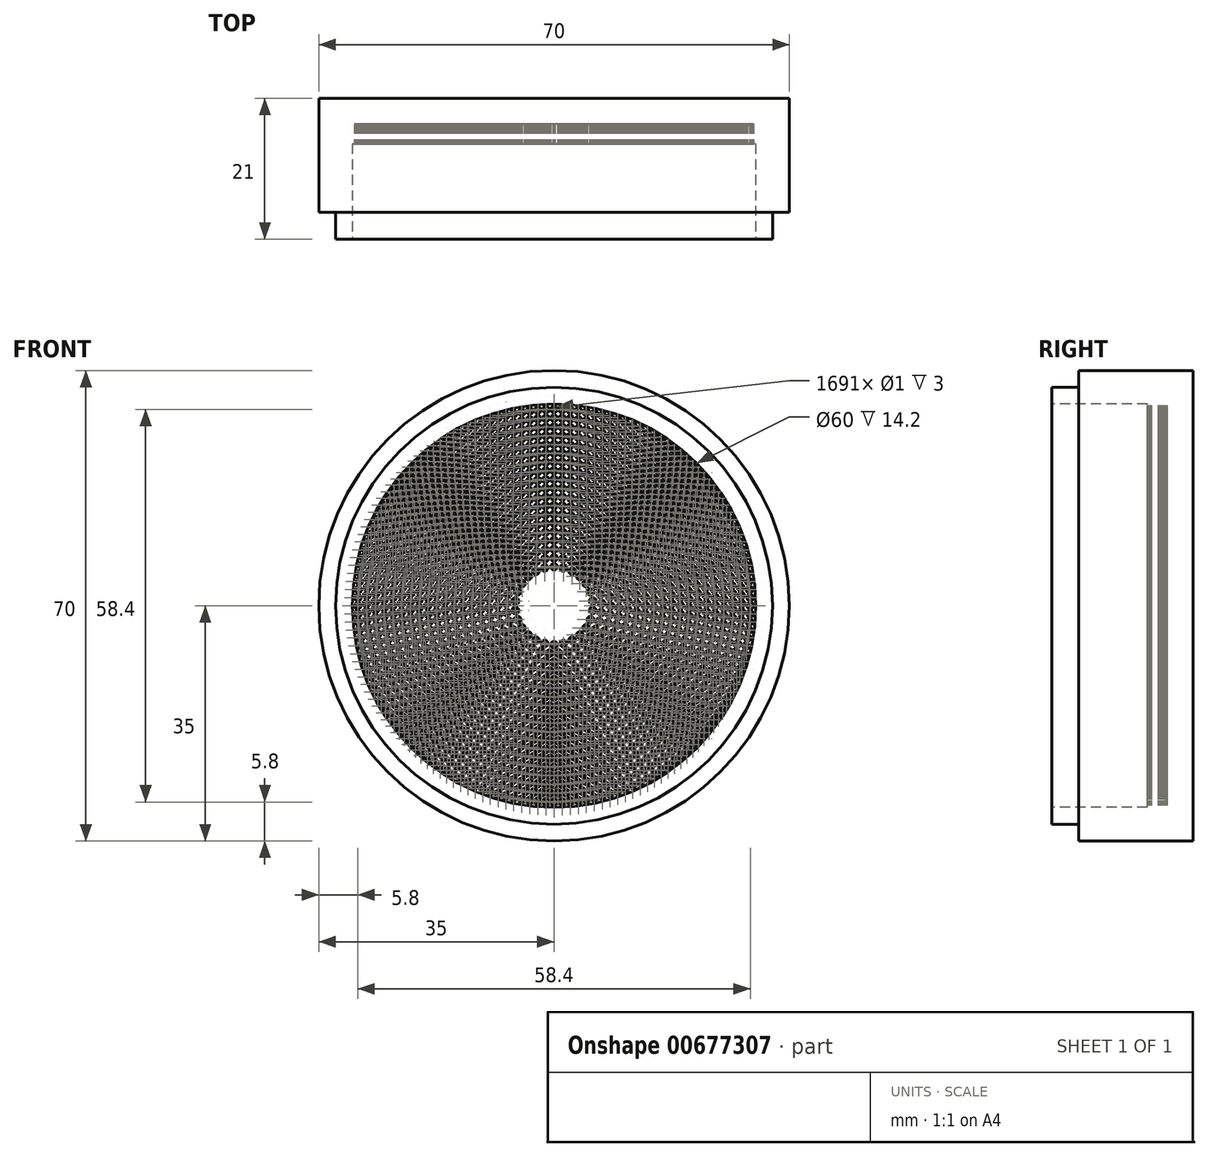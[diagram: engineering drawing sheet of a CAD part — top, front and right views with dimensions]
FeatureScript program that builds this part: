
annotation { "Feature Type Name" : "Feature", "Feature Type Description" : "" }
export const myFeature = defineFeature(function(context is Context, id is Id, definition is map)
    precondition{}
    {
        {
            var Q0;
            Q0=qCreatedBy(makeId("Front.planeOp"),FACE);
            var sketch = newSketch(context, id + "F0", { "sketchPlane" : qUnion([Q0])});
            skCircle(sketch, "E0", {"center": v(0, 0) * mm, "radius": 35 * mm});
            skSolve(sketch);
        }
        {
            var Q0;
            Q0=qSketchRegion(id+"F0",true);
            var Q1;
            Q1=makeQuery(id+"F0.imprint","IMPRINT",FACE,{"disambiguationData":[TD([[makeQuery(id+"F0.imprint","IMPRINT",EDGE,{"derivedFrom":sQuery(id+"F0.wireOp",EDGE,"E0")}),1.0]])]});
            extrude(context, id + "F1", {"entities" : qUnion([Q0, Q1]), "depth" : 21 * mm, "offsetDistance" : 25 * mm});
        }
        {
            var Q0;
            Q0=makeQuery(id+"F1.opExtrude","CAP_FACE",FACE,{"disambiguationData":[OSD([sQuery(id+"F0.wireOp",EDGE,"E0")])],"isStart":false});
            var sketch = newSketch(context, id + "F2", { "sketchPlane" : qUnion([Q0])});
            skCircle(sketch, "E1", {"center": v(0, 0) * mm, "radius": 30 * mm});
            skSolve(sketch);
        }
        {
            var Q0;
            Q0=qSketchRegion(id+"F2",true);
            var Q1;
            Q1=makeQuery(id+"F2.imprint","IMPRINT",FACE,{"disambiguationData":[TD([[makeQuery(id+"F2.imprint","IMPRINT",EDGE,{"derivedFrom":sQuery(id+"F2.wireOp",EDGE,"E1")}),1.0]])]});
            extrude(context, id + "F3", {"entities" : qUnion([Q0, Q1]), "operationType" : NewBodyOperationType.REMOVE, "oppositeDirection" : true, "depth" : 17 * mm, "offsetDistance" : 25 * mm});
        }
        {
            var Q0;
            Q0=makeQuery(id+"F1.opExtrude","CAP_FACE",FACE,{"disambiguationData":[OSD([sQuery(id+"F0.wireOp",EDGE,"E0")])],"isStart":false});
            var sketch = newSketch(context, id + "F4", { "sketchPlane" : qUnion([Q0])});
            skCircle(sketch, "E2", {"center": v(0, 0) * mm, "radius": 32.5 * mm});
            skSolve(sketch);
        }
        {
            var Q0;
            Q0=makeQuery(id+"F4.imprint","IMPRINT",FACE,{"disambiguationData":[TD([[makeQuery(id+"F4.imprint","IMPRINT",EDGE,{"derivedFrom":sQuery(id+"F4.wireOp",EDGE,"E2")}),-1.0]])]});
            extrude(context, id + "F5", {"entities" : qUnion([Q0]), "operationType" : NewBodyOperationType.REMOVE, "oppositeDirection" : true, "depth" : 4 * mm, "offsetDistance" : 25 * mm});
        }
        {
            var Q0;
            Q0=makeQuery(id+"F3.boolean.opBoolean","COPY",FACE,{"derivedFrom":makeQuery(id+"F3.opExtrude","CAP_FACE",FACE,{"disambiguationData":[OSD([sQuery(id+"F2.wireOp",EDGE,"E1")])],"isStart":false})});
            var sketch = newSketch(context, id + "F6", { "sketchPlane" : qUnion([Q0])});
            skLineSegment(sketch, "E3", {"start": v(0, 0) * mm, "end": v(0, 30) * mm, "construction": true});
            skCircle(sketch, "E4", {"center": v(0, 0) * mm, "radius": 5 * mm, "construction": true});
            skCircle(sketch, "E5", {"center": v(0, 5.8) * mm, "radius": 0.1 * mm});
            skLineSegment(sketch, "E6", {"start": v(0, 5) * mm, "end": v(-0.66, 5) * mm, "construction": true});
            skCircle(sketch, "E7", {"center": v(0, 7.1) * mm, "radius": 0.1 * mm});
            skCircle(sketch, "E8", {"center": v(0, 8.4) * mm, "radius": 0.1 * mm});
            skCircle(sketch, "E9", {"center": v(0, 9.7) * mm, "radius": 0.1 * mm});
            skCircle(sketch, "E10", {"center": v(0, 11) * mm, "radius": 0.1 * mm});
            skLineSegment(sketch, "E11", {"start": v(-1.23, 11.65) * mm, "end": v(1.24, 11.65) * mm, "construction": true});
            skCircle(sketch, "E12.MirrorC", {"center": v(0, 12.3) * mm, "radius": 0.1 * mm});
            skCircle(sketch, "E13.MirrorC", {"center": v(0, 13.6) * mm, "radius": 0.1 * mm});
            skCircle(sketch, "E14.MirrorC", {"center": v(0, 14.9) * mm, "radius": 0.1 * mm});
            skCircle(sketch, "E15.MirrorC", {"center": v(0, 16.2) * mm, "radius": 0.1 * mm});
            skCircle(sketch, "E16.MirrorC", {"center": v(0, 17.5) * mm, "radius": 0.1 * mm});
            skLineSegment(sketch, "E17", {"start": v(-0.97, 18.15) * mm, "end": v(1.04, 18.15) * mm, "construction": true});
            skCircle(sketch, "E18.MirrorC", {"center": v(0, 18.8) * mm, "radius": 0.1 * mm});
            skCircle(sketch, "E19.MirrorC", {"center": v(0, 20.1) * mm, "radius": 0.1 * mm});
            skCircle(sketch, "E20.MirrorC", {"center": v(0, 21.4) * mm, "radius": 0.1 * mm});
            skCircle(sketch, "E21.MirrorC", {"center": v(0, 22.7) * mm, "radius": 0.1 * mm});
            skCircle(sketch, "E22.MirrorC", {"center": v(0, 24) * mm, "radius": 0.1 * mm});
            skCircle(sketch, "E23.MirrorC", {"center": v(0, 25.3) * mm, "radius": 0.1 * mm});
            skCircle(sketch, "E24.MirrorC", {"center": v(0, 26.6) * mm, "radius": 0.1 * mm});
            skCircle(sketch, "E25.MirrorC", {"center": v(0, 27.9) * mm, "radius": 0.1 * mm});
            skCircle(sketch, "E26.MirrorC", {"center": v(0, 29.2) * mm, "radius": 0.1 * mm});
            skCircle(sketch, "E27.1.0", {"center": v(-1.39, 5.63) * mm, "radius": 0.1 * mm});
            skCircle(sketch, "E27.2.0", {"center": v(-2.7, 5.14) * mm, "radius": 0.1 * mm});
            skCircle(sketch, "E27.3.0", {"center": v(-3.85, 4.34) * mm, "radius": 0.1 * mm});
            skCircle(sketch, "E27.4.0", {"center": v(-4.77, 3.3) * mm, "radius": 0.1 * mm});
            skCircle(sketch, "E27.5.0", {"center": v(-5.42, 2.06) * mm, "radius": 0.1 * mm});
            skCircle(sketch, "E27.6.0", {"center": v(-5.76, 0.7) * mm, "radius": 0.1 * mm});
            skCircle(sketch, "E27.7.0", {"center": v(-5.76, -0.7) * mm, "radius": 0.1 * mm});
            skCircle(sketch, "E27.8.0", {"center": v(-5.42, -2.06) * mm, "radius": 0.1 * mm});
            skCircle(sketch, "E27.9.0", {"center": v(-4.77, -3.3) * mm, "radius": 0.1 * mm});
            skCircle(sketch, "E27.10.0", {"center": v(-3.85, -4.34) * mm, "radius": 0.1 * mm});
            skCircle(sketch, "E27.11.0", {"center": v(-2.7, -5.14) * mm, "radius": 0.1 * mm});
            skCircle(sketch, "E27.12.0", {"center": v(-1.39, -5.63) * mm, "radius": 0.1 * mm});
            skCircle(sketch, "E27.13.0", {"center": v(0, -5.8) * mm, "radius": 0.1 * mm});
            skCircle(sketch, "E27.14.0", {"center": v(1.39, -5.63) * mm, "radius": 0.1 * mm});
            skCircle(sketch, "E27.15.0", {"center": v(2.7, -5.14) * mm, "radius": 0.1 * mm});
            skCircle(sketch, "E27.16.0", {"center": v(3.85, -4.34) * mm, "radius": 0.1 * mm});
            skCircle(sketch, "E27.17.0", {"center": v(4.77, -3.3) * mm, "radius": 0.1 * mm});
            skCircle(sketch, "E27.18.0", {"center": v(5.42, -2.06) * mm, "radius": 0.1 * mm});
            skCircle(sketch, "E27.19.0", {"center": v(5.76, -0.7) * mm, "radius": 0.1 * mm});
            skCircle(sketch, "E27.20.0", {"center": v(5.76, 0.7) * mm, "radius": 0.1 * mm});
            skCircle(sketch, "E27.21.0", {"center": v(5.42, 2.06) * mm, "radius": 0.1 * mm});
            skCircle(sketch, "E27.22.0", {"center": v(4.77, 3.3) * mm, "radius": 0.1 * mm});
            skCircle(sketch, "E27.23.0", {"center": v(3.85, 4.34) * mm, "radius": 0.1 * mm});
            skCircle(sketch, "E27.24.0", {"center": v(2.7, 5.14) * mm, "radius": 0.1 * mm});
            skCircle(sketch, "E27.25.0", {"center": v(1.39, 5.63) * mm, "radius": 0.1 * mm});
            skCircle(sketch, "E28.1.0", {"center": v(-1.34, 6.97) * mm, "radius": 0.1 * mm});
            skCircle(sketch, "E28.2.0", {"center": v(-2.64, 6.6) * mm, "radius": 0.1 * mm});
            skCircle(sketch, "E28.3.0", {"center": v(-3.84, 5.97) * mm, "radius": 0.1 * mm});
            skCircle(sketch, "E28.4.0", {"center": v(-4.9, 5.14) * mm, "radius": 0.1 * mm});
            skCircle(sketch, "E28.5.0", {"center": v(-5.78, 4.12) * mm, "radius": 0.1 * mm});
            skCircle(sketch, "E28.6.0", {"center": v(-6.46, 2.95) * mm, "radius": 0.1 * mm});
            skCircle(sketch, "E28.7.0", {"center": v(-6.9, 1.67) * mm, "radius": 0.1 * mm});
            skCircle(sketch, "E28.8.0", {"center": v(-7.1, 0.34) * mm, "radius": 0.1 * mm});
            skCircle(sketch, "E28.9.0", {"center": v(-7.03, -1.01) * mm, "radius": 0.1 * mm});
            skCircle(sketch, "E28.10.0", {"center": v(-6.7, -2.32) * mm, "radius": 0.1 * mm});
            skCircle(sketch, "E28.11.0", {"center": v(-6.15, -3.55) * mm, "radius": 0.1 * mm});
            skCircle(sketch, "E28.12.0", {"center": v(-5.37, -4.65) * mm, "radius": 0.1 * mm});
            skCircle(sketch, "E28.13.0", {"center": v(-4.39, -5.58) * mm, "radius": 0.1 * mm});
            skCircle(sketch, "E28.14.0", {"center": v(-3.25, -6.31) * mm, "radius": 0.1 * mm});
            skCircle(sketch, "E28.15.0", {"center": v(-2, -6.81) * mm, "radius": 0.1 * mm});
            skCircle(sketch, "E28.16.0", {"center": v(-0.67, -7.07) * mm, "radius": 0.1 * mm});
            skCircle(sketch, "E28.17.0", {"center": v(0.67, -7.07) * mm, "radius": 0.1 * mm});
            skCircle(sketch, "E28.18.0", {"center": v(2, -6.81) * mm, "radius": 0.1 * mm});
            skCircle(sketch, "E28.19.0", {"center": v(3.25, -6.31) * mm, "radius": 0.1 * mm});
            skCircle(sketch, "E28.20.0", {"center": v(4.39, -5.58) * mm, "radius": 0.1 * mm});
            skCircle(sketch, "E28.21.0", {"center": v(5.37, -4.65) * mm, "radius": 0.1 * mm});
            skCircle(sketch, "E28.22.0", {"center": v(6.15, -3.55) * mm, "radius": 0.1 * mm});
            skCircle(sketch, "E28.23.0", {"center": v(6.7, -2.32) * mm, "radius": 0.1 * mm});
            skCircle(sketch, "E28.24.0", {"center": v(7.03, -1.01) * mm, "radius": 0.1 * mm});
            skCircle(sketch, "E28.25.0", {"center": v(7.1, 0.34) * mm, "radius": 0.1 * mm});
            skCircle(sketch, "E28.26.0", {"center": v(6.9, 1.67) * mm, "radius": 0.1 * mm});
            skCircle(sketch, "E28.27.0", {"center": v(6.46, 2.95) * mm, "radius": 0.1 * mm});
            skCircle(sketch, "E28.28.0", {"center": v(5.78, 4.12) * mm, "radius": 0.1 * mm});
            skCircle(sketch, "E28.29.0", {"center": v(4.9, 5.14) * mm, "radius": 0.1 * mm});
            skCircle(sketch, "E28.30.0", {"center": v(3.84, 5.97) * mm, "radius": 0.1 * mm});
            skCircle(sketch, "E28.31.0", {"center": v(2.64, 6.6) * mm, "radius": 0.1 * mm});
            skCircle(sketch, "E28.32.0", {"center": v(1.34, 6.97) * mm, "radius": 0.1 * mm});
            skCircle(sketch, "E29.1.0", {"center": v(-1.31, 8.3) * mm, "radius": 0.1 * mm});
            skCircle(sketch, "E29.2.0", {"center": v(-2.6, 7.99) * mm, "radius": 0.1 * mm});
            skCircle(sketch, "E29.3.0", {"center": v(-3.81, 7.48) * mm, "radius": 0.1 * mm});
            skCircle(sketch, "E29.4.0", {"center": v(-4.94, 6.8) * mm, "radius": 0.1 * mm});
            skCircle(sketch, "E29.5.0", {"center": v(-5.94, 5.94) * mm, "radius": 0.1 * mm});
            skCircle(sketch, "E29.6.0", {"center": v(-6.8, 4.94) * mm, "radius": 0.1 * mm});
            skCircle(sketch, "E29.7.0", {"center": v(-7.48, 3.81) * mm, "radius": 0.1 * mm});
            skCircle(sketch, "E29.8.0", {"center": v(-7.99, 2.6) * mm, "radius": 0.1 * mm});
            skCircle(sketch, "E29.9.0", {"center": v(-8.3, 1.31) * mm, "radius": 0.1 * mm});
            skCircle(sketch, "E29.10.0", {"center": v(-8.4, 0) * mm, "radius": 0.1 * mm});
            skCircle(sketch, "E29.11.0", {"center": v(-8.3, -1.31) * mm, "radius": 0.1 * mm});
            skCircle(sketch, "E29.12.0", {"center": v(-7.99, -2.6) * mm, "radius": 0.1 * mm});
            skCircle(sketch, "E29.13.0", {"center": v(-7.48, -3.81) * mm, "radius": 0.1 * mm});
            skCircle(sketch, "E29.14.0", {"center": v(-6.8, -4.94) * mm, "radius": 0.1 * mm});
            skCircle(sketch, "E29.15.0", {"center": v(-5.94, -5.94) * mm, "radius": 0.1 * mm});
            skCircle(sketch, "E29.16.0", {"center": v(-4.94, -6.8) * mm, "radius": 0.1 * mm});
            skCircle(sketch, "E29.17.0", {"center": v(-3.81, -7.48) * mm, "radius": 0.1 * mm});
            skCircle(sketch, "E29.18.0", {"center": v(-2.6, -7.99) * mm, "radius": 0.1 * mm});
            skCircle(sketch, "E29.19.0", {"center": v(-1.31, -8.3) * mm, "radius": 0.1 * mm});
            skCircle(sketch, "E29.20.0", {"center": v(0, -8.4) * mm, "radius": 0.1 * mm});
            skCircle(sketch, "E29.21.0", {"center": v(1.31, -8.3) * mm, "radius": 0.1 * mm});
            skCircle(sketch, "E29.22.0", {"center": v(2.6, -7.99) * mm, "radius": 0.1 * mm});
            skCircle(sketch, "E29.23.0", {"center": v(3.81, -7.48) * mm, "radius": 0.1 * mm});
            skCircle(sketch, "E29.24.0", {"center": v(4.94, -6.8) * mm, "radius": 0.1 * mm});
            skCircle(sketch, "E29.25.0", {"center": v(5.94, -5.94) * mm, "radius": 0.1 * mm});
            skCircle(sketch, "E29.26.0", {"center": v(6.8, -4.94) * mm, "radius": 0.1 * mm});
            skCircle(sketch, "E29.27.0", {"center": v(7.48, -3.81) * mm, "radius": 0.1 * mm});
            skCircle(sketch, "E29.28.0", {"center": v(7.99, -2.6) * mm, "radius": 0.1 * mm});
            skCircle(sketch, "E29.29.0", {"center": v(8.3, -1.31) * mm, "radius": 0.1 * mm});
            skCircle(sketch, "E29.30.0", {"center": v(8.4, 0) * mm, "radius": 0.1 * mm});
            skCircle(sketch, "E29.31.0", {"center": v(8.3, 1.31) * mm, "radius": 0.1 * mm});
            skCircle(sketch, "E29.32.0", {"center": v(7.99, 2.6) * mm, "radius": 0.1 * mm});
            skCircle(sketch, "E29.33.0", {"center": v(7.48, 3.81) * mm, "radius": 0.1 * mm});
            skCircle(sketch, "E29.34.0", {"center": v(6.8, 4.94) * mm, "radius": 0.1 * mm});
            skCircle(sketch, "E29.35.0", {"center": v(5.94, 5.94) * mm, "radius": 0.1 * mm});
            skCircle(sketch, "E29.36.0", {"center": v(4.94, 6.8) * mm, "radius": 0.1 * mm});
            skCircle(sketch, "E29.37.0", {"center": v(3.81, 7.48) * mm, "radius": 0.1 * mm});
            skCircle(sketch, "E29.38.0", {"center": v(2.6, 7.99) * mm, "radius": 0.1 * mm});
            skCircle(sketch, "E29.39.0", {"center": v(1.31, 8.3) * mm, "radius": 0.1 * mm});
            skCircle(sketch, "E30.1.0", {"center": v(-1.3, 9.61) * mm, "radius": 0.1 * mm});
            skCircle(sketch, "E30.2.0", {"center": v(-2.56, 9.36) * mm, "radius": 0.1 * mm});
            skCircle(sketch, "E30.3.0", {"center": v(-3.79, 8.93) * mm, "radius": 0.1 * mm});
            skCircle(sketch, "E30.4.0", {"center": v(-4.94, 8.35) * mm, "radius": 0.1 * mm});
            skCircle(sketch, "E30.5.0", {"center": v(-6.01, 7.61) * mm, "radius": 0.1 * mm});
            skCircle(sketch, "E30.6.0", {"center": v(-6.97, 6.74) * mm, "radius": 0.1 * mm});
            skCircle(sketch, "E30.7.0", {"center": v(-7.8, 5.75) * mm, "radius": 0.1 * mm});
            skCircle(sketch, "E30.8.0", {"center": v(-8.5, 4.66) * mm, "radius": 0.1 * mm});
            skCircle(sketch, "E30.9.0", {"center": v(-9.05, 3.49) * mm, "radius": 0.1 * mm});
            skCircle(sketch, "E30.10.0", {"center": v(-9.44, 2.25) * mm, "radius": 0.1 * mm});
            skCircle(sketch, "E30.11.0", {"center": v(-9.65, 0.97) * mm, "radius": 0.1 * mm});
            skCircle(sketch, "E30.12.0", {"center": v(-9.7, -0.32) * mm, "radius": 0.1 * mm});
            skCircle(sketch, "E30.13.0", {"center": v(-9.56, -1.61) * mm, "radius": 0.1 * mm});
            skCircle(sketch, "E30.14.0", {"center": v(-9.26, -2.87) * mm, "radius": 0.1 * mm});
            skCircle(sketch, "E30.15.0", {"center": v(-8.8, -4.08) * mm, "radius": 0.1 * mm});
            skCircle(sketch, "E30.16.0", {"center": v(-8.18, -5.22) * mm, "radius": 0.1 * mm});
            skCircle(sketch, "E30.17.0", {"center": v(-7.4, -6.26) * mm, "radius": 0.1 * mm});
            skCircle(sketch, "E30.18.0", {"center": v(-6.5, -7.2) * mm, "radius": 0.1 * mm});
            skCircle(sketch, "E30.19.0", {"center": v(-5.49, -8) * mm, "radius": 0.1 * mm});
            skCircle(sketch, "E30.20.0", {"center": v(-4.37, -8.66) * mm, "radius": 0.1 * mm});
            skCircle(sketch, "E30.21.0", {"center": v(-3.18, -9.16) * mm, "radius": 0.1 * mm});
            skCircle(sketch, "E30.22.0", {"center": v(-1.93, -9.5) * mm, "radius": 0.1 * mm});
            skCircle(sketch, "E30.23.0", {"center": v(-0.65, -9.68) * mm, "radius": 0.1 * mm});
            skCircle(sketch, "E30.24.0", {"center": v(0.65, -9.68) * mm, "radius": 0.1 * mm});
            skCircle(sketch, "E30.25.0", {"center": v(1.93, -9.5) * mm, "radius": 0.1 * mm});
            skCircle(sketch, "E30.26.0", {"center": v(3.18, -9.16) * mm, "radius": 0.1 * mm});
            skCircle(sketch, "E30.27.0", {"center": v(4.37, -8.66) * mm, "radius": 0.1 * mm});
            skCircle(sketch, "E30.28.0", {"center": v(5.49, -8) * mm, "radius": 0.1 * mm});
            skCircle(sketch, "E30.29.0", {"center": v(6.5, -7.2) * mm, "radius": 0.1 * mm});
            skCircle(sketch, "E30.30.0", {"center": v(7.4, -6.26) * mm, "radius": 0.1 * mm});
            skCircle(sketch, "E30.31.0", {"center": v(8.18, -5.22) * mm, "radius": 0.1 * mm});
            skCircle(sketch, "E30.32.0", {"center": v(8.8, -4.08) * mm, "radius": 0.1 * mm});
            skCircle(sketch, "E30.33.0", {"center": v(9.26, -2.87) * mm, "radius": 0.1 * mm});
            skCircle(sketch, "E30.34.0", {"center": v(9.56, -1.61) * mm, "radius": 0.1 * mm});
            skCircle(sketch, "E30.35.0", {"center": v(9.7, -0.32) * mm, "radius": 0.1 * mm});
            skCircle(sketch, "E30.36.0", {"center": v(9.65, 0.97) * mm, "radius": 0.1 * mm});
            skCircle(sketch, "E30.37.0", {"center": v(9.44, 2.25) * mm, "radius": 0.1 * mm});
            skCircle(sketch, "E30.38.0", {"center": v(9.05, 3.49) * mm, "radius": 0.1 * mm});
            skCircle(sketch, "E30.39.0", {"center": v(8.5, 4.66) * mm, "radius": 0.1 * mm});
            skCircle(sketch, "E30.40.0", {"center": v(7.8, 5.75) * mm, "radius": 0.1 * mm});
            skCircle(sketch, "E30.41.0", {"center": v(6.97, 6.74) * mm, "radius": 0.1 * mm});
            skCircle(sketch, "E30.42.0", {"center": v(6.01, 7.61) * mm, "radius": 0.1 * mm});
            skCircle(sketch, "E30.43.0", {"center": v(4.94, 8.35) * mm, "radius": 0.1 * mm});
            skCircle(sketch, "E30.44.0", {"center": v(3.79, 8.93) * mm, "radius": 0.1 * mm});
            skCircle(sketch, "E30.45.0", {"center": v(2.56, 9.36) * mm, "radius": 0.1 * mm});
            skCircle(sketch, "E30.46.0", {"center": v(1.3, 9.61) * mm, "radius": 0.1 * mm});
            skCircle(sketch, "E31.1.0", {"center": v(-1.28, 10.93) * mm, "radius": 0.1 * mm});
            skCircle(sketch, "E31.2.0", {"center": v(-2.54, 10.7) * mm, "radius": 0.1 * mm});
            skCircle(sketch, "E31.3.0", {"center": v(-3.76, 10.34) * mm, "radius": 0.1 * mm});
            skCircle(sketch, "E31.4.0", {"center": v(-4.94, 9.83) * mm, "radius": 0.1 * mm});
            skCircle(sketch, "E31.5.0", {"center": v(-6.04, 9.2) * mm, "radius": 0.1 * mm});
            skCircle(sketch, "E31.6.0", {"center": v(-7.07, 8.43) * mm, "radius": 0.1 * mm});
            skCircle(sketch, "E31.7.0", {"center": v(-8, 7.55) * mm, "radius": 0.1 * mm});
            skCircle(sketch, "E31.8.0", {"center": v(-8.82, 6.57) * mm, "radius": 0.1 * mm});
            skCircle(sketch, "E31.9.0", {"center": v(-9.53, 5.5) * mm, "radius": 0.1 * mm});
            skCircle(sketch, "E31.10.0", {"center": v(-10.1, 4.36) * mm, "radius": 0.1 * mm});
            skCircle(sketch, "E31.11.0", {"center": v(-10.54, 3.15) * mm, "radius": 0.1 * mm});
            skCircle(sketch, "E31.12.0", {"center": v(-10.83, 1.91) * mm, "radius": 0.1 * mm});
            skCircle(sketch, "E31.13.0", {"center": v(-10.98, 0.64) * mm, "radius": 0.1 * mm});
            skCircle(sketch, "E31.14.0", {"center": v(-10.98, -0.64) * mm, "radius": 0.1 * mm});
            skCircle(sketch, "E31.15.0", {"center": v(-10.83, -1.91) * mm, "radius": 0.1 * mm});
            skCircle(sketch, "E31.16.0", {"center": v(-10.54, -3.15) * mm, "radius": 0.1 * mm});
            skCircle(sketch, "E31.17.0", {"center": v(-10.1, -4.36) * mm, "radius": 0.1 * mm});
            skCircle(sketch, "E31.18.0", {"center": v(-9.53, -5.5) * mm, "radius": 0.1 * mm});
            skCircle(sketch, "E31.19.0", {"center": v(-8.82, -6.57) * mm, "radius": 0.1 * mm});
            skCircle(sketch, "E31.20.0", {"center": v(-8, -7.55) * mm, "radius": 0.1 * mm});
            skCircle(sketch, "E31.21.0", {"center": v(-7.07, -8.43) * mm, "radius": 0.1 * mm});
            skCircle(sketch, "E31.22.0", {"center": v(-6.04, -9.2) * mm, "radius": 0.1 * mm});
            skCircle(sketch, "E31.23.0", {"center": v(-4.94, -9.83) * mm, "radius": 0.1 * mm});
            skCircle(sketch, "E31.24.0", {"center": v(-3.76, -10.34) * mm, "radius": 0.1 * mm});
            skCircle(sketch, "E31.25.0", {"center": v(-2.54, -10.7) * mm, "radius": 0.1 * mm});
            skCircle(sketch, "E31.26.0", {"center": v(-1.28, -10.93) * mm, "radius": 0.1 * mm});
            skCircle(sketch, "E31.27.0", {"center": v(0, -11) * mm, "radius": 0.1 * mm});
            skCircle(sketch, "E31.28.0", {"center": v(1.28, -10.93) * mm, "radius": 0.1 * mm});
            skCircle(sketch, "E31.29.0", {"center": v(2.54, -10.7) * mm, "radius": 0.1 * mm});
            skCircle(sketch, "E31.30.0", {"center": v(3.76, -10.34) * mm, "radius": 0.1 * mm});
            skCircle(sketch, "E31.31.0", {"center": v(4.94, -9.83) * mm, "radius": 0.1 * mm});
            skCircle(sketch, "E31.32.0", {"center": v(6.04, -9.2) * mm, "radius": 0.1 * mm});
            skCircle(sketch, "E31.33.0", {"center": v(7.07, -8.43) * mm, "radius": 0.1 * mm});
            skCircle(sketch, "E31.34.0", {"center": v(8, -7.55) * mm, "radius": 0.1 * mm});
            skCircle(sketch, "E31.35.0", {"center": v(8.82, -6.57) * mm, "radius": 0.1 * mm});
            skCircle(sketch, "E31.36.0", {"center": v(9.53, -5.5) * mm, "radius": 0.1 * mm});
            skCircle(sketch, "E31.37.0", {"center": v(10.1, -4.36) * mm, "radius": 0.1 * mm});
            skCircle(sketch, "E31.38.0", {"center": v(10.54, -3.15) * mm, "radius": 0.1 * mm});
            skCircle(sketch, "E31.39.0", {"center": v(10.83, -1.91) * mm, "radius": 0.1 * mm});
            skCircle(sketch, "E31.40.0", {"center": v(10.98, -0.64) * mm, "radius": 0.1 * mm});
            skCircle(sketch, "E31.41.0", {"center": v(10.98, 0.64) * mm, "radius": 0.1 * mm});
            skCircle(sketch, "E31.42.0", {"center": v(10.83, 1.91) * mm, "radius": 0.1 * mm});
            skCircle(sketch, "E31.43.0", {"center": v(10.54, 3.15) * mm, "radius": 0.1 * mm});
            skCircle(sketch, "E31.44.0", {"center": v(10.1, 4.36) * mm, "radius": 0.1 * mm});
            skCircle(sketch, "E31.45.0", {"center": v(9.53, 5.5) * mm, "radius": 0.1 * mm});
            skCircle(sketch, "E31.46.0", {"center": v(8.82, 6.57) * mm, "radius": 0.1 * mm});
            skCircle(sketch, "E31.47.0", {"center": v(8, 7.55) * mm, "radius": 0.1 * mm});
            skCircle(sketch, "E31.48.0", {"center": v(7.07, 8.43) * mm, "radius": 0.1 * mm});
            skCircle(sketch, "E31.49.0", {"center": v(6.04, 9.2) * mm, "radius": 0.1 * mm});
            skCircle(sketch, "E31.50.0", {"center": v(4.94, 9.83) * mm, "radius": 0.1 * mm});
            skCircle(sketch, "E31.51.0", {"center": v(3.76, 10.34) * mm, "radius": 0.1 * mm});
            skCircle(sketch, "E31.52.0", {"center": v(2.54, 10.7) * mm, "radius": 0.1 * mm});
            skCircle(sketch, "E31.53.0", {"center": v(1.28, 10.93) * mm, "radius": 0.1 * mm});
            skCircle(sketch, "E32.1.0", {"center": v(-1.26, 12.23) * mm, "radius": 0.1 * mm});
            skCircle(sketch, "E32.2.0", {"center": v(-2.52, 12.04) * mm, "radius": 0.1 * mm});
            skCircle(sketch, "E32.3.0", {"center": v(-3.74, 11.72) * mm, "radius": 0.1 * mm});
            skCircle(sketch, "E32.4.0", {"center": v(-4.93, 11.27) * mm, "radius": 0.1 * mm});
            skCircle(sketch, "E32.5.0", {"center": v(-6.06, 10.7) * mm, "radius": 0.1 * mm});
            skCircle(sketch, "E32.6.0", {"center": v(-7.13, 10.02) * mm, "radius": 0.1 * mm});
            skCircle(sketch, "E32.7.0", {"center": v(-8.12, 9.24) * mm, "radius": 0.1 * mm});
            skCircle(sketch, "E32.8.0", {"center": v(-9.03, 8.36) * mm, "radius": 0.1 * mm});
            skCircle(sketch, "E32.9.0", {"center": v(-9.84, 7.38) * mm, "radius": 0.1 * mm});
            skCircle(sketch, "E32.10.0", {"center": v(-10.54, 6.33) * mm, "radius": 0.1 * mm});
            skCircle(sketch, "E32.11.0", {"center": v(-11.14, 5.21) * mm, "radius": 0.1 * mm});
            skCircle(sketch, "E32.12.0", {"center": v(-11.62, 4.04) * mm, "radius": 0.1 * mm});
            skCircle(sketch, "E32.13.0", {"center": v(-11.97, 2.83) * mm, "radius": 0.1 * mm});
            skCircle(sketch, "E32.14.0", {"center": v(-12.2, 1.58) * mm, "radius": 0.1 * mm});
            skCircle(sketch, "E32.15.0", {"center": v(-12.3, 0.32) * mm, "radius": 0.1 * mm});
            skCircle(sketch, "E32.16.0", {"center": v(-12.26, -0.95) * mm, "radius": 0.1 * mm});
            skCircle(sketch, "E32.17.0", {"center": v(-12.1, -2.2) * mm, "radius": 0.1 * mm});
            skCircle(sketch, "E32.18.0", {"center": v(-11.8, -3.44) * mm, "radius": 0.1 * mm});
            skCircle(sketch, "E32.19.0", {"center": v(-11.4, -4.63) * mm, "radius": 0.1 * mm});
            skCircle(sketch, "E32.20.0", {"center": v(-10.86, -5.78) * mm, "radius": 0.1 * mm});
            skCircle(sketch, "E32.21.0", {"center": v(-10.2, -6.87) * mm, "radius": 0.1 * mm});
            skCircle(sketch, "E32.22.0", {"center": v(-9.44, -7.88) * mm, "radius": 0.1 * mm});
            skCircle(sketch, "E32.23.0", {"center": v(-8.58, -8.8) * mm, "radius": 0.1 * mm});
            skCircle(sketch, "E32.24.0", {"center": v(-7.63, -9.64) * mm, "radius": 0.1 * mm});
            skCircle(sketch, "E32.25.0", {"center": v(-6.6, -10.38) * mm, "radius": 0.1 * mm});
            skCircle(sketch, "E32.26.0", {"center": v(-5.5, -11) * mm, "radius": 0.1 * mm});
            skCircle(sketch, "E32.27.0", {"center": v(-4.34, -11.5) * mm, "radius": 0.1 * mm});
            skCircle(sketch, "E32.28.0", {"center": v(-3.13, -11.9) * mm, "radius": 0.1 * mm});
            skCircle(sketch, "E32.29.0", {"center": v(-1.9, -12.15) * mm, "radius": 0.1 * mm});
            skCircle(sketch, "E32.30.0", {"center": v(-0.63, -12.28) * mm, "radius": 0.1 * mm});
            skCircle(sketch, "E32.31.0", {"center": v(0.63, -12.28) * mm, "radius": 0.1 * mm});
            skCircle(sketch, "E32.32.0", {"center": v(1.9, -12.15) * mm, "radius": 0.1 * mm});
            skCircle(sketch, "E32.33.0", {"center": v(3.13, -11.9) * mm, "radius": 0.1 * mm});
            skCircle(sketch, "E32.34.0", {"center": v(4.34, -11.5) * mm, "radius": 0.1 * mm});
            skCircle(sketch, "E32.35.0", {"center": v(5.5, -11) * mm, "radius": 0.1 * mm});
            skCircle(sketch, "E32.36.0", {"center": v(6.6, -10.38) * mm, "radius": 0.1 * mm});
            skCircle(sketch, "E32.37.0", {"center": v(7.63, -9.64) * mm, "radius": 0.1 * mm});
            skCircle(sketch, "E32.38.0", {"center": v(8.58, -8.8) * mm, "radius": 0.1 * mm});
            skCircle(sketch, "E32.39.0", {"center": v(9.44, -7.88) * mm, "radius": 0.1 * mm});
            skCircle(sketch, "E32.40.0", {"center": v(10.2, -6.87) * mm, "radius": 0.1 * mm});
            skCircle(sketch, "E32.41.0", {"center": v(10.86, -5.78) * mm, "radius": 0.1 * mm});
            skCircle(sketch, "E32.42.0", {"center": v(11.4, -4.63) * mm, "radius": 0.1 * mm});
            skCircle(sketch, "E32.43.0", {"center": v(11.8, -3.44) * mm, "radius": 0.1 * mm});
            skCircle(sketch, "E32.44.0", {"center": v(12.1, -2.2) * mm, "radius": 0.1 * mm});
            skCircle(sketch, "E32.45.0", {"center": v(12.26, -0.95) * mm, "radius": 0.1 * mm});
            skCircle(sketch, "E32.46.0", {"center": v(12.3, 0.32) * mm, "radius": 0.1 * mm});
            skCircle(sketch, "E32.47.0", {"center": v(12.2, 1.58) * mm, "radius": 0.1 * mm});
            skCircle(sketch, "E32.48.0", {"center": v(11.97, 2.83) * mm, "radius": 0.1 * mm});
            skCircle(sketch, "E32.49.0", {"center": v(11.62, 4.04) * mm, "radius": 0.1 * mm});
            skCircle(sketch, "E32.50.0", {"center": v(11.14, 5.21) * mm, "radius": 0.1 * mm});
            skCircle(sketch, "E32.51.0", {"center": v(10.54, 6.33) * mm, "radius": 0.1 * mm});
            skCircle(sketch, "E32.52.0", {"center": v(9.84, 7.38) * mm, "radius": 0.1 * mm});
            skCircle(sketch, "E32.53.0", {"center": v(9.03, 8.36) * mm, "radius": 0.1 * mm});
            skCircle(sketch, "E32.54.0", {"center": v(8.12, 9.24) * mm, "radius": 0.1 * mm});
            skCircle(sketch, "E32.55.0", {"center": v(7.13, 10.02) * mm, "radius": 0.1 * mm});
            skCircle(sketch, "E32.56.0", {"center": v(6.06, 10.7) * mm, "radius": 0.1 * mm});
            skCircle(sketch, "E32.57.0", {"center": v(4.93, 11.27) * mm, "radius": 0.1 * mm});
            skCircle(sketch, "E32.58.0", {"center": v(3.74, 11.72) * mm, "radius": 0.1 * mm});
            skCircle(sketch, "E32.59.0", {"center": v(2.52, 12.04) * mm, "radius": 0.1 * mm});
            skCircle(sketch, "E32.60.0", {"center": v(1.26, 12.23) * mm, "radius": 0.1 * mm});
            skCircle(sketch, "E33.1.0", {"center": v(-1.25, 13.54) * mm, "radius": 0.1 * mm});
            skCircle(sketch, "E33.2.0", {"center": v(-2.5, 13.37) * mm, "radius": 0.1 * mm});
            skCircle(sketch, "E33.3.0", {"center": v(-3.72, 13.08) * mm, "radius": 0.1 * mm});
            skCircle(sketch, "E33.4.0", {"center": v(-4.91, 12.68) * mm, "radius": 0.1 * mm});
            skCircle(sketch, "E33.5.0", {"center": v(-6.06, 12.17) * mm, "radius": 0.1 * mm});
            skCircle(sketch, "E33.6.0", {"center": v(-7.16, 11.56) * mm, "radius": 0.1 * mm});
            skCircle(sketch, "E33.7.0", {"center": v(-8.2, 10.85) * mm, "radius": 0.1 * mm});
            skCircle(sketch, "E33.8.0", {"center": v(-9.16, 10.05) * mm, "radius": 0.1 * mm});
            skCircle(sketch, "E33.9.0", {"center": v(-10.05, 9.16) * mm, "radius": 0.1 * mm});
            skCircle(sketch, "E33.10.0", {"center": v(-10.85, 8.2) * mm, "radius": 0.1 * mm});
            skCircle(sketch, "E33.11.0", {"center": v(-11.56, 7.16) * mm, "radius": 0.1 * mm});
            skCircle(sketch, "E33.12.0", {"center": v(-12.17, 6.06) * mm, "radius": 0.1 * mm});
            skCircle(sketch, "E33.13.0", {"center": v(-12.68, 4.91) * mm, "radius": 0.1 * mm});
            skCircle(sketch, "E33.14.0", {"center": v(-13.08, 3.72) * mm, "radius": 0.1 * mm});
            skCircle(sketch, "E33.15.0", {"center": v(-13.37, 2.5) * mm, "radius": 0.1 * mm});
            skCircle(sketch, "E33.16.0", {"center": v(-13.54, 1.25) * mm, "radius": 0.1 * mm});
            skCircle(sketch, "E33.17.0", {"center": v(-13.6, 0) * mm, "radius": 0.1 * mm});
            skCircle(sketch, "E33.18.0", {"center": v(-13.54, -1.25) * mm, "radius": 0.1 * mm});
            skCircle(sketch, "E33.19.0", {"center": v(-13.37, -2.5) * mm, "radius": 0.1 * mm});
            skCircle(sketch, "E33.20.0", {"center": v(-13.08, -3.72) * mm, "radius": 0.1 * mm});
            skCircle(sketch, "E33.21.0", {"center": v(-12.68, -4.91) * mm, "radius": 0.1 * mm});
            skCircle(sketch, "E33.22.0", {"center": v(-12.17, -6.06) * mm, "radius": 0.1 * mm});
            skCircle(sketch, "E33.23.0", {"center": v(-11.56, -7.16) * mm, "radius": 0.1 * mm});
            skCircle(sketch, "E33.24.0", {"center": v(-10.85, -8.2) * mm, "radius": 0.1 * mm});
            skCircle(sketch, "E33.25.0", {"center": v(-10.05, -9.16) * mm, "radius": 0.1 * mm});
            skCircle(sketch, "E33.26.0", {"center": v(-9.16, -10.05) * mm, "radius": 0.1 * mm});
            skCircle(sketch, "E33.27.0", {"center": v(-8.2, -10.85) * mm, "radius": 0.1 * mm});
            skCircle(sketch, "E33.28.0", {"center": v(-7.16, -11.56) * mm, "radius": 0.1 * mm});
            skCircle(sketch, "E33.29.0", {"center": v(-6.06, -12.17) * mm, "radius": 0.1 * mm});
            skCircle(sketch, "E33.30.0", {"center": v(-4.91, -12.68) * mm, "radius": 0.1 * mm});
            skCircle(sketch, "E33.31.0", {"center": v(-3.72, -13.08) * mm, "radius": 0.1 * mm});
            skCircle(sketch, "E33.32.0", {"center": v(-2.5, -13.37) * mm, "radius": 0.1 * mm});
            skCircle(sketch, "E33.33.0", {"center": v(-1.25, -13.54) * mm, "radius": 0.1 * mm});
            skCircle(sketch, "E33.34.0", {"center": v(0, -13.6) * mm, "radius": 0.1 * mm});
            skCircle(sketch, "E33.35.0", {"center": v(1.25, -13.54) * mm, "radius": 0.1 * mm});
            skCircle(sketch, "E33.36.0", {"center": v(2.5, -13.37) * mm, "radius": 0.1 * mm});
            skCircle(sketch, "E33.37.0", {"center": v(3.72, -13.08) * mm, "radius": 0.1 * mm});
            skCircle(sketch, "E33.38.0", {"center": v(4.91, -12.68) * mm, "radius": 0.1 * mm});
            skCircle(sketch, "E33.39.0", {"center": v(6.06, -12.17) * mm, "radius": 0.1 * mm});
            skCircle(sketch, "E33.40.0", {"center": v(7.16, -11.56) * mm, "radius": 0.1 * mm});
            skCircle(sketch, "E33.41.0", {"center": v(8.2, -10.85) * mm, "radius": 0.1 * mm});
            skCircle(sketch, "E33.42.0", {"center": v(9.16, -10.05) * mm, "radius": 0.1 * mm});
            skCircle(sketch, "E33.43.0", {"center": v(10.05, -9.16) * mm, "radius": 0.1 * mm});
            skCircle(sketch, "E33.44.0", {"center": v(10.85, -8.2) * mm, "radius": 0.1 * mm});
            skCircle(sketch, "E33.45.0", {"center": v(11.56, -7.16) * mm, "radius": 0.1 * mm});
            skCircle(sketch, "E33.46.0", {"center": v(12.17, -6.06) * mm, "radius": 0.1 * mm});
            skCircle(sketch, "E33.47.0", {"center": v(12.68, -4.91) * mm, "radius": 0.1 * mm});
            skCircle(sketch, "E33.48.0", {"center": v(13.08, -3.72) * mm, "radius": 0.1 * mm});
            skCircle(sketch, "E33.49.0", {"center": v(13.37, -2.5) * mm, "radius": 0.1 * mm});
            skCircle(sketch, "E33.50.0", {"center": v(13.54, -1.25) * mm, "radius": 0.1 * mm});
            skCircle(sketch, "E33.51.0", {"center": v(13.6, 0) * mm, "radius": 0.1 * mm});
            skCircle(sketch, "E33.52.0", {"center": v(13.54, 1.25) * mm, "radius": 0.1 * mm});
            skCircle(sketch, "E33.53.0", {"center": v(13.37, 2.5) * mm, "radius": 0.1 * mm});
            skCircle(sketch, "E33.54.0", {"center": v(13.08, 3.72) * mm, "radius": 0.1 * mm});
            skCircle(sketch, "E33.55.0", {"center": v(12.68, 4.91) * mm, "radius": 0.1 * mm});
            skCircle(sketch, "E33.56.0", {"center": v(12.17, 6.06) * mm, "radius": 0.1 * mm});
            skCircle(sketch, "E33.57.0", {"center": v(11.56, 7.16) * mm, "radius": 0.1 * mm});
            skCircle(sketch, "E33.58.0", {"center": v(10.85, 8.2) * mm, "radius": 0.1 * mm});
            skCircle(sketch, "E33.59.0", {"center": v(10.05, 9.16) * mm, "radius": 0.1 * mm});
            skCircle(sketch, "E33.60.0", {"center": v(9.16, 10.05) * mm, "radius": 0.1 * mm});
            skCircle(sketch, "E33.61.0", {"center": v(8.2, 10.85) * mm, "radius": 0.1 * mm});
            skCircle(sketch, "E33.62.0", {"center": v(7.16, 11.56) * mm, "radius": 0.1 * mm});
            skCircle(sketch, "E33.63.0", {"center": v(6.06, 12.17) * mm, "radius": 0.1 * mm});
            skCircle(sketch, "E33.64.0", {"center": v(4.91, 12.68) * mm, "radius": 0.1 * mm});
            skCircle(sketch, "E33.65.0", {"center": v(3.72, 13.08) * mm, "radius": 0.1 * mm});
            skCircle(sketch, "E33.66.0", {"center": v(2.5, 13.37) * mm, "radius": 0.1 * mm});
            skCircle(sketch, "E33.67.0", {"center": v(1.25, 13.54) * mm, "radius": 0.1 * mm});
            skCircle(sketch, "E34.1.0", {"center": v(-1.25, 14.85) * mm, "radius": 0.1 * mm});
            skCircle(sketch, "E34.2.0", {"center": v(-2.48, 14.7) * mm, "radius": 0.1 * mm});
            skCircle(sketch, "E34.3.0", {"center": v(-3.7, 14.43) * mm, "radius": 0.1 * mm});
            skCircle(sketch, "E34.4.0", {"center": v(-4.9, 14.07) * mm, "radius": 0.1 * mm});
            skCircle(sketch, "E34.5.0", {"center": v(-6.06, 13.61) * mm, "radius": 0.1 * mm});
            skCircle(sketch, "E34.6.0", {"center": v(-7.18, 13.06) * mm, "radius": 0.1 * mm});
            skCircle(sketch, "E34.7.0", {"center": v(-8.25, 12.41) * mm, "radius": 0.1 * mm});
            skCircle(sketch, "E34.8.0", {"center": v(-9.26, 11.68) * mm, "radius": 0.1 * mm});
            skCircle(sketch, "E34.9.0", {"center": v(-10.2, 10.86) * mm, "radius": 0.1 * mm});
            skCircle(sketch, "E34.10.0", {"center": v(-11.07, 9.97) * mm, "radius": 0.1 * mm});
            skCircle(sketch, "E34.11.0", {"center": v(-11.87, 9) * mm, "radius": 0.1 * mm});
            skCircle(sketch, "E34.12.0", {"center": v(-12.58, 7.98) * mm, "radius": 0.1 * mm});
            skCircle(sketch, "E34.13.0", {"center": v(-13.2, 6.9) * mm, "radius": 0.1 * mm});
            skCircle(sketch, "E34.14.0", {"center": v(-13.74, 5.77) * mm, "radius": 0.1 * mm});
            skCircle(sketch, "E34.15.0", {"center": v(-14.17, 4.6) * mm, "radius": 0.1 * mm});
            skCircle(sketch, "E34.16.0", {"center": v(-14.5, 3.4) * mm, "radius": 0.1 * mm});
            skCircle(sketch, "E34.17.0", {"center": v(-14.74, 2.18) * mm, "radius": 0.1 * mm});
            skCircle(sketch, "E34.18.0", {"center": v(-14.87, 0.94) * mm, "radius": 0.1 * mm});
            skCircle(sketch, "E34.19.0", {"center": v(-14.9, -0.31) * mm, "radius": 0.1 * mm});
            skCircle(sketch, "E34.20.0", {"center": v(-14.82, -1.56) * mm, "radius": 0.1 * mm});
            skCircle(sketch, "E34.21.0", {"center": v(-14.64, -2.8) * mm, "radius": 0.1 * mm});
            skCircle(sketch, "E34.22.0", {"center": v(-14.35, -4) * mm, "radius": 0.1 * mm});
            skCircle(sketch, "E34.23.0", {"center": v(-13.97, -5.2) * mm, "radius": 0.1 * mm});
            skCircle(sketch, "E34.24.0", {"center": v(-13.48, -6.34) * mm, "radius": 0.1 * mm});
            skCircle(sketch, "E34.25.0", {"center": v(-12.9, -7.45) * mm, "radius": 0.1 * mm});
            skCircle(sketch, "E34.26.0", {"center": v(-12.24, -8.5) * mm, "radius": 0.1 * mm});
            skCircle(sketch, "E34.27.0", {"center": v(-11.48, -9.5) * mm, "radius": 0.1 * mm});
            skCircle(sketch, "E34.28.0", {"center": v(-10.65, -10.42) * mm, "radius": 0.1 * mm});
            skCircle(sketch, "E34.29.0", {"center": v(-9.74, -11.28) * mm, "radius": 0.1 * mm});
            skCircle(sketch, "E34.30.0", {"center": v(-8.76, -12.05) * mm, "radius": 0.1 * mm});
            skCircle(sketch, "E34.31.0", {"center": v(-7.72, -12.74) * mm, "radius": 0.1 * mm});
            skCircle(sketch, "E34.32.0", {"center": v(-6.63, -13.35) * mm, "radius": 0.1 * mm});
            skCircle(sketch, "E34.33.0", {"center": v(-5.49, -13.85) * mm, "radius": 0.1 * mm});
            skCircle(sketch, "E34.34.0", {"center": v(-4.3, -14.26) * mm, "radius": 0.1 * mm});
            skCircle(sketch, "E34.35.0", {"center": v(-3.1, -14.57) * mm, "radius": 0.1 * mm});
            skCircle(sketch, "E34.36.0", {"center": v(-1.87, -14.78) * mm, "radius": 0.1 * mm});
            skCircle(sketch, "E34.37.0", {"center": v(-0.62, -14.89) * mm, "radius": 0.1 * mm});
            skCircle(sketch, "E34.38.0", {"center": v(0.62, -14.89) * mm, "radius": 0.1 * mm});
            skCircle(sketch, "E34.39.0", {"center": v(1.87, -14.78) * mm, "radius": 0.1 * mm});
            skCircle(sketch, "E34.40.0", {"center": v(3.1, -14.57) * mm, "radius": 0.1 * mm});
            skCircle(sketch, "E34.41.0", {"center": v(4.3, -14.26) * mm, "radius": 0.1 * mm});
            skCircle(sketch, "E34.42.0", {"center": v(5.49, -13.85) * mm, "radius": 0.1 * mm});
            skCircle(sketch, "E34.43.0", {"center": v(6.63, -13.35) * mm, "radius": 0.1 * mm});
            skCircle(sketch, "E34.44.0", {"center": v(7.72, -12.74) * mm, "radius": 0.1 * mm});
            skCircle(sketch, "E34.45.0", {"center": v(8.76, -12.05) * mm, "radius": 0.1 * mm});
            skCircle(sketch, "E34.46.0", {"center": v(9.74, -11.28) * mm, "radius": 0.1 * mm});
            skCircle(sketch, "E34.47.0", {"center": v(10.65, -10.42) * mm, "radius": 0.1 * mm});
            skCircle(sketch, "E34.48.0", {"center": v(11.48, -9.5) * mm, "radius": 0.1 * mm});
            skCircle(sketch, "E34.49.0", {"center": v(12.24, -8.5) * mm, "radius": 0.1 * mm});
            skCircle(sketch, "E34.50.0", {"center": v(12.9, -7.45) * mm, "radius": 0.1 * mm});
            skCircle(sketch, "E34.51.0", {"center": v(13.48, -6.34) * mm, "radius": 0.1 * mm});
            skCircle(sketch, "E34.52.0", {"center": v(13.97, -5.2) * mm, "radius": 0.1 * mm});
            skCircle(sketch, "E34.53.0", {"center": v(14.35, -4) * mm, "radius": 0.1 * mm});
            skCircle(sketch, "E34.54.0", {"center": v(14.64, -2.8) * mm, "radius": 0.1 * mm});
            skCircle(sketch, "E34.55.0", {"center": v(14.82, -1.56) * mm, "radius": 0.1 * mm});
            skCircle(sketch, "E34.56.0", {"center": v(14.9, -0.31) * mm, "radius": 0.1 * mm});
            skCircle(sketch, "E34.57.0", {"center": v(14.87, 0.94) * mm, "radius": 0.1 * mm});
            skCircle(sketch, "E34.58.0", {"center": v(14.74, 2.18) * mm, "radius": 0.1 * mm});
            skCircle(sketch, "E34.59.0", {"center": v(14.5, 3.4) * mm, "radius": 0.1 * mm});
            skCircle(sketch, "E34.60.0", {"center": v(14.17, 4.6) * mm, "radius": 0.1 * mm});
            skCircle(sketch, "E34.61.0", {"center": v(13.74, 5.77) * mm, "radius": 0.1 * mm});
            skCircle(sketch, "E34.62.0", {"center": v(13.2, 6.9) * mm, "radius": 0.1 * mm});
            skCircle(sketch, "E34.63.0", {"center": v(12.58, 7.98) * mm, "radius": 0.1 * mm});
            skCircle(sketch, "E34.64.0", {"center": v(11.87, 9) * mm, "radius": 0.1 * mm});
            skCircle(sketch, "E34.65.0", {"center": v(11.07, 9.97) * mm, "radius": 0.1 * mm});
            skCircle(sketch, "E34.66.0", {"center": v(10.2, 10.86) * mm, "radius": 0.1 * mm});
            skCircle(sketch, "E34.67.0", {"center": v(9.26, 11.68) * mm, "radius": 0.1 * mm});
            skCircle(sketch, "E34.68.0", {"center": v(8.25, 12.41) * mm, "radius": 0.1 * mm});
            skCircle(sketch, "E34.69.0", {"center": v(7.18, 13.06) * mm, "radius": 0.1 * mm});
            skCircle(sketch, "E34.70.0", {"center": v(6.06, 13.61) * mm, "radius": 0.1 * mm});
            skCircle(sketch, "E34.71.0", {"center": v(4.9, 14.07) * mm, "radius": 0.1 * mm});
            skCircle(sketch, "E34.72.0", {"center": v(3.7, 14.43) * mm, "radius": 0.1 * mm});
            skCircle(sketch, "E34.73.0", {"center": v(2.48, 14.7) * mm, "radius": 0.1 * mm});
            skCircle(sketch, "E34.74.0", {"center": v(1.25, 14.85) * mm, "radius": 0.1 * mm});
            skCircle(sketch, "E35.1.0", {"center": v(-1.24, 16.15) * mm, "radius": 0.1 * mm});
            skCircle(sketch, "E35.2.0", {"center": v(-2.47, 16.01) * mm, "radius": 0.1 * mm});
            skCircle(sketch, "E35.3.0", {"center": v(-3.7, 15.77) * mm, "radius": 0.1 * mm});
            skCircle(sketch, "E35.4.0", {"center": v(-4.89, 15.45) * mm, "radius": 0.1 * mm});
            skCircle(sketch, "E35.5.0", {"center": v(-6.06, 15.03) * mm, "radius": 0.1 * mm});
            skCircle(sketch, "E35.6.0", {"center": v(-7.19, 14.52) * mm, "radius": 0.1 * mm});
            skCircle(sketch, "E35.7.0", {"center": v(-8.28, 13.93) * mm, "radius": 0.1 * mm});
            skCircle(sketch, "E35.8.0", {"center": v(-9.32, 13.25) * mm, "radius": 0.1 * mm});
            skCircle(sketch, "E35.9.0", {"center": v(-10.3, 12.5) * mm, "radius": 0.1 * mm});
            skCircle(sketch, "E35.10.0", {"center": v(-11.23, 11.67) * mm, "radius": 0.1 * mm});
            skCircle(sketch, "E35.11.0", {"center": v(-12.1, 10.78) * mm, "radius": 0.1 * mm});
            skCircle(sketch, "E35.12.0", {"center": v(-12.88, 9.82) * mm, "radius": 0.1 * mm});
            skCircle(sketch, "E35.13.0", {"center": v(-13.6, 8.8) * mm, "radius": 0.1 * mm});
            skCircle(sketch, "E35.14.0", {"center": v(-14.23, 7.74) * mm, "radius": 0.1 * mm});
            skCircle(sketch, "E35.15.0", {"center": v(-14.78, 6.63) * mm, "radius": 0.1 * mm});
            skCircle(sketch, "E35.16.0", {"center": v(-15.25, 5.48) * mm, "radius": 0.1 * mm});
            skCircle(sketch, "E35.17.0", {"center": v(-15.62, 4.3) * mm, "radius": 0.1 * mm});
            skCircle(sketch, "E35.18.0", {"center": v(-15.9, 3.08) * mm, "radius": 0.1 * mm});
            skCircle(sketch, "E35.19.0", {"center": v(-16.1, 1.86) * mm, "radius": 0.1 * mm});
            skCircle(sketch, "E35.20.0", {"center": v(-16.19, 0.62) * mm, "radius": 0.1 * mm});
            skCircle(sketch, "E35.21.0", {"center": v(-16.19, -0.62) * mm, "radius": 0.1 * mm});
            skCircle(sketch, "E35.22.0", {"center": v(-16.1, -1.86) * mm, "radius": 0.1 * mm});
            skCircle(sketch, "E35.23.0", {"center": v(-15.9, -3.08) * mm, "radius": 0.1 * mm});
            skCircle(sketch, "E35.24.0", {"center": v(-15.62, -4.3) * mm, "radius": 0.1 * mm});
            skCircle(sketch, "E35.25.0", {"center": v(-15.25, -5.48) * mm, "radius": 0.1 * mm});
            skCircle(sketch, "E35.26.0", {"center": v(-14.78, -6.63) * mm, "radius": 0.1 * mm});
            skCircle(sketch, "E35.27.0", {"center": v(-14.23, -7.74) * mm, "radius": 0.1 * mm});
            skCircle(sketch, "E35.28.0", {"center": v(-13.6, -8.8) * mm, "radius": 0.1 * mm});
            skCircle(sketch, "E35.29.0", {"center": v(-12.88, -9.82) * mm, "radius": 0.1 * mm});
            skCircle(sketch, "E35.30.0", {"center": v(-12.1, -10.78) * mm, "radius": 0.1 * mm});
            skCircle(sketch, "E35.31.0", {"center": v(-11.23, -11.67) * mm, "radius": 0.1 * mm});
            skCircle(sketch, "E35.32.0", {"center": v(-10.3, -12.5) * mm, "radius": 0.1 * mm});
            skCircle(sketch, "E35.33.0", {"center": v(-9.32, -13.25) * mm, "radius": 0.1 * mm});
            skCircle(sketch, "E35.34.0", {"center": v(-8.28, -13.93) * mm, "radius": 0.1 * mm});
            skCircle(sketch, "E35.35.0", {"center": v(-7.19, -14.52) * mm, "radius": 0.1 * mm});
            skCircle(sketch, "E35.36.0", {"center": v(-6.06, -15.03) * mm, "radius": 0.1 * mm});
            skCircle(sketch, "E35.37.0", {"center": v(-4.89, -15.45) * mm, "radius": 0.1 * mm});
            skCircle(sketch, "E35.38.0", {"center": v(-3.7, -15.77) * mm, "radius": 0.1 * mm});
            skCircle(sketch, "E35.39.0", {"center": v(-2.47, -16.01) * mm, "radius": 0.1 * mm});
            skCircle(sketch, "E35.40.0", {"center": v(-1.24, -16.15) * mm, "radius": 0.1 * mm});
            skCircle(sketch, "E35.41.0", {"center": v(0, -16.2) * mm, "radius": 0.1 * mm});
            skCircle(sketch, "E35.42.0", {"center": v(1.24, -16.15) * mm, "radius": 0.1 * mm});
            skCircle(sketch, "E35.43.0", {"center": v(2.47, -16.01) * mm, "radius": 0.1 * mm});
            skCircle(sketch, "E35.44.0", {"center": v(3.7, -15.77) * mm, "radius": 0.1 * mm});
            skCircle(sketch, "E35.45.0", {"center": v(4.89, -15.45) * mm, "radius": 0.1 * mm});
            skCircle(sketch, "E35.46.0", {"center": v(6.06, -15.03) * mm, "radius": 0.1 * mm});
            skCircle(sketch, "E35.47.0", {"center": v(7.19, -14.52) * mm, "radius": 0.1 * mm});
            skCircle(sketch, "E35.48.0", {"center": v(8.28, -13.93) * mm, "radius": 0.1 * mm});
            skCircle(sketch, "E35.49.0", {"center": v(9.32, -13.25) * mm, "radius": 0.1 * mm});
            skCircle(sketch, "E35.50.0", {"center": v(10.3, -12.5) * mm, "radius": 0.1 * mm});
            skCircle(sketch, "E35.51.0", {"center": v(11.23, -11.67) * mm, "radius": 0.1 * mm});
            skCircle(sketch, "E35.52.0", {"center": v(12.1, -10.78) * mm, "radius": 0.1 * mm});
            skCircle(sketch, "E35.53.0", {"center": v(12.88, -9.82) * mm, "radius": 0.1 * mm});
            skCircle(sketch, "E35.54.0", {"center": v(13.6, -8.8) * mm, "radius": 0.1 * mm});
            skCircle(sketch, "E35.55.0", {"center": v(14.23, -7.74) * mm, "radius": 0.1 * mm});
            skCircle(sketch, "E35.56.0", {"center": v(14.78, -6.63) * mm, "radius": 0.1 * mm});
            skCircle(sketch, "E35.57.0", {"center": v(15.25, -5.48) * mm, "radius": 0.1 * mm});
            skCircle(sketch, "E35.58.0", {"center": v(15.62, -4.3) * mm, "radius": 0.1 * mm});
            skCircle(sketch, "E35.59.0", {"center": v(15.9, -3.08) * mm, "radius": 0.1 * mm});
            skCircle(sketch, "E35.60.0", {"center": v(16.1, -1.86) * mm, "radius": 0.1 * mm});
            skCircle(sketch, "E35.61.0", {"center": v(16.19, -0.62) * mm, "radius": 0.1 * mm});
            skCircle(sketch, "E35.62.0", {"center": v(16.19, 0.62) * mm, "radius": 0.1 * mm});
            skCircle(sketch, "E35.63.0", {"center": v(16.1, 1.86) * mm, "radius": 0.1 * mm});
            skCircle(sketch, "E35.64.0", {"center": v(15.9, 3.08) * mm, "radius": 0.1 * mm});
            skCircle(sketch, "E35.65.0", {"center": v(15.62, 4.3) * mm, "radius": 0.1 * mm});
            skCircle(sketch, "E35.66.0", {"center": v(15.25, 5.48) * mm, "radius": 0.1 * mm});
            skCircle(sketch, "E35.67.0", {"center": v(14.78, 6.63) * mm, "radius": 0.1 * mm});
            skCircle(sketch, "E35.68.0", {"center": v(14.23, 7.74) * mm, "radius": 0.1 * mm});
            skCircle(sketch, "E35.69.0", {"center": v(13.6, 8.8) * mm, "radius": 0.1 * mm});
            skCircle(sketch, "E35.70.0", {"center": v(12.88, 9.82) * mm, "radius": 0.1 * mm});
            skCircle(sketch, "E35.71.0", {"center": v(12.1, 10.78) * mm, "radius": 0.1 * mm});
            skCircle(sketch, "E35.72.0", {"center": v(11.23, 11.67) * mm, "radius": 0.1 * mm});
            skCircle(sketch, "E35.73.0", {"center": v(10.3, 12.5) * mm, "radius": 0.1 * mm});
            skCircle(sketch, "E35.74.0", {"center": v(9.32, 13.25) * mm, "radius": 0.1 * mm});
            skCircle(sketch, "E35.75.0", {"center": v(8.28, 13.93) * mm, "radius": 0.1 * mm});
            skCircle(sketch, "E35.76.0", {"center": v(7.19, 14.52) * mm, "radius": 0.1 * mm});
            skCircle(sketch, "E35.77.0", {"center": v(6.06, 15.03) * mm, "radius": 0.1 * mm});
            skCircle(sketch, "E35.78.0", {"center": v(4.89, 15.45) * mm, "radius": 0.1 * mm});
            skCircle(sketch, "E35.79.0", {"center": v(3.7, 15.77) * mm, "radius": 0.1 * mm});
            skCircle(sketch, "E35.80.0", {"center": v(2.47, 16.01) * mm, "radius": 0.1 * mm});
            skCircle(sketch, "E35.81.0", {"center": v(1.24, 16.15) * mm, "radius": 0.1 * mm});
            skCircle(sketch, "E36.1.0", {"center": v(-1.23, 17.46) * mm, "radius": 0.1 * mm});
            skCircle(sketch, "E36.2.0", {"center": v(-2.46, 17.33) * mm, "radius": 0.1 * mm});
            skCircle(sketch, "E36.3.0", {"center": v(-3.68, 17.1) * mm, "radius": 0.1 * mm});
            skCircle(sketch, "E36.4.0", {"center": v(-4.88, 16.8) * mm, "radius": 0.1 * mm});
            skCircle(sketch, "E36.5.0", {"center": v(-6.05, 16.42) * mm, "radius": 0.1 * mm});
            skCircle(sketch, "E36.6.0", {"center": v(-7.2, 15.95) * mm, "radius": 0.1 * mm});
            skCircle(sketch, "E36.7.0", {"center": v(-8.3, 15.4) * mm, "radius": 0.1 * mm});
            skCircle(sketch, "E36.8.0", {"center": v(-9.37, 14.78) * mm, "radius": 0.1 * mm});
            skCircle(sketch, "E36.9.0", {"center": v(-10.39, 14.08) * mm, "radius": 0.1 * mm});
            skCircle(sketch, "E36.10.0", {"center": v(-11.35, 13.32) * mm, "radius": 0.1 * mm});
            skCircle(sketch, "E36.11.0", {"center": v(-12.26, 12.48) * mm, "radius": 0.1 * mm});
            skCircle(sketch, "E36.12.0", {"center": v(-13.11, 11.59) * mm, "radius": 0.1 * mm});
            skCircle(sketch, "E36.13.0", {"center": v(-13.9, 10.63) * mm, "radius": 0.1 * mm});
            skCircle(sketch, "E36.14.0", {"center": v(-14.61, 9.63) * mm, "radius": 0.1 * mm});
            skCircle(sketch, "E36.15.0", {"center": v(-15.26, 8.57) * mm, "radius": 0.1 * mm});
            skCircle(sketch, "E36.16.0", {"center": v(-15.82, 7.47) * mm, "radius": 0.1 * mm});
            skCircle(sketch, "E36.17.0", {"center": v(-16.31, 6.34) * mm, "radius": 0.1 * mm});
            skCircle(sketch, "E36.18.0", {"center": v(-16.72, 5.17) * mm, "radius": 0.1 * mm});
            skCircle(sketch, "E36.19.0", {"center": v(-17.04, 3.98) * mm, "radius": 0.1 * mm});
            skCircle(sketch, "E36.20.0", {"center": v(-17.28, 2.77) * mm, "radius": 0.1 * mm});
            skCircle(sketch, "E36.21.0", {"center": v(-17.43, 1.54) * mm, "radius": 0.1 * mm});
            skCircle(sketch, "E36.22.0", {"center": v(-17.5, 0.3) * mm, "radius": 0.1 * mm});
            skCircle(sketch, "E36.23.0", {"center": v(-17.48, -0.93) * mm, "radius": 0.1 * mm});
            skCircle(sketch, "E36.24.0", {"center": v(-17.37, -2.16) * mm, "radius": 0.1 * mm});
            skCircle(sketch, "E36.25.0", {"center": v(-17.17, -3.38) * mm, "radius": 0.1 * mm});
            skCircle(sketch, "E36.26.0", {"center": v(-16.9, -4.58) * mm, "radius": 0.1 * mm});
            skCircle(sketch, "E36.27.0", {"center": v(-16.53, -5.76) * mm, "radius": 0.1 * mm});
            skCircle(sketch, "E36.28.0", {"center": v(-16.08, -6.91) * mm, "radius": 0.1 * mm});
            skCircle(sketch, "E36.29.0", {"center": v(-15.55, -8.03) * mm, "radius": 0.1 * mm});
            skCircle(sketch, "E36.30.0", {"center": v(-14.95, -9.1) * mm, "radius": 0.1 * mm});
            skCircle(sketch, "E36.31.0", {"center": v(-14.27, -10.14) * mm, "radius": 0.1 * mm});
            skCircle(sketch, "E36.32.0", {"center": v(-13.52, -11.12) * mm, "radius": 0.1 * mm});
            skCircle(sketch, "E36.33.0", {"center": v(-12.7, -12.04) * mm, "radius": 0.1 * mm});
            skCircle(sketch, "E36.34.0", {"center": v(-11.82, -12.9) * mm, "radius": 0.1 * mm});
            skCircle(sketch, "E36.35.0", {"center": v(-10.88, -13.7) * mm, "radius": 0.1 * mm});
            skCircle(sketch, "E36.36.0", {"center": v(-9.88, -14.44) * mm, "radius": 0.1 * mm});
            skCircle(sketch, "E36.37.0", {"center": v(-8.84, -15.1) * mm, "radius": 0.1 * mm});
            skCircle(sketch, "E36.38.0", {"center": v(-7.75, -15.69) * mm, "radius": 0.1 * mm});
            skCircle(sketch, "E36.39.0", {"center": v(-6.63, -16.2) * mm, "radius": 0.1 * mm});
            skCircle(sketch, "E36.40.0", {"center": v(-5.47, -16.62) * mm, "radius": 0.1 * mm});
            skCircle(sketch, "E36.41.0", {"center": v(-4.28, -16.97) * mm, "radius": 0.1 * mm});
            skCircle(sketch, "E36.42.0", {"center": v(-3.07, -17.23) * mm, "radius": 0.1 * mm});
            skCircle(sketch, "E36.43.0", {"center": v(-1.85, -17.4) * mm, "radius": 0.1 * mm});
            skCircle(sketch, "E36.44.0", {"center": v(-0.62, -17.49) * mm, "radius": 0.1 * mm});
            skCircle(sketch, "E36.45.0", {"center": v(0.62, -17.49) * mm, "radius": 0.1 * mm});
            skCircle(sketch, "E36.46.0", {"center": v(1.85, -17.4) * mm, "radius": 0.1 * mm});
            skCircle(sketch, "E36.47.0", {"center": v(3.07, -17.23) * mm, "radius": 0.1 * mm});
            skCircle(sketch, "E36.48.0", {"center": v(4.28, -16.97) * mm, "radius": 0.1 * mm});
            skCircle(sketch, "E36.49.0", {"center": v(5.47, -16.62) * mm, "radius": 0.1 * mm});
            skCircle(sketch, "E36.50.0", {"center": v(6.63, -16.2) * mm, "radius": 0.1 * mm});
            skCircle(sketch, "E36.51.0", {"center": v(7.75, -15.69) * mm, "radius": 0.1 * mm});
            skCircle(sketch, "E36.52.0", {"center": v(8.84, -15.1) * mm, "radius": 0.1 * mm});
            skCircle(sketch, "E36.53.0", {"center": v(9.88, -14.44) * mm, "radius": 0.1 * mm});
            skCircle(sketch, "E36.54.0", {"center": v(10.88, -13.7) * mm, "radius": 0.1 * mm});
            skCircle(sketch, "E36.55.0", {"center": v(11.82, -12.9) * mm, "radius": 0.1 * mm});
            skCircle(sketch, "E36.56.0", {"center": v(12.7, -12.04) * mm, "radius": 0.1 * mm});
            skCircle(sketch, "E36.57.0", {"center": v(13.52, -11.12) * mm, "radius": 0.1 * mm});
            skCircle(sketch, "E36.58.0", {"center": v(14.27, -10.14) * mm, "radius": 0.1 * mm});
            skCircle(sketch, "E36.59.0", {"center": v(14.95, -9.1) * mm, "radius": 0.1 * mm});
            skCircle(sketch, "E36.60.0", {"center": v(15.55, -8.03) * mm, "radius": 0.1 * mm});
            skCircle(sketch, "E36.61.0", {"center": v(16.08, -6.91) * mm, "radius": 0.1 * mm});
            skCircle(sketch, "E36.62.0", {"center": v(16.53, -5.76) * mm, "radius": 0.1 * mm});
            skCircle(sketch, "E36.63.0", {"center": v(16.9, -4.58) * mm, "radius": 0.1 * mm});
            skCircle(sketch, "E36.64.0", {"center": v(17.17, -3.38) * mm, "radius": 0.1 * mm});
            skCircle(sketch, "E36.65.0", {"center": v(17.37, -2.16) * mm, "radius": 0.1 * mm});
            skCircle(sketch, "E36.66.0", {"center": v(17.48, -0.93) * mm, "radius": 0.1 * mm});
            skCircle(sketch, "E36.67.0", {"center": v(17.5, 0.3) * mm, "radius": 0.1 * mm});
            skCircle(sketch, "E36.68.0", {"center": v(17.43, 1.54) * mm, "radius": 0.1 * mm});
            skCircle(sketch, "E36.69.0", {"center": v(17.28, 2.77) * mm, "radius": 0.1 * mm});
            skCircle(sketch, "E36.70.0", {"center": v(17.04, 3.98) * mm, "radius": 0.1 * mm});
            skCircle(sketch, "E36.71.0", {"center": v(16.72, 5.17) * mm, "radius": 0.1 * mm});
            skCircle(sketch, "E36.72.0", {"center": v(16.31, 6.34) * mm, "radius": 0.1 * mm});
            skCircle(sketch, "E36.73.0", {"center": v(15.82, 7.47) * mm, "radius": 0.1 * mm});
            skCircle(sketch, "E36.74.0", {"center": v(15.26, 8.57) * mm, "radius": 0.1 * mm});
            skCircle(sketch, "E36.75.0", {"center": v(14.61, 9.63) * mm, "radius": 0.1 * mm});
            skCircle(sketch, "E36.76.0", {"center": v(13.9, 10.63) * mm, "radius": 0.1 * mm});
            skCircle(sketch, "E36.77.0", {"center": v(13.11, 11.59) * mm, "radius": 0.1 * mm});
            skCircle(sketch, "E36.78.0", {"center": v(12.26, 12.48) * mm, "radius": 0.1 * mm});
            skCircle(sketch, "E36.79.0", {"center": v(11.35, 13.32) * mm, "radius": 0.1 * mm});
            skCircle(sketch, "E36.80.0", {"center": v(10.39, 14.08) * mm, "radius": 0.1 * mm});
            skCircle(sketch, "E36.81.0", {"center": v(9.37, 14.78) * mm, "radius": 0.1 * mm});
            skCircle(sketch, "E36.82.0", {"center": v(8.3, 15.4) * mm, "radius": 0.1 * mm});
            skCircle(sketch, "E36.83.0", {"center": v(7.2, 15.95) * mm, "radius": 0.1 * mm});
            skCircle(sketch, "E36.84.0", {"center": v(6.05, 16.42) * mm, "radius": 0.1 * mm});
            skCircle(sketch, "E36.85.0", {"center": v(4.88, 16.8) * mm, "radius": 0.1 * mm});
            skCircle(sketch, "E36.86.0", {"center": v(3.68, 17.1) * mm, "radius": 0.1 * mm});
            skCircle(sketch, "E36.87.0", {"center": v(2.46, 17.33) * mm, "radius": 0.1 * mm});
            skCircle(sketch, "E36.88.0", {"center": v(1.23, 17.46) * mm, "radius": 0.1 * mm});
            skCircle(sketch, "E37.1.0", {"center": v(-1.23, 18.76) * mm, "radius": 0.1 * mm});
            skCircle(sketch, "E37.2.0", {"center": v(-2.45, 18.64) * mm, "radius": 0.1 * mm});
            skCircle(sketch, "E37.3.0", {"center": v(-3.67, 18.44) * mm, "radius": 0.1 * mm});
            skCircle(sketch, "E37.4.0", {"center": v(-4.87, 18.16) * mm, "radius": 0.1 * mm});
            skCircle(sketch, "E37.5.0", {"center": v(-6.04, 17.8) * mm, "radius": 0.1 * mm});
            skCircle(sketch, "E37.6.0", {"center": v(-7.2, 17.37) * mm, "radius": 0.1 * mm});
            skCircle(sketch, "E37.7.0", {"center": v(-8.32, 16.86) * mm, "radius": 0.1 * mm});
            skCircle(sketch, "E37.8.0", {"center": v(-9.4, 16.28) * mm, "radius": 0.1 * mm});
            skCircle(sketch, "E37.9.0", {"center": v(-10.44, 15.63) * mm, "radius": 0.1 * mm});
            skCircle(sketch, "E37.10.0", {"center": v(-11.44, 14.92) * mm, "radius": 0.1 * mm});
            skCircle(sketch, "E37.11.0", {"center": v(-12.4, 14.13) * mm, "radius": 0.1 * mm});
            skCircle(sketch, "E37.12.0", {"center": v(-13.3, 13.3) * mm, "radius": 0.1 * mm});
            skCircle(sketch, "E37.13.0", {"center": v(-14.13, 12.4) * mm, "radius": 0.1 * mm});
            skCircle(sketch, "E37.14.0", {"center": v(-14.92, 11.44) * mm, "radius": 0.1 * mm});
            skCircle(sketch, "E37.15.0", {"center": v(-15.63, 10.44) * mm, "radius": 0.1 * mm});
            skCircle(sketch, "E37.16.0", {"center": v(-16.28, 9.4) * mm, "radius": 0.1 * mm});
            skCircle(sketch, "E37.17.0", {"center": v(-16.86, 8.32) * mm, "radius": 0.1 * mm});
            skCircle(sketch, "E37.18.0", {"center": v(-17.37, 7.2) * mm, "radius": 0.1 * mm});
            skCircle(sketch, "E37.19.0", {"center": v(-17.8, 6.04) * mm, "radius": 0.1 * mm});
            skCircle(sketch, "E37.20.0", {"center": v(-18.16, 4.87) * mm, "radius": 0.1 * mm});
            skCircle(sketch, "E37.21.0", {"center": v(-18.44, 3.67) * mm, "radius": 0.1 * mm});
            skCircle(sketch, "E37.22.0", {"center": v(-18.64, 2.45) * mm, "radius": 0.1 * mm});
            skCircle(sketch, "E37.23.0", {"center": v(-18.76, 1.23) * mm, "radius": 0.1 * mm});
            skCircle(sketch, "E37.24.0", {"center": v(-18.8, 0) * mm, "radius": 0.1 * mm});
            skCircle(sketch, "E37.25.0", {"center": v(-18.76, -1.23) * mm, "radius": 0.1 * mm});
            skCircle(sketch, "E37.26.0", {"center": v(-18.64, -2.45) * mm, "radius": 0.1 * mm});
            skCircle(sketch, "E37.27.0", {"center": v(-18.44, -3.67) * mm, "radius": 0.1 * mm});
            skCircle(sketch, "E37.28.0", {"center": v(-18.16, -4.87) * mm, "radius": 0.1 * mm});
            skCircle(sketch, "E37.29.0", {"center": v(-17.8, -6.04) * mm, "radius": 0.1 * mm});
            skCircle(sketch, "E37.30.0", {"center": v(-17.37, -7.2) * mm, "radius": 0.1 * mm});
            skCircle(sketch, "E37.31.0", {"center": v(-16.86, -8.32) * mm, "radius": 0.1 * mm});
            skCircle(sketch, "E37.32.0", {"center": v(-16.28, -9.4) * mm, "radius": 0.1 * mm});
            skCircle(sketch, "E37.33.0", {"center": v(-15.63, -10.44) * mm, "radius": 0.1 * mm});
            skCircle(sketch, "E37.34.0", {"center": v(-14.92, -11.44) * mm, "radius": 0.1 * mm});
            skCircle(sketch, "E37.35.0", {"center": v(-14.13, -12.4) * mm, "radius": 0.1 * mm});
            skCircle(sketch, "E37.36.0", {"center": v(-13.3, -13.3) * mm, "radius": 0.1 * mm});
            skCircle(sketch, "E37.37.0", {"center": v(-12.4, -14.13) * mm, "radius": 0.1 * mm});
            skCircle(sketch, "E37.38.0", {"center": v(-11.44, -14.92) * mm, "radius": 0.1 * mm});
            skCircle(sketch, "E37.39.0", {"center": v(-10.44, -15.63) * mm, "radius": 0.1 * mm});
            skCircle(sketch, "E37.40.0", {"center": v(-9.4, -16.28) * mm, "radius": 0.1 * mm});
            skCircle(sketch, "E37.41.0", {"center": v(-8.32, -16.86) * mm, "radius": 0.1 * mm});
            skCircle(sketch, "E37.42.0", {"center": v(-7.2, -17.37) * mm, "radius": 0.1 * mm});
            skCircle(sketch, "E37.43.0", {"center": v(-6.04, -17.8) * mm, "radius": 0.1 * mm});
            skCircle(sketch, "E37.44.0", {"center": v(-4.87, -18.16) * mm, "radius": 0.1 * mm});
            skCircle(sketch, "E37.45.0", {"center": v(-3.67, -18.44) * mm, "radius": 0.1 * mm});
            skCircle(sketch, "E37.46.0", {"center": v(-2.45, -18.64) * mm, "radius": 0.1 * mm});
            skCircle(sketch, "E37.47.0", {"center": v(-1.23, -18.76) * mm, "radius": 0.1 * mm});
            skCircle(sketch, "E37.48.0", {"center": v(0, -18.8) * mm, "radius": 0.1 * mm});
            skCircle(sketch, "E37.49.0", {"center": v(1.23, -18.76) * mm, "radius": 0.1 * mm});
            skCircle(sketch, "E37.50.0", {"center": v(2.45, -18.64) * mm, "radius": 0.1 * mm});
            skCircle(sketch, "E37.51.0", {"center": v(3.67, -18.44) * mm, "radius": 0.1 * mm});
            skCircle(sketch, "E37.52.0", {"center": v(4.87, -18.16) * mm, "radius": 0.1 * mm});
            skCircle(sketch, "E37.53.0", {"center": v(6.04, -17.8) * mm, "radius": 0.1 * mm});
            skCircle(sketch, "E37.54.0", {"center": v(7.2, -17.37) * mm, "radius": 0.1 * mm});
            skCircle(sketch, "E37.55.0", {"center": v(8.32, -16.86) * mm, "radius": 0.1 * mm});
            skCircle(sketch, "E37.56.0", {"center": v(9.4, -16.28) * mm, "radius": 0.1 * mm});
            skCircle(sketch, "E37.57.0", {"center": v(10.44, -15.63) * mm, "radius": 0.1 * mm});
            skCircle(sketch, "E37.58.0", {"center": v(11.44, -14.92) * mm, "radius": 0.1 * mm});
            skCircle(sketch, "E37.59.0", {"center": v(12.4, -14.13) * mm, "radius": 0.1 * mm});
            skCircle(sketch, "E37.60.0", {"center": v(13.3, -13.3) * mm, "radius": 0.1 * mm});
            skCircle(sketch, "E37.61.0", {"center": v(14.13, -12.4) * mm, "radius": 0.1 * mm});
            skCircle(sketch, "E37.62.0", {"center": v(14.92, -11.44) * mm, "radius": 0.1 * mm});
            skCircle(sketch, "E37.63.0", {"center": v(15.63, -10.44) * mm, "radius": 0.1 * mm});
            skCircle(sketch, "E37.64.0", {"center": v(16.28, -9.4) * mm, "radius": 0.1 * mm});
            skCircle(sketch, "E37.65.0", {"center": v(16.86, -8.32) * mm, "radius": 0.1 * mm});
            skCircle(sketch, "E37.66.0", {"center": v(17.37, -7.2) * mm, "radius": 0.1 * mm});
            skCircle(sketch, "E37.67.0", {"center": v(17.8, -6.04) * mm, "radius": 0.1 * mm});
            skCircle(sketch, "E37.68.0", {"center": v(18.16, -4.87) * mm, "radius": 0.1 * mm});
            skCircle(sketch, "E37.69.0", {"center": v(18.44, -3.67) * mm, "radius": 0.1 * mm});
            skCircle(sketch, "E37.70.0", {"center": v(18.64, -2.45) * mm, "radius": 0.1 * mm});
            skCircle(sketch, "E37.71.0", {"center": v(18.76, -1.23) * mm, "radius": 0.1 * mm});
            skCircle(sketch, "E37.72.0", {"center": v(18.8, 0) * mm, "radius": 0.1 * mm});
            skCircle(sketch, "E37.73.0", {"center": v(18.76, 1.23) * mm, "radius": 0.1 * mm});
            skCircle(sketch, "E37.74.0", {"center": v(18.64, 2.45) * mm, "radius": 0.1 * mm});
            skCircle(sketch, "E37.75.0", {"center": v(18.44, 3.67) * mm, "radius": 0.1 * mm});
            skCircle(sketch, "E37.76.0", {"center": v(18.16, 4.87) * mm, "radius": 0.1 * mm});
            skCircle(sketch, "E37.77.0", {"center": v(17.8, 6.04) * mm, "radius": 0.1 * mm});
            skCircle(sketch, "E37.78.0", {"center": v(17.37, 7.2) * mm, "radius": 0.1 * mm});
            skCircle(sketch, "E37.79.0", {"center": v(16.86, 8.32) * mm, "radius": 0.1 * mm});
            skCircle(sketch, "E37.80.0", {"center": v(16.28, 9.4) * mm, "radius": 0.1 * mm});
            skCircle(sketch, "E37.81.0", {"center": v(15.63, 10.44) * mm, "radius": 0.1 * mm});
            skCircle(sketch, "E37.82.0", {"center": v(14.92, 11.44) * mm, "radius": 0.1 * mm});
            skCircle(sketch, "E37.83.0", {"center": v(14.13, 12.4) * mm, "radius": 0.1 * mm});
            skCircle(sketch, "E37.84.0", {"center": v(13.3, 13.3) * mm, "radius": 0.1 * mm});
            skCircle(sketch, "E37.85.0", {"center": v(12.4, 14.13) * mm, "radius": 0.1 * mm});
            skCircle(sketch, "E37.86.0", {"center": v(11.44, 14.92) * mm, "radius": 0.1 * mm});
            skCircle(sketch, "E37.87.0", {"center": v(10.44, 15.63) * mm, "radius": 0.1 * mm});
            skCircle(sketch, "E37.88.0", {"center": v(9.4, 16.28) * mm, "radius": 0.1 * mm});
            skCircle(sketch, "E37.89.0", {"center": v(8.32, 16.86) * mm, "radius": 0.1 * mm});
            skCircle(sketch, "E37.90.0", {"center": v(7.2, 17.37) * mm, "radius": 0.1 * mm});
            skCircle(sketch, "E37.91.0", {"center": v(6.04, 17.8) * mm, "radius": 0.1 * mm});
            skCircle(sketch, "E37.92.0", {"center": v(4.87, 18.16) * mm, "radius": 0.1 * mm});
            skCircle(sketch, "E37.93.0", {"center": v(3.67, 18.44) * mm, "radius": 0.1 * mm});
            skCircle(sketch, "E37.94.0", {"center": v(2.45, 18.64) * mm, "radius": 0.1 * mm});
            skCircle(sketch, "E37.95.0", {"center": v(1.23, 18.76) * mm, "radius": 0.1 * mm});
            skCircle(sketch, "E38.1.0", {"center": v(-1.23, 20.06) * mm, "radius": 0.1 * mm});
            skCircle(sketch, "E38.2.0", {"center": v(-2.45, 19.95) * mm, "radius": 0.1 * mm});
            skCircle(sketch, "E38.3.0", {"center": v(-3.66, 19.76) * mm, "radius": 0.1 * mm});
            skCircle(sketch, "E38.4.0", {"center": v(-4.86, 19.5) * mm, "radius": 0.1 * mm});
            skCircle(sketch, "E38.5.0", {"center": v(-6.04, 19.17) * mm, "radius": 0.1 * mm});
            skCircle(sketch, "E38.6.0", {"center": v(-7.2, 18.77) * mm, "radius": 0.1 * mm});
            skCircle(sketch, "E38.7.0", {"center": v(-8.32, 18.3) * mm, "radius": 0.1 * mm});
            skCircle(sketch, "E38.8.0", {"center": v(-9.42, 17.75) * mm, "radius": 0.1 * mm});
            skCircle(sketch, "E38.9.0", {"center": v(-10.49, 17.15) * mm, "radius": 0.1 * mm});
            skCircle(sketch, "E38.10.0", {"center": v(-11.51, 16.47) * mm, "radius": 0.1 * mm});
            skCircle(sketch, "E38.11.0", {"center": v(-12.5, 15.74) * mm, "radius": 0.1 * mm});
            skCircle(sketch, "E38.12.0", {"center": v(-13.43, 14.95) * mm, "radius": 0.1 * mm});
            skCircle(sketch, "E38.13.0", {"center": v(-14.32, 14.1) * mm, "radius": 0.1 * mm});
            skCircle(sketch, "E38.14.0", {"center": v(-15.15, 13.2) * mm, "radius": 0.1 * mm});
            skCircle(sketch, "E38.15.0", {"center": v(-15.93, 12.26) * mm, "radius": 0.1 * mm});
            skCircle(sketch, "E38.16.0", {"center": v(-16.65, 11.26) * mm, "radius": 0.1 * mm});
            skCircle(sketch, "E38.17.0", {"center": v(-17.3, 10.23) * mm, "radius": 0.1 * mm});
            skCircle(sketch, "E38.18.0", {"center": v(-17.9, 9.15) * mm, "radius": 0.1 * mm});
            skCircle(sketch, "E38.19.0", {"center": v(-18.42, 8.04) * mm, "radius": 0.1 * mm});
            skCircle(sketch, "E38.20.0", {"center": v(-18.88, 6.9) * mm, "radius": 0.1 * mm});
            skCircle(sketch, "E38.21.0", {"center": v(-19.26, 5.74) * mm, "radius": 0.1 * mm});
            skCircle(sketch, "E38.22.0", {"center": v(-19.58, 4.56) * mm, "radius": 0.1 * mm});
            skCircle(sketch, "E38.23.0", {"center": v(-19.82, 3.36) * mm, "radius": 0.1 * mm});
            skCircle(sketch, "E38.24.0", {"center": v(-19.99, 2.14) * mm, "radius": 0.1 * mm});
            skCircle(sketch, "E38.25.0", {"center": v(-20.08, 0.92) * mm, "radius": 0.1 * mm});
            skCircle(sketch, "E38.26.0", {"center": v(-20.1, -0.3) * mm, "radius": 0.1 * mm});
            skCircle(sketch, "E38.27.0", {"center": v(-20.04, -1.53) * mm, "radius": 0.1 * mm});
            skCircle(sketch, "E38.28.0", {"center": v(-19.91, -2.75) * mm, "radius": 0.1 * mm});
            skCircle(sketch, "E38.29.0", {"center": v(-19.7, -3.96) * mm, "radius": 0.1 * mm});
            skCircle(sketch, "E38.30.0", {"center": v(-19.43, -5.15) * mm, "radius": 0.1 * mm});
            skCircle(sketch, "E38.31.0", {"center": v(-19.08, -6.33) * mm, "radius": 0.1 * mm});
            skCircle(sketch, "E38.32.0", {"center": v(-18.66, -7.48) * mm, "radius": 0.1 * mm});
            skCircle(sketch, "E38.33.0", {"center": v(-18.17, -8.6) * mm, "radius": 0.1 * mm});
            skCircle(sketch, "E38.34.0", {"center": v(-17.6, -9.7) * mm, "radius": 0.1 * mm});
            skCircle(sketch, "E38.35.0", {"center": v(-16.98, -10.75) * mm, "radius": 0.1 * mm});
            skCircle(sketch, "E38.36.0", {"center": v(-16.3, -11.76) * mm, "radius": 0.1 * mm});
            skCircle(sketch, "E38.37.0", {"center": v(-15.55, -12.74) * mm, "radius": 0.1 * mm});
            skCircle(sketch, "E38.38.0", {"center": v(-14.74, -13.66) * mm, "radius": 0.1 * mm});
            skCircle(sketch, "E38.39.0", {"center": v(-13.88, -14.53) * mm, "radius": 0.1 * mm});
            skCircle(sketch, "E38.40.0", {"center": v(-12.97, -15.35) * mm, "radius": 0.1 * mm});
            skCircle(sketch, "E38.41.0", {"center": v(-12.01, -16.12) * mm, "radius": 0.1 * mm});
            skCircle(sketch, "E38.42.0", {"center": v(-11, -16.82) * mm, "radius": 0.1 * mm});
            skCircle(sketch, "E38.43.0", {"center": v(-9.96, -17.46) * mm, "radius": 0.1 * mm});
            skCircle(sketch, "E38.44.0", {"center": v(-8.88, -18.03) * mm, "radius": 0.1 * mm});
            skCircle(sketch, "E38.45.0", {"center": v(-7.76, -18.54) * mm, "radius": 0.1 * mm});
            skCircle(sketch, "E38.46.0", {"center": v(-6.62, -18.98) * mm, "radius": 0.1 * mm});
            skCircle(sketch, "E38.47.0", {"center": v(-5.45, -19.35) * mm, "radius": 0.1 * mm});
            skCircle(sketch, "E38.48.0", {"center": v(-4.26, -19.64) * mm, "radius": 0.1 * mm});
            skCircle(sketch, "E38.49.0", {"center": v(-3.05, -19.87) * mm, "radius": 0.1 * mm});
            skCircle(sketch, "E38.50.0", {"center": v(-1.84, -20.02) * mm, "radius": 0.1 * mm});
            skCircle(sketch, "E38.51.0", {"center": v(-0.61, -20.1) * mm, "radius": 0.1 * mm});
            skCircle(sketch, "E38.52.0", {"center": v(0.61, -20.1) * mm, "radius": 0.1 * mm});
            skCircle(sketch, "E38.53.0", {"center": v(1.84, -20.02) * mm, "radius": 0.1 * mm});
            skCircle(sketch, "E38.54.0", {"center": v(3.05, -19.87) * mm, "radius": 0.1 * mm});
            skCircle(sketch, "E38.55.0", {"center": v(4.26, -19.64) * mm, "radius": 0.1 * mm});
            skCircle(sketch, "E38.56.0", {"center": v(5.45, -19.35) * mm, "radius": 0.1 * mm});
            skCircle(sketch, "E38.57.0", {"center": v(6.62, -18.98) * mm, "radius": 0.1 * mm});
            skCircle(sketch, "E38.58.0", {"center": v(7.76, -18.54) * mm, "radius": 0.1 * mm});
            skCircle(sketch, "E38.59.0", {"center": v(8.88, -18.03) * mm, "radius": 0.1 * mm});
            skCircle(sketch, "E38.60.0", {"center": v(9.96, -17.46) * mm, "radius": 0.1 * mm});
            skCircle(sketch, "E38.61.0", {"center": v(11, -16.82) * mm, "radius": 0.1 * mm});
            skCircle(sketch, "E38.62.0", {"center": v(12.01, -16.12) * mm, "radius": 0.1 * mm});
            skCircle(sketch, "E38.63.0", {"center": v(12.97, -15.35) * mm, "radius": 0.1 * mm});
            skCircle(sketch, "E38.64.0", {"center": v(13.88, -14.53) * mm, "radius": 0.1 * mm});
            skCircle(sketch, "E38.65.0", {"center": v(14.74, -13.66) * mm, "radius": 0.1 * mm});
            skCircle(sketch, "E38.66.0", {"center": v(15.55, -12.74) * mm, "radius": 0.1 * mm});
            skCircle(sketch, "E38.67.0", {"center": v(16.3, -11.76) * mm, "radius": 0.1 * mm});
            skCircle(sketch, "E38.68.0", {"center": v(16.98, -10.75) * mm, "radius": 0.1 * mm});
            skCircle(sketch, "E38.69.0", {"center": v(17.6, -9.7) * mm, "radius": 0.1 * mm});
            skCircle(sketch, "E38.70.0", {"center": v(18.17, -8.6) * mm, "radius": 0.1 * mm});
            skCircle(sketch, "E38.71.0", {"center": v(18.66, -7.48) * mm, "radius": 0.1 * mm});
            skCircle(sketch, "E38.72.0", {"center": v(19.08, -6.33) * mm, "radius": 0.1 * mm});
            skCircle(sketch, "E38.73.0", {"center": v(19.43, -5.15) * mm, "radius": 0.1 * mm});
            skCircle(sketch, "E38.74.0", {"center": v(19.7, -3.96) * mm, "radius": 0.1 * mm});
            skCircle(sketch, "E38.75.0", {"center": v(19.91, -2.75) * mm, "radius": 0.1 * mm});
            skCircle(sketch, "E38.76.0", {"center": v(20.04, -1.53) * mm, "radius": 0.1 * mm});
            skCircle(sketch, "E38.77.0", {"center": v(20.1, -0.3) * mm, "radius": 0.1 * mm});
            skCircle(sketch, "E38.78.0", {"center": v(20.08, 0.92) * mm, "radius": 0.1 * mm});
            skCircle(sketch, "E38.79.0", {"center": v(19.99, 2.14) * mm, "radius": 0.1 * mm});
            skCircle(sketch, "E38.80.0", {"center": v(19.82, 3.36) * mm, "radius": 0.1 * mm});
            skCircle(sketch, "E38.81.0", {"center": v(19.58, 4.56) * mm, "radius": 0.1 * mm});
            skCircle(sketch, "E38.82.0", {"center": v(19.26, 5.74) * mm, "radius": 0.1 * mm});
            skCircle(sketch, "E38.83.0", {"center": v(18.88, 6.9) * mm, "radius": 0.1 * mm});
            skCircle(sketch, "E38.84.0", {"center": v(18.42, 8.04) * mm, "radius": 0.1 * mm});
            skCircle(sketch, "E38.85.0", {"center": v(17.9, 9.15) * mm, "radius": 0.1 * mm});
            skCircle(sketch, "E38.86.0", {"center": v(17.3, 10.23) * mm, "radius": 0.1 * mm});
            skCircle(sketch, "E38.87.0", {"center": v(16.65, 11.26) * mm, "radius": 0.1 * mm});
            skCircle(sketch, "E38.88.0", {"center": v(15.93, 12.26) * mm, "radius": 0.1 * mm});
            skCircle(sketch, "E38.89.0", {"center": v(15.15, 13.2) * mm, "radius": 0.1 * mm});
            skCircle(sketch, "E38.90.0", {"center": v(14.32, 14.1) * mm, "radius": 0.1 * mm});
            skCircle(sketch, "E38.91.0", {"center": v(13.43, 14.95) * mm, "radius": 0.1 * mm});
            skCircle(sketch, "E38.92.0", {"center": v(12.5, 15.74) * mm, "radius": 0.1 * mm});
            skCircle(sketch, "E38.93.0", {"center": v(11.51, 16.47) * mm, "radius": 0.1 * mm});
            skCircle(sketch, "E38.94.0", {"center": v(10.49, 17.15) * mm, "radius": 0.1 * mm});
            skCircle(sketch, "E38.95.0", {"center": v(9.42, 17.75) * mm, "radius": 0.1 * mm});
            skCircle(sketch, "E38.96.0", {"center": v(8.32, 18.3) * mm, "radius": 0.1 * mm});
            skCircle(sketch, "E38.97.0", {"center": v(7.2, 18.77) * mm, "radius": 0.1 * mm});
            skCircle(sketch, "E38.98.0", {"center": v(6.04, 19.17) * mm, "radius": 0.1 * mm});
            skCircle(sketch, "E38.99.0", {"center": v(4.86, 19.5) * mm, "radius": 0.1 * mm});
            skCircle(sketch, "E38.100.0", {"center": v(3.66, 19.76) * mm, "radius": 0.1 * mm});
            skCircle(sketch, "E38.101.0", {"center": v(2.45, 19.95) * mm, "radius": 0.1 * mm});
            skCircle(sketch, "E38.102.0", {"center": v(1.23, 20.06) * mm, "radius": 0.1 * mm});
            skCircle(sketch, "E39.1.0", {"center": v(-1.22, 21.37) * mm, "radius": 0.1 * mm});
            skCircle(sketch, "E39.2.0", {"center": v(-2.44, 21.26) * mm, "radius": 0.1 * mm});
            skCircle(sketch, "E39.3.0", {"center": v(-3.65, 21.09) * mm, "radius": 0.1 * mm});
            skCircle(sketch, "E39.4.0", {"center": v(-4.85, 20.84) * mm, "radius": 0.1 * mm});
            skCircle(sketch, "E39.5.0", {"center": v(-6.03, 20.53) * mm, "radius": 0.1 * mm});
            skCircle(sketch, "E39.6.0", {"center": v(-7.2, 20.16) * mm, "radius": 0.1 * mm});
            skCircle(sketch, "E39.7.0", {"center": v(-8.33, 19.71) * mm, "radius": 0.1 * mm});
            skCircle(sketch, "E39.8.0", {"center": v(-9.44, 19.2) * mm, "radius": 0.1 * mm});
            skCircle(sketch, "E39.9.0", {"center": v(-10.52, 18.63) * mm, "radius": 0.1 * mm});
            skCircle(sketch, "E39.10.0", {"center": v(-11.57, 18) * mm, "radius": 0.1 * mm});
            skCircle(sketch, "E39.11.0", {"center": v(-12.58, 17.31) * mm, "radius": 0.1 * mm});
            skCircle(sketch, "E39.12.0", {"center": v(-13.55, 16.57) * mm, "radius": 0.1 * mm});
            skCircle(sketch, "E39.13.0", {"center": v(-14.47, 15.77) * mm, "radius": 0.1 * mm});
            skCircle(sketch, "E39.14.0", {"center": v(-15.35, 14.91) * mm, "radius": 0.1 * mm});
            skCircle(sketch, "E39.15.0", {"center": v(-16.17, 14.01) * mm, "radius": 0.1 * mm});
            skCircle(sketch, "E39.16.0", {"center": v(-16.95, 13.07) * mm, "radius": 0.1 * mm});
            skCircle(sketch, "E39.17.0", {"center": v(-17.67, 12.08) * mm, "radius": 0.1 * mm});
            skCircle(sketch, "E39.18.0", {"center": v(-18.33, 11.05) * mm, "radius": 0.1 * mm});
            skCircle(sketch, "E39.19.0", {"center": v(-18.93, 9.99) * mm, "radius": 0.1 * mm});
            skCircle(sketch, "E39.20.0", {"center": v(-19.47, 8.89) * mm, "radius": 0.1 * mm});
            skCircle(sketch, "E39.21.0", {"center": v(-19.94, 7.76) * mm, "radius": 0.1 * mm});
            skCircle(sketch, "E39.22.0", {"center": v(-20.35, 6.61) * mm, "radius": 0.1 * mm});
            skCircle(sketch, "E39.23.0", {"center": v(-20.7, 5.44) * mm, "radius": 0.1 * mm});
            skCircle(sketch, "E39.24.0", {"center": v(-20.97, 4.25) * mm, "radius": 0.1 * mm});
            skCircle(sketch, "E39.25.0", {"center": v(-21.18, 3.05) * mm, "radius": 0.1 * mm});
            skCircle(sketch, "E39.26.0", {"center": v(-21.32, 1.83) * mm, "radius": 0.1 * mm});
            skCircle(sketch, "E39.27.0", {"center": v(-21.4, 0.61) * mm, "radius": 0.1 * mm});
            skCircle(sketch, "E39.28.0", {"center": v(-21.4, -0.61) * mm, "radius": 0.1 * mm});
            skCircle(sketch, "E39.29.0", {"center": v(-21.32, -1.83) * mm, "radius": 0.1 * mm});
            skCircle(sketch, "E39.30.0", {"center": v(-21.18, -3.05) * mm, "radius": 0.1 * mm});
            skCircle(sketch, "E39.31.0", {"center": v(-20.97, -4.25) * mm, "radius": 0.1 * mm});
            skCircle(sketch, "E39.32.0", {"center": v(-20.7, -5.44) * mm, "radius": 0.1 * mm});
            skCircle(sketch, "E39.33.0", {"center": v(-20.35, -6.61) * mm, "radius": 0.1 * mm});
            skCircle(sketch, "E39.34.0", {"center": v(-19.94, -7.76) * mm, "radius": 0.1 * mm});
            skCircle(sketch, "E39.35.0", {"center": v(-19.47, -8.89) * mm, "radius": 0.1 * mm});
            skCircle(sketch, "E39.36.0", {"center": v(-18.93, -9.99) * mm, "radius": 0.1 * mm});
            skCircle(sketch, "E39.37.0", {"center": v(-18.33, -11.05) * mm, "radius": 0.1 * mm});
            skCircle(sketch, "E39.38.0", {"center": v(-17.67, -12.08) * mm, "radius": 0.1 * mm});
            skCircle(sketch, "E39.39.0", {"center": v(-16.95, -13.07) * mm, "radius": 0.1 * mm});
            skCircle(sketch, "E39.40.0", {"center": v(-16.17, -14.01) * mm, "radius": 0.1 * mm});
            skCircle(sketch, "E39.41.0", {"center": v(-15.35, -14.91) * mm, "radius": 0.1 * mm});
            skCircle(sketch, "E39.42.0", {"center": v(-14.47, -15.77) * mm, "radius": 0.1 * mm});
            skCircle(sketch, "E39.43.0", {"center": v(-13.55, -16.57) * mm, "radius": 0.1 * mm});
            skCircle(sketch, "E39.44.0", {"center": v(-12.58, -17.31) * mm, "radius": 0.1 * mm});
            skCircle(sketch, "E39.45.0", {"center": v(-11.57, -18) * mm, "radius": 0.1 * mm});
            skCircle(sketch, "E39.46.0", {"center": v(-10.52, -18.63) * mm, "radius": 0.1 * mm});
            skCircle(sketch, "E39.47.0", {"center": v(-9.44, -19.2) * mm, "radius": 0.1 * mm});
            skCircle(sketch, "E39.48.0", {"center": v(-8.33, -19.71) * mm, "radius": 0.1 * mm});
            skCircle(sketch, "E39.49.0", {"center": v(-7.2, -20.16) * mm, "radius": 0.1 * mm});
            skCircle(sketch, "E39.50.0", {"center": v(-6.03, -20.53) * mm, "radius": 0.1 * mm});
            skCircle(sketch, "E39.51.0", {"center": v(-4.85, -20.84) * mm, "radius": 0.1 * mm});
            skCircle(sketch, "E39.52.0", {"center": v(-3.65, -21.09) * mm, "radius": 0.1 * mm});
            skCircle(sketch, "E39.53.0", {"center": v(-2.44, -21.26) * mm, "radius": 0.1 * mm});
            skCircle(sketch, "E39.54.0", {"center": v(-1.22, -21.37) * mm, "radius": 0.1 * mm});
            skCircle(sketch, "E39.55.0", {"center": v(0, -21.4) * mm, "radius": 0.1 * mm});
            skCircle(sketch, "E39.56.0", {"center": v(1.22, -21.37) * mm, "radius": 0.1 * mm});
            skCircle(sketch, "E39.57.0", {"center": v(2.44, -21.26) * mm, "radius": 0.1 * mm});
            skCircle(sketch, "E39.58.0", {"center": v(3.65, -21.09) * mm, "radius": 0.1 * mm});
            skCircle(sketch, "E39.59.0", {"center": v(4.85, -20.84) * mm, "radius": 0.1 * mm});
            skCircle(sketch, "E39.60.0", {"center": v(6.03, -20.53) * mm, "radius": 0.1 * mm});
            skCircle(sketch, "E39.61.0", {"center": v(7.2, -20.16) * mm, "radius": 0.1 * mm});
            skCircle(sketch, "E39.62.0", {"center": v(8.33, -19.71) * mm, "radius": 0.1 * mm});
            skCircle(sketch, "E39.63.0", {"center": v(9.44, -19.2) * mm, "radius": 0.1 * mm});
            skCircle(sketch, "E39.64.0", {"center": v(10.52, -18.63) * mm, "radius": 0.1 * mm});
            skCircle(sketch, "E39.65.0", {"center": v(11.57, -18) * mm, "radius": 0.1 * mm});
            skCircle(sketch, "E39.66.0", {"center": v(12.58, -17.31) * mm, "radius": 0.1 * mm});
            skCircle(sketch, "E39.67.0", {"center": v(13.55, -16.57) * mm, "radius": 0.1 * mm});
            skCircle(sketch, "E39.68.0", {"center": v(14.47, -15.77) * mm, "radius": 0.1 * mm});
            skCircle(sketch, "E39.69.0", {"center": v(15.35, -14.91) * mm, "radius": 0.1 * mm});
            skCircle(sketch, "E39.70.0", {"center": v(16.17, -14.01) * mm, "radius": 0.1 * mm});
            skCircle(sketch, "E39.71.0", {"center": v(16.95, -13.07) * mm, "radius": 0.1 * mm});
            skCircle(sketch, "E39.72.0", {"center": v(17.67, -12.08) * mm, "radius": 0.1 * mm});
            skCircle(sketch, "E39.73.0", {"center": v(18.33, -11.05) * mm, "radius": 0.1 * mm});
            skCircle(sketch, "E39.74.0", {"center": v(18.93, -9.99) * mm, "radius": 0.1 * mm});
            skCircle(sketch, "E39.75.0", {"center": v(19.47, -8.89) * mm, "radius": 0.1 * mm});
            skCircle(sketch, "E39.76.0", {"center": v(19.94, -7.76) * mm, "radius": 0.1 * mm});
            skCircle(sketch, "E39.77.0", {"center": v(20.35, -6.61) * mm, "radius": 0.1 * mm});
            skCircle(sketch, "E39.78.0", {"center": v(20.7, -5.44) * mm, "radius": 0.1 * mm});
            skCircle(sketch, "E39.79.0", {"center": v(20.97, -4.25) * mm, "radius": 0.1 * mm});
            skCircle(sketch, "E39.80.0", {"center": v(21.18, -3.05) * mm, "radius": 0.1 * mm});
            skCircle(sketch, "E39.81.0", {"center": v(21.32, -1.83) * mm, "radius": 0.1 * mm});
            skCircle(sketch, "E39.82.0", {"center": v(21.4, -0.61) * mm, "radius": 0.1 * mm});
            skCircle(sketch, "E39.83.0", {"center": v(21.4, 0.61) * mm, "radius": 0.1 * mm});
            skCircle(sketch, "E39.84.0", {"center": v(21.32, 1.83) * mm, "radius": 0.1 * mm});
            skCircle(sketch, "E39.85.0", {"center": v(21.18, 3.05) * mm, "radius": 0.1 * mm});
            skCircle(sketch, "E39.86.0", {"center": v(20.97, 4.25) * mm, "radius": 0.1 * mm});
            skCircle(sketch, "E39.87.0", {"center": v(20.7, 5.44) * mm, "radius": 0.1 * mm});
            skCircle(sketch, "E39.88.0", {"center": v(20.35, 6.61) * mm, "radius": 0.1 * mm});
            skCircle(sketch, "E39.89.0", {"center": v(19.94, 7.76) * mm, "radius": 0.1 * mm});
            skCircle(sketch, "E39.90.0", {"center": v(19.47, 8.89) * mm, "radius": 0.1 * mm});
            skCircle(sketch, "E39.91.0", {"center": v(18.93, 9.99) * mm, "radius": 0.1 * mm});
            skCircle(sketch, "E39.92.0", {"center": v(18.33, 11.05) * mm, "radius": 0.1 * mm});
            skCircle(sketch, "E39.93.0", {"center": v(17.67, 12.08) * mm, "radius": 0.1 * mm});
            skCircle(sketch, "E39.94.0", {"center": v(16.95, 13.07) * mm, "radius": 0.1 * mm});
            skCircle(sketch, "E39.95.0", {"center": v(16.17, 14.01) * mm, "radius": 0.1 * mm});
            skCircle(sketch, "E39.96.0", {"center": v(15.35, 14.91) * mm, "radius": 0.1 * mm});
            skCircle(sketch, "E39.97.0", {"center": v(14.47, 15.77) * mm, "radius": 0.1 * mm});
            skCircle(sketch, "E39.98.0", {"center": v(13.55, 16.57) * mm, "radius": 0.1 * mm});
            skCircle(sketch, "E39.99.0", {"center": v(12.58, 17.31) * mm, "radius": 0.1 * mm});
            skCircle(sketch, "E39.100.0", {"center": v(11.57, 18) * mm, "radius": 0.1 * mm});
            skCircle(sketch, "E39.101.0", {"center": v(10.52, 18.63) * mm, "radius": 0.1 * mm});
            skCircle(sketch, "E39.102.0", {"center": v(9.44, 19.2) * mm, "radius": 0.1 * mm});
            skCircle(sketch, "E39.103.0", {"center": v(8.33, 19.71) * mm, "radius": 0.1 * mm});
            skCircle(sketch, "E39.104.0", {"center": v(7.2, 20.16) * mm, "radius": 0.1 * mm});
            skCircle(sketch, "E39.105.0", {"center": v(6.03, 20.53) * mm, "radius": 0.1 * mm});
            skCircle(sketch, "E39.106.0", {"center": v(4.85, 20.84) * mm, "radius": 0.1 * mm});
            skCircle(sketch, "E39.107.0", {"center": v(3.65, 21.09) * mm, "radius": 0.1 * mm});
            skCircle(sketch, "E39.108.0", {"center": v(2.44, 21.26) * mm, "radius": 0.1 * mm});
            skCircle(sketch, "E39.109.0", {"center": v(1.22, 21.37) * mm, "radius": 0.1 * mm});
            skCircle(sketch, "E40.1.0", {"center": v(-1.22, 22.67) * mm, "radius": 0.1 * mm});
            skCircle(sketch, "E40.2.0", {"center": v(-2.43, 22.57) * mm, "radius": 0.1 * mm});
            skCircle(sketch, "E40.3.0", {"center": v(-3.64, 22.4) * mm, "radius": 0.1 * mm});
            skCircle(sketch, "E40.4.0", {"center": v(-4.84, 22.18) * mm, "radius": 0.1 * mm});
            skCircle(sketch, "E40.5.0", {"center": v(-6.02, 21.89) * mm, "radius": 0.1 * mm});
            skCircle(sketch, "E40.6.0", {"center": v(-7.19, 21.53) * mm, "radius": 0.1 * mm});
            skCircle(sketch, "E40.7.0", {"center": v(-8.33, 21.11) * mm, "radius": 0.1 * mm});
            skCircle(sketch, "E40.8.0", {"center": v(-9.46, 20.64) * mm, "radius": 0.1 * mm});
            skCircle(sketch, "E40.9.0", {"center": v(-10.55, 20.1) * mm, "radius": 0.1 * mm});
            skCircle(sketch, "E40.10.0", {"center": v(-11.61, 19.5) * mm, "radius": 0.1 * mm});
            skCircle(sketch, "E40.11.0", {"center": v(-12.64, 18.85) * mm, "radius": 0.1 * mm});
            skCircle(sketch, "E40.12.0", {"center": v(-13.64, 18.15) * mm, "radius": 0.1 * mm});
            skCircle(sketch, "E40.13.0", {"center": v(-14.6, 17.39) * mm, "radius": 0.1 * mm});
            skCircle(sketch, "E40.14.0", {"center": v(-15.5, 16.58) * mm, "radius": 0.1 * mm});
            skCircle(sketch, "E40.15.0", {"center": v(-16.37, 15.72) * mm, "radius": 0.1 * mm});
            skCircle(sketch, "E40.16.0", {"center": v(-17.2, 14.82) * mm, "radius": 0.1 * mm});
            skCircle(sketch, "E40.17.0", {"center": v(-17.96, 13.88) * mm, "radius": 0.1 * mm});
            skCircle(sketch, "E40.18.0", {"center": v(-18.68, 12.9) * mm, "radius": 0.1 * mm});
            skCircle(sketch, "E40.19.0", {"center": v(-19.35, 11.87) * mm, "radius": 0.1 * mm});
            skCircle(sketch, "E40.20.0", {"center": v(-19.96, 10.82) * mm, "radius": 0.1 * mm});
            skCircle(sketch, "E40.21.0", {"center": v(-20.5, 9.73) * mm, "radius": 0.1 * mm});
            skCircle(sketch, "E40.22.0", {"center": v(-21, 8.62) * mm, "radius": 0.1 * mm});
            skCircle(sketch, "E40.23.0", {"center": v(-21.43, 7.48) * mm, "radius": 0.1 * mm});
            skCircle(sketch, "E40.24.0", {"center": v(-21.8, 6.32) * mm, "radius": 0.1 * mm});
            skCircle(sketch, "E40.25.0", {"center": v(-22.11, 5.14) * mm, "radius": 0.1 * mm});
            skCircle(sketch, "E40.26.0", {"center": v(-22.36, 3.94) * mm, "radius": 0.1 * mm});
            skCircle(sketch, "E40.27.0", {"center": v(-22.53, 2.74) * mm, "radius": 0.1 * mm});
            skCircle(sketch, "E40.28.0", {"center": v(-22.65, 1.52) * mm, "radius": 0.1 * mm});
            skCircle(sketch, "E40.29.0", {"center": v(-22.7, 0.3) * mm, "radius": 0.1 * mm});
            skCircle(sketch, "E40.30.0", {"center": v(-22.68, -0.91) * mm, "radius": 0.1 * mm});
            skCircle(sketch, "E40.31.0", {"center": v(-22.6, -2.13) * mm, "radius": 0.1 * mm});
            skCircle(sketch, "E40.32.0", {"center": v(-22.45, -3.34) * mm, "radius": 0.1 * mm});
            skCircle(sketch, "E40.33.0", {"center": v(-22.24, -4.54) * mm, "radius": 0.1 * mm});
            skCircle(sketch, "E40.34.0", {"center": v(-21.97, -5.73) * mm, "radius": 0.1 * mm});
            skCircle(sketch, "E40.35.0", {"center": v(-21.63, -6.9) * mm, "radius": 0.1 * mm});
            skCircle(sketch, "E40.36.0", {"center": v(-21.22, -8.05) * mm, "radius": 0.1 * mm});
            skCircle(sketch, "E40.37.0", {"center": v(-20.76, -9.18) * mm, "radius": 0.1 * mm});
            skCircle(sketch, "E40.38.0", {"center": v(-20.24, -10.28) * mm, "radius": 0.1 * mm});
            skCircle(sketch, "E40.39.0", {"center": v(-19.66, -11.35) * mm, "radius": 0.1 * mm});
            skCircle(sketch, "E40.40.0", {"center": v(-19.02, -12.39) * mm, "radius": 0.1 * mm});
            skCircle(sketch, "E40.41.0", {"center": v(-18.33, -13.4) * mm, "radius": 0.1 * mm});
            skCircle(sketch, "E40.42.0", {"center": v(-17.58, -14.36) * mm, "radius": 0.1 * mm});
            skCircle(sketch, "E40.43.0", {"center": v(-16.79, -15.28) * mm, "radius": 0.1 * mm});
            skCircle(sketch, "E40.44.0", {"center": v(-15.94, -16.16) * mm, "radius": 0.1 * mm});
            skCircle(sketch, "E40.45.0", {"center": v(-15.05, -17) * mm, "radius": 0.1 * mm});
            skCircle(sketch, "E40.46.0", {"center": v(-14.12, -17.77) * mm, "radius": 0.1 * mm});
            skCircle(sketch, "E40.47.0", {"center": v(-13.14, -18.5) * mm, "radius": 0.1 * mm});
            skCircle(sketch, "E40.48.0", {"center": v(-12.13, -19.19) * mm, "radius": 0.1 * mm});
            skCircle(sketch, "E40.49.0", {"center": v(-11.09, -19.8) * mm, "radius": 0.1 * mm});
            skCircle(sketch, "E40.50.0", {"center": v(-10, -20.38) * mm, "radius": 0.1 * mm});
            skCircle(sketch, "E40.51.0", {"center": v(-8.9, -20.88) * mm, "radius": 0.1 * mm});
            skCircle(sketch, "E40.52.0", {"center": v(-7.76, -21.33) * mm, "radius": 0.1 * mm});
            skCircle(sketch, "E40.53.0", {"center": v(-6.6, -21.72) * mm, "radius": 0.1 * mm});
            skCircle(sketch, "E40.54.0", {"center": v(-5.43, -22.04) * mm, "radius": 0.1 * mm});
            skCircle(sketch, "E40.55.0", {"center": v(-4.24, -22.3) * mm, "radius": 0.1 * mm});
            skCircle(sketch, "E40.56.0", {"center": v(-3.04, -22.5) * mm, "radius": 0.1 * mm});
            skCircle(sketch, "E40.57.0", {"center": v(-1.83, -22.63) * mm, "radius": 0.1 * mm});
            skCircle(sketch, "E40.58.0", {"center": v(-0.6, -22.7) * mm, "radius": 0.1 * mm});
            skCircle(sketch, "E40.59.0", {"center": v(0.6, -22.7) * mm, "radius": 0.1 * mm});
            skCircle(sketch, "E40.60.0", {"center": v(1.83, -22.63) * mm, "radius": 0.1 * mm});
            skCircle(sketch, "E40.61.0", {"center": v(3.04, -22.5) * mm, "radius": 0.1 * mm});
            skCircle(sketch, "E40.62.0", {"center": v(4.24, -22.3) * mm, "radius": 0.1 * mm});
            skCircle(sketch, "E40.63.0", {"center": v(5.43, -22.04) * mm, "radius": 0.1 * mm});
            skCircle(sketch, "E40.64.0", {"center": v(6.6, -21.72) * mm, "radius": 0.1 * mm});
            skCircle(sketch, "E40.65.0", {"center": v(7.76, -21.33) * mm, "radius": 0.1 * mm});
            skCircle(sketch, "E40.66.0", {"center": v(8.9, -20.88) * mm, "radius": 0.1 * mm});
            skCircle(sketch, "E40.67.0", {"center": v(10, -20.38) * mm, "radius": 0.1 * mm});
            skCircle(sketch, "E40.68.0", {"center": v(11.09, -19.8) * mm, "radius": 0.1 * mm});
            skCircle(sketch, "E40.69.0", {"center": v(12.13, -19.19) * mm, "radius": 0.1 * mm});
            skCircle(sketch, "E40.70.0", {"center": v(13.14, -18.5) * mm, "radius": 0.1 * mm});
            skCircle(sketch, "E40.71.0", {"center": v(14.12, -17.77) * mm, "radius": 0.1 * mm});
            skCircle(sketch, "E40.72.0", {"center": v(15.05, -17) * mm, "radius": 0.1 * mm});
            skCircle(sketch, "E40.73.0", {"center": v(15.94, -16.16) * mm, "radius": 0.1 * mm});
            skCircle(sketch, "E40.74.0", {"center": v(16.79, -15.28) * mm, "radius": 0.1 * mm});
            skCircle(sketch, "E40.75.0", {"center": v(17.58, -14.36) * mm, "radius": 0.1 * mm});
            skCircle(sketch, "E40.76.0", {"center": v(18.33, -13.4) * mm, "radius": 0.1 * mm});
            skCircle(sketch, "E40.77.0", {"center": v(19.02, -12.39) * mm, "radius": 0.1 * mm});
            skCircle(sketch, "E40.78.0", {"center": v(19.66, -11.35) * mm, "radius": 0.1 * mm});
            skCircle(sketch, "E40.79.0", {"center": v(20.24, -10.28) * mm, "radius": 0.1 * mm});
            skCircle(sketch, "E40.80.0", {"center": v(20.76, -9.18) * mm, "radius": 0.1 * mm});
            skCircle(sketch, "E40.81.0", {"center": v(21.22, -8.05) * mm, "radius": 0.1 * mm});
            skCircle(sketch, "E40.82.0", {"center": v(21.63, -6.9) * mm, "radius": 0.1 * mm});
            skCircle(sketch, "E40.83.0", {"center": v(21.97, -5.73) * mm, "radius": 0.1 * mm});
            skCircle(sketch, "E40.84.0", {"center": v(22.24, -4.54) * mm, "radius": 0.1 * mm});
            skCircle(sketch, "E40.85.0", {"center": v(22.45, -3.34) * mm, "radius": 0.1 * mm});
            skCircle(sketch, "E40.86.0", {"center": v(22.6, -2.13) * mm, "radius": 0.1 * mm});
            skCircle(sketch, "E40.87.0", {"center": v(22.68, -0.91) * mm, "radius": 0.1 * mm});
            skCircle(sketch, "E40.88.0", {"center": v(22.7, 0.3) * mm, "radius": 0.1 * mm});
            skCircle(sketch, "E40.89.0", {"center": v(22.65, 1.52) * mm, "radius": 0.1 * mm});
            skCircle(sketch, "E40.90.0", {"center": v(22.53, 2.74) * mm, "radius": 0.1 * mm});
            skCircle(sketch, "E40.91.0", {"center": v(22.36, 3.94) * mm, "radius": 0.1 * mm});
            skCircle(sketch, "E40.92.0", {"center": v(22.11, 5.14) * mm, "radius": 0.1 * mm});
            skCircle(sketch, "E40.93.0", {"center": v(21.8, 6.32) * mm, "radius": 0.1 * mm});
            skCircle(sketch, "E40.94.0", {"center": v(21.43, 7.48) * mm, "radius": 0.1 * mm});
            skCircle(sketch, "E40.95.0", {"center": v(21, 8.62) * mm, "radius": 0.1 * mm});
            skCircle(sketch, "E40.96.0", {"center": v(20.5, 9.73) * mm, "radius": 0.1 * mm});
            skCircle(sketch, "E40.97.0", {"center": v(19.96, 10.82) * mm, "radius": 0.1 * mm});
            skCircle(sketch, "E40.98.0", {"center": v(19.35, 11.87) * mm, "radius": 0.1 * mm});
            skCircle(sketch, "E40.99.0", {"center": v(18.68, 12.9) * mm, "radius": 0.1 * mm});
            skCircle(sketch, "E40.100.0", {"center": v(17.96, 13.88) * mm, "radius": 0.1 * mm});
            skCircle(sketch, "E40.101.0", {"center": v(17.2, 14.82) * mm, "radius": 0.1 * mm});
            skCircle(sketch, "E40.102.0", {"center": v(16.37, 15.72) * mm, "radius": 0.1 * mm});
            skCircle(sketch, "E40.103.0", {"center": v(15.5, 16.58) * mm, "radius": 0.1 * mm});
            skCircle(sketch, "E40.104.0", {"center": v(14.6, 17.39) * mm, "radius": 0.1 * mm});
            skCircle(sketch, "E40.105.0", {"center": v(13.64, 18.15) * mm, "radius": 0.1 * mm});
            skCircle(sketch, "E40.106.0", {"center": v(12.64, 18.85) * mm, "radius": 0.1 * mm});
            skCircle(sketch, "E40.107.0", {"center": v(11.61, 19.5) * mm, "radius": 0.1 * mm});
            skCircle(sketch, "E40.108.0", {"center": v(10.55, 20.1) * mm, "radius": 0.1 * mm});
            skCircle(sketch, "E40.109.0", {"center": v(9.46, 20.64) * mm, "radius": 0.1 * mm});
            skCircle(sketch, "E40.110.0", {"center": v(8.33, 21.11) * mm, "radius": 0.1 * mm});
            skCircle(sketch, "E40.111.0", {"center": v(7.19, 21.53) * mm, "radius": 0.1 * mm});
            skCircle(sketch, "E40.112.0", {"center": v(6.02, 21.89) * mm, "radius": 0.1 * mm});
            skCircle(sketch, "E40.113.0", {"center": v(4.84, 22.18) * mm, "radius": 0.1 * mm});
            skCircle(sketch, "E40.114.0", {"center": v(3.64, 22.4) * mm, "radius": 0.1 * mm});
            skCircle(sketch, "E40.115.0", {"center": v(2.43, 22.57) * mm, "radius": 0.1 * mm});
            skCircle(sketch, "E40.116.0", {"center": v(1.22, 22.67) * mm, "radius": 0.1 * mm});
            skCircle(sketch, "E41.1.0", {"center": v(-1.22, 23.97) * mm, "radius": 0.1 * mm});
            skCircle(sketch, "E41.2.0", {"center": v(-2.43, 23.88) * mm, "radius": 0.1 * mm});
            skCircle(sketch, "E41.3.0", {"center": v(-3.63, 23.72) * mm, "radius": 0.1 * mm});
            skCircle(sketch, "E41.4.0", {"center": v(-4.83, 23.5) * mm, "radius": 0.1 * mm});
            skCircle(sketch, "E41.5.0", {"center": v(-6.02, 23.23) * mm, "radius": 0.1 * mm});
            skCircle(sketch, "E41.6.0", {"center": v(-7.18, 22.9) * mm, "radius": 0.1 * mm});
            skCircle(sketch, "E41.7.0", {"center": v(-8.34, 22.5) * mm, "radius": 0.1 * mm});
            skCircle(sketch, "E41.8.0", {"center": v(-9.46, 22.05) * mm, "radius": 0.1 * mm});
            skCircle(sketch, "E41.9.0", {"center": v(-10.57, 21.55) * mm, "radius": 0.1 * mm});
            skCircle(sketch, "E41.10.0", {"center": v(-11.65, 20.98) * mm, "radius": 0.1 * mm});
            skCircle(sketch, "E41.11.0", {"center": v(-12.7, 20.37) * mm, "radius": 0.1 * mm});
            skCircle(sketch, "E41.12.0", {"center": v(-13.71, 19.7) * mm, "radius": 0.1 * mm});
            skCircle(sketch, "E41.13.0", {"center": v(-14.7, 18.98) * mm, "radius": 0.1 * mm});
            skCircle(sketch, "E41.14.0", {"center": v(-15.63, 18.21) * mm, "radius": 0.1 * mm});
            skCircle(sketch, "E41.15.0", {"center": v(-16.54, 17.4) * mm, "radius": 0.1 * mm});
            skCircle(sketch, "E41.16.0", {"center": v(-17.4, 16.54) * mm, "radius": 0.1 * mm});
            skCircle(sketch, "E41.17.0", {"center": v(-18.21, 15.63) * mm, "radius": 0.1 * mm});
            skCircle(sketch, "E41.18.0", {"center": v(-18.98, 14.7) * mm, "radius": 0.1 * mm});
            skCircle(sketch, "E41.19.0", {"center": v(-19.7, 13.71) * mm, "radius": 0.1 * mm});
            skCircle(sketch, "E41.20.0", {"center": v(-20.37, 12.7) * mm, "radius": 0.1 * mm});
            skCircle(sketch, "E41.21.0", {"center": v(-20.98, 11.65) * mm, "radius": 0.1 * mm});
            skCircle(sketch, "E41.22.0", {"center": v(-21.55, 10.57) * mm, "radius": 0.1 * mm});
            skCircle(sketch, "E41.23.0", {"center": v(-22.05, 9.46) * mm, "radius": 0.1 * mm});
            skCircle(sketch, "E41.24.0", {"center": v(-22.5, 8.34) * mm, "radius": 0.1 * mm});
            skCircle(sketch, "E41.25.0", {"center": v(-22.9, 7.18) * mm, "radius": 0.1 * mm});
            skCircle(sketch, "E41.26.0", {"center": v(-23.23, 6.02) * mm, "radius": 0.1 * mm});
            skCircle(sketch, "E41.27.0", {"center": v(-23.5, 4.83) * mm, "radius": 0.1 * mm});
            skCircle(sketch, "E41.28.0", {"center": v(-23.72, 3.63) * mm, "radius": 0.1 * mm});
            skCircle(sketch, "E41.29.0", {"center": v(-23.88, 2.43) * mm, "radius": 0.1 * mm});
            skCircle(sketch, "E41.30.0", {"center": v(-23.97, 1.22) * mm, "radius": 0.1 * mm});
            skCircle(sketch, "E41.31.0", {"center": v(-24, 0) * mm, "radius": 0.1 * mm});
            skCircle(sketch, "E41.32.0", {"center": v(-23.97, -1.22) * mm, "radius": 0.1 * mm});
            skCircle(sketch, "E41.33.0", {"center": v(-23.88, -2.43) * mm, "radius": 0.1 * mm});
            skCircle(sketch, "E41.34.0", {"center": v(-23.72, -3.63) * mm, "radius": 0.1 * mm});
            skCircle(sketch, "E41.35.0", {"center": v(-23.5, -4.83) * mm, "radius": 0.1 * mm});
            skCircle(sketch, "E41.36.0", {"center": v(-23.23, -6.02) * mm, "radius": 0.1 * mm});
            skCircle(sketch, "E41.37.0", {"center": v(-22.9, -7.18) * mm, "radius": 0.1 * mm});
            skCircle(sketch, "E41.38.0", {"center": v(-22.5, -8.34) * mm, "radius": 0.1 * mm});
            skCircle(sketch, "E41.39.0", {"center": v(-22.05, -9.46) * mm, "radius": 0.1 * mm});
            skCircle(sketch, "E41.40.0", {"center": v(-21.55, -10.57) * mm, "radius": 0.1 * mm});
            skCircle(sketch, "E41.41.0", {"center": v(-20.98, -11.65) * mm, "radius": 0.1 * mm});
            skCircle(sketch, "E41.42.0", {"center": v(-20.37, -12.7) * mm, "radius": 0.1 * mm});
            skCircle(sketch, "E41.43.0", {"center": v(-19.7, -13.71) * mm, "radius": 0.1 * mm});
            skCircle(sketch, "E41.44.0", {"center": v(-18.98, -14.7) * mm, "radius": 0.1 * mm});
            skCircle(sketch, "E41.45.0", {"center": v(-18.21, -15.63) * mm, "radius": 0.1 * mm});
            skCircle(sketch, "E41.46.0", {"center": v(-17.4, -16.54) * mm, "radius": 0.1 * mm});
            skCircle(sketch, "E41.47.0", {"center": v(-16.54, -17.4) * mm, "radius": 0.1 * mm});
            skCircle(sketch, "E41.48.0", {"center": v(-15.63, -18.21) * mm, "radius": 0.1 * mm});
            skCircle(sketch, "E41.49.0", {"center": v(-14.7, -18.98) * mm, "radius": 0.1 * mm});
            skCircle(sketch, "E41.50.0", {"center": v(-13.71, -19.7) * mm, "radius": 0.1 * mm});
            skCircle(sketch, "E41.51.0", {"center": v(-12.7, -20.37) * mm, "radius": 0.1 * mm});
            skCircle(sketch, "E41.52.0", {"center": v(-11.65, -20.98) * mm, "radius": 0.1 * mm});
            skCircle(sketch, "E41.53.0", {"center": v(-10.57, -21.55) * mm, "radius": 0.1 * mm});
            skCircle(sketch, "E41.54.0", {"center": v(-9.46, -22.05) * mm, "radius": 0.1 * mm});
            skCircle(sketch, "E41.55.0", {"center": v(-8.34, -22.5) * mm, "radius": 0.1 * mm});
            skCircle(sketch, "E41.56.0", {"center": v(-7.18, -22.9) * mm, "radius": 0.1 * mm});
            skCircle(sketch, "E41.57.0", {"center": v(-6.02, -23.23) * mm, "radius": 0.1 * mm});
            skCircle(sketch, "E41.58.0", {"center": v(-4.83, -23.5) * mm, "radius": 0.1 * mm});
            skCircle(sketch, "E41.59.0", {"center": v(-3.63, -23.72) * mm, "radius": 0.1 * mm});
            skCircle(sketch, "E41.60.0", {"center": v(-2.43, -23.88) * mm, "radius": 0.1 * mm});
            skCircle(sketch, "E41.61.0", {"center": v(-1.22, -23.97) * mm, "radius": 0.1 * mm});
            skCircle(sketch, "E41.62.0", {"center": v(0, -24) * mm, "radius": 0.1 * mm});
            skCircle(sketch, "E41.63.0", {"center": v(1.22, -23.97) * mm, "radius": 0.1 * mm});
            skCircle(sketch, "E41.64.0", {"center": v(2.43, -23.88) * mm, "radius": 0.1 * mm});
            skCircle(sketch, "E41.65.0", {"center": v(3.63, -23.72) * mm, "radius": 0.1 * mm});
            skCircle(sketch, "E41.66.0", {"center": v(4.83, -23.5) * mm, "radius": 0.1 * mm});
            skCircle(sketch, "E41.67.0", {"center": v(6.02, -23.23) * mm, "radius": 0.1 * mm});
            skCircle(sketch, "E41.68.0", {"center": v(7.18, -22.9) * mm, "radius": 0.1 * mm});
            skCircle(sketch, "E41.69.0", {"center": v(8.34, -22.5) * mm, "radius": 0.1 * mm});
            skCircle(sketch, "E41.70.0", {"center": v(9.46, -22.05) * mm, "radius": 0.1 * mm});
            skCircle(sketch, "E41.71.0", {"center": v(10.57, -21.55) * mm, "radius": 0.1 * mm});
            skCircle(sketch, "E41.72.0", {"center": v(11.65, -20.98) * mm, "radius": 0.1 * mm});
            skCircle(sketch, "E41.73.0", {"center": v(12.7, -20.37) * mm, "radius": 0.1 * mm});
            skCircle(sketch, "E41.74.0", {"center": v(13.71, -19.7) * mm, "radius": 0.1 * mm});
            skCircle(sketch, "E41.75.0", {"center": v(14.7, -18.98) * mm, "radius": 0.1 * mm});
            skCircle(sketch, "E41.76.0", {"center": v(15.63, -18.21) * mm, "radius": 0.1 * mm});
            skCircle(sketch, "E41.77.0", {"center": v(16.54, -17.4) * mm, "radius": 0.1 * mm});
            skCircle(sketch, "E41.78.0", {"center": v(17.4, -16.54) * mm, "radius": 0.1 * mm});
            skCircle(sketch, "E41.79.0", {"center": v(18.21, -15.63) * mm, "radius": 0.1 * mm});
            skCircle(sketch, "E41.80.0", {"center": v(18.98, -14.7) * mm, "radius": 0.1 * mm});
            skCircle(sketch, "E41.81.0", {"center": v(19.7, -13.71) * mm, "radius": 0.1 * mm});
            skCircle(sketch, "E41.82.0", {"center": v(20.37, -12.7) * mm, "radius": 0.1 * mm});
            skCircle(sketch, "E41.83.0", {"center": v(20.98, -11.65) * mm, "radius": 0.1 * mm});
            skCircle(sketch, "E41.84.0", {"center": v(21.55, -10.57) * mm, "radius": 0.1 * mm});
            skCircle(sketch, "E41.85.0", {"center": v(22.05, -9.46) * mm, "radius": 0.1 * mm});
            skCircle(sketch, "E41.86.0", {"center": v(22.5, -8.34) * mm, "radius": 0.1 * mm});
            skCircle(sketch, "E41.87.0", {"center": v(22.9, -7.18) * mm, "radius": 0.1 * mm});
            skCircle(sketch, "E41.88.0", {"center": v(23.23, -6.02) * mm, "radius": 0.1 * mm});
            skCircle(sketch, "E41.89.0", {"center": v(23.5, -4.83) * mm, "radius": 0.1 * mm});
            skCircle(sketch, "E41.90.0", {"center": v(23.72, -3.63) * mm, "radius": 0.1 * mm});
            skCircle(sketch, "E41.91.0", {"center": v(23.88, -2.43) * mm, "radius": 0.1 * mm});
            skCircle(sketch, "E41.92.0", {"center": v(23.97, -1.22) * mm, "radius": 0.1 * mm});
            skCircle(sketch, "E41.93.0", {"center": v(24, 0) * mm, "radius": 0.1 * mm});
            skCircle(sketch, "E41.94.0", {"center": v(23.97, 1.22) * mm, "radius": 0.1 * mm});
            skCircle(sketch, "E41.95.0", {"center": v(23.88, 2.43) * mm, "radius": 0.1 * mm});
            skCircle(sketch, "E41.96.0", {"center": v(23.72, 3.63) * mm, "radius": 0.1 * mm});
            skCircle(sketch, "E41.97.0", {"center": v(23.5, 4.83) * mm, "radius": 0.1 * mm});
            skCircle(sketch, "E41.98.0", {"center": v(23.23, 6.02) * mm, "radius": 0.1 * mm});
            skCircle(sketch, "E41.99.0", {"center": v(22.9, 7.18) * mm, "radius": 0.1 * mm});
            skCircle(sketch, "E41.100.0", {"center": v(22.5, 8.34) * mm, "radius": 0.1 * mm});
            skCircle(sketch, "E41.101.0", {"center": v(22.05, 9.46) * mm, "radius": 0.1 * mm});
            skCircle(sketch, "E41.102.0", {"center": v(21.55, 10.57) * mm, "radius": 0.1 * mm});
            skCircle(sketch, "E41.103.0", {"center": v(20.98, 11.65) * mm, "radius": 0.1 * mm});
            skCircle(sketch, "E41.104.0", {"center": v(20.37, 12.7) * mm, "radius": 0.1 * mm});
            skCircle(sketch, "E41.105.0", {"center": v(19.7, 13.71) * mm, "radius": 0.1 * mm});
            skCircle(sketch, "E41.106.0", {"center": v(18.98, 14.7) * mm, "radius": 0.1 * mm});
            skCircle(sketch, "E41.107.0", {"center": v(18.21, 15.63) * mm, "radius": 0.1 * mm});
            skCircle(sketch, "E41.108.0", {"center": v(17.4, 16.54) * mm, "radius": 0.1 * mm});
            skCircle(sketch, "E41.109.0", {"center": v(16.54, 17.4) * mm, "radius": 0.1 * mm});
            skCircle(sketch, "E41.110.0", {"center": v(15.63, 18.21) * mm, "radius": 0.1 * mm});
            skCircle(sketch, "E41.111.0", {"center": v(14.7, 18.98) * mm, "radius": 0.1 * mm});
            skCircle(sketch, "E41.112.0", {"center": v(13.71, 19.7) * mm, "radius": 0.1 * mm});
            skCircle(sketch, "E41.113.0", {"center": v(12.7, 20.37) * mm, "radius": 0.1 * mm});
            skCircle(sketch, "E41.114.0", {"center": v(11.65, 20.98) * mm, "radius": 0.1 * mm});
            skCircle(sketch, "E41.115.0", {"center": v(10.57, 21.55) * mm, "radius": 0.1 * mm});
            skCircle(sketch, "E41.116.0", {"center": v(9.46, 22.05) * mm, "radius": 0.1 * mm});
            skCircle(sketch, "E41.117.0", {"center": v(8.34, 22.5) * mm, "radius": 0.1 * mm});
            skCircle(sketch, "E41.118.0", {"center": v(7.18, 22.9) * mm, "radius": 0.1 * mm});
            skCircle(sketch, "E41.119.0", {"center": v(6.02, 23.23) * mm, "radius": 0.1 * mm});
            skCircle(sketch, "E41.120.0", {"center": v(4.83, 23.5) * mm, "radius": 0.1 * mm});
            skCircle(sketch, "E41.121.0", {"center": v(3.63, 23.72) * mm, "radius": 0.1 * mm});
            skCircle(sketch, "E41.122.0", {"center": v(2.43, 23.88) * mm, "radius": 0.1 * mm});
            skCircle(sketch, "E41.123.0", {"center": v(1.22, 23.97) * mm, "radius": 0.1 * mm});
            skCircle(sketch, "E42.1.0", {"center": v(-1.21, 25.27) * mm, "radius": 0.1 * mm});
            skCircle(sketch, "E42.2.0", {"center": v(-2.42, 25.18) * mm, "radius": 0.1 * mm});
            skCircle(sketch, "E42.3.0", {"center": v(-3.63, 25.04) * mm, "radius": 0.1 * mm});
            skCircle(sketch, "E42.4.0", {"center": v(-4.82, 24.84) * mm, "radius": 0.1 * mm});
            skCircle(sketch, "E42.5.0", {"center": v(-6, 24.58) * mm, "radius": 0.1 * mm});
            skCircle(sketch, "E42.6.0", {"center": v(-7.18, 24.26) * mm, "radius": 0.1 * mm});
            skCircle(sketch, "E42.7.0", {"center": v(-8.34, 23.89) * mm, "radius": 0.1 * mm});
            skCircle(sketch, "E42.8.0", {"center": v(-9.47, 23.46) * mm, "radius": 0.1 * mm});
            skCircle(sketch, "E42.9.0", {"center": v(-10.59, 22.98) * mm, "radius": 0.1 * mm});
            skCircle(sketch, "E42.10.0", {"center": v(-11.67, 22.45) * mm, "radius": 0.1 * mm});
            skCircle(sketch, "E42.11.0", {"center": v(-12.74, 21.86) * mm, "radius": 0.1 * mm});
            skCircle(sketch, "E42.12.0", {"center": v(-13.77, 21.22) * mm, "radius": 0.1 * mm});
            skCircle(sketch, "E42.13.0", {"center": v(-14.77, 20.54) * mm, "radius": 0.1 * mm});
            skCircle(sketch, "E42.14.0", {"center": v(-15.74, 19.8) * mm, "radius": 0.1 * mm});
            skCircle(sketch, "E42.15.0", {"center": v(-16.67, 19.03) * mm, "radius": 0.1 * mm});
            skCircle(sketch, "E42.16.0", {"center": v(-17.57, 18.2) * mm, "radius": 0.1 * mm});
            skCircle(sketch, "E42.17.0", {"center": v(-18.42, 17.35) * mm, "radius": 0.1 * mm});
            skCircle(sketch, "E42.18.0", {"center": v(-19.23, 16.44) * mm, "radius": 0.1 * mm});
            skCircle(sketch, "E42.19.0", {"center": v(-20, 15.5) * mm, "radius": 0.1 * mm});
            skCircle(sketch, "E42.20.0", {"center": v(-20.71, 14.53) * mm, "radius": 0.1 * mm});
            skCircle(sketch, "E42.21.0", {"center": v(-21.39, 13.52) * mm, "radius": 0.1 * mm});
            skCircle(sketch, "E42.22.0", {"center": v(-22.01, 12.47) * mm, "radius": 0.1 * mm});
            skCircle(sketch, "E42.23.0", {"center": v(-22.58, 11.4) * mm, "radius": 0.1 * mm});
            skCircle(sketch, "E42.24.0", {"center": v(-23.1, 10.3) * mm, "radius": 0.1 * mm});
            skCircle(sketch, "E42.25.0", {"center": v(-23.57, 9.19) * mm, "radius": 0.1 * mm});
            skCircle(sketch, "E42.26.0", {"center": v(-23.99, 8.05) * mm, "radius": 0.1 * mm});
            skCircle(sketch, "E42.27.0", {"center": v(-24.34, 6.89) * mm, "radius": 0.1 * mm});
            skCircle(sketch, "E42.28.0", {"center": v(-24.65, 5.71) * mm, "radius": 0.1 * mm});
            skCircle(sketch, "E42.29.0", {"center": v(-24.9, 4.53) * mm, "radius": 0.1 * mm});
            skCircle(sketch, "E42.30.0", {"center": v(-25.08, 3.33) * mm, "radius": 0.1 * mm});
            skCircle(sketch, "E42.31.0", {"center": v(-25.21, 2.12) * mm, "radius": 0.1 * mm});
            skCircle(sketch, "E42.32.0", {"center": v(-25.28, 0.9) * mm, "radius": 0.1 * mm});
            skCircle(sketch, "E42.33.0", {"center": v(-25.3, -0.3) * mm, "radius": 0.1 * mm});
            skCircle(sketch, "E42.34.0", {"center": v(-25.25, -1.52) * mm, "radius": 0.1 * mm});
            skCircle(sketch, "E42.35.0", {"center": v(-25.15, -2.73) * mm, "radius": 0.1 * mm});
            skCircle(sketch, "E42.36.0", {"center": v(-25, -3.93) * mm, "radius": 0.1 * mm});
            skCircle(sketch, "E42.37.0", {"center": v(-24.78, -5.12) * mm, "radius": 0.1 * mm});
            skCircle(sketch, "E42.38.0", {"center": v(-24.5, -6.3) * mm, "radius": 0.1 * mm});
            skCircle(sketch, "E42.39.0", {"center": v(-24.17, -7.47) * mm, "radius": 0.1 * mm});
            skCircle(sketch, "E42.40.0", {"center": v(-23.79, -8.62) * mm, "radius": 0.1 * mm});
            skCircle(sketch, "E42.41.0", {"center": v(-23.35, -9.75) * mm, "radius": 0.1 * mm});
            skCircle(sketch, "E42.42.0", {"center": v(-22.85, -10.86) * mm, "radius": 0.1 * mm});
            skCircle(sketch, "E42.43.0", {"center": v(-22.3, -11.94) * mm, "radius": 0.1 * mm});
            skCircle(sketch, "E42.44.0", {"center": v(-21.7, -13) * mm, "radius": 0.1 * mm});
            skCircle(sketch, "E42.45.0", {"center": v(-21.06, -14.02) * mm, "radius": 0.1 * mm});
            skCircle(sketch, "E42.46.0", {"center": v(-20.36, -15.02) * mm, "radius": 0.1 * mm});
            skCircle(sketch, "E42.47.0", {"center": v(-19.62, -15.98) * mm, "radius": 0.1 * mm});
            skCircle(sketch, "E42.48.0", {"center": v(-18.83, -16.9) * mm, "radius": 0.1 * mm});
            skCircle(sketch, "E42.49.0", {"center": v(-18, -17.78) * mm, "radius": 0.1 * mm});
            skCircle(sketch, "E42.50.0", {"center": v(-17.12, -18.62) * mm, "radius": 0.1 * mm});
            skCircle(sketch, "E42.51.0", {"center": v(-16.21, -19.42) * mm, "radius": 0.1 * mm});
            skCircle(sketch, "E42.52.0", {"center": v(-15.26, -20.18) * mm, "radius": 0.1 * mm});
            skCircle(sketch, "E42.53.0", {"center": v(-14.28, -20.89) * mm, "radius": 0.1 * mm});
            skCircle(sketch, "E42.54.0", {"center": v(-13.26, -21.55) * mm, "radius": 0.1 * mm});
            skCircle(sketch, "E42.55.0", {"center": v(-12.2, -22.16) * mm, "radius": 0.1 * mm});
            skCircle(sketch, "E42.56.0", {"center": v(-11.13, -22.72) * mm, "radius": 0.1 * mm});
            skCircle(sketch, "E42.57.0", {"center": v(-10.03, -23.23) * mm, "radius": 0.1 * mm});
            skCircle(sketch, "E42.58.0", {"center": v(-8.9, -23.68) * mm, "radius": 0.1 * mm});
            skCircle(sketch, "E42.59.0", {"center": v(-7.76, -24.08) * mm, "radius": 0.1 * mm});
            skCircle(sketch, "E42.60.0", {"center": v(-6.6, -24.42) * mm, "radius": 0.1 * mm});
            skCircle(sketch, "E42.61.0", {"center": v(-5.42, -24.71) * mm, "radius": 0.1 * mm});
            skCircle(sketch, "E42.62.0", {"center": v(-4.23, -24.94) * mm, "radius": 0.1 * mm});
            skCircle(sketch, "E42.63.0", {"center": v(-3.03, -25.12) * mm, "radius": 0.1 * mm});
            skCircle(sketch, "E42.64.0", {"center": v(-1.82, -25.23) * mm, "radius": 0.1 * mm});
            skCircle(sketch, "E42.65.0", {"center": v(-0.6, -25.3) * mm, "radius": 0.1 * mm});
            skCircle(sketch, "E42.66.0", {"center": v(0.6, -25.3) * mm, "radius": 0.1 * mm});
            skCircle(sketch, "E42.67.0", {"center": v(1.82, -25.23) * mm, "radius": 0.1 * mm});
            skCircle(sketch, "E42.68.0", {"center": v(3.03, -25.12) * mm, "radius": 0.1 * mm});
            skCircle(sketch, "E42.69.0", {"center": v(4.23, -24.94) * mm, "radius": 0.1 * mm});
            skCircle(sketch, "E42.70.0", {"center": v(5.42, -24.71) * mm, "radius": 0.1 * mm});
            skCircle(sketch, "E42.71.0", {"center": v(6.6, -24.42) * mm, "radius": 0.1 * mm});
            skCircle(sketch, "E42.72.0", {"center": v(7.76, -24.08) * mm, "radius": 0.1 * mm});
            skCircle(sketch, "E42.73.0", {"center": v(8.9, -23.68) * mm, "radius": 0.1 * mm});
            skCircle(sketch, "E42.74.0", {"center": v(10.03, -23.23) * mm, "radius": 0.1 * mm});
            skCircle(sketch, "E42.75.0", {"center": v(11.13, -22.72) * mm, "radius": 0.1 * mm});
            skCircle(sketch, "E42.76.0", {"center": v(12.2, -22.16) * mm, "radius": 0.1 * mm});
            skCircle(sketch, "E42.77.0", {"center": v(13.26, -21.55) * mm, "radius": 0.1 * mm});
            skCircle(sketch, "E42.78.0", {"center": v(14.28, -20.89) * mm, "radius": 0.1 * mm});
            skCircle(sketch, "E42.79.0", {"center": v(15.26, -20.18) * mm, "radius": 0.1 * mm});
            skCircle(sketch, "E42.80.0", {"center": v(16.21, -19.42) * mm, "radius": 0.1 * mm});
            skCircle(sketch, "E42.81.0", {"center": v(17.12, -18.62) * mm, "radius": 0.1 * mm});
            skCircle(sketch, "E42.82.0", {"center": v(18, -17.78) * mm, "radius": 0.1 * mm});
            skCircle(sketch, "E42.83.0", {"center": v(18.83, -16.9) * mm, "radius": 0.1 * mm});
            skCircle(sketch, "E42.84.0", {"center": v(19.62, -15.98) * mm, "radius": 0.1 * mm});
            skCircle(sketch, "E42.85.0", {"center": v(20.36, -15.02) * mm, "radius": 0.1 * mm});
            skCircle(sketch, "E42.86.0", {"center": v(21.06, -14.02) * mm, "radius": 0.1 * mm});
            skCircle(sketch, "E42.87.0", {"center": v(21.7, -13) * mm, "radius": 0.1 * mm});
            skCircle(sketch, "E42.88.0", {"center": v(22.3, -11.94) * mm, "radius": 0.1 * mm});
            skCircle(sketch, "E42.89.0", {"center": v(22.85, -10.86) * mm, "radius": 0.1 * mm});
            skCircle(sketch, "E42.90.0", {"center": v(23.35, -9.75) * mm, "radius": 0.1 * mm});
            skCircle(sketch, "E42.91.0", {"center": v(23.79, -8.62) * mm, "radius": 0.1 * mm});
            skCircle(sketch, "E42.92.0", {"center": v(24.17, -7.47) * mm, "radius": 0.1 * mm});
            skCircle(sketch, "E42.93.0", {"center": v(24.5, -6.3) * mm, "radius": 0.1 * mm});
            skCircle(sketch, "E42.94.0", {"center": v(24.78, -5.12) * mm, "radius": 0.1 * mm});
            skCircle(sketch, "E42.95.0", {"center": v(25, -3.93) * mm, "radius": 0.1 * mm});
            skCircle(sketch, "E42.96.0", {"center": v(25.15, -2.73) * mm, "radius": 0.1 * mm});
            skCircle(sketch, "E42.97.0", {"center": v(25.25, -1.52) * mm, "radius": 0.1 * mm});
            skCircle(sketch, "E42.98.0", {"center": v(25.3, -0.3) * mm, "radius": 0.1 * mm});
            skCircle(sketch, "E42.99.0", {"center": v(25.28, 0.9) * mm, "radius": 0.1 * mm});
            skCircle(sketch, "E42.100.0", {"center": v(25.21, 2.12) * mm, "radius": 0.1 * mm});
            skCircle(sketch, "E42.101.0", {"center": v(25.08, 3.33) * mm, "radius": 0.1 * mm});
            skCircle(sketch, "E42.102.0", {"center": v(24.9, 4.53) * mm, "radius": 0.1 * mm});
            skCircle(sketch, "E42.103.0", {"center": v(24.65, 5.71) * mm, "radius": 0.1 * mm});
            skCircle(sketch, "E42.104.0", {"center": v(24.34, 6.89) * mm, "radius": 0.1 * mm});
            skCircle(sketch, "E42.105.0", {"center": v(23.99, 8.05) * mm, "radius": 0.1 * mm});
            skCircle(sketch, "E42.106.0", {"center": v(23.57, 9.19) * mm, "radius": 0.1 * mm});
            skCircle(sketch, "E42.107.0", {"center": v(23.1, 10.3) * mm, "radius": 0.1 * mm});
            skCircle(sketch, "E42.108.0", {"center": v(22.58, 11.4) * mm, "radius": 0.1 * mm});
            skCircle(sketch, "E42.109.0", {"center": v(22.01, 12.47) * mm, "radius": 0.1 * mm});
            skCircle(sketch, "E42.110.0", {"center": v(21.39, 13.52) * mm, "radius": 0.1 * mm});
            skCircle(sketch, "E42.111.0", {"center": v(20.71, 14.53) * mm, "radius": 0.1 * mm});
            skCircle(sketch, "E42.112.0", {"center": v(20, 15.5) * mm, "radius": 0.1 * mm});
            skCircle(sketch, "E42.113.0", {"center": v(19.23, 16.44) * mm, "radius": 0.1 * mm});
            skCircle(sketch, "E42.114.0", {"center": v(18.42, 17.35) * mm, "radius": 0.1 * mm});
            skCircle(sketch, "E42.115.0", {"center": v(17.57, 18.2) * mm, "radius": 0.1 * mm});
            skCircle(sketch, "E42.116.0", {"center": v(16.67, 19.03) * mm, "radius": 0.1 * mm});
            skCircle(sketch, "E42.117.0", {"center": v(15.74, 19.8) * mm, "radius": 0.1 * mm});
            skCircle(sketch, "E42.118.0", {"center": v(14.77, 20.54) * mm, "radius": 0.1 * mm});
            skCircle(sketch, "E42.119.0", {"center": v(13.77, 21.22) * mm, "radius": 0.1 * mm});
            skCircle(sketch, "E42.120.0", {"center": v(12.74, 21.86) * mm, "radius": 0.1 * mm});
            skCircle(sketch, "E42.121.0", {"center": v(11.67, 22.45) * mm, "radius": 0.1 * mm});
            skCircle(sketch, "E42.122.0", {"center": v(10.59, 22.98) * mm, "radius": 0.1 * mm});
            skCircle(sketch, "E42.123.0", {"center": v(9.47, 23.46) * mm, "radius": 0.1 * mm});
            skCircle(sketch, "E42.124.0", {"center": v(8.34, 23.89) * mm, "radius": 0.1 * mm});
            skCircle(sketch, "E42.125.0", {"center": v(7.18, 24.26) * mm, "radius": 0.1 * mm});
            skCircle(sketch, "E42.126.0", {"center": v(6, 24.58) * mm, "radius": 0.1 * mm});
            skCircle(sketch, "E42.127.0", {"center": v(4.82, 24.84) * mm, "radius": 0.1 * mm});
            skCircle(sketch, "E42.128.0", {"center": v(3.63, 25.04) * mm, "radius": 0.1 * mm});
            skCircle(sketch, "E42.129.0", {"center": v(2.42, 25.18) * mm, "radius": 0.1 * mm});
            skCircle(sketch, "E42.130.0", {"center": v(1.21, 25.27) * mm, "radius": 0.1 * mm});
            skCircle(sketch, "E43.1.0", {"center": v(-1.21, 26.57) * mm, "radius": 0.1 * mm});
            skCircle(sketch, "E43.2.0", {"center": v(-2.42, 26.49) * mm, "radius": 0.1 * mm});
            skCircle(sketch, "E43.3.0", {"center": v(-3.62, 26.35) * mm, "radius": 0.1 * mm});
            skCircle(sketch, "E43.4.0", {"center": v(-4.82, 26.16) * mm, "radius": 0.1 * mm});
            skCircle(sketch, "E43.5.0", {"center": v(-6, 25.91) * mm, "radius": 0.1 * mm});
            skCircle(sketch, "E43.6.0", {"center": v(-7.18, 25.61) * mm, "radius": 0.1 * mm});
            skCircle(sketch, "E43.7.0", {"center": v(-8.33, 25.26) * mm, "radius": 0.1 * mm});
            skCircle(sketch, "E43.8.0", {"center": v(-9.48, 24.85) * mm, "radius": 0.1 * mm});
            skCircle(sketch, "E43.9.0", {"center": v(-10.6, 24.4) * mm, "radius": 0.1 * mm});
            skCircle(sketch, "E43.10.0", {"center": v(-11.7, 23.9) * mm, "radius": 0.1 * mm});
            skCircle(sketch, "E43.11.0", {"center": v(-12.77, 23.33) * mm, "radius": 0.1 * mm});
            skCircle(sketch, "E43.12.0", {"center": v(-13.82, 22.73) * mm, "radius": 0.1 * mm});
            skCircle(sketch, "E43.13.0", {"center": v(-14.84, 22.07) * mm, "radius": 0.1 * mm});
            skCircle(sketch, "E43.14.0", {"center": v(-15.83, 21.38) * mm, "radius": 0.1 * mm});
            skCircle(sketch, "E43.15.0", {"center": v(-16.79, 20.63) * mm, "radius": 0.1 * mm});
            skCircle(sketch, "E43.16.0", {"center": v(-17.7, 19.85) * mm, "radius": 0.1 * mm});
            skCircle(sketch, "E43.17.0", {"center": v(-18.6, 19.02) * mm, "radius": 0.1 * mm});
            skCircle(sketch, "E43.18.0", {"center": v(-19.44, 18.16) * mm, "radius": 0.1 * mm});
            skCircle(sketch, "E43.19.0", {"center": v(-20.25, 17.25) * mm, "radius": 0.1 * mm});
            skCircle(sketch, "E43.20.0", {"center": v(-21.01, 16.31) * mm, "radius": 0.1 * mm});
            skCircle(sketch, "E43.21.0", {"center": v(-21.73, 15.34) * mm, "radius": 0.1 * mm});
            skCircle(sketch, "E43.22.0", {"center": v(-22.4, 14.33) * mm, "radius": 0.1 * mm});
            skCircle(sketch, "E43.23.0", {"center": v(-23.04, 13.3) * mm, "radius": 0.1 * mm});
            skCircle(sketch, "E43.24.0", {"center": v(-23.62, 12.24) * mm, "radius": 0.1 * mm});
            skCircle(sketch, "E43.25.0", {"center": v(-24.15, 11.15) * mm, "radius": 0.1 * mm});
            skCircle(sketch, "E43.26.0", {"center": v(-24.63, 10.04) * mm, "radius": 0.1 * mm});
            skCircle(sketch, "E43.27.0", {"center": v(-25.06, 8.9) * mm, "radius": 0.1 * mm});
            skCircle(sketch, "E43.28.0", {"center": v(-25.44, 7.76) * mm, "radius": 0.1 * mm});
            skCircle(sketch, "E43.29.0", {"center": v(-25.77, 6.6) * mm, "radius": 0.1 * mm});
            skCircle(sketch, "E43.30.0", {"center": v(-26.04, 5.41) * mm, "radius": 0.1 * mm});
            skCircle(sketch, "E43.31.0", {"center": v(-26.26, 4.22) * mm, "radius": 0.1 * mm});
            skCircle(sketch, "E43.32.0", {"center": v(-26.43, 3.02) * mm, "radius": 0.1 * mm});
            skCircle(sketch, "E43.33.0", {"center": v(-26.54, 1.82) * mm, "radius": 0.1 * mm});
            skCircle(sketch, "E43.34.0", {"center": v(-26.6, 0.6) * mm, "radius": 0.1 * mm});
            skCircle(sketch, "E43.35.0", {"center": v(-26.6, -0.6) * mm, "radius": 0.1 * mm});
            skCircle(sketch, "E43.36.0", {"center": v(-26.54, -1.82) * mm, "radius": 0.1 * mm});
            skCircle(sketch, "E43.37.0", {"center": v(-26.43, -3.02) * mm, "radius": 0.1 * mm});
            skCircle(sketch, "E43.38.0", {"center": v(-26.26, -4.22) * mm, "radius": 0.1 * mm});
            skCircle(sketch, "E43.39.0", {"center": v(-26.04, -5.41) * mm, "radius": 0.1 * mm});
            skCircle(sketch, "E43.40.0", {"center": v(-25.77, -6.6) * mm, "radius": 0.1 * mm});
            skCircle(sketch, "E43.41.0", {"center": v(-25.44, -7.76) * mm, "radius": 0.1 * mm});
            skCircle(sketch, "E43.42.0", {"center": v(-25.06, -8.9) * mm, "radius": 0.1 * mm});
            skCircle(sketch, "E43.43.0", {"center": v(-24.63, -10.04) * mm, "radius": 0.1 * mm});
            skCircle(sketch, "E43.44.0", {"center": v(-24.15, -11.15) * mm, "radius": 0.1 * mm});
            skCircle(sketch, "E43.45.0", {"center": v(-23.62, -12.24) * mm, "radius": 0.1 * mm});
            skCircle(sketch, "E43.46.0", {"center": v(-23.04, -13.3) * mm, "radius": 0.1 * mm});
            skCircle(sketch, "E43.47.0", {"center": v(-22.4, -14.33) * mm, "radius": 0.1 * mm});
            skCircle(sketch, "E43.48.0", {"center": v(-21.73, -15.34) * mm, "radius": 0.1 * mm});
            skCircle(sketch, "E43.49.0", {"center": v(-21.01, -16.31) * mm, "radius": 0.1 * mm});
            skCircle(sketch, "E43.50.0", {"center": v(-20.25, -17.25) * mm, "radius": 0.1 * mm});
            skCircle(sketch, "E43.51.0", {"center": v(-19.44, -18.16) * mm, "radius": 0.1 * mm});
            skCircle(sketch, "E43.52.0", {"center": v(-18.6, -19.02) * mm, "radius": 0.1 * mm});
            skCircle(sketch, "E43.53.0", {"center": v(-17.7, -19.85) * mm, "radius": 0.1 * mm});
            skCircle(sketch, "E43.54.0", {"center": v(-16.79, -20.63) * mm, "radius": 0.1 * mm});
            skCircle(sketch, "E43.55.0", {"center": v(-15.83, -21.38) * mm, "radius": 0.1 * mm});
            skCircle(sketch, "E43.56.0", {"center": v(-14.84, -22.07) * mm, "radius": 0.1 * mm});
            skCircle(sketch, "E43.57.0", {"center": v(-13.82, -22.73) * mm, "radius": 0.1 * mm});
            skCircle(sketch, "E43.58.0", {"center": v(-12.77, -23.33) * mm, "radius": 0.1 * mm});
            skCircle(sketch, "E43.59.0", {"center": v(-11.7, -23.9) * mm, "radius": 0.1 * mm});
            skCircle(sketch, "E43.60.0", {"center": v(-10.6, -24.4) * mm, "radius": 0.1 * mm});
            skCircle(sketch, "E43.61.0", {"center": v(-9.48, -24.85) * mm, "radius": 0.1 * mm});
            skCircle(sketch, "E43.62.0", {"center": v(-8.33, -25.26) * mm, "radius": 0.1 * mm});
            skCircle(sketch, "E43.63.0", {"center": v(-7.18, -25.61) * mm, "radius": 0.1 * mm});
            skCircle(sketch, "E43.64.0", {"center": v(-6, -25.91) * mm, "radius": 0.1 * mm});
            skCircle(sketch, "E43.65.0", {"center": v(-4.82, -26.16) * mm, "radius": 0.1 * mm});
            skCircle(sketch, "E43.66.0", {"center": v(-3.62, -26.35) * mm, "radius": 0.1 * mm});
            skCircle(sketch, "E43.67.0", {"center": v(-2.42, -26.49) * mm, "radius": 0.1 * mm});
            skCircle(sketch, "E43.68.0", {"center": v(-1.21, -26.57) * mm, "radius": 0.1 * mm});
            skCircle(sketch, "E43.69.0", {"center": v(0, -26.6) * mm, "radius": 0.1 * mm});
            skCircle(sketch, "E43.70.0", {"center": v(1.21, -26.57) * mm, "radius": 0.1 * mm});
            skCircle(sketch, "E43.71.0", {"center": v(2.42, -26.49) * mm, "radius": 0.1 * mm});
            skCircle(sketch, "E43.72.0", {"center": v(3.62, -26.35) * mm, "radius": 0.1 * mm});
            skCircle(sketch, "E43.73.0", {"center": v(4.82, -26.16) * mm, "radius": 0.1 * mm});
            skCircle(sketch, "E43.74.0", {"center": v(6, -25.91) * mm, "radius": 0.1 * mm});
            skCircle(sketch, "E43.75.0", {"center": v(7.18, -25.61) * mm, "radius": 0.1 * mm});
            skCircle(sketch, "E43.76.0", {"center": v(8.33, -25.26) * mm, "radius": 0.1 * mm});
            skCircle(sketch, "E43.77.0", {"center": v(9.48, -24.85) * mm, "radius": 0.1 * mm});
            skCircle(sketch, "E43.78.0", {"center": v(10.6, -24.4) * mm, "radius": 0.1 * mm});
            skCircle(sketch, "E43.79.0", {"center": v(11.7, -23.9) * mm, "radius": 0.1 * mm});
            skCircle(sketch, "E43.80.0", {"center": v(12.77, -23.33) * mm, "radius": 0.1 * mm});
            skCircle(sketch, "E43.81.0", {"center": v(13.82, -22.73) * mm, "radius": 0.1 * mm});
            skCircle(sketch, "E43.82.0", {"center": v(14.84, -22.07) * mm, "radius": 0.1 * mm});
            skCircle(sketch, "E43.83.0", {"center": v(15.83, -21.38) * mm, "radius": 0.1 * mm});
            skCircle(sketch, "E43.84.0", {"center": v(16.79, -20.63) * mm, "radius": 0.1 * mm});
            skCircle(sketch, "E43.85.0", {"center": v(17.7, -19.85) * mm, "radius": 0.1 * mm});
            skCircle(sketch, "E43.86.0", {"center": v(18.6, -19.02) * mm, "radius": 0.1 * mm});
            skCircle(sketch, "E43.87.0", {"center": v(19.44, -18.16) * mm, "radius": 0.1 * mm});
            skCircle(sketch, "E43.88.0", {"center": v(20.25, -17.25) * mm, "radius": 0.1 * mm});
            skCircle(sketch, "E43.89.0", {"center": v(21.01, -16.31) * mm, "radius": 0.1 * mm});
            skCircle(sketch, "E43.90.0", {"center": v(21.73, -15.34) * mm, "radius": 0.1 * mm});
            skCircle(sketch, "E43.91.0", {"center": v(22.4, -14.33) * mm, "radius": 0.1 * mm});
            skCircle(sketch, "E43.92.0", {"center": v(23.04, -13.3) * mm, "radius": 0.1 * mm});
            skCircle(sketch, "E43.93.0", {"center": v(23.62, -12.24) * mm, "radius": 0.1 * mm});
            skCircle(sketch, "E43.94.0", {"center": v(24.15, -11.15) * mm, "radius": 0.1 * mm});
            skCircle(sketch, "E43.95.0", {"center": v(24.63, -10.04) * mm, "radius": 0.1 * mm});
            skCircle(sketch, "E43.96.0", {"center": v(25.06, -8.9) * mm, "radius": 0.1 * mm});
            skCircle(sketch, "E43.97.0", {"center": v(25.44, -7.76) * mm, "radius": 0.1 * mm});
            skCircle(sketch, "E43.98.0", {"center": v(25.77, -6.6) * mm, "radius": 0.1 * mm});
            skCircle(sketch, "E43.99.0", {"center": v(26.04, -5.41) * mm, "radius": 0.1 * mm});
            skCircle(sketch, "E43.100.0", {"center": v(26.26, -4.22) * mm, "radius": 0.1 * mm});
            skCircle(sketch, "E43.101.0", {"center": v(26.43, -3.02) * mm, "radius": 0.1 * mm});
            skCircle(sketch, "E43.102.0", {"center": v(26.54, -1.82) * mm, "radius": 0.1 * mm});
            skCircle(sketch, "E43.103.0", {"center": v(26.6, -0.6) * mm, "radius": 0.1 * mm});
            skCircle(sketch, "E43.104.0", {"center": v(26.6, 0.6) * mm, "radius": 0.1 * mm});
            skCircle(sketch, "E43.105.0", {"center": v(26.54, 1.82) * mm, "radius": 0.1 * mm});
            skCircle(sketch, "E43.106.0", {"center": v(26.43, 3.02) * mm, "radius": 0.1 * mm});
            skCircle(sketch, "E43.107.0", {"center": v(26.26, 4.22) * mm, "radius": 0.1 * mm});
            skCircle(sketch, "E43.108.0", {"center": v(26.04, 5.41) * mm, "radius": 0.1 * mm});
            skCircle(sketch, "E43.109.0", {"center": v(25.77, 6.6) * mm, "radius": 0.1 * mm});
            skCircle(sketch, "E43.110.0", {"center": v(25.44, 7.76) * mm, "radius": 0.1 * mm});
            skCircle(sketch, "E43.111.0", {"center": v(25.06, 8.9) * mm, "radius": 0.1 * mm});
            skCircle(sketch, "E43.112.0", {"center": v(24.63, 10.04) * mm, "radius": 0.1 * mm});
            skCircle(sketch, "E43.113.0", {"center": v(24.15, 11.15) * mm, "radius": 0.1 * mm});
            skCircle(sketch, "E43.114.0", {"center": v(23.62, 12.24) * mm, "radius": 0.1 * mm});
            skCircle(sketch, "E43.115.0", {"center": v(23.04, 13.3) * mm, "radius": 0.1 * mm});
            skCircle(sketch, "E43.116.0", {"center": v(22.4, 14.33) * mm, "radius": 0.1 * mm});
            skCircle(sketch, "E43.117.0", {"center": v(21.73, 15.34) * mm, "radius": 0.1 * mm});
            skCircle(sketch, "E43.118.0", {"center": v(21.01, 16.31) * mm, "radius": 0.1 * mm});
            skCircle(sketch, "E43.119.0", {"center": v(20.25, 17.25) * mm, "radius": 0.1 * mm});
            skCircle(sketch, "E43.120.0", {"center": v(19.44, 18.16) * mm, "radius": 0.1 * mm});
            skCircle(sketch, "E43.121.0", {"center": v(18.6, 19.02) * mm, "radius": 0.1 * mm});
            skCircle(sketch, "E43.122.0", {"center": v(17.7, 19.85) * mm, "radius": 0.1 * mm});
            skCircle(sketch, "E43.123.0", {"center": v(16.79, 20.63) * mm, "radius": 0.1 * mm});
            skCircle(sketch, "E43.124.0", {"center": v(15.83, 21.38) * mm, "radius": 0.1 * mm});
            skCircle(sketch, "E43.125.0", {"center": v(14.84, 22.07) * mm, "radius": 0.1 * mm});
            skCircle(sketch, "E43.126.0", {"center": v(13.82, 22.73) * mm, "radius": 0.1 * mm});
            skCircle(sketch, "E43.127.0", {"center": v(12.77, 23.33) * mm, "radius": 0.1 * mm});
            skCircle(sketch, "E43.128.0", {"center": v(11.7, 23.9) * mm, "radius": 0.1 * mm});
            skCircle(sketch, "E43.129.0", {"center": v(10.6, 24.4) * mm, "radius": 0.1 * mm});
            skCircle(sketch, "E43.130.0", {"center": v(9.48, 24.85) * mm, "radius": 0.1 * mm});
            skCircle(sketch, "E43.131.0", {"center": v(8.33, 25.26) * mm, "radius": 0.1 * mm});
            skCircle(sketch, "E43.132.0", {"center": v(7.18, 25.61) * mm, "radius": 0.1 * mm});
            skCircle(sketch, "E43.133.0", {"center": v(6, 25.91) * mm, "radius": 0.1 * mm});
            skCircle(sketch, "E43.134.0", {"center": v(4.82, 26.16) * mm, "radius": 0.1 * mm});
            skCircle(sketch, "E43.135.0", {"center": v(3.62, 26.35) * mm, "radius": 0.1 * mm});
            skCircle(sketch, "E43.136.0", {"center": v(2.42, 26.49) * mm, "radius": 0.1 * mm});
            skCircle(sketch, "E43.137.0", {"center": v(1.21, 26.57) * mm, "radius": 0.1 * mm});
            skCircle(sketch, "E44.1.0", {"center": v(-1.2, 27.87) * mm, "radius": 0.1 * mm});
            skCircle(sketch, "E44.2.0", {"center": v(-2.41, 27.8) * mm, "radius": 0.1 * mm});
            skCircle(sketch, "E44.3.0", {"center": v(-3.62, 27.66) * mm, "radius": 0.1 * mm});
            skCircle(sketch, "E44.4.0", {"center": v(-4.81, 27.48) * mm, "radius": 0.1 * mm});
            skCircle(sketch, "E44.5.0", {"center": v(-6, 27.25) * mm, "radius": 0.1 * mm});
            skCircle(sketch, "E44.6.0", {"center": v(-7.17, 26.96) * mm, "radius": 0.1 * mm});
            skCircle(sketch, "E44.7.0", {"center": v(-8.33, 26.63) * mm, "radius": 0.1 * mm});
            skCircle(sketch, "E44.8.0", {"center": v(-9.48, 26.24) * mm, "radius": 0.1 * mm});
            skCircle(sketch, "E44.9.0", {"center": v(-10.6, 25.8) * mm, "radius": 0.1 * mm});
            skCircle(sketch, "E44.10.0", {"center": v(-11.71, 25.32) * mm, "radius": 0.1 * mm});
            skCircle(sketch, "E44.11.0", {"center": v(-12.8, 24.8) * mm, "radius": 0.1 * mm});
            skCircle(sketch, "E44.12.0", {"center": v(-13.86, 24.21) * mm, "radius": 0.1 * mm});
            skCircle(sketch, "E44.13.0", {"center": v(-14.9, 23.59) * mm, "radius": 0.1 * mm});
            skCircle(sketch, "E44.14.0", {"center": v(-15.9, 22.92) * mm, "radius": 0.1 * mm});
            skCircle(sketch, "E44.15.0", {"center": v(-16.88, 22.21) * mm, "radius": 0.1 * mm});
            skCircle(sketch, "E44.16.0", {"center": v(-17.83, 21.46) * mm, "radius": 0.1 * mm});
            skCircle(sketch, "E44.17.0", {"center": v(-18.74, 20.67) * mm, "radius": 0.1 * mm});
            skCircle(sketch, "E44.18.0", {"center": v(-19.62, 19.83) * mm, "radius": 0.1 * mm});
            skCircle(sketch, "E44.19.0", {"center": v(-20.46, 18.97) * mm, "radius": 0.1 * mm});
            skCircle(sketch, "E44.20.0", {"center": v(-21.26, 18.06) * mm, "radius": 0.1 * mm});
            skCircle(sketch, "E44.21.0", {"center": v(-22.03, 17.12) * mm, "radius": 0.1 * mm});
            skCircle(sketch, "E44.22.0", {"center": v(-22.75, 16.15) * mm, "radius": 0.1 * mm});
            skCircle(sketch, "E44.23.0", {"center": v(-23.43, 15.15) * mm, "radius": 0.1 * mm});
            skCircle(sketch, "E44.24.0", {"center": v(-24.06, 14.12) * mm, "radius": 0.1 * mm});
            skCircle(sketch, "E44.25.0", {"center": v(-24.65, 13.07) * mm, "radius": 0.1 * mm});
            skCircle(sketch, "E44.26.0", {"center": v(-25.2, 11.99) * mm, "radius": 0.1 * mm});
            skCircle(sketch, "E44.27.0", {"center": v(-25.69, 10.89) * mm, "radius": 0.1 * mm});
            skCircle(sketch, "E44.28.0", {"center": v(-26.14, 9.76) * mm, "radius": 0.1 * mm});
            skCircle(sketch, "E44.29.0", {"center": v(-26.53, 8.62) * mm, "radius": 0.1 * mm});
            skCircle(sketch, "E44.30.0", {"center": v(-26.88, 7.46) * mm, "radius": 0.1 * mm});
            skCircle(sketch, "E44.31.0", {"center": v(-27.18, 6.3) * mm, "radius": 0.1 * mm});
            skCircle(sketch, "E44.32.0", {"center": v(-27.43, 5.1) * mm, "radius": 0.1 * mm});
            skCircle(sketch, "E44.33.0", {"center": v(-27.62, 3.92) * mm, "radius": 0.1 * mm});
            skCircle(sketch, "E44.34.0", {"center": v(-27.77, 2.72) * mm, "radius": 0.1 * mm});
            skCircle(sketch, "E44.35.0", {"center": v(-27.86, 1.51) * mm, "radius": 0.1 * mm});
            skCircle(sketch, "E44.36.0", {"center": v(-27.9, 0.3) * mm, "radius": 0.1 * mm});
            skCircle(sketch, "E44.37.0", {"center": v(-27.89, -0.9) * mm, "radius": 0.1 * mm});
            skCircle(sketch, "E44.38.0", {"center": v(-27.82, -2.11) * mm, "radius": 0.1 * mm});
            skCircle(sketch, "E44.39.0", {"center": v(-27.7, -3.32) * mm, "radius": 0.1 * mm});
            skCircle(sketch, "E44.40.0", {"center": v(-27.53, -4.51) * mm, "radius": 0.1 * mm});
            skCircle(sketch, "E44.41.0", {"center": v(-27.31, -5.7) * mm, "radius": 0.1 * mm});
            skCircle(sketch, "E44.42.0", {"center": v(-27.04, -6.88) * mm, "radius": 0.1 * mm});
            skCircle(sketch, "E44.43.0", {"center": v(-26.72, -8.04) * mm, "radius": 0.1 * mm});
            skCircle(sketch, "E44.44.0", {"center": v(-26.34, -9.2) * mm, "radius": 0.1 * mm});
            skCircle(sketch, "E44.45.0", {"center": v(-25.92, -10.33) * mm, "radius": 0.1 * mm});
            skCircle(sketch, "E44.46.0", {"center": v(-25.45, -11.44) * mm, "radius": 0.1 * mm});
            skCircle(sketch, "E44.47.0", {"center": v(-24.93, -12.53) * mm, "radius": 0.1 * mm});
            skCircle(sketch, "E44.48.0", {"center": v(-24.36, -13.6) * mm, "radius": 0.1 * mm});
            skCircle(sketch, "E44.49.0", {"center": v(-23.75, -14.64) * mm, "radius": 0.1 * mm});
            skCircle(sketch, "E44.50.0", {"center": v(-23.1, -15.66) * mm, "radius": 0.1 * mm});
            skCircle(sketch, "E44.51.0", {"center": v(-22.4, -16.64) * mm, "radius": 0.1 * mm});
            skCircle(sketch, "E44.52.0", {"center": v(-21.65, -17.6) * mm, "radius": 0.1 * mm});
            skCircle(sketch, "E44.53.0", {"center": v(-20.87, -18.52) * mm, "radius": 0.1 * mm});
            skCircle(sketch, "E44.54.0", {"center": v(-20.05, -19.4) * mm, "radius": 0.1 * mm});
            skCircle(sketch, "E44.55.0", {"center": v(-19.19, -20.26) * mm, "radius": 0.1 * mm});
            skCircle(sketch, "E44.56.0", {"center": v(-18.3, -21.07) * mm, "radius": 0.1 * mm});
            skCircle(sketch, "E44.57.0", {"center": v(-17.36, -21.84) * mm, "radius": 0.1 * mm});
            skCircle(sketch, "E44.58.0", {"center": v(-16.4, -22.57) * mm, "radius": 0.1 * mm});
            skCircle(sketch, "E44.59.0", {"center": v(-15.4, -23.26) * mm, "radius": 0.1 * mm});
            skCircle(sketch, "E44.60.0", {"center": v(-14.38, -23.9) * mm, "radius": 0.1 * mm});
            skCircle(sketch, "E44.61.0", {"center": v(-13.33, -24.5) * mm, "radius": 0.1 * mm});
            skCircle(sketch, "E44.62.0", {"center": v(-12.26, -25.06) * mm, "radius": 0.1 * mm});
            skCircle(sketch, "E44.63.0", {"center": v(-11.16, -25.57) * mm, "radius": 0.1 * mm});
            skCircle(sketch, "E44.64.0", {"center": v(-10.05, -26.03) * mm, "radius": 0.1 * mm});
            skCircle(sketch, "E44.65.0", {"center": v(-8.9, -26.44) * mm, "radius": 0.1 * mm});
            skCircle(sketch, "E44.66.0", {"center": v(-7.75, -26.8) * mm, "radius": 0.1 * mm});
            skCircle(sketch, "E44.67.0", {"center": v(-6.59, -27.11) * mm, "radius": 0.1 * mm});
            skCircle(sketch, "E44.68.0", {"center": v(-5.4, -27.37) * mm, "radius": 0.1 * mm});
            skCircle(sketch, "E44.69.0", {"center": v(-4.22, -27.58) * mm, "radius": 0.1 * mm});
            skCircle(sketch, "E44.70.0", {"center": v(-3.02, -27.74) * mm, "radius": 0.1 * mm});
            skCircle(sketch, "E44.71.0", {"center": v(-1.81, -27.84) * mm, "radius": 0.1 * mm});
            skCircle(sketch, "E44.72.0", {"center": v(-0.6, -27.9) * mm, "radius": 0.1 * mm});
            skCircle(sketch, "E44.73.0", {"center": v(0.6, -27.9) * mm, "radius": 0.1 * mm});
            skCircle(sketch, "E44.74.0", {"center": v(1.81, -27.84) * mm, "radius": 0.1 * mm});
            skCircle(sketch, "E44.75.0", {"center": v(3.02, -27.74) * mm, "radius": 0.1 * mm});
            skCircle(sketch, "E44.76.0", {"center": v(4.22, -27.58) * mm, "radius": 0.1 * mm});
            skCircle(sketch, "E44.77.0", {"center": v(5.4, -27.37) * mm, "radius": 0.1 * mm});
            skCircle(sketch, "E44.78.0", {"center": v(6.59, -27.11) * mm, "radius": 0.1 * mm});
            skCircle(sketch, "E44.79.0", {"center": v(7.75, -26.8) * mm, "radius": 0.1 * mm});
            skCircle(sketch, "E44.80.0", {"center": v(8.9, -26.44) * mm, "radius": 0.1 * mm});
            skCircle(sketch, "E44.81.0", {"center": v(10.05, -26.03) * mm, "radius": 0.1 * mm});
            skCircle(sketch, "E44.82.0", {"center": v(11.16, -25.57) * mm, "radius": 0.1 * mm});
            skCircle(sketch, "E44.83.0", {"center": v(12.26, -25.06) * mm, "radius": 0.1 * mm});
            skCircle(sketch, "E44.84.0", {"center": v(13.33, -24.5) * mm, "radius": 0.1 * mm});
            skCircle(sketch, "E44.85.0", {"center": v(14.38, -23.9) * mm, "radius": 0.1 * mm});
            skCircle(sketch, "E44.86.0", {"center": v(15.4, -23.26) * mm, "radius": 0.1 * mm});
            skCircle(sketch, "E44.87.0", {"center": v(16.4, -22.57) * mm, "radius": 0.1 * mm});
            skCircle(sketch, "E44.88.0", {"center": v(17.36, -21.84) * mm, "radius": 0.1 * mm});
            skCircle(sketch, "E44.89.0", {"center": v(18.3, -21.07) * mm, "radius": 0.1 * mm});
            skCircle(sketch, "E44.90.0", {"center": v(19.19, -20.26) * mm, "radius": 0.1 * mm});
            skCircle(sketch, "E44.91.0", {"center": v(20.05, -19.4) * mm, "radius": 0.1 * mm});
            skCircle(sketch, "E44.92.0", {"center": v(20.87, -18.52) * mm, "radius": 0.1 * mm});
            skCircle(sketch, "E44.93.0", {"center": v(21.65, -17.6) * mm, "radius": 0.1 * mm});
            skCircle(sketch, "E44.94.0", {"center": v(22.4, -16.64) * mm, "radius": 0.1 * mm});
            skCircle(sketch, "E44.95.0", {"center": v(23.1, -15.66) * mm, "radius": 0.1 * mm});
            skCircle(sketch, "E44.96.0", {"center": v(23.75, -14.64) * mm, "radius": 0.1 * mm});
            skCircle(sketch, "E44.97.0", {"center": v(24.36, -13.6) * mm, "radius": 0.1 * mm});
            skCircle(sketch, "E44.98.0", {"center": v(24.93, -12.53) * mm, "radius": 0.1 * mm});
            skCircle(sketch, "E44.99.0", {"center": v(25.45, -11.44) * mm, "radius": 0.1 * mm});
            skCircle(sketch, "E44.100.0", {"center": v(25.92, -10.33) * mm, "radius": 0.1 * mm});
            skCircle(sketch, "E44.101.0", {"center": v(26.34, -9.2) * mm, "radius": 0.1 * mm});
            skCircle(sketch, "E44.102.0", {"center": v(26.72, -8.04) * mm, "radius": 0.1 * mm});
            skCircle(sketch, "E44.103.0", {"center": v(27.04, -6.88) * mm, "radius": 0.1 * mm});
            skCircle(sketch, "E44.104.0", {"center": v(27.31, -5.7) * mm, "radius": 0.1 * mm});
            skCircle(sketch, "E44.105.0", {"center": v(27.53, -4.51) * mm, "radius": 0.1 * mm});
            skCircle(sketch, "E44.106.0", {"center": v(27.7, -3.32) * mm, "radius": 0.1 * mm});
            skCircle(sketch, "E44.107.0", {"center": v(27.82, -2.11) * mm, "radius": 0.1 * mm});
            skCircle(sketch, "E44.108.0", {"center": v(27.89, -0.9) * mm, "radius": 0.1 * mm});
            skCircle(sketch, "E44.109.0", {"center": v(27.9, 0.3) * mm, "radius": 0.1 * mm});
            skCircle(sketch, "E44.110.0", {"center": v(27.86, 1.51) * mm, "radius": 0.1 * mm});
            skCircle(sketch, "E44.111.0", {"center": v(27.77, 2.72) * mm, "radius": 0.1 * mm});
            skCircle(sketch, "E44.112.0", {"center": v(27.62, 3.92) * mm, "radius": 0.1 * mm});
            skCircle(sketch, "E44.113.0", {"center": v(27.43, 5.1) * mm, "radius": 0.1 * mm});
            skCircle(sketch, "E44.114.0", {"center": v(27.18, 6.3) * mm, "radius": 0.1 * mm});
            skCircle(sketch, "E44.115.0", {"center": v(26.88, 7.46) * mm, "radius": 0.1 * mm});
            skCircle(sketch, "E44.116.0", {"center": v(26.53, 8.62) * mm, "radius": 0.1 * mm});
            skCircle(sketch, "E44.117.0", {"center": v(26.14, 9.76) * mm, "radius": 0.1 * mm});
            skCircle(sketch, "E44.118.0", {"center": v(25.69, 10.89) * mm, "radius": 0.1 * mm});
            skCircle(sketch, "E44.119.0", {"center": v(25.2, 11.99) * mm, "radius": 0.1 * mm});
            skCircle(sketch, "E44.120.0", {"center": v(24.65, 13.07) * mm, "radius": 0.1 * mm});
            skCircle(sketch, "E44.121.0", {"center": v(24.06, 14.12) * mm, "radius": 0.1 * mm});
            skCircle(sketch, "E44.122.0", {"center": v(23.43, 15.15) * mm, "radius": 0.1 * mm});
            skCircle(sketch, "E44.123.0", {"center": v(22.75, 16.15) * mm, "radius": 0.1 * mm});
            skCircle(sketch, "E44.124.0", {"center": v(22.03, 17.12) * mm, "radius": 0.1 * mm});
            skCircle(sketch, "E44.125.0", {"center": v(21.26, 18.06) * mm, "radius": 0.1 * mm});
            skCircle(sketch, "E44.126.0", {"center": v(20.46, 18.97) * mm, "radius": 0.1 * mm});
            skCircle(sketch, "E44.127.0", {"center": v(19.62, 19.83) * mm, "radius": 0.1 * mm});
            skCircle(sketch, "E44.128.0", {"center": v(18.74, 20.67) * mm, "radius": 0.1 * mm});
            skCircle(sketch, "E44.129.0", {"center": v(17.83, 21.46) * mm, "radius": 0.1 * mm});
            skCircle(sketch, "E44.130.0", {"center": v(16.88, 22.21) * mm, "radius": 0.1 * mm});
            skCircle(sketch, "E44.131.0", {"center": v(15.9, 22.92) * mm, "radius": 0.1 * mm});
            skCircle(sketch, "E44.132.0", {"center": v(14.9, 23.59) * mm, "radius": 0.1 * mm});
            skCircle(sketch, "E44.133.0", {"center": v(13.86, 24.21) * mm, "radius": 0.1 * mm});
            skCircle(sketch, "E44.134.0", {"center": v(12.8, 24.8) * mm, "radius": 0.1 * mm});
            skCircle(sketch, "E44.135.0", {"center": v(11.71, 25.32) * mm, "radius": 0.1 * mm});
            skCircle(sketch, "E44.136.0", {"center": v(10.6, 25.8) * mm, "radius": 0.1 * mm});
            skCircle(sketch, "E44.137.0", {"center": v(9.48, 26.24) * mm, "radius": 0.1 * mm});
            skCircle(sketch, "E44.138.0", {"center": v(8.33, 26.63) * mm, "radius": 0.1 * mm});
            skCircle(sketch, "E44.139.0", {"center": v(7.17, 26.96) * mm, "radius": 0.1 * mm});
            skCircle(sketch, "E44.140.0", {"center": v(6, 27.25) * mm, "radius": 0.1 * mm});
            skCircle(sketch, "E44.141.0", {"center": v(4.81, 27.48) * mm, "radius": 0.1 * mm});
            skCircle(sketch, "E44.142.0", {"center": v(3.62, 27.66) * mm, "radius": 0.1 * mm});
            skCircle(sketch, "E44.143.0", {"center": v(2.41, 27.8) * mm, "radius": 0.1 * mm});
            skCircle(sketch, "E44.144.0", {"center": v(1.2, 27.87) * mm, "radius": 0.1 * mm});
            skCircle(sketch, "E45.1.0", {"center": v(-1.2, 29.18) * mm, "radius": 0.1 * mm});
            skCircle(sketch, "E45.2.0", {"center": v(-2.41, 29.1) * mm, "radius": 0.1 * mm});
            skCircle(sketch, "E45.3.0", {"center": v(-3.61, 28.98) * mm, "radius": 0.1 * mm});
            skCircle(sketch, "E45.4.0", {"center": v(-4.8, 28.8) * mm, "radius": 0.1 * mm});
            skCircle(sketch, "E45.5.0", {"center": v(-6, 28.58) * mm, "radius": 0.1 * mm});
            skCircle(sketch, "E45.6.0", {"center": v(-7.17, 28.3) * mm, "radius": 0.1 * mm});
            skCircle(sketch, "E45.7.0", {"center": v(-8.33, 27.99) * mm, "radius": 0.1 * mm});
            skCircle(sketch, "E45.8.0", {"center": v(-9.48, 27.62) * mm, "radius": 0.1 * mm});
            skCircle(sketch, "E45.9.0", {"center": v(-10.61, 27.2) * mm, "radius": 0.1 * mm});
            skCircle(sketch, "E45.10.0", {"center": v(-11.73, 26.74) * mm, "radius": 0.1 * mm});
            skCircle(sketch, "E45.11.0", {"center": v(-12.82, 26.23) * mm, "radius": 0.1 * mm});
            skCircle(sketch, "E45.12.0", {"center": v(-13.9, 25.68) * mm, "radius": 0.1 * mm});
            skCircle(sketch, "E45.13.0", {"center": v(-14.95, 25.08) * mm, "radius": 0.1 * mm});
            skCircle(sketch, "E45.14.0", {"center": v(-15.97, 24.45) * mm, "radius": 0.1 * mm});
            skCircle(sketch, "E45.15.0", {"center": v(-16.97, 23.76) * mm, "radius": 0.1 * mm});
            skCircle(sketch, "E45.16.0", {"center": v(-17.94, 23.04) * mm, "radius": 0.1 * mm});
            skCircle(sketch, "E45.17.0", {"center": v(-18.87, 22.28) * mm, "radius": 0.1 * mm});
            skCircle(sketch, "E45.18.0", {"center": v(-19.78, 21.48) * mm, "radius": 0.1 * mm});
            skCircle(sketch, "E45.19.0", {"center": v(-20.65, 20.65) * mm, "radius": 0.1 * mm});
            skCircle(sketch, "E45.20.0", {"center": v(-21.48, 19.78) * mm, "radius": 0.1 * mm});
            skCircle(sketch, "E45.21.0", {"center": v(-22.28, 18.87) * mm, "radius": 0.1 * mm});
            skCircle(sketch, "E45.22.0", {"center": v(-23.04, 17.94) * mm, "radius": 0.1 * mm});
            skCircle(sketch, "E45.23.0", {"center": v(-23.76, 16.97) * mm, "radius": 0.1 * mm});
            skCircle(sketch, "E45.24.0", {"center": v(-24.45, 15.97) * mm, "radius": 0.1 * mm});
            skCircle(sketch, "E45.25.0", {"center": v(-25.08, 14.95) * mm, "radius": 0.1 * mm});
            skCircle(sketch, "E45.26.0", {"center": v(-25.68, 13.9) * mm, "radius": 0.1 * mm});
            skCircle(sketch, "E45.27.0", {"center": v(-26.23, 12.82) * mm, "radius": 0.1 * mm});
            skCircle(sketch, "E45.28.0", {"center": v(-26.74, 11.73) * mm, "radius": 0.1 * mm});
            skCircle(sketch, "E45.29.0", {"center": v(-27.2, 10.61) * mm, "radius": 0.1 * mm});
            skCircle(sketch, "E45.30.0", {"center": v(-27.62, 9.48) * mm, "radius": 0.1 * mm});
            skCircle(sketch, "E45.31.0", {"center": v(-27.99, 8.33) * mm, "radius": 0.1 * mm});
            skCircle(sketch, "E45.32.0", {"center": v(-28.3, 7.17) * mm, "radius": 0.1 * mm});
            skCircle(sketch, "E45.33.0", {"center": v(-28.58, 6) * mm, "radius": 0.1 * mm});
            skCircle(sketch, "E45.34.0", {"center": v(-28.8, 4.8) * mm, "radius": 0.1 * mm});
            skCircle(sketch, "E45.35.0", {"center": v(-28.98, 3.61) * mm, "radius": 0.1 * mm});
            skCircle(sketch, "E45.36.0", {"center": v(-29.1, 2.41) * mm, "radius": 0.1 * mm});
            skCircle(sketch, "E45.37.0", {"center": v(-29.18, 1.2) * mm, "radius": 0.1 * mm});
            skCircle(sketch, "E45.38.0", {"center": v(-29.2, 0) * mm, "radius": 0.1 * mm});
            skCircle(sketch, "E45.39.0", {"center": v(-29.18, -1.2) * mm, "radius": 0.1 * mm});
            skCircle(sketch, "E45.40.0", {"center": v(-29.1, -2.41) * mm, "radius": 0.1 * mm});
            skCircle(sketch, "E45.41.0", {"center": v(-28.98, -3.61) * mm, "radius": 0.1 * mm});
            skCircle(sketch, "E45.42.0", {"center": v(-28.8, -4.8) * mm, "radius": 0.1 * mm});
            skCircle(sketch, "E45.43.0", {"center": v(-28.58, -6) * mm, "radius": 0.1 * mm});
            skCircle(sketch, "E45.44.0", {"center": v(-28.3, -7.17) * mm, "radius": 0.1 * mm});
            skCircle(sketch, "E45.45.0", {"center": v(-27.99, -8.33) * mm, "radius": 0.1 * mm});
            skCircle(sketch, "E45.46.0", {"center": v(-27.62, -9.48) * mm, "radius": 0.1 * mm});
            skCircle(sketch, "E45.47.0", {"center": v(-27.2, -10.61) * mm, "radius": 0.1 * mm});
            skCircle(sketch, "E45.48.0", {"center": v(-26.74, -11.73) * mm, "radius": 0.1 * mm});
            skCircle(sketch, "E45.49.0", {"center": v(-26.23, -12.82) * mm, "radius": 0.1 * mm});
            skCircle(sketch, "E45.50.0", {"center": v(-25.68, -13.9) * mm, "radius": 0.1 * mm});
            skCircle(sketch, "E45.51.0", {"center": v(-25.08, -14.95) * mm, "radius": 0.1 * mm});
            skCircle(sketch, "E45.52.0", {"center": v(-24.45, -15.97) * mm, "radius": 0.1 * mm});
            skCircle(sketch, "E45.53.0", {"center": v(-23.76, -16.97) * mm, "radius": 0.1 * mm});
            skCircle(sketch, "E45.54.0", {"center": v(-23.04, -17.94) * mm, "radius": 0.1 * mm});
            skCircle(sketch, "E45.55.0", {"center": v(-22.28, -18.87) * mm, "radius": 0.1 * mm});
            skCircle(sketch, "E45.56.0", {"center": v(-21.48, -19.78) * mm, "radius": 0.1 * mm});
            skCircle(sketch, "E45.57.0", {"center": v(-20.65, -20.65) * mm, "radius": 0.1 * mm});
            skCircle(sketch, "E45.58.0", {"center": v(-19.78, -21.48) * mm, "radius": 0.1 * mm});
            skCircle(sketch, "E45.59.0", {"center": v(-18.87, -22.28) * mm, "radius": 0.1 * mm});
            skCircle(sketch, "E45.60.0", {"center": v(-17.94, -23.04) * mm, "radius": 0.1 * mm});
            skCircle(sketch, "E45.61.0", {"center": v(-16.97, -23.76) * mm, "radius": 0.1 * mm});
            skCircle(sketch, "E45.62.0", {"center": v(-15.97, -24.45) * mm, "radius": 0.1 * mm});
            skCircle(sketch, "E45.63.0", {"center": v(-14.95, -25.08) * mm, "radius": 0.1 * mm});
            skCircle(sketch, "E45.64.0", {"center": v(-13.9, -25.68) * mm, "radius": 0.1 * mm});
            skCircle(sketch, "E45.65.0", {"center": v(-12.82, -26.23) * mm, "radius": 0.1 * mm});
            skCircle(sketch, "E45.66.0", {"center": v(-11.73, -26.74) * mm, "radius": 0.1 * mm});
            skCircle(sketch, "E45.67.0", {"center": v(-10.61, -27.2) * mm, "radius": 0.1 * mm});
            skCircle(sketch, "E45.68.0", {"center": v(-9.48, -27.62) * mm, "radius": 0.1 * mm});
            skCircle(sketch, "E45.69.0", {"center": v(-8.33, -27.99) * mm, "radius": 0.1 * mm});
            skCircle(sketch, "E45.70.0", {"center": v(-7.17, -28.3) * mm, "radius": 0.1 * mm});
            skCircle(sketch, "E45.71.0", {"center": v(-6, -28.58) * mm, "radius": 0.1 * mm});
            skCircle(sketch, "E45.72.0", {"center": v(-4.8, -28.8) * mm, "radius": 0.1 * mm});
            skCircle(sketch, "E45.73.0", {"center": v(-3.61, -28.98) * mm, "radius": 0.1 * mm});
            skCircle(sketch, "E45.74.0", {"center": v(-2.41, -29.1) * mm, "radius": 0.1 * mm});
            skCircle(sketch, "E45.75.0", {"center": v(-1.2, -29.18) * mm, "radius": 0.1 * mm});
            skCircle(sketch, "E45.76.0", {"center": v(0, -29.2) * mm, "radius": 0.1 * mm});
            skCircle(sketch, "E45.77.0", {"center": v(1.2, -29.18) * mm, "radius": 0.1 * mm});
            skCircle(sketch, "E45.78.0", {"center": v(2.41, -29.1) * mm, "radius": 0.1 * mm});
            skCircle(sketch, "E45.79.0", {"center": v(3.61, -28.98) * mm, "radius": 0.1 * mm});
            skCircle(sketch, "E45.80.0", {"center": v(4.8, -28.8) * mm, "radius": 0.1 * mm});
            skCircle(sketch, "E45.81.0", {"center": v(6, -28.58) * mm, "radius": 0.1 * mm});
            skCircle(sketch, "E45.82.0", {"center": v(7.17, -28.3) * mm, "radius": 0.1 * mm});
            skCircle(sketch, "E45.83.0", {"center": v(8.33, -27.99) * mm, "radius": 0.1 * mm});
            skCircle(sketch, "E45.84.0", {"center": v(9.48, -27.62) * mm, "radius": 0.1 * mm});
            skCircle(sketch, "E45.85.0", {"center": v(10.61, -27.2) * mm, "radius": 0.1 * mm});
            skCircle(sketch, "E45.86.0", {"center": v(11.73, -26.74) * mm, "radius": 0.1 * mm});
            skCircle(sketch, "E45.87.0", {"center": v(12.82, -26.23) * mm, "radius": 0.1 * mm});
            skCircle(sketch, "E45.88.0", {"center": v(13.9, -25.68) * mm, "radius": 0.1 * mm});
            skCircle(sketch, "E45.89.0", {"center": v(14.95, -25.08) * mm, "radius": 0.1 * mm});
            skCircle(sketch, "E45.90.0", {"center": v(15.97, -24.45) * mm, "radius": 0.1 * mm});
            skCircle(sketch, "E45.91.0", {"center": v(16.97, -23.76) * mm, "radius": 0.1 * mm});
            skCircle(sketch, "E45.92.0", {"center": v(17.94, -23.04) * mm, "radius": 0.1 * mm});
            skCircle(sketch, "E45.93.0", {"center": v(18.87, -22.28) * mm, "radius": 0.1 * mm});
            skCircle(sketch, "E45.94.0", {"center": v(19.78, -21.48) * mm, "radius": 0.1 * mm});
            skCircle(sketch, "E45.95.0", {"center": v(20.65, -20.65) * mm, "radius": 0.1 * mm});
            skCircle(sketch, "E45.96.0", {"center": v(21.48, -19.78) * mm, "radius": 0.1 * mm});
            skCircle(sketch, "E45.97.0", {"center": v(22.28, -18.87) * mm, "radius": 0.1 * mm});
            skCircle(sketch, "E45.98.0", {"center": v(23.04, -17.94) * mm, "radius": 0.1 * mm});
            skCircle(sketch, "E45.99.0", {"center": v(23.76, -16.97) * mm, "radius": 0.1 * mm});
            skCircle(sketch, "E45.100.0", {"center": v(24.45, -15.97) * mm, "radius": 0.1 * mm});
            skCircle(sketch, "E45.101.0", {"center": v(25.08, -14.95) * mm, "radius": 0.1 * mm});
            skCircle(sketch, "E45.102.0", {"center": v(25.68, -13.9) * mm, "radius": 0.1 * mm});
            skCircle(sketch, "E45.103.0", {"center": v(26.23, -12.82) * mm, "radius": 0.1 * mm});
            skCircle(sketch, "E45.104.0", {"center": v(26.74, -11.73) * mm, "radius": 0.1 * mm});
            skCircle(sketch, "E45.105.0", {"center": v(27.2, -10.61) * mm, "radius": 0.1 * mm});
            skCircle(sketch, "E45.106.0", {"center": v(27.62, -9.48) * mm, "radius": 0.1 * mm});
            skCircle(sketch, "E45.107.0", {"center": v(27.99, -8.33) * mm, "radius": 0.1 * mm});
            skCircle(sketch, "E45.108.0", {"center": v(28.3, -7.17) * mm, "radius": 0.1 * mm});
            skCircle(sketch, "E45.109.0", {"center": v(28.58, -6) * mm, "radius": 0.1 * mm});
            skCircle(sketch, "E45.110.0", {"center": v(28.8, -4.8) * mm, "radius": 0.1 * mm});
            skCircle(sketch, "E45.111.0", {"center": v(28.98, -3.61) * mm, "radius": 0.1 * mm});
            skCircle(sketch, "E45.112.0", {"center": v(29.1, -2.41) * mm, "radius": 0.1 * mm});
            skCircle(sketch, "E45.113.0", {"center": v(29.18, -1.2) * mm, "radius": 0.1 * mm});
            skCircle(sketch, "E45.114.0", {"center": v(29.2, 0) * mm, "radius": 0.1 * mm});
            skCircle(sketch, "E45.115.0", {"center": v(29.18, 1.2) * mm, "radius": 0.1 * mm});
            skCircle(sketch, "E45.116.0", {"center": v(29.1, 2.41) * mm, "radius": 0.1 * mm});
            skCircle(sketch, "E45.117.0", {"center": v(28.98, 3.61) * mm, "radius": 0.1 * mm});
            skCircle(sketch, "E45.118.0", {"center": v(28.8, 4.8) * mm, "radius": 0.1 * mm});
            skCircle(sketch, "E45.119.0", {"center": v(28.58, 6) * mm, "radius": 0.1 * mm});
            skCircle(sketch, "E45.120.0", {"center": v(28.3, 7.17) * mm, "radius": 0.1 * mm});
            skCircle(sketch, "E45.121.0", {"center": v(27.99, 8.33) * mm, "radius": 0.1 * mm});
            skCircle(sketch, "E45.122.0", {"center": v(27.62, 9.48) * mm, "radius": 0.1 * mm});
            skCircle(sketch, "E45.123.0", {"center": v(27.2, 10.61) * mm, "radius": 0.1 * mm});
            skCircle(sketch, "E45.124.0", {"center": v(26.74, 11.73) * mm, "radius": 0.1 * mm});
            skCircle(sketch, "E45.125.0", {"center": v(26.23, 12.82) * mm, "radius": 0.1 * mm});
            skCircle(sketch, "E45.126.0", {"center": v(25.68, 13.9) * mm, "radius": 0.1 * mm});
            skCircle(sketch, "E45.127.0", {"center": v(25.08, 14.95) * mm, "radius": 0.1 * mm});
            skCircle(sketch, "E45.128.0", {"center": v(24.45, 15.97) * mm, "radius": 0.1 * mm});
            skCircle(sketch, "E45.129.0", {"center": v(23.76, 16.97) * mm, "radius": 0.1 * mm});
            skCircle(sketch, "E45.130.0", {"center": v(23.04, 17.94) * mm, "radius": 0.1 * mm});
            skCircle(sketch, "E45.131.0", {"center": v(22.28, 18.87) * mm, "radius": 0.1 * mm});
            skCircle(sketch, "E45.132.0", {"center": v(21.48, 19.78) * mm, "radius": 0.1 * mm});
            skCircle(sketch, "E45.133.0", {"center": v(20.65, 20.65) * mm, "radius": 0.1 * mm});
            skCircle(sketch, "E45.134.0", {"center": v(19.78, 21.48) * mm, "radius": 0.1 * mm});
            skCircle(sketch, "E45.135.0", {"center": v(18.87, 22.28) * mm, "radius": 0.1 * mm});
            skCircle(sketch, "E45.136.0", {"center": v(17.94, 23.04) * mm, "radius": 0.1 * mm});
            skCircle(sketch, "E45.137.0", {"center": v(16.97, 23.76) * mm, "radius": 0.1 * mm});
            skCircle(sketch, "E45.138.0", {"center": v(15.97, 24.45) * mm, "radius": 0.1 * mm});
            skCircle(sketch, "E45.139.0", {"center": v(14.95, 25.08) * mm, "radius": 0.1 * mm});
            skCircle(sketch, "E45.140.0", {"center": v(13.9, 25.68) * mm, "radius": 0.1 * mm});
            skCircle(sketch, "E45.141.0", {"center": v(12.82, 26.23) * mm, "radius": 0.1 * mm});
            skCircle(sketch, "E45.142.0", {"center": v(11.73, 26.74) * mm, "radius": 0.1 * mm});
            skCircle(sketch, "E45.143.0", {"center": v(10.61, 27.2) * mm, "radius": 0.1 * mm});
            skCircle(sketch, "E45.144.0", {"center": v(9.48, 27.62) * mm, "radius": 0.1 * mm});
            skCircle(sketch, "E45.145.0", {"center": v(8.33, 27.99) * mm, "radius": 0.1 * mm});
            skCircle(sketch, "E45.146.0", {"center": v(7.17, 28.3) * mm, "radius": 0.1 * mm});
            skCircle(sketch, "E45.147.0", {"center": v(6, 28.58) * mm, "radius": 0.1 * mm});
            skCircle(sketch, "E45.148.0", {"center": v(4.8, 28.8) * mm, "radius": 0.1 * mm});
            skCircle(sketch, "E45.149.0", {"center": v(3.61, 28.98) * mm, "radius": 0.1 * mm});
            skCircle(sketch, "E45.150.0", {"center": v(2.41, 29.1) * mm, "radius": 0.1 * mm});
            skCircle(sketch, "E45.151.0", {"center": v(1.2, 29.18) * mm, "radius": 0.1 * mm});
            skSolve(sketch);
        }
        {
            var Q0;
            Q0=makeQuery(id+"F6.imprint","IMPRINT",FACE,{"disambiguationData":[TD([[makeQuery(id+"F6.imprint","IMPRINT",EDGE,{"derivedFrom":sQuery(id+"F6.wireOp",EDGE,"E5")}),-1.0]])]});
            extrude(context, id + "F7", {"entities" : qUnion([Q0]), "operationType" : NewBodyOperationType.REMOVE, "oppositeDirection" : true, "depth" : 0.2 * mm, "offsetDistance" : 25 * mm});
        }
        {
            var Q0;
            Q0=makeQuery(id+"F3.boolean.opBoolean","COPY",FACE,{"derivedFrom":makeQuery(id+"F3.opExtrude","CAP_FACE",FACE,{"disambiguationData":[OSD([sQuery(id+"F2.wireOp",EDGE,"E1")])],"isStart":false})});
            var sketch = newSketch(context, id + "F8", { "sketchPlane" : qUnion([Q0])});
            skCircle(sketch, "E46", {"center": v(0, 0) * mm, "radius": 5 * mm, "construction": true});
            skLineSegment(sketch, "E47", {"start": v(0, 0) * mm, "end": v(0, 30) * mm, "construction": true});
            skLineSegment(sketch, "E48", {"start": v(0, 5) * mm, "end": v(-2.84, 5) * mm, "construction": true});
            skCircle(sketch, "E49", {"center": v(0, 5.8) * mm, "radius": 0.5 * mm});
            skCircle(sketch, "E50", {"center": v(0, 7.1) * mm, "radius": 0.5 * mm});
            skCircle(sketch, "E51", {"center": v(0, 8.4) * mm, "radius": 0.5 * mm});
            skCircle(sketch, "E52", {"center": v(0, 9.7) * mm, "radius": 0.5 * mm});
            skCircle(sketch, "E53", {"center": v(0, 11) * mm, "radius": 0.5 * mm});
            skLineSegment(sketch, "E54", {"start": v(-1.18, 11.65) * mm, "end": v(1.98, 11.65) * mm, "construction": true});
            skCircle(sketch, "E55.MirrorC", {"center": v(0, 12.3) * mm, "radius": 0.5 * mm});
            skCircle(sketch, "E56.MirrorC", {"center": v(0, 13.6) * mm, "radius": 0.5 * mm});
            skCircle(sketch, "E57.MirrorC", {"center": v(0, 14.9) * mm, "radius": 0.5 * mm});
            skCircle(sketch, "E58.MirrorC", {"center": v(0, 16.2) * mm, "radius": 0.5 * mm});
            skCircle(sketch, "E59.MirrorC", {"center": v(0, 17.5) * mm, "radius": 0.5 * mm});
            skLineSegment(sketch, "E60", {"start": v(-1.26, 18.15) * mm, "end": v(1.37, 18.15) * mm, "construction": true});
            skCircle(sketch, "E61.MirrorC", {"center": v(0, 18.8) * mm, "radius": 0.5 * mm});
            skCircle(sketch, "E62.MirrorC", {"center": v(0, 20.1) * mm, "radius": 0.5 * mm});
            skCircle(sketch, "E63.MirrorC", {"center": v(0, 21.4) * mm, "radius": 0.5 * mm});
            skCircle(sketch, "E64.MirrorC", {"center": v(0, 22.7) * mm, "radius": 0.5 * mm});
            skCircle(sketch, "E65.MirrorC", {"center": v(0, 24) * mm, "radius": 0.5 * mm});
            skCircle(sketch, "E66.MirrorC", {"center": v(0, 25.3) * mm, "radius": 0.5 * mm});
            skCircle(sketch, "E67.MirrorC", {"center": v(0, 26.6) * mm, "radius": 0.5 * mm});
            skCircle(sketch, "E68.MirrorC", {"center": v(0, 27.9) * mm, "radius": 0.5 * mm});
            skCircle(sketch, "E69.MirrorC", {"center": v(0, 29.2) * mm, "radius": 0.5 * mm});
            skCircle(sketch, "E70.1.0", {"center": v(-1.39, 5.63) * mm, "radius": 0.5 * mm});
            skCircle(sketch, "E70.2.0", {"center": v(-2.7, 5.14) * mm, "radius": 0.5 * mm});
            skCircle(sketch, "E70.3.0", {"center": v(-3.85, 4.34) * mm, "radius": 0.5 * mm});
            skCircle(sketch, "E70.4.0", {"center": v(-4.77, 3.3) * mm, "radius": 0.5 * mm});
            skCircle(sketch, "E70.5.0", {"center": v(-5.42, 2.06) * mm, "radius": 0.5 * mm});
            skCircle(sketch, "E70.6.0", {"center": v(-5.76, 0.7) * mm, "radius": 0.5 * mm});
            skCircle(sketch, "E70.7.0", {"center": v(-5.76, -0.7) * mm, "radius": 0.5 * mm});
            skCircle(sketch, "E70.8.0", {"center": v(-5.42, -2.06) * mm, "radius": 0.5 * mm});
            skCircle(sketch, "E70.9.0", {"center": v(-4.77, -3.3) * mm, "radius": 0.5 * mm});
            skCircle(sketch, "E70.10.0", {"center": v(-3.85, -4.34) * mm, "radius": 0.5 * mm});
            skCircle(sketch, "E70.11.0", {"center": v(-2.7, -5.14) * mm, "radius": 0.5 * mm});
            skCircle(sketch, "E70.12.0", {"center": v(-1.39, -5.63) * mm, "radius": 0.5 * mm});
            skCircle(sketch, "E70.13.0", {"center": v(0, -5.8) * mm, "radius": 0.5 * mm});
            skCircle(sketch, "E70.14.0", {"center": v(1.39, -5.63) * mm, "radius": 0.5 * mm});
            skCircle(sketch, "E70.15.0", {"center": v(2.7, -5.14) * mm, "radius": 0.5 * mm});
            skCircle(sketch, "E70.16.0", {"center": v(3.85, -4.34) * mm, "radius": 0.5 * mm});
            skCircle(sketch, "E70.17.0", {"center": v(4.77, -3.3) * mm, "radius": 0.5 * mm});
            skCircle(sketch, "E70.18.0", {"center": v(5.42, -2.06) * mm, "radius": 0.5 * mm});
            skCircle(sketch, "E70.19.0", {"center": v(5.76, -0.7) * mm, "radius": 0.5 * mm});
            skCircle(sketch, "E70.20.0", {"center": v(5.76, 0.7) * mm, "radius": 0.5 * mm});
            skCircle(sketch, "E70.21.0", {"center": v(5.42, 2.06) * mm, "radius": 0.5 * mm});
            skCircle(sketch, "E70.22.0", {"center": v(4.77, 3.3) * mm, "radius": 0.5 * mm});
            skCircle(sketch, "E70.23.0", {"center": v(3.85, 4.34) * mm, "radius": 0.5 * mm});
            skCircle(sketch, "E70.24.0", {"center": v(2.7, 5.14) * mm, "radius": 0.5 * mm});
            skCircle(sketch, "E70.25.0", {"center": v(1.39, 5.63) * mm, "radius": 0.5 * mm});
            skCircle(sketch, "E71.1.0", {"center": v(-1.34, 6.97) * mm, "radius": 0.5 * mm});
            skCircle(sketch, "E71.2.0", {"center": v(-2.64, 6.6) * mm, "radius": 0.5 * mm});
            skCircle(sketch, "E71.3.0", {"center": v(-3.84, 5.97) * mm, "radius": 0.5 * mm});
            skCircle(sketch, "E71.4.0", {"center": v(-4.9, 5.14) * mm, "radius": 0.5 * mm});
            skCircle(sketch, "E71.5.0", {"center": v(-5.78, 4.12) * mm, "radius": 0.5 * mm});
            skCircle(sketch, "E71.6.0", {"center": v(-6.46, 2.95) * mm, "radius": 0.5 * mm});
            skCircle(sketch, "E71.7.0", {"center": v(-6.9, 1.67) * mm, "radius": 0.5 * mm});
            skCircle(sketch, "E71.8.0", {"center": v(-7.1, 0.34) * mm, "radius": 0.5 * mm});
            skCircle(sketch, "E71.9.0", {"center": v(-7.03, -1.01) * mm, "radius": 0.5 * mm});
            skCircle(sketch, "E71.10.0", {"center": v(-6.7, -2.32) * mm, "radius": 0.5 * mm});
            skCircle(sketch, "E71.11.0", {"center": v(-6.15, -3.55) * mm, "radius": 0.5 * mm});
            skCircle(sketch, "E71.12.0", {"center": v(-5.37, -4.65) * mm, "radius": 0.5 * mm});
            skCircle(sketch, "E71.13.0", {"center": v(-4.39, -5.58) * mm, "radius": 0.5 * mm});
            skCircle(sketch, "E71.14.0", {"center": v(-3.25, -6.31) * mm, "radius": 0.5 * mm});
            skCircle(sketch, "E71.15.0", {"center": v(-2, -6.81) * mm, "radius": 0.5 * mm});
            skCircle(sketch, "E71.16.0", {"center": v(-0.67, -7.07) * mm, "radius": 0.5 * mm});
            skCircle(sketch, "E71.17.0", {"center": v(0.67, -7.07) * mm, "radius": 0.5 * mm});
            skCircle(sketch, "E71.18.0", {"center": v(2, -6.81) * mm, "radius": 0.5 * mm});
            skCircle(sketch, "E71.19.0", {"center": v(3.25, -6.31) * mm, "radius": 0.5 * mm});
            skCircle(sketch, "E71.20.0", {"center": v(4.39, -5.58) * mm, "radius": 0.5 * mm});
            skCircle(sketch, "E71.21.0", {"center": v(5.37, -4.65) * mm, "radius": 0.5 * mm});
            skCircle(sketch, "E71.22.0", {"center": v(6.15, -3.55) * mm, "radius": 0.5 * mm});
            skCircle(sketch, "E71.23.0", {"center": v(6.7, -2.32) * mm, "radius": 0.5 * mm});
            skCircle(sketch, "E71.24.0", {"center": v(7.03, -1.01) * mm, "radius": 0.5 * mm});
            skCircle(sketch, "E71.25.0", {"center": v(7.1, 0.34) * mm, "radius": 0.5 * mm});
            skCircle(sketch, "E71.26.0", {"center": v(6.9, 1.67) * mm, "radius": 0.5 * mm});
            skCircle(sketch, "E71.27.0", {"center": v(6.46, 2.95) * mm, "radius": 0.5 * mm});
            skCircle(sketch, "E71.28.0", {"center": v(5.78, 4.12) * mm, "radius": 0.5 * mm});
            skCircle(sketch, "E71.29.0", {"center": v(4.9, 5.14) * mm, "radius": 0.5 * mm});
            skCircle(sketch, "E71.30.0", {"center": v(3.84, 5.97) * mm, "radius": 0.5 * mm});
            skCircle(sketch, "E71.31.0", {"center": v(2.64, 6.6) * mm, "radius": 0.5 * mm});
            skCircle(sketch, "E71.32.0", {"center": v(1.34, 6.97) * mm, "radius": 0.5 * mm});
            skCircle(sketch, "E72.1.0", {"center": v(-1.31, 8.3) * mm, "radius": 0.5 * mm});
            skCircle(sketch, "E72.2.0", {"center": v(-2.6, 7.99) * mm, "radius": 0.5 * mm});
            skCircle(sketch, "E72.3.0", {"center": v(-3.81, 7.48) * mm, "radius": 0.5 * mm});
            skCircle(sketch, "E72.4.0", {"center": v(-4.94, 6.8) * mm, "radius": 0.5 * mm});
            skCircle(sketch, "E72.5.0", {"center": v(-5.94, 5.94) * mm, "radius": 0.5 * mm});
            skCircle(sketch, "E72.6.0", {"center": v(-6.8, 4.94) * mm, "radius": 0.5 * mm});
            skCircle(sketch, "E72.7.0", {"center": v(-7.48, 3.81) * mm, "radius": 0.5 * mm});
            skCircle(sketch, "E72.8.0", {"center": v(-7.99, 2.6) * mm, "radius": 0.5 * mm});
            skCircle(sketch, "E72.9.0", {"center": v(-8.3, 1.31) * mm, "radius": 0.5 * mm});
            skCircle(sketch, "E72.10.0", {"center": v(-8.4, 0) * mm, "radius": 0.5 * mm});
            skCircle(sketch, "E72.11.0", {"center": v(-8.3, -1.31) * mm, "radius": 0.5 * mm});
            skCircle(sketch, "E72.12.0", {"center": v(-7.99, -2.6) * mm, "radius": 0.5 * mm});
            skCircle(sketch, "E72.13.0", {"center": v(-7.48, -3.81) * mm, "radius": 0.5 * mm});
            skCircle(sketch, "E72.14.0", {"center": v(-6.8, -4.94) * mm, "radius": 0.5 * mm});
            skCircle(sketch, "E72.15.0", {"center": v(-5.94, -5.94) * mm, "radius": 0.5 * mm});
            skCircle(sketch, "E72.16.0", {"center": v(-4.94, -6.8) * mm, "radius": 0.5 * mm});
            skCircle(sketch, "E72.17.0", {"center": v(-3.81, -7.48) * mm, "radius": 0.5 * mm});
            skCircle(sketch, "E72.18.0", {"center": v(-2.6, -7.99) * mm, "radius": 0.5 * mm});
            skCircle(sketch, "E72.19.0", {"center": v(-1.31, -8.3) * mm, "radius": 0.5 * mm});
            skCircle(sketch, "E72.20.0", {"center": v(0, -8.4) * mm, "radius": 0.5 * mm});
            skCircle(sketch, "E72.21.0", {"center": v(1.31, -8.3) * mm, "radius": 0.5 * mm});
            skCircle(sketch, "E72.22.0", {"center": v(2.6, -7.99) * mm, "radius": 0.5 * mm});
            skCircle(sketch, "E72.23.0", {"center": v(3.81, -7.48) * mm, "radius": 0.5 * mm});
            skCircle(sketch, "E72.24.0", {"center": v(4.94, -6.8) * mm, "radius": 0.5 * mm});
            skCircle(sketch, "E72.25.0", {"center": v(5.94, -5.94) * mm, "radius": 0.5 * mm});
            skCircle(sketch, "E72.26.0", {"center": v(6.8, -4.94) * mm, "radius": 0.5 * mm});
            skCircle(sketch, "E72.27.0", {"center": v(7.48, -3.81) * mm, "radius": 0.5 * mm});
            skCircle(sketch, "E72.28.0", {"center": v(7.99, -2.6) * mm, "radius": 0.5 * mm});
            skCircle(sketch, "E72.29.0", {"center": v(8.3, -1.31) * mm, "radius": 0.5 * mm});
            skCircle(sketch, "E72.30.0", {"center": v(8.4, 0) * mm, "radius": 0.5 * mm});
            skCircle(sketch, "E72.31.0", {"center": v(8.3, 1.31) * mm, "radius": 0.5 * mm});
            skCircle(sketch, "E72.32.0", {"center": v(7.99, 2.6) * mm, "radius": 0.5 * mm});
            skCircle(sketch, "E72.33.0", {"center": v(7.48, 3.81) * mm, "radius": 0.5 * mm});
            skCircle(sketch, "E72.34.0", {"center": v(6.8, 4.94) * mm, "radius": 0.5 * mm});
            skCircle(sketch, "E72.35.0", {"center": v(5.94, 5.94) * mm, "radius": 0.5 * mm});
            skCircle(sketch, "E72.36.0", {"center": v(4.94, 6.8) * mm, "radius": 0.5 * mm});
            skCircle(sketch, "E72.37.0", {"center": v(3.81, 7.48) * mm, "radius": 0.5 * mm});
            skCircle(sketch, "E72.38.0", {"center": v(2.6, 7.99) * mm, "radius": 0.5 * mm});
            skCircle(sketch, "E72.39.0", {"center": v(1.31, 8.3) * mm, "radius": 0.5 * mm});
            skCircle(sketch, "E73.1.0", {"center": v(-1.3, 9.61) * mm, "radius": 0.5 * mm});
            skCircle(sketch, "E73.2.0", {"center": v(-2.56, 9.36) * mm, "radius": 0.5 * mm});
            skCircle(sketch, "E73.3.0", {"center": v(-3.79, 8.93) * mm, "radius": 0.5 * mm});
            skCircle(sketch, "E73.4.0", {"center": v(-4.94, 8.35) * mm, "radius": 0.5 * mm});
            skCircle(sketch, "E73.5.0", {"center": v(-6.01, 7.61) * mm, "radius": 0.5 * mm});
            skCircle(sketch, "E73.6.0", {"center": v(-6.97, 6.74) * mm, "radius": 0.5 * mm});
            skCircle(sketch, "E73.7.0", {"center": v(-7.8, 5.75) * mm, "radius": 0.5 * mm});
            skCircle(sketch, "E73.8.0", {"center": v(-8.5, 4.66) * mm, "radius": 0.5 * mm});
            skCircle(sketch, "E73.9.0", {"center": v(-9.05, 3.49) * mm, "radius": 0.5 * mm});
            skCircle(sketch, "E73.10.0", {"center": v(-9.44, 2.25) * mm, "radius": 0.5 * mm});
            skCircle(sketch, "E73.11.0", {"center": v(-9.65, 0.97) * mm, "radius": 0.5 * mm});
            skCircle(sketch, "E73.12.0", {"center": v(-9.7, -0.32) * mm, "radius": 0.5 * mm});
            skCircle(sketch, "E73.13.0", {"center": v(-9.56, -1.61) * mm, "radius": 0.5 * mm});
            skCircle(sketch, "E73.14.0", {"center": v(-9.26, -2.87) * mm, "radius": 0.5 * mm});
            skCircle(sketch, "E73.15.0", {"center": v(-8.8, -4.08) * mm, "radius": 0.5 * mm});
            skCircle(sketch, "E73.16.0", {"center": v(-8.18, -5.22) * mm, "radius": 0.5 * mm});
            skCircle(sketch, "E73.17.0", {"center": v(-7.4, -6.26) * mm, "radius": 0.5 * mm});
            skCircle(sketch, "E73.18.0", {"center": v(-6.5, -7.2) * mm, "radius": 0.5 * mm});
            skCircle(sketch, "E73.19.0", {"center": v(-5.49, -8) * mm, "radius": 0.5 * mm});
            skCircle(sketch, "E73.20.0", {"center": v(-4.37, -8.66) * mm, "radius": 0.5 * mm});
            skCircle(sketch, "E73.21.0", {"center": v(-3.18, -9.16) * mm, "radius": 0.5 * mm});
            skCircle(sketch, "E73.22.0", {"center": v(-1.93, -9.5) * mm, "radius": 0.5 * mm});
            skCircle(sketch, "E73.23.0", {"center": v(-0.65, -9.68) * mm, "radius": 0.5 * mm});
            skCircle(sketch, "E73.24.0", {"center": v(0.65, -9.68) * mm, "radius": 0.5 * mm});
            skCircle(sketch, "E73.25.0", {"center": v(1.93, -9.5) * mm, "radius": 0.5 * mm});
            skCircle(sketch, "E73.26.0", {"center": v(3.18, -9.16) * mm, "radius": 0.5 * mm});
            skCircle(sketch, "E73.27.0", {"center": v(4.37, -8.66) * mm, "radius": 0.5 * mm});
            skCircle(sketch, "E73.28.0", {"center": v(5.49, -8) * mm, "radius": 0.5 * mm});
            skCircle(sketch, "E73.29.0", {"center": v(6.5, -7.2) * mm, "radius": 0.5 * mm});
            skCircle(sketch, "E73.30.0", {"center": v(7.4, -6.26) * mm, "radius": 0.5 * mm});
            skCircle(sketch, "E73.31.0", {"center": v(8.18, -5.22) * mm, "radius": 0.5 * mm});
            skCircle(sketch, "E73.32.0", {"center": v(8.8, -4.08) * mm, "radius": 0.5 * mm});
            skCircle(sketch, "E73.33.0", {"center": v(9.26, -2.87) * mm, "radius": 0.5 * mm});
            skCircle(sketch, "E73.34.0", {"center": v(9.56, -1.61) * mm, "radius": 0.5 * mm});
            skCircle(sketch, "E73.35.0", {"center": v(9.7, -0.32) * mm, "radius": 0.5 * mm});
            skCircle(sketch, "E73.36.0", {"center": v(9.65, 0.97) * mm, "radius": 0.5 * mm});
            skCircle(sketch, "E73.37.0", {"center": v(9.44, 2.25) * mm, "radius": 0.5 * mm});
            skCircle(sketch, "E73.38.0", {"center": v(9.05, 3.49) * mm, "radius": 0.5 * mm});
            skCircle(sketch, "E73.39.0", {"center": v(8.5, 4.66) * mm, "radius": 0.5 * mm});
            skCircle(sketch, "E73.40.0", {"center": v(7.8, 5.75) * mm, "radius": 0.5 * mm});
            skCircle(sketch, "E73.41.0", {"center": v(6.97, 6.74) * mm, "radius": 0.5 * mm});
            skCircle(sketch, "E73.42.0", {"center": v(6.01, 7.61) * mm, "radius": 0.5 * mm});
            skCircle(sketch, "E73.43.0", {"center": v(4.94, 8.35) * mm, "radius": 0.5 * mm});
            skCircle(sketch, "E73.44.0", {"center": v(3.79, 8.93) * mm, "radius": 0.5 * mm});
            skCircle(sketch, "E73.45.0", {"center": v(2.56, 9.36) * mm, "radius": 0.5 * mm});
            skCircle(sketch, "E73.46.0", {"center": v(1.3, 9.61) * mm, "radius": 0.5 * mm});
            skCircle(sketch, "E74.1.0", {"center": v(-1.28, 10.93) * mm, "radius": 0.5 * mm});
            skCircle(sketch, "E74.2.0", {"center": v(-2.54, 10.7) * mm, "radius": 0.5 * mm});
            skCircle(sketch, "E74.3.0", {"center": v(-3.76, 10.34) * mm, "radius": 0.5 * mm});
            skCircle(sketch, "E74.4.0", {"center": v(-4.94, 9.83) * mm, "radius": 0.5 * mm});
            skCircle(sketch, "E74.5.0", {"center": v(-6.04, 9.2) * mm, "radius": 0.5 * mm});
            skCircle(sketch, "E74.6.0", {"center": v(-7.07, 8.43) * mm, "radius": 0.5 * mm});
            skCircle(sketch, "E74.7.0", {"center": v(-8, 7.55) * mm, "radius": 0.5 * mm});
            skCircle(sketch, "E74.8.0", {"center": v(-8.82, 6.57) * mm, "radius": 0.5 * mm});
            skCircle(sketch, "E74.9.0", {"center": v(-9.53, 5.5) * mm, "radius": 0.5 * mm});
            skCircle(sketch, "E74.10.0", {"center": v(-10.1, 4.36) * mm, "radius": 0.5 * mm});
            skCircle(sketch, "E74.11.0", {"center": v(-10.54, 3.15) * mm, "radius": 0.5 * mm});
            skCircle(sketch, "E74.12.0", {"center": v(-10.83, 1.91) * mm, "radius": 0.5 * mm});
            skCircle(sketch, "E74.13.0", {"center": v(-10.98, 0.64) * mm, "radius": 0.5 * mm});
            skCircle(sketch, "E74.14.0", {"center": v(-10.98, -0.64) * mm, "radius": 0.5 * mm});
            skCircle(sketch, "E74.15.0", {"center": v(-10.83, -1.91) * mm, "radius": 0.5 * mm});
            skCircle(sketch, "E74.16.0", {"center": v(-10.54, -3.15) * mm, "radius": 0.5 * mm});
            skCircle(sketch, "E74.17.0", {"center": v(-10.1, -4.36) * mm, "radius": 0.5 * mm});
            skCircle(sketch, "E74.18.0", {"center": v(-9.53, -5.5) * mm, "radius": 0.5 * mm});
            skCircle(sketch, "E74.19.0", {"center": v(-8.82, -6.57) * mm, "radius": 0.5 * mm});
            skCircle(sketch, "E74.20.0", {"center": v(-8, -7.55) * mm, "radius": 0.5 * mm});
            skCircle(sketch, "E74.21.0", {"center": v(-7.07, -8.43) * mm, "radius": 0.5 * mm});
            skCircle(sketch, "E74.22.0", {"center": v(-6.04, -9.2) * mm, "radius": 0.5 * mm});
            skCircle(sketch, "E74.23.0", {"center": v(-4.94, -9.83) * mm, "radius": 0.5 * mm});
            skCircle(sketch, "E74.24.0", {"center": v(-3.76, -10.34) * mm, "radius": 0.5 * mm});
            skCircle(sketch, "E74.25.0", {"center": v(-2.54, -10.7) * mm, "radius": 0.5 * mm});
            skCircle(sketch, "E74.26.0", {"center": v(-1.28, -10.93) * mm, "radius": 0.5 * mm});
            skCircle(sketch, "E74.27.0", {"center": v(0, -11) * mm, "radius": 0.5 * mm});
            skCircle(sketch, "E74.28.0", {"center": v(1.28, -10.93) * mm, "radius": 0.5 * mm});
            skCircle(sketch, "E74.29.0", {"center": v(2.54, -10.7) * mm, "radius": 0.5 * mm});
            skCircle(sketch, "E74.30.0", {"center": v(3.76, -10.34) * mm, "radius": 0.5 * mm});
            skCircle(sketch, "E74.31.0", {"center": v(4.94, -9.83) * mm, "radius": 0.5 * mm});
            skCircle(sketch, "E74.32.0", {"center": v(6.04, -9.2) * mm, "radius": 0.5 * mm});
            skCircle(sketch, "E74.33.0", {"center": v(7.07, -8.43) * mm, "radius": 0.5 * mm});
            skCircle(sketch, "E74.34.0", {"center": v(8, -7.55) * mm, "radius": 0.5 * mm});
            skCircle(sketch, "E74.35.0", {"center": v(8.82, -6.57) * mm, "radius": 0.5 * mm});
            skCircle(sketch, "E74.36.0", {"center": v(9.53, -5.5) * mm, "radius": 0.5 * mm});
            skCircle(sketch, "E74.37.0", {"center": v(10.1, -4.36) * mm, "radius": 0.5 * mm});
            skCircle(sketch, "E74.38.0", {"center": v(10.54, -3.15) * mm, "radius": 0.5 * mm});
            skCircle(sketch, "E74.39.0", {"center": v(10.83, -1.91) * mm, "radius": 0.5 * mm});
            skCircle(sketch, "E74.40.0", {"center": v(10.98, -0.64) * mm, "radius": 0.5 * mm});
            skCircle(sketch, "E74.41.0", {"center": v(10.98, 0.64) * mm, "radius": 0.5 * mm});
            skCircle(sketch, "E74.42.0", {"center": v(10.83, 1.91) * mm, "radius": 0.5 * mm});
            skCircle(sketch, "E74.43.0", {"center": v(10.54, 3.15) * mm, "radius": 0.5 * mm});
            skCircle(sketch, "E74.44.0", {"center": v(10.1, 4.36) * mm, "radius": 0.5 * mm});
            skCircle(sketch, "E74.45.0", {"center": v(9.53, 5.5) * mm, "radius": 0.5 * mm});
            skCircle(sketch, "E74.46.0", {"center": v(8.82, 6.57) * mm, "radius": 0.5 * mm});
            skCircle(sketch, "E74.47.0", {"center": v(8, 7.55) * mm, "radius": 0.5 * mm});
            skCircle(sketch, "E74.48.0", {"center": v(7.07, 8.43) * mm, "radius": 0.5 * mm});
            skCircle(sketch, "E74.49.0", {"center": v(6.04, 9.2) * mm, "radius": 0.5 * mm});
            skCircle(sketch, "E74.50.0", {"center": v(4.94, 9.83) * mm, "radius": 0.5 * mm});
            skCircle(sketch, "E74.51.0", {"center": v(3.76, 10.34) * mm, "radius": 0.5 * mm});
            skCircle(sketch, "E74.52.0", {"center": v(2.54, 10.7) * mm, "radius": 0.5 * mm});
            skCircle(sketch, "E74.53.0", {"center": v(1.28, 10.93) * mm, "radius": 0.5 * mm});
            skCircle(sketch, "E75.1.0", {"center": v(-1.26, 12.23) * mm, "radius": 0.5 * mm});
            skCircle(sketch, "E75.2.0", {"center": v(-2.52, 12.04) * mm, "radius": 0.5 * mm});
            skCircle(sketch, "E75.3.0", {"center": v(-3.74, 11.72) * mm, "radius": 0.5 * mm});
            skCircle(sketch, "E75.4.0", {"center": v(-4.93, 11.27) * mm, "radius": 0.5 * mm});
            skCircle(sketch, "E75.5.0", {"center": v(-6.06, 10.7) * mm, "radius": 0.5 * mm});
            skCircle(sketch, "E75.6.0", {"center": v(-7.13, 10.02) * mm, "radius": 0.5 * mm});
            skCircle(sketch, "E75.7.0", {"center": v(-8.12, 9.24) * mm, "radius": 0.5 * mm});
            skCircle(sketch, "E75.8.0", {"center": v(-9.03, 8.36) * mm, "radius": 0.5 * mm});
            skCircle(sketch, "E75.9.0", {"center": v(-9.84, 7.38) * mm, "radius": 0.5 * mm});
            skCircle(sketch, "E75.10.0", {"center": v(-10.54, 6.33) * mm, "radius": 0.5 * mm});
            skCircle(sketch, "E75.11.0", {"center": v(-11.14, 5.21) * mm, "radius": 0.5 * mm});
            skCircle(sketch, "E75.12.0", {"center": v(-11.62, 4.04) * mm, "radius": 0.5 * mm});
            skCircle(sketch, "E75.13.0", {"center": v(-11.97, 2.83) * mm, "radius": 0.5 * mm});
            skCircle(sketch, "E75.14.0", {"center": v(-12.2, 1.58) * mm, "radius": 0.5 * mm});
            skCircle(sketch, "E75.15.0", {"center": v(-12.3, 0.32) * mm, "radius": 0.5 * mm});
            skCircle(sketch, "E75.16.0", {"center": v(-12.26, -0.95) * mm, "radius": 0.5 * mm});
            skCircle(sketch, "E75.17.0", {"center": v(-12.1, -2.2) * mm, "radius": 0.5 * mm});
            skCircle(sketch, "E75.18.0", {"center": v(-11.8, -3.44) * mm, "radius": 0.5 * mm});
            skCircle(sketch, "E75.19.0", {"center": v(-11.4, -4.63) * mm, "radius": 0.5 * mm});
            skCircle(sketch, "E75.20.0", {"center": v(-10.86, -5.78) * mm, "radius": 0.5 * mm});
            skCircle(sketch, "E75.21.0", {"center": v(-10.2, -6.87) * mm, "radius": 0.5 * mm});
            skCircle(sketch, "E75.22.0", {"center": v(-9.44, -7.88) * mm, "radius": 0.5 * mm});
            skCircle(sketch, "E75.23.0", {"center": v(-8.58, -8.8) * mm, "radius": 0.5 * mm});
            skCircle(sketch, "E75.24.0", {"center": v(-7.63, -9.64) * mm, "radius": 0.5 * mm});
            skCircle(sketch, "E75.25.0", {"center": v(-6.6, -10.38) * mm, "radius": 0.5 * mm});
            skCircle(sketch, "E75.26.0", {"center": v(-5.5, -11) * mm, "radius": 0.5 * mm});
            skCircle(sketch, "E75.27.0", {"center": v(-4.34, -11.5) * mm, "radius": 0.5 * mm});
            skCircle(sketch, "E75.28.0", {"center": v(-3.13, -11.9) * mm, "radius": 0.5 * mm});
            skCircle(sketch, "E75.29.0", {"center": v(-1.9, -12.15) * mm, "radius": 0.5 * mm});
            skCircle(sketch, "E75.30.0", {"center": v(-0.63, -12.28) * mm, "radius": 0.5 * mm});
            skCircle(sketch, "E75.31.0", {"center": v(0.63, -12.28) * mm, "radius": 0.5 * mm});
            skCircle(sketch, "E75.32.0", {"center": v(1.9, -12.15) * mm, "radius": 0.5 * mm});
            skCircle(sketch, "E75.33.0", {"center": v(3.13, -11.9) * mm, "radius": 0.5 * mm});
            skCircle(sketch, "E75.34.0", {"center": v(4.34, -11.5) * mm, "radius": 0.5 * mm});
            skCircle(sketch, "E75.35.0", {"center": v(5.5, -11) * mm, "radius": 0.5 * mm});
            skCircle(sketch, "E75.36.0", {"center": v(6.6, -10.38) * mm, "radius": 0.5 * mm});
            skCircle(sketch, "E75.37.0", {"center": v(7.63, -9.64) * mm, "radius": 0.5 * mm});
            skCircle(sketch, "E75.38.0", {"center": v(8.58, -8.8) * mm, "radius": 0.5 * mm});
            skCircle(sketch, "E75.39.0", {"center": v(9.44, -7.88) * mm, "radius": 0.5 * mm});
            skCircle(sketch, "E75.40.0", {"center": v(10.2, -6.87) * mm, "radius": 0.5 * mm});
            skCircle(sketch, "E75.41.0", {"center": v(10.86, -5.78) * mm, "radius": 0.5 * mm});
            skCircle(sketch, "E75.42.0", {"center": v(11.4, -4.63) * mm, "radius": 0.5 * mm});
            skCircle(sketch, "E75.43.0", {"center": v(11.8, -3.44) * mm, "radius": 0.5 * mm});
            skCircle(sketch, "E75.44.0", {"center": v(12.1, -2.2) * mm, "radius": 0.5 * mm});
            skCircle(sketch, "E75.45.0", {"center": v(12.26, -0.95) * mm, "radius": 0.5 * mm});
            skCircle(sketch, "E75.46.0", {"center": v(12.3, 0.32) * mm, "radius": 0.5 * mm});
            skCircle(sketch, "E75.47.0", {"center": v(12.2, 1.58) * mm, "radius": 0.5 * mm});
            skCircle(sketch, "E75.48.0", {"center": v(11.97, 2.83) * mm, "radius": 0.5 * mm});
            skCircle(sketch, "E75.49.0", {"center": v(11.62, 4.04) * mm, "radius": 0.5 * mm});
            skCircle(sketch, "E75.50.0", {"center": v(11.14, 5.21) * mm, "radius": 0.5 * mm});
            skCircle(sketch, "E75.51.0", {"center": v(10.54, 6.33) * mm, "radius": 0.5 * mm});
            skCircle(sketch, "E75.52.0", {"center": v(9.84, 7.38) * mm, "radius": 0.5 * mm});
            skCircle(sketch, "E75.53.0", {"center": v(9.03, 8.36) * mm, "radius": 0.5 * mm});
            skCircle(sketch, "E75.54.0", {"center": v(8.12, 9.24) * mm, "radius": 0.5 * mm});
            skCircle(sketch, "E75.55.0", {"center": v(7.13, 10.02) * mm, "radius": 0.5 * mm});
            skCircle(sketch, "E75.56.0", {"center": v(6.06, 10.7) * mm, "radius": 0.5 * mm});
            skCircle(sketch, "E75.57.0", {"center": v(4.93, 11.27) * mm, "radius": 0.5 * mm});
            skCircle(sketch, "E75.58.0", {"center": v(3.74, 11.72) * mm, "radius": 0.5 * mm});
            skCircle(sketch, "E75.59.0", {"center": v(2.52, 12.04) * mm, "radius": 0.5 * mm});
            skCircle(sketch, "E75.60.0", {"center": v(1.26, 12.23) * mm, "radius": 0.5 * mm});
            skCircle(sketch, "E76.1.0", {"center": v(-1.25, 13.54) * mm, "radius": 0.5 * mm});
            skCircle(sketch, "E76.2.0", {"center": v(-2.5, 13.37) * mm, "radius": 0.5 * mm});
            skCircle(sketch, "E76.3.0", {"center": v(-3.72, 13.08) * mm, "radius": 0.5 * mm});
            skCircle(sketch, "E76.4.0", {"center": v(-4.91, 12.68) * mm, "radius": 0.5 * mm});
            skCircle(sketch, "E76.5.0", {"center": v(-6.06, 12.17) * mm, "radius": 0.5 * mm});
            skCircle(sketch, "E76.6.0", {"center": v(-7.16, 11.56) * mm, "radius": 0.5 * mm});
            skCircle(sketch, "E76.7.0", {"center": v(-8.2, 10.85) * mm, "radius": 0.5 * mm});
            skCircle(sketch, "E76.8.0", {"center": v(-9.16, 10.05) * mm, "radius": 0.5 * mm});
            skCircle(sketch, "E76.9.0", {"center": v(-10.05, 9.16) * mm, "radius": 0.5 * mm});
            skCircle(sketch, "E76.10.0", {"center": v(-10.85, 8.2) * mm, "radius": 0.5 * mm});
            skCircle(sketch, "E76.11.0", {"center": v(-11.56, 7.16) * mm, "radius": 0.5 * mm});
            skCircle(sketch, "E76.12.0", {"center": v(-12.17, 6.06) * mm, "radius": 0.5 * mm});
            skCircle(sketch, "E76.13.0", {"center": v(-12.68, 4.91) * mm, "radius": 0.5 * mm});
            skCircle(sketch, "E76.14.0", {"center": v(-13.08, 3.72) * mm, "radius": 0.5 * mm});
            skCircle(sketch, "E76.15.0", {"center": v(-13.37, 2.5) * mm, "radius": 0.5 * mm});
            skCircle(sketch, "E76.16.0", {"center": v(-13.54, 1.25) * mm, "radius": 0.5 * mm});
            skCircle(sketch, "E76.17.0", {"center": v(-13.6, 0) * mm, "radius": 0.5 * mm});
            skCircle(sketch, "E76.18.0", {"center": v(-13.54, -1.25) * mm, "radius": 0.5 * mm});
            skCircle(sketch, "E76.19.0", {"center": v(-13.37, -2.5) * mm, "radius": 0.5 * mm});
            skCircle(sketch, "E76.20.0", {"center": v(-13.08, -3.72) * mm, "radius": 0.5 * mm});
            skCircle(sketch, "E76.21.0", {"center": v(-12.68, -4.91) * mm, "radius": 0.5 * mm});
            skCircle(sketch, "E76.22.0", {"center": v(-12.17, -6.06) * mm, "radius": 0.5 * mm});
            skCircle(sketch, "E76.23.0", {"center": v(-11.56, -7.16) * mm, "radius": 0.5 * mm});
            skCircle(sketch, "E76.24.0", {"center": v(-10.85, -8.2) * mm, "radius": 0.5 * mm});
            skCircle(sketch, "E76.25.0", {"center": v(-10.05, -9.16) * mm, "radius": 0.5 * mm});
            skCircle(sketch, "E76.26.0", {"center": v(-9.16, -10.05) * mm, "radius": 0.5 * mm});
            skCircle(sketch, "E76.27.0", {"center": v(-8.2, -10.85) * mm, "radius": 0.5 * mm});
            skCircle(sketch, "E76.28.0", {"center": v(-7.16, -11.56) * mm, "radius": 0.5 * mm});
            skCircle(sketch, "E76.29.0", {"center": v(-6.06, -12.17) * mm, "radius": 0.5 * mm});
            skCircle(sketch, "E76.30.0", {"center": v(-4.91, -12.68) * mm, "radius": 0.5 * mm});
            skCircle(sketch, "E76.31.0", {"center": v(-3.72, -13.08) * mm, "radius": 0.5 * mm});
            skCircle(sketch, "E76.32.0", {"center": v(-2.5, -13.37) * mm, "radius": 0.5 * mm});
            skCircle(sketch, "E76.33.0", {"center": v(-1.25, -13.54) * mm, "radius": 0.5 * mm});
            skCircle(sketch, "E76.34.0", {"center": v(0, -13.6) * mm, "radius": 0.5 * mm});
            skCircle(sketch, "E76.35.0", {"center": v(1.25, -13.54) * mm, "radius": 0.5 * mm});
            skCircle(sketch, "E76.36.0", {"center": v(2.5, -13.37) * mm, "radius": 0.5 * mm});
            skCircle(sketch, "E76.37.0", {"center": v(3.72, -13.08) * mm, "radius": 0.5 * mm});
            skCircle(sketch, "E76.38.0", {"center": v(4.91, -12.68) * mm, "radius": 0.5 * mm});
            skCircle(sketch, "E76.39.0", {"center": v(6.06, -12.17) * mm, "radius": 0.5 * mm});
            skCircle(sketch, "E76.40.0", {"center": v(7.16, -11.56) * mm, "radius": 0.5 * mm});
            skCircle(sketch, "E76.41.0", {"center": v(8.2, -10.85) * mm, "radius": 0.5 * mm});
            skCircle(sketch, "E76.42.0", {"center": v(9.16, -10.05) * mm, "radius": 0.5 * mm});
            skCircle(sketch, "E76.43.0", {"center": v(10.05, -9.16) * mm, "radius": 0.5 * mm});
            skCircle(sketch, "E76.44.0", {"center": v(10.85, -8.2) * mm, "radius": 0.5 * mm});
            skCircle(sketch, "E76.45.0", {"center": v(11.56, -7.16) * mm, "radius": 0.5 * mm});
            skCircle(sketch, "E76.46.0", {"center": v(12.17, -6.06) * mm, "radius": 0.5 * mm});
            skCircle(sketch, "E76.47.0", {"center": v(12.68, -4.91) * mm, "radius": 0.5 * mm});
            skCircle(sketch, "E76.48.0", {"center": v(13.08, -3.72) * mm, "radius": 0.5 * mm});
            skCircle(sketch, "E76.49.0", {"center": v(13.37, -2.5) * mm, "radius": 0.5 * mm});
            skCircle(sketch, "E76.50.0", {"center": v(13.54, -1.25) * mm, "radius": 0.5 * mm});
            skCircle(sketch, "E76.51.0", {"center": v(13.6, 0) * mm, "radius": 0.5 * mm});
            skCircle(sketch, "E76.52.0", {"center": v(13.54, 1.25) * mm, "radius": 0.5 * mm});
            skCircle(sketch, "E76.53.0", {"center": v(13.37, 2.5) * mm, "radius": 0.5 * mm});
            skCircle(sketch, "E76.54.0", {"center": v(13.08, 3.72) * mm, "radius": 0.5 * mm});
            skCircle(sketch, "E76.55.0", {"center": v(12.68, 4.91) * mm, "radius": 0.5 * mm});
            skCircle(sketch, "E76.56.0", {"center": v(12.17, 6.06) * mm, "radius": 0.5 * mm});
            skCircle(sketch, "E76.57.0", {"center": v(11.56, 7.16) * mm, "radius": 0.5 * mm});
            skCircle(sketch, "E76.58.0", {"center": v(10.85, 8.2) * mm, "radius": 0.5 * mm});
            skCircle(sketch, "E76.59.0", {"center": v(10.05, 9.16) * mm, "radius": 0.5 * mm});
            skCircle(sketch, "E76.60.0", {"center": v(9.16, 10.05) * mm, "radius": 0.5 * mm});
            skCircle(sketch, "E76.61.0", {"center": v(8.2, 10.85) * mm, "radius": 0.5 * mm});
            skCircle(sketch, "E76.62.0", {"center": v(7.16, 11.56) * mm, "radius": 0.5 * mm});
            skCircle(sketch, "E76.63.0", {"center": v(6.06, 12.17) * mm, "radius": 0.5 * mm});
            skCircle(sketch, "E76.64.0", {"center": v(4.91, 12.68) * mm, "radius": 0.5 * mm});
            skCircle(sketch, "E76.65.0", {"center": v(3.72, 13.08) * mm, "radius": 0.5 * mm});
            skCircle(sketch, "E76.66.0", {"center": v(2.5, 13.37) * mm, "radius": 0.5 * mm});
            skCircle(sketch, "E76.67.0", {"center": v(1.25, 13.54) * mm, "radius": 0.5 * mm});
            skCircle(sketch, "E77.1.0", {"center": v(-1.25, 14.85) * mm, "radius": 0.5 * mm});
            skCircle(sketch, "E77.2.0", {"center": v(-2.48, 14.7) * mm, "radius": 0.5 * mm});
            skCircle(sketch, "E77.3.0", {"center": v(-3.7, 14.43) * mm, "radius": 0.5 * mm});
            skCircle(sketch, "E77.4.0", {"center": v(-4.9, 14.07) * mm, "radius": 0.5 * mm});
            skCircle(sketch, "E77.5.0", {"center": v(-6.06, 13.61) * mm, "radius": 0.5 * mm});
            skCircle(sketch, "E77.6.0", {"center": v(-7.18, 13.06) * mm, "radius": 0.5 * mm});
            skCircle(sketch, "E77.7.0", {"center": v(-8.25, 12.41) * mm, "radius": 0.5 * mm});
            skCircle(sketch, "E77.8.0", {"center": v(-9.26, 11.68) * mm, "radius": 0.5 * mm});
            skCircle(sketch, "E77.9.0", {"center": v(-10.2, 10.86) * mm, "radius": 0.5 * mm});
            skCircle(sketch, "E77.10.0", {"center": v(-11.07, 9.97) * mm, "radius": 0.5 * mm});
            skCircle(sketch, "E77.11.0", {"center": v(-11.87, 9) * mm, "radius": 0.5 * mm});
            skCircle(sketch, "E77.12.0", {"center": v(-12.58, 7.98) * mm, "radius": 0.5 * mm});
            skCircle(sketch, "E77.13.0", {"center": v(-13.2, 6.9) * mm, "radius": 0.5 * mm});
            skCircle(sketch, "E77.14.0", {"center": v(-13.74, 5.77) * mm, "radius": 0.5 * mm});
            skCircle(sketch, "E77.15.0", {"center": v(-14.17, 4.6) * mm, "radius": 0.5 * mm});
            skCircle(sketch, "E77.16.0", {"center": v(-14.5, 3.4) * mm, "radius": 0.5 * mm});
            skCircle(sketch, "E77.17.0", {"center": v(-14.74, 2.18) * mm, "radius": 0.5 * mm});
            skCircle(sketch, "E77.18.0", {"center": v(-14.87, 0.94) * mm, "radius": 0.5 * mm});
            skCircle(sketch, "E77.19.0", {"center": v(-14.9, -0.31) * mm, "radius": 0.5 * mm});
            skCircle(sketch, "E77.20.0", {"center": v(-14.82, -1.56) * mm, "radius": 0.5 * mm});
            skCircle(sketch, "E77.21.0", {"center": v(-14.64, -2.8) * mm, "radius": 0.5 * mm});
            skCircle(sketch, "E77.22.0", {"center": v(-14.35, -4) * mm, "radius": 0.5 * mm});
            skCircle(sketch, "E77.23.0", {"center": v(-13.97, -5.2) * mm, "radius": 0.5 * mm});
            skCircle(sketch, "E77.24.0", {"center": v(-13.48, -6.34) * mm, "radius": 0.5 * mm});
            skCircle(sketch, "E77.25.0", {"center": v(-12.9, -7.45) * mm, "radius": 0.5 * mm});
            skCircle(sketch, "E77.26.0", {"center": v(-12.24, -8.5) * mm, "radius": 0.5 * mm});
            skCircle(sketch, "E77.27.0", {"center": v(-11.48, -9.5) * mm, "radius": 0.5 * mm});
            skCircle(sketch, "E77.28.0", {"center": v(-10.65, -10.42) * mm, "radius": 0.5 * mm});
            skCircle(sketch, "E77.29.0", {"center": v(-9.74, -11.28) * mm, "radius": 0.5 * mm});
            skCircle(sketch, "E77.30.0", {"center": v(-8.76, -12.05) * mm, "radius": 0.5 * mm});
            skCircle(sketch, "E77.31.0", {"center": v(-7.72, -12.74) * mm, "radius": 0.5 * mm});
            skCircle(sketch, "E77.32.0", {"center": v(-6.63, -13.35) * mm, "radius": 0.5 * mm});
            skCircle(sketch, "E77.33.0", {"center": v(-5.49, -13.85) * mm, "radius": 0.5 * mm});
            skCircle(sketch, "E77.34.0", {"center": v(-4.3, -14.26) * mm, "radius": 0.5 * mm});
            skCircle(sketch, "E77.35.0", {"center": v(-3.1, -14.57) * mm, "radius": 0.5 * mm});
            skCircle(sketch, "E77.36.0", {"center": v(-1.87, -14.78) * mm, "radius": 0.5 * mm});
            skCircle(sketch, "E77.37.0", {"center": v(-0.62, -14.89) * mm, "radius": 0.5 * mm});
            skCircle(sketch, "E77.38.0", {"center": v(0.62, -14.89) * mm, "radius": 0.5 * mm});
            skCircle(sketch, "E77.39.0", {"center": v(1.87, -14.78) * mm, "radius": 0.5 * mm});
            skCircle(sketch, "E77.40.0", {"center": v(3.1, -14.57) * mm, "radius": 0.5 * mm});
            skCircle(sketch, "E77.41.0", {"center": v(4.3, -14.26) * mm, "radius": 0.5 * mm});
            skCircle(sketch, "E77.42.0", {"center": v(5.49, -13.85) * mm, "radius": 0.5 * mm});
            skCircle(sketch, "E77.43.0", {"center": v(6.63, -13.35) * mm, "radius": 0.5 * mm});
            skCircle(sketch, "E77.44.0", {"center": v(7.72, -12.74) * mm, "radius": 0.5 * mm});
            skCircle(sketch, "E77.45.0", {"center": v(8.76, -12.05) * mm, "radius": 0.5 * mm});
            skCircle(sketch, "E77.46.0", {"center": v(9.74, -11.28) * mm, "radius": 0.5 * mm});
            skCircle(sketch, "E77.47.0", {"center": v(10.65, -10.42) * mm, "radius": 0.5 * mm});
            skCircle(sketch, "E77.48.0", {"center": v(11.48, -9.5) * mm, "radius": 0.5 * mm});
            skCircle(sketch, "E77.49.0", {"center": v(12.24, -8.5) * mm, "radius": 0.5 * mm});
            skCircle(sketch, "E77.50.0", {"center": v(12.9, -7.45) * mm, "radius": 0.5 * mm});
            skCircle(sketch, "E77.51.0", {"center": v(13.48, -6.34) * mm, "radius": 0.5 * mm});
            skCircle(sketch, "E77.52.0", {"center": v(13.97, -5.2) * mm, "radius": 0.5 * mm});
            skCircle(sketch, "E77.53.0", {"center": v(14.35, -4) * mm, "radius": 0.5 * mm});
            skCircle(sketch, "E77.54.0", {"center": v(14.64, -2.8) * mm, "radius": 0.5 * mm});
            skCircle(sketch, "E77.55.0", {"center": v(14.82, -1.56) * mm, "radius": 0.5 * mm});
            skCircle(sketch, "E77.56.0", {"center": v(14.9, -0.31) * mm, "radius": 0.5 * mm});
            skCircle(sketch, "E77.57.0", {"center": v(14.87, 0.94) * mm, "radius": 0.5 * mm});
            skCircle(sketch, "E77.58.0", {"center": v(14.74, 2.18) * mm, "radius": 0.5 * mm});
            skCircle(sketch, "E77.59.0", {"center": v(14.5, 3.4) * mm, "radius": 0.5 * mm});
            skCircle(sketch, "E77.60.0", {"center": v(14.17, 4.6) * mm, "radius": 0.5 * mm});
            skCircle(sketch, "E77.61.0", {"center": v(13.74, 5.77) * mm, "radius": 0.5 * mm});
            skCircle(sketch, "E77.62.0", {"center": v(13.2, 6.9) * mm, "radius": 0.5 * mm});
            skCircle(sketch, "E77.63.0", {"center": v(12.58, 7.98) * mm, "radius": 0.5 * mm});
            skCircle(sketch, "E77.64.0", {"center": v(11.87, 9) * mm, "radius": 0.5 * mm});
            skCircle(sketch, "E77.65.0", {"center": v(11.07, 9.97) * mm, "radius": 0.5 * mm});
            skCircle(sketch, "E77.66.0", {"center": v(10.2, 10.86) * mm, "radius": 0.5 * mm});
            skCircle(sketch, "E77.67.0", {"center": v(9.26, 11.68) * mm, "radius": 0.5 * mm});
            skCircle(sketch, "E77.68.0", {"center": v(8.25, 12.41) * mm, "radius": 0.5 * mm});
            skCircle(sketch, "E77.69.0", {"center": v(7.18, 13.06) * mm, "radius": 0.5 * mm});
            skCircle(sketch, "E77.70.0", {"center": v(6.06, 13.61) * mm, "radius": 0.5 * mm});
            skCircle(sketch, "E77.71.0", {"center": v(4.9, 14.07) * mm, "radius": 0.5 * mm});
            skCircle(sketch, "E77.72.0", {"center": v(3.7, 14.43) * mm, "radius": 0.5 * mm});
            skCircle(sketch, "E77.73.0", {"center": v(2.48, 14.7) * mm, "radius": 0.5 * mm});
            skCircle(sketch, "E77.74.0", {"center": v(1.25, 14.85) * mm, "radius": 0.5 * mm});
            skCircle(sketch, "E78.1.0", {"center": v(-1.24, 16.15) * mm, "radius": 0.5 * mm});
            skCircle(sketch, "E78.2.0", {"center": v(-2.47, 16.01) * mm, "radius": 0.5 * mm});
            skCircle(sketch, "E78.3.0", {"center": v(-3.7, 15.77) * mm, "radius": 0.5 * mm});
            skCircle(sketch, "E78.4.0", {"center": v(-4.89, 15.45) * mm, "radius": 0.5 * mm});
            skCircle(sketch, "E78.5.0", {"center": v(-6.06, 15.03) * mm, "radius": 0.5 * mm});
            skCircle(sketch, "E78.6.0", {"center": v(-7.19, 14.52) * mm, "radius": 0.5 * mm});
            skCircle(sketch, "E78.7.0", {"center": v(-8.28, 13.93) * mm, "radius": 0.5 * mm});
            skCircle(sketch, "E78.8.0", {"center": v(-9.32, 13.25) * mm, "radius": 0.5 * mm});
            skCircle(sketch, "E78.9.0", {"center": v(-10.3, 12.5) * mm, "radius": 0.5 * mm});
            skCircle(sketch, "E78.10.0", {"center": v(-11.23, 11.67) * mm, "radius": 0.5 * mm});
            skCircle(sketch, "E78.11.0", {"center": v(-12.1, 10.78) * mm, "radius": 0.5 * mm});
            skCircle(sketch, "E78.12.0", {"center": v(-12.88, 9.82) * mm, "radius": 0.5 * mm});
            skCircle(sketch, "E78.13.0", {"center": v(-13.6, 8.8) * mm, "radius": 0.5 * mm});
            skCircle(sketch, "E78.14.0", {"center": v(-14.23, 7.74) * mm, "radius": 0.5 * mm});
            skCircle(sketch, "E78.15.0", {"center": v(-14.78, 6.63) * mm, "radius": 0.5 * mm});
            skCircle(sketch, "E78.16.0", {"center": v(-15.25, 5.48) * mm, "radius": 0.5 * mm});
            skCircle(sketch, "E78.17.0", {"center": v(-15.62, 4.3) * mm, "radius": 0.5 * mm});
            skCircle(sketch, "E78.18.0", {"center": v(-15.9, 3.08) * mm, "radius": 0.5 * mm});
            skCircle(sketch, "E78.19.0", {"center": v(-16.1, 1.86) * mm, "radius": 0.5 * mm});
            skCircle(sketch, "E78.20.0", {"center": v(-16.19, 0.62) * mm, "radius": 0.5 * mm});
            skCircle(sketch, "E78.21.0", {"center": v(-16.19, -0.62) * mm, "radius": 0.5 * mm});
            skCircle(sketch, "E78.22.0", {"center": v(-16.1, -1.86) * mm, "radius": 0.5 * mm});
            skCircle(sketch, "E78.23.0", {"center": v(-15.9, -3.08) * mm, "radius": 0.5 * mm});
            skCircle(sketch, "E78.24.0", {"center": v(-15.62, -4.3) * mm, "radius": 0.5 * mm});
            skCircle(sketch, "E78.25.0", {"center": v(-15.25, -5.48) * mm, "radius": 0.5 * mm});
            skCircle(sketch, "E78.26.0", {"center": v(-14.78, -6.63) * mm, "radius": 0.5 * mm});
            skCircle(sketch, "E78.27.0", {"center": v(-14.23, -7.74) * mm, "radius": 0.5 * mm});
            skCircle(sketch, "E78.28.0", {"center": v(-13.6, -8.8) * mm, "radius": 0.5 * mm});
            skCircle(sketch, "E78.29.0", {"center": v(-12.88, -9.82) * mm, "radius": 0.5 * mm});
            skCircle(sketch, "E78.30.0", {"center": v(-12.1, -10.78) * mm, "radius": 0.5 * mm});
            skCircle(sketch, "E78.31.0", {"center": v(-11.23, -11.67) * mm, "radius": 0.5 * mm});
            skCircle(sketch, "E78.32.0", {"center": v(-10.3, -12.5) * mm, "radius": 0.5 * mm});
            skCircle(sketch, "E78.33.0", {"center": v(-9.32, -13.25) * mm, "radius": 0.5 * mm});
            skCircle(sketch, "E78.34.0", {"center": v(-8.28, -13.93) * mm, "radius": 0.5 * mm});
            skCircle(sketch, "E78.35.0", {"center": v(-7.19, -14.52) * mm, "radius": 0.5 * mm});
            skCircle(sketch, "E78.36.0", {"center": v(-6.06, -15.03) * mm, "radius": 0.5 * mm});
            skCircle(sketch, "E78.37.0", {"center": v(-4.89, -15.45) * mm, "radius": 0.5 * mm});
            skCircle(sketch, "E78.38.0", {"center": v(-3.7, -15.77) * mm, "radius": 0.5 * mm});
            skCircle(sketch, "E78.39.0", {"center": v(-2.47, -16.01) * mm, "radius": 0.5 * mm});
            skCircle(sketch, "E78.40.0", {"center": v(-1.24, -16.15) * mm, "radius": 0.5 * mm});
            skCircle(sketch, "E78.41.0", {"center": v(0, -16.2) * mm, "radius": 0.5 * mm});
            skCircle(sketch, "E78.42.0", {"center": v(1.24, -16.15) * mm, "radius": 0.5 * mm});
            skCircle(sketch, "E78.43.0", {"center": v(2.47, -16.01) * mm, "radius": 0.5 * mm});
            skCircle(sketch, "E78.44.0", {"center": v(3.7, -15.77) * mm, "radius": 0.5 * mm});
            skCircle(sketch, "E78.45.0", {"center": v(4.89, -15.45) * mm, "radius": 0.5 * mm});
            skCircle(sketch, "E78.46.0", {"center": v(6.06, -15.03) * mm, "radius": 0.5 * mm});
            skCircle(sketch, "E78.47.0", {"center": v(7.19, -14.52) * mm, "radius": 0.5 * mm});
            skCircle(sketch, "E78.48.0", {"center": v(8.28, -13.93) * mm, "radius": 0.5 * mm});
            skCircle(sketch, "E78.49.0", {"center": v(9.32, -13.25) * mm, "radius": 0.5 * mm});
            skCircle(sketch, "E78.50.0", {"center": v(10.3, -12.5) * mm, "radius": 0.5 * mm});
            skCircle(sketch, "E78.51.0", {"center": v(11.23, -11.67) * mm, "radius": 0.5 * mm});
            skCircle(sketch, "E78.52.0", {"center": v(12.1, -10.78) * mm, "radius": 0.5 * mm});
            skCircle(sketch, "E78.53.0", {"center": v(12.88, -9.82) * mm, "radius": 0.5 * mm});
            skCircle(sketch, "E78.54.0", {"center": v(13.6, -8.8) * mm, "radius": 0.5 * mm});
            skCircle(sketch, "E78.55.0", {"center": v(14.23, -7.74) * mm, "radius": 0.5 * mm});
            skCircle(sketch, "E78.56.0", {"center": v(14.78, -6.63) * mm, "radius": 0.5 * mm});
            skCircle(sketch, "E78.57.0", {"center": v(15.25, -5.48) * mm, "radius": 0.5 * mm});
            skCircle(sketch, "E78.58.0", {"center": v(15.62, -4.3) * mm, "radius": 0.5 * mm});
            skCircle(sketch, "E78.59.0", {"center": v(15.9, -3.08) * mm, "radius": 0.5 * mm});
            skCircle(sketch, "E78.60.0", {"center": v(16.1, -1.86) * mm, "radius": 0.5 * mm});
            skCircle(sketch, "E78.61.0", {"center": v(16.19, -0.62) * mm, "radius": 0.5 * mm});
            skCircle(sketch, "E78.62.0", {"center": v(16.19, 0.62) * mm, "radius": 0.5 * mm});
            skCircle(sketch, "E78.63.0", {"center": v(16.1, 1.86) * mm, "radius": 0.5 * mm});
            skCircle(sketch, "E78.64.0", {"center": v(15.9, 3.08) * mm, "radius": 0.5 * mm});
            skCircle(sketch, "E78.65.0", {"center": v(15.62, 4.3) * mm, "radius": 0.5 * mm});
            skCircle(sketch, "E78.66.0", {"center": v(15.25, 5.48) * mm, "radius": 0.5 * mm});
            skCircle(sketch, "E78.67.0", {"center": v(14.78, 6.63) * mm, "radius": 0.5 * mm});
            skCircle(sketch, "E78.68.0", {"center": v(14.23, 7.74) * mm, "radius": 0.5 * mm});
            skCircle(sketch, "E78.69.0", {"center": v(13.6, 8.8) * mm, "radius": 0.5 * mm});
            skCircle(sketch, "E78.70.0", {"center": v(12.88, 9.82) * mm, "radius": 0.5 * mm});
            skCircle(sketch, "E78.71.0", {"center": v(12.1, 10.78) * mm, "radius": 0.5 * mm});
            skCircle(sketch, "E78.72.0", {"center": v(11.23, 11.67) * mm, "radius": 0.5 * mm});
            skCircle(sketch, "E78.73.0", {"center": v(10.3, 12.5) * mm, "radius": 0.5 * mm});
            skCircle(sketch, "E78.74.0", {"center": v(9.32, 13.25) * mm, "radius": 0.5 * mm});
            skCircle(sketch, "E78.75.0", {"center": v(8.28, 13.93) * mm, "radius": 0.5 * mm});
            skCircle(sketch, "E78.76.0", {"center": v(7.19, 14.52) * mm, "radius": 0.5 * mm});
            skCircle(sketch, "E78.77.0", {"center": v(6.06, 15.03) * mm, "radius": 0.5 * mm});
            skCircle(sketch, "E78.78.0", {"center": v(4.89, 15.45) * mm, "radius": 0.5 * mm});
            skCircle(sketch, "E78.79.0", {"center": v(3.7, 15.77) * mm, "radius": 0.5 * mm});
            skCircle(sketch, "E78.80.0", {"center": v(2.47, 16.01) * mm, "radius": 0.5 * mm});
            skCircle(sketch, "E78.81.0", {"center": v(1.24, 16.15) * mm, "radius": 0.5 * mm});
            skCircle(sketch, "E79.1.0", {"center": v(-1.23, 17.46) * mm, "radius": 0.5 * mm});
            skCircle(sketch, "E79.2.0", {"center": v(-2.46, 17.33) * mm, "radius": 0.5 * mm});
            skCircle(sketch, "E79.3.0", {"center": v(-3.68, 17.1) * mm, "radius": 0.5 * mm});
            skCircle(sketch, "E79.4.0", {"center": v(-4.88, 16.8) * mm, "radius": 0.5 * mm});
            skCircle(sketch, "E79.5.0", {"center": v(-6.05, 16.42) * mm, "radius": 0.5 * mm});
            skCircle(sketch, "E79.6.0", {"center": v(-7.2, 15.95) * mm, "radius": 0.5 * mm});
            skCircle(sketch, "E79.7.0", {"center": v(-8.3, 15.4) * mm, "radius": 0.5 * mm});
            skCircle(sketch, "E79.8.0", {"center": v(-9.37, 14.78) * mm, "radius": 0.5 * mm});
            skCircle(sketch, "E79.9.0", {"center": v(-10.39, 14.08) * mm, "radius": 0.5 * mm});
            skCircle(sketch, "E79.10.0", {"center": v(-11.35, 13.32) * mm, "radius": 0.5 * mm});
            skCircle(sketch, "E79.11.0", {"center": v(-12.26, 12.48) * mm, "radius": 0.5 * mm});
            skCircle(sketch, "E79.12.0", {"center": v(-13.11, 11.59) * mm, "radius": 0.5 * mm});
            skCircle(sketch, "E79.13.0", {"center": v(-13.9, 10.63) * mm, "radius": 0.5 * mm});
            skCircle(sketch, "E79.14.0", {"center": v(-14.61, 9.63) * mm, "radius": 0.5 * mm});
            skCircle(sketch, "E79.15.0", {"center": v(-15.26, 8.57) * mm, "radius": 0.5 * mm});
            skCircle(sketch, "E79.16.0", {"center": v(-15.82, 7.47) * mm, "radius": 0.5 * mm});
            skCircle(sketch, "E79.17.0", {"center": v(-16.31, 6.34) * mm, "radius": 0.5 * mm});
            skCircle(sketch, "E79.18.0", {"center": v(-16.72, 5.17) * mm, "radius": 0.5 * mm});
            skCircle(sketch, "E79.19.0", {"center": v(-17.04, 3.98) * mm, "radius": 0.5 * mm});
            skCircle(sketch, "E79.20.0", {"center": v(-17.28, 2.77) * mm, "radius": 0.5 * mm});
            skCircle(sketch, "E79.21.0", {"center": v(-17.43, 1.54) * mm, "radius": 0.5 * mm});
            skCircle(sketch, "E79.22.0", {"center": v(-17.5, 0.3) * mm, "radius": 0.5 * mm});
            skCircle(sketch, "E79.23.0", {"center": v(-17.48, -0.93) * mm, "radius": 0.5 * mm});
            skCircle(sketch, "E79.24.0", {"center": v(-17.37, -2.16) * mm, "radius": 0.5 * mm});
            skCircle(sketch, "E79.25.0", {"center": v(-17.17, -3.38) * mm, "radius": 0.5 * mm});
            skCircle(sketch, "E79.26.0", {"center": v(-16.9, -4.58) * mm, "radius": 0.5 * mm});
            skCircle(sketch, "E79.27.0", {"center": v(-16.53, -5.76) * mm, "radius": 0.5 * mm});
            skCircle(sketch, "E79.28.0", {"center": v(-16.08, -6.91) * mm, "radius": 0.5 * mm});
            skCircle(sketch, "E79.29.0", {"center": v(-15.55, -8.03) * mm, "radius": 0.5 * mm});
            skCircle(sketch, "E79.30.0", {"center": v(-14.95, -9.1) * mm, "radius": 0.5 * mm});
            skCircle(sketch, "E79.31.0", {"center": v(-14.27, -10.14) * mm, "radius": 0.5 * mm});
            skCircle(sketch, "E79.32.0", {"center": v(-13.52, -11.12) * mm, "radius": 0.5 * mm});
            skCircle(sketch, "E79.33.0", {"center": v(-12.7, -12.04) * mm, "radius": 0.5 * mm});
            skCircle(sketch, "E79.34.0", {"center": v(-11.82, -12.9) * mm, "radius": 0.5 * mm});
            skCircle(sketch, "E79.35.0", {"center": v(-10.88, -13.7) * mm, "radius": 0.5 * mm});
            skCircle(sketch, "E79.36.0", {"center": v(-9.88, -14.44) * mm, "radius": 0.5 * mm});
            skCircle(sketch, "E79.37.0", {"center": v(-8.84, -15.1) * mm, "radius": 0.5 * mm});
            skCircle(sketch, "E79.38.0", {"center": v(-7.75, -15.69) * mm, "radius": 0.5 * mm});
            skCircle(sketch, "E79.39.0", {"center": v(-6.63, -16.2) * mm, "radius": 0.5 * mm});
            skCircle(sketch, "E79.40.0", {"center": v(-5.47, -16.62) * mm, "radius": 0.5 * mm});
            skCircle(sketch, "E79.41.0", {"center": v(-4.28, -16.97) * mm, "radius": 0.5 * mm});
            skCircle(sketch, "E79.42.0", {"center": v(-3.07, -17.23) * mm, "radius": 0.5 * mm});
            skCircle(sketch, "E79.43.0", {"center": v(-1.85, -17.4) * mm, "radius": 0.5 * mm});
            skCircle(sketch, "E79.44.0", {"center": v(-0.62, -17.49) * mm, "radius": 0.5 * mm});
            skCircle(sketch, "E79.45.0", {"center": v(0.62, -17.49) * mm, "radius": 0.5 * mm});
            skCircle(sketch, "E79.46.0", {"center": v(1.85, -17.4) * mm, "radius": 0.5 * mm});
            skCircle(sketch, "E79.47.0", {"center": v(3.07, -17.23) * mm, "radius": 0.5 * mm});
            skCircle(sketch, "E79.48.0", {"center": v(4.28, -16.97) * mm, "radius": 0.5 * mm});
            skCircle(sketch, "E79.49.0", {"center": v(5.47, -16.62) * mm, "radius": 0.5 * mm});
            skCircle(sketch, "E79.50.0", {"center": v(6.63, -16.2) * mm, "radius": 0.5 * mm});
            skCircle(sketch, "E79.51.0", {"center": v(7.75, -15.69) * mm, "radius": 0.5 * mm});
            skCircle(sketch, "E79.52.0", {"center": v(8.84, -15.1) * mm, "radius": 0.5 * mm});
            skCircle(sketch, "E79.53.0", {"center": v(9.88, -14.44) * mm, "radius": 0.5 * mm});
            skCircle(sketch, "E79.54.0", {"center": v(10.88, -13.7) * mm, "radius": 0.5 * mm});
            skCircle(sketch, "E79.55.0", {"center": v(11.82, -12.9) * mm, "radius": 0.5 * mm});
            skCircle(sketch, "E79.56.0", {"center": v(12.7, -12.04) * mm, "radius": 0.5 * mm});
            skCircle(sketch, "E79.57.0", {"center": v(13.52, -11.12) * mm, "radius": 0.5 * mm});
            skCircle(sketch, "E79.58.0", {"center": v(14.27, -10.14) * mm, "radius": 0.5 * mm});
            skCircle(sketch, "E79.59.0", {"center": v(14.95, -9.1) * mm, "radius": 0.5 * mm});
            skCircle(sketch, "E79.60.0", {"center": v(15.55, -8.03) * mm, "radius": 0.5 * mm});
            skCircle(sketch, "E79.61.0", {"center": v(16.08, -6.91) * mm, "radius": 0.5 * mm});
            skCircle(sketch, "E79.62.0", {"center": v(16.53, -5.76) * mm, "radius": 0.5 * mm});
            skCircle(sketch, "E79.63.0", {"center": v(16.9, -4.58) * mm, "radius": 0.5 * mm});
            skCircle(sketch, "E79.64.0", {"center": v(17.17, -3.38) * mm, "radius": 0.5 * mm});
            skCircle(sketch, "E79.65.0", {"center": v(17.37, -2.16) * mm, "radius": 0.5 * mm});
            skCircle(sketch, "E79.66.0", {"center": v(17.48, -0.93) * mm, "radius": 0.5 * mm});
            skCircle(sketch, "E79.67.0", {"center": v(17.5, 0.3) * mm, "radius": 0.5 * mm});
            skCircle(sketch, "E79.68.0", {"center": v(17.43, 1.54) * mm, "radius": 0.5 * mm});
            skCircle(sketch, "E79.69.0", {"center": v(17.28, 2.77) * mm, "radius": 0.5 * mm});
            skCircle(sketch, "E79.70.0", {"center": v(17.04, 3.98) * mm, "radius": 0.5 * mm});
            skCircle(sketch, "E79.71.0", {"center": v(16.72, 5.17) * mm, "radius": 0.5 * mm});
            skCircle(sketch, "E79.72.0", {"center": v(16.31, 6.34) * mm, "radius": 0.5 * mm});
            skCircle(sketch, "E79.73.0", {"center": v(15.82, 7.47) * mm, "radius": 0.5 * mm});
            skCircle(sketch, "E79.74.0", {"center": v(15.26, 8.57) * mm, "radius": 0.5 * mm});
            skCircle(sketch, "E79.75.0", {"center": v(14.61, 9.63) * mm, "radius": 0.5 * mm});
            skCircle(sketch, "E79.76.0", {"center": v(13.9, 10.63) * mm, "radius": 0.5 * mm});
            skCircle(sketch, "E79.77.0", {"center": v(13.11, 11.59) * mm, "radius": 0.5 * mm});
            skCircle(sketch, "E79.78.0", {"center": v(12.26, 12.48) * mm, "radius": 0.5 * mm});
            skCircle(sketch, "E79.79.0", {"center": v(11.35, 13.32) * mm, "radius": 0.5 * mm});
            skCircle(sketch, "E79.80.0", {"center": v(10.39, 14.08) * mm, "radius": 0.5 * mm});
            skCircle(sketch, "E79.81.0", {"center": v(9.37, 14.78) * mm, "radius": 0.5 * mm});
            skCircle(sketch, "E79.82.0", {"center": v(8.3, 15.4) * mm, "radius": 0.5 * mm});
            skCircle(sketch, "E79.83.0", {"center": v(7.2, 15.95) * mm, "radius": 0.5 * mm});
            skCircle(sketch, "E79.84.0", {"center": v(6.05, 16.42) * mm, "radius": 0.5 * mm});
            skCircle(sketch, "E79.85.0", {"center": v(4.88, 16.8) * mm, "radius": 0.5 * mm});
            skCircle(sketch, "E79.86.0", {"center": v(3.68, 17.1) * mm, "radius": 0.5 * mm});
            skCircle(sketch, "E79.87.0", {"center": v(2.46, 17.33) * mm, "radius": 0.5 * mm});
            skCircle(sketch, "E79.88.0", {"center": v(1.23, 17.46) * mm, "radius": 0.5 * mm});
            skCircle(sketch, "E80.1.0", {"center": v(-1.23, 18.76) * mm, "radius": 0.5 * mm});
            skCircle(sketch, "E80.2.0", {"center": v(-2.45, 18.64) * mm, "radius": 0.5 * mm});
            skCircle(sketch, "E80.3.0", {"center": v(-3.67, 18.44) * mm, "radius": 0.5 * mm});
            skCircle(sketch, "E80.4.0", {"center": v(-4.87, 18.16) * mm, "radius": 0.5 * mm});
            skCircle(sketch, "E80.5.0", {"center": v(-6.04, 17.8) * mm, "radius": 0.5 * mm});
            skCircle(sketch, "E80.6.0", {"center": v(-7.2, 17.37) * mm, "radius": 0.5 * mm});
            skCircle(sketch, "E80.7.0", {"center": v(-8.32, 16.86) * mm, "radius": 0.5 * mm});
            skCircle(sketch, "E80.8.0", {"center": v(-9.4, 16.28) * mm, "radius": 0.5 * mm});
            skCircle(sketch, "E80.9.0", {"center": v(-10.44, 15.63) * mm, "radius": 0.5 * mm});
            skCircle(sketch, "E80.10.0", {"center": v(-11.44, 14.92) * mm, "radius": 0.5 * mm});
            skCircle(sketch, "E80.11.0", {"center": v(-12.4, 14.13) * mm, "radius": 0.5 * mm});
            skCircle(sketch, "E80.12.0", {"center": v(-13.3, 13.3) * mm, "radius": 0.5 * mm});
            skCircle(sketch, "E80.13.0", {"center": v(-14.13, 12.4) * mm, "radius": 0.5 * mm});
            skCircle(sketch, "E80.14.0", {"center": v(-14.92, 11.44) * mm, "radius": 0.5 * mm});
            skCircle(sketch, "E80.15.0", {"center": v(-15.63, 10.44) * mm, "radius": 0.5 * mm});
            skCircle(sketch, "E80.16.0", {"center": v(-16.28, 9.4) * mm, "radius": 0.5 * mm});
            skCircle(sketch, "E80.17.0", {"center": v(-16.86, 8.32) * mm, "radius": 0.5 * mm});
            skCircle(sketch, "E80.18.0", {"center": v(-17.37, 7.2) * mm, "radius": 0.5 * mm});
            skCircle(sketch, "E80.19.0", {"center": v(-17.8, 6.04) * mm, "radius": 0.5 * mm});
            skCircle(sketch, "E80.20.0", {"center": v(-18.16, 4.87) * mm, "radius": 0.5 * mm});
            skCircle(sketch, "E80.21.0", {"center": v(-18.44, 3.67) * mm, "radius": 0.5 * mm});
            skCircle(sketch, "E80.22.0", {"center": v(-18.64, 2.45) * mm, "radius": 0.5 * mm});
            skCircle(sketch, "E80.23.0", {"center": v(-18.76, 1.23) * mm, "radius": 0.5 * mm});
            skCircle(sketch, "E80.24.0", {"center": v(-18.8, 0) * mm, "radius": 0.5 * mm});
            skCircle(sketch, "E80.25.0", {"center": v(-18.76, -1.23) * mm, "radius": 0.5 * mm});
            skCircle(sketch, "E80.26.0", {"center": v(-18.64, -2.45) * mm, "radius": 0.5 * mm});
            skCircle(sketch, "E80.27.0", {"center": v(-18.44, -3.67) * mm, "radius": 0.5 * mm});
            skCircle(sketch, "E80.28.0", {"center": v(-18.16, -4.87) * mm, "radius": 0.5 * mm});
            skCircle(sketch, "E80.29.0", {"center": v(-17.8, -6.04) * mm, "radius": 0.5 * mm});
            skCircle(sketch, "E80.30.0", {"center": v(-17.37, -7.2) * mm, "radius": 0.5 * mm});
            skCircle(sketch, "E80.31.0", {"center": v(-16.86, -8.32) * mm, "radius": 0.5 * mm});
            skCircle(sketch, "E80.32.0", {"center": v(-16.28, -9.4) * mm, "radius": 0.5 * mm});
            skCircle(sketch, "E80.33.0", {"center": v(-15.63, -10.44) * mm, "radius": 0.5 * mm});
            skCircle(sketch, "E80.34.0", {"center": v(-14.92, -11.44) * mm, "radius": 0.5 * mm});
            skCircle(sketch, "E80.35.0", {"center": v(-14.13, -12.4) * mm, "radius": 0.5 * mm});
            skCircle(sketch, "E80.36.0", {"center": v(-13.3, -13.3) * mm, "radius": 0.5 * mm});
            skCircle(sketch, "E80.37.0", {"center": v(-12.4, -14.13) * mm, "radius": 0.5 * mm});
            skCircle(sketch, "E80.38.0", {"center": v(-11.44, -14.92) * mm, "radius": 0.5 * mm});
            skCircle(sketch, "E80.39.0", {"center": v(-10.44, -15.63) * mm, "radius": 0.5 * mm});
            skCircle(sketch, "E80.40.0", {"center": v(-9.4, -16.28) * mm, "radius": 0.5 * mm});
            skCircle(sketch, "E80.41.0", {"center": v(-8.32, -16.86) * mm, "radius": 0.5 * mm});
            skCircle(sketch, "E80.42.0", {"center": v(-7.2, -17.37) * mm, "radius": 0.5 * mm});
            skCircle(sketch, "E80.43.0", {"center": v(-6.04, -17.8) * mm, "radius": 0.5 * mm});
            skCircle(sketch, "E80.44.0", {"center": v(-4.87, -18.16) * mm, "radius": 0.5 * mm});
            skCircle(sketch, "E80.45.0", {"center": v(-3.67, -18.44) * mm, "radius": 0.5 * mm});
            skCircle(sketch, "E80.46.0", {"center": v(-2.45, -18.64) * mm, "radius": 0.5 * mm});
            skCircle(sketch, "E80.47.0", {"center": v(-1.23, -18.76) * mm, "radius": 0.5 * mm});
            skCircle(sketch, "E80.48.0", {"center": v(0, -18.8) * mm, "radius": 0.5 * mm});
            skCircle(sketch, "E80.49.0", {"center": v(1.23, -18.76) * mm, "radius": 0.5 * mm});
            skCircle(sketch, "E80.50.0", {"center": v(2.45, -18.64) * mm, "radius": 0.5 * mm});
            skCircle(sketch, "E80.51.0", {"center": v(3.67, -18.44) * mm, "radius": 0.5 * mm});
            skCircle(sketch, "E80.52.0", {"center": v(4.87, -18.16) * mm, "radius": 0.5 * mm});
            skCircle(sketch, "E80.53.0", {"center": v(6.04, -17.8) * mm, "radius": 0.5 * mm});
            skCircle(sketch, "E80.54.0", {"center": v(7.2, -17.37) * mm, "radius": 0.5 * mm});
            skCircle(sketch, "E80.55.0", {"center": v(8.32, -16.86) * mm, "radius": 0.5 * mm});
            skCircle(sketch, "E80.56.0", {"center": v(9.4, -16.28) * mm, "radius": 0.5 * mm});
            skCircle(sketch, "E80.57.0", {"center": v(10.44, -15.63) * mm, "radius": 0.5 * mm});
            skCircle(sketch, "E80.58.0", {"center": v(11.44, -14.92) * mm, "radius": 0.5 * mm});
            skCircle(sketch, "E80.59.0", {"center": v(12.4, -14.13) * mm, "radius": 0.5 * mm});
            skCircle(sketch, "E80.60.0", {"center": v(13.3, -13.3) * mm, "radius": 0.5 * mm});
            skCircle(sketch, "E80.61.0", {"center": v(14.13, -12.4) * mm, "radius": 0.5 * mm});
            skCircle(sketch, "E80.62.0", {"center": v(14.92, -11.44) * mm, "radius": 0.5 * mm});
            skCircle(sketch, "E80.63.0", {"center": v(15.63, -10.44) * mm, "radius": 0.5 * mm});
            skCircle(sketch, "E80.64.0", {"center": v(16.28, -9.4) * mm, "radius": 0.5 * mm});
            skCircle(sketch, "E80.65.0", {"center": v(16.86, -8.32) * mm, "radius": 0.5 * mm});
            skCircle(sketch, "E80.66.0", {"center": v(17.37, -7.2) * mm, "radius": 0.5 * mm});
            skCircle(sketch, "E80.67.0", {"center": v(17.8, -6.04) * mm, "radius": 0.5 * mm});
            skCircle(sketch, "E80.68.0", {"center": v(18.16, -4.87) * mm, "radius": 0.5 * mm});
            skCircle(sketch, "E80.69.0", {"center": v(18.44, -3.67) * mm, "radius": 0.5 * mm});
            skCircle(sketch, "E80.70.0", {"center": v(18.64, -2.45) * mm, "radius": 0.5 * mm});
            skCircle(sketch, "E80.71.0", {"center": v(18.76, -1.23) * mm, "radius": 0.5 * mm});
            skCircle(sketch, "E80.72.0", {"center": v(18.8, 0) * mm, "radius": 0.5 * mm});
            skCircle(sketch, "E80.73.0", {"center": v(18.76, 1.23) * mm, "radius": 0.5 * mm});
            skCircle(sketch, "E80.74.0", {"center": v(18.64, 2.45) * mm, "radius": 0.5 * mm});
            skCircle(sketch, "E80.75.0", {"center": v(18.44, 3.67) * mm, "radius": 0.5 * mm});
            skCircle(sketch, "E80.76.0", {"center": v(18.16, 4.87) * mm, "radius": 0.5 * mm});
            skCircle(sketch, "E80.77.0", {"center": v(17.8, 6.04) * mm, "radius": 0.5 * mm});
            skCircle(sketch, "E80.78.0", {"center": v(17.37, 7.2) * mm, "radius": 0.5 * mm});
            skCircle(sketch, "E80.79.0", {"center": v(16.86, 8.32) * mm, "radius": 0.5 * mm});
            skCircle(sketch, "E80.80.0", {"center": v(16.28, 9.4) * mm, "radius": 0.5 * mm});
            skCircle(sketch, "E80.81.0", {"center": v(15.63, 10.44) * mm, "radius": 0.5 * mm});
            skCircle(sketch, "E80.82.0", {"center": v(14.92, 11.44) * mm, "radius": 0.5 * mm});
            skCircle(sketch, "E80.83.0", {"center": v(14.13, 12.4) * mm, "radius": 0.5 * mm});
            skCircle(sketch, "E80.84.0", {"center": v(13.3, 13.3) * mm, "radius": 0.5 * mm});
            skCircle(sketch, "E80.85.0", {"center": v(12.4, 14.13) * mm, "radius": 0.5 * mm});
            skCircle(sketch, "E80.86.0", {"center": v(11.44, 14.92) * mm, "radius": 0.5 * mm});
            skCircle(sketch, "E80.87.0", {"center": v(10.44, 15.63) * mm, "radius": 0.5 * mm});
            skCircle(sketch, "E80.88.0", {"center": v(9.4, 16.28) * mm, "radius": 0.5 * mm});
            skCircle(sketch, "E80.89.0", {"center": v(8.32, 16.86) * mm, "radius": 0.5 * mm});
            skCircle(sketch, "E80.90.0", {"center": v(7.2, 17.37) * mm, "radius": 0.5 * mm});
            skCircle(sketch, "E80.91.0", {"center": v(6.04, 17.8) * mm, "radius": 0.5 * mm});
            skCircle(sketch, "E80.92.0", {"center": v(4.87, 18.16) * mm, "radius": 0.5 * mm});
            skCircle(sketch, "E80.93.0", {"center": v(3.67, 18.44) * mm, "radius": 0.5 * mm});
            skCircle(sketch, "E80.94.0", {"center": v(2.45, 18.64) * mm, "radius": 0.5 * mm});
            skCircle(sketch, "E80.95.0", {"center": v(1.23, 18.76) * mm, "radius": 0.5 * mm});
            skCircle(sketch, "E81.1.0", {"center": v(-1.23, 20.06) * mm, "radius": 0.5 * mm});
            skCircle(sketch, "E81.2.0", {"center": v(-2.45, 19.95) * mm, "radius": 0.5 * mm});
            skCircle(sketch, "E81.3.0", {"center": v(-3.66, 19.76) * mm, "radius": 0.5 * mm});
            skCircle(sketch, "E81.4.0", {"center": v(-4.86, 19.5) * mm, "radius": 0.5 * mm});
            skCircle(sketch, "E81.5.0", {"center": v(-6.04, 19.17) * mm, "radius": 0.5 * mm});
            skCircle(sketch, "E81.6.0", {"center": v(-7.2, 18.77) * mm, "radius": 0.5 * mm});
            skCircle(sketch, "E81.7.0", {"center": v(-8.32, 18.3) * mm, "radius": 0.5 * mm});
            skCircle(sketch, "E81.8.0", {"center": v(-9.42, 17.75) * mm, "radius": 0.5 * mm});
            skCircle(sketch, "E81.9.0", {"center": v(-10.49, 17.15) * mm, "radius": 0.5 * mm});
            skCircle(sketch, "E81.10.0", {"center": v(-11.51, 16.47) * mm, "radius": 0.5 * mm});
            skCircle(sketch, "E81.11.0", {"center": v(-12.5, 15.74) * mm, "radius": 0.5 * mm});
            skCircle(sketch, "E81.12.0", {"center": v(-13.43, 14.95) * mm, "radius": 0.5 * mm});
            skCircle(sketch, "E81.13.0", {"center": v(-14.32, 14.1) * mm, "radius": 0.5 * mm});
            skCircle(sketch, "E81.14.0", {"center": v(-15.15, 13.2) * mm, "radius": 0.5 * mm});
            skCircle(sketch, "E81.15.0", {"center": v(-15.93, 12.26) * mm, "radius": 0.5 * mm});
            skCircle(sketch, "E81.16.0", {"center": v(-16.65, 11.26) * mm, "radius": 0.5 * mm});
            skCircle(sketch, "E81.17.0", {"center": v(-17.3, 10.23) * mm, "radius": 0.5 * mm});
            skCircle(sketch, "E81.18.0", {"center": v(-17.9, 9.15) * mm, "radius": 0.5 * mm});
            skCircle(sketch, "E81.19.0", {"center": v(-18.42, 8.04) * mm, "radius": 0.5 * mm});
            skCircle(sketch, "E81.20.0", {"center": v(-18.88, 6.9) * mm, "radius": 0.5 * mm});
            skCircle(sketch, "E81.21.0", {"center": v(-19.26, 5.74) * mm, "radius": 0.5 * mm});
            skCircle(sketch, "E81.22.0", {"center": v(-19.58, 4.56) * mm, "radius": 0.5 * mm});
            skCircle(sketch, "E81.23.0", {"center": v(-19.82, 3.36) * mm, "radius": 0.5 * mm});
            skCircle(sketch, "E81.24.0", {"center": v(-19.99, 2.14) * mm, "radius": 0.5 * mm});
            skCircle(sketch, "E81.25.0", {"center": v(-20.08, 0.92) * mm, "radius": 0.5 * mm});
            skCircle(sketch, "E81.26.0", {"center": v(-20.1, -0.3) * mm, "radius": 0.5 * mm});
            skCircle(sketch, "E81.27.0", {"center": v(-20.04, -1.53) * mm, "radius": 0.5 * mm});
            skCircle(sketch, "E81.28.0", {"center": v(-19.91, -2.75) * mm, "radius": 0.5 * mm});
            skCircle(sketch, "E81.29.0", {"center": v(-19.7, -3.96) * mm, "radius": 0.5 * mm});
            skCircle(sketch, "E81.30.0", {"center": v(-19.43, -5.15) * mm, "radius": 0.5 * mm});
            skCircle(sketch, "E81.31.0", {"center": v(-19.08, -6.33) * mm, "radius": 0.5 * mm});
            skCircle(sketch, "E81.32.0", {"center": v(-18.66, -7.48) * mm, "radius": 0.5 * mm});
            skCircle(sketch, "E81.33.0", {"center": v(-18.17, -8.6) * mm, "radius": 0.5 * mm});
            skCircle(sketch, "E81.34.0", {"center": v(-17.6, -9.7) * mm, "radius": 0.5 * mm});
            skCircle(sketch, "E81.35.0", {"center": v(-16.98, -10.75) * mm, "radius": 0.5 * mm});
            skCircle(sketch, "E81.36.0", {"center": v(-16.3, -11.76) * mm, "radius": 0.5 * mm});
            skCircle(sketch, "E81.37.0", {"center": v(-15.55, -12.74) * mm, "radius": 0.5 * mm});
            skCircle(sketch, "E81.38.0", {"center": v(-14.74, -13.66) * mm, "radius": 0.5 * mm});
            skCircle(sketch, "E81.39.0", {"center": v(-13.88, -14.53) * mm, "radius": 0.5 * mm});
            skCircle(sketch, "E81.40.0", {"center": v(-12.97, -15.35) * mm, "radius": 0.5 * mm});
            skCircle(sketch, "E81.41.0", {"center": v(-12.01, -16.12) * mm, "radius": 0.5 * mm});
            skCircle(sketch, "E81.42.0", {"center": v(-11, -16.82) * mm, "radius": 0.5 * mm});
            skCircle(sketch, "E81.43.0", {"center": v(-9.96, -17.46) * mm, "radius": 0.5 * mm});
            skCircle(sketch, "E81.44.0", {"center": v(-8.88, -18.03) * mm, "radius": 0.5 * mm});
            skCircle(sketch, "E81.45.0", {"center": v(-7.76, -18.54) * mm, "radius": 0.5 * mm});
            skCircle(sketch, "E81.46.0", {"center": v(-6.62, -18.98) * mm, "radius": 0.5 * mm});
            skCircle(sketch, "E81.47.0", {"center": v(-5.45, -19.35) * mm, "radius": 0.5 * mm});
            skCircle(sketch, "E81.48.0", {"center": v(-4.26, -19.64) * mm, "radius": 0.5 * mm});
            skCircle(sketch, "E81.49.0", {"center": v(-3.05, -19.87) * mm, "radius": 0.5 * mm});
            skCircle(sketch, "E81.50.0", {"center": v(-1.84, -20.02) * mm, "radius": 0.5 * mm});
            skCircle(sketch, "E81.51.0", {"center": v(-0.61, -20.1) * mm, "radius": 0.5 * mm});
            skCircle(sketch, "E81.52.0", {"center": v(0.61, -20.1) * mm, "radius": 0.5 * mm});
            skCircle(sketch, "E81.53.0", {"center": v(1.84, -20.02) * mm, "radius": 0.5 * mm});
            skCircle(sketch, "E81.54.0", {"center": v(3.05, -19.87) * mm, "radius": 0.5 * mm});
            skCircle(sketch, "E81.55.0", {"center": v(4.26, -19.64) * mm, "radius": 0.5 * mm});
            skCircle(sketch, "E81.56.0", {"center": v(5.45, -19.35) * mm, "radius": 0.5 * mm});
            skCircle(sketch, "E81.57.0", {"center": v(6.62, -18.98) * mm, "radius": 0.5 * mm});
            skCircle(sketch, "E81.58.0", {"center": v(7.76, -18.54) * mm, "radius": 0.5 * mm});
            skCircle(sketch, "E81.59.0", {"center": v(8.88, -18.03) * mm, "radius": 0.5 * mm});
            skCircle(sketch, "E81.60.0", {"center": v(9.96, -17.46) * mm, "radius": 0.5 * mm});
            skCircle(sketch, "E81.61.0", {"center": v(11, -16.82) * mm, "radius": 0.5 * mm});
            skCircle(sketch, "E81.62.0", {"center": v(12.01, -16.12) * mm, "radius": 0.5 * mm});
            skCircle(sketch, "E81.63.0", {"center": v(12.97, -15.35) * mm, "radius": 0.5 * mm});
            skCircle(sketch, "E81.64.0", {"center": v(13.88, -14.53) * mm, "radius": 0.5 * mm});
            skCircle(sketch, "E81.65.0", {"center": v(14.74, -13.66) * mm, "radius": 0.5 * mm});
            skCircle(sketch, "E81.66.0", {"center": v(15.55, -12.74) * mm, "radius": 0.5 * mm});
            skCircle(sketch, "E81.67.0", {"center": v(16.3, -11.76) * mm, "radius": 0.5 * mm});
            skCircle(sketch, "E81.68.0", {"center": v(16.98, -10.75) * mm, "radius": 0.5 * mm});
            skCircle(sketch, "E81.69.0", {"center": v(17.6, -9.7) * mm, "radius": 0.5 * mm});
            skCircle(sketch, "E81.70.0", {"center": v(18.17, -8.6) * mm, "radius": 0.5 * mm});
            skCircle(sketch, "E81.71.0", {"center": v(18.66, -7.48) * mm, "radius": 0.5 * mm});
            skCircle(sketch, "E81.72.0", {"center": v(19.08, -6.33) * mm, "radius": 0.5 * mm});
            skCircle(sketch, "E81.73.0", {"center": v(19.43, -5.15) * mm, "radius": 0.5 * mm});
            skCircle(sketch, "E81.74.0", {"center": v(19.7, -3.96) * mm, "radius": 0.5 * mm});
            skCircle(sketch, "E81.75.0", {"center": v(19.91, -2.75) * mm, "radius": 0.5 * mm});
            skCircle(sketch, "E81.76.0", {"center": v(20.04, -1.53) * mm, "radius": 0.5 * mm});
            skCircle(sketch, "E81.77.0", {"center": v(20.1, -0.3) * mm, "radius": 0.5 * mm});
            skCircle(sketch, "E81.78.0", {"center": v(20.08, 0.92) * mm, "radius": 0.5 * mm});
            skCircle(sketch, "E81.79.0", {"center": v(19.99, 2.14) * mm, "radius": 0.5 * mm});
            skCircle(sketch, "E81.80.0", {"center": v(19.82, 3.36) * mm, "radius": 0.5 * mm});
            skCircle(sketch, "E81.81.0", {"center": v(19.58, 4.56) * mm, "radius": 0.5 * mm});
            skCircle(sketch, "E81.82.0", {"center": v(19.26, 5.74) * mm, "radius": 0.5 * mm});
            skCircle(sketch, "E81.83.0", {"center": v(18.88, 6.9) * mm, "radius": 0.5 * mm});
            skCircle(sketch, "E81.84.0", {"center": v(18.42, 8.04) * mm, "radius": 0.5 * mm});
            skCircle(sketch, "E81.85.0", {"center": v(17.9, 9.15) * mm, "radius": 0.5 * mm});
            skCircle(sketch, "E81.86.0", {"center": v(17.3, 10.23) * mm, "radius": 0.5 * mm});
            skCircle(sketch, "E81.87.0", {"center": v(16.65, 11.26) * mm, "radius": 0.5 * mm});
            skCircle(sketch, "E81.88.0", {"center": v(15.93, 12.26) * mm, "radius": 0.5 * mm});
            skCircle(sketch, "E81.89.0", {"center": v(15.15, 13.2) * mm, "radius": 0.5 * mm});
            skCircle(sketch, "E81.90.0", {"center": v(14.32, 14.1) * mm, "radius": 0.5 * mm});
            skCircle(sketch, "E81.91.0", {"center": v(13.43, 14.95) * mm, "radius": 0.5 * mm});
            skCircle(sketch, "E81.92.0", {"center": v(12.5, 15.74) * mm, "radius": 0.5 * mm});
            skCircle(sketch, "E81.93.0", {"center": v(11.51, 16.47) * mm, "radius": 0.5 * mm});
            skCircle(sketch, "E81.94.0", {"center": v(10.49, 17.15) * mm, "radius": 0.5 * mm});
            skCircle(sketch, "E81.95.0", {"center": v(9.42, 17.75) * mm, "radius": 0.5 * mm});
            skCircle(sketch, "E81.96.0", {"center": v(8.32, 18.3) * mm, "radius": 0.5 * mm});
            skCircle(sketch, "E81.97.0", {"center": v(7.2, 18.77) * mm, "radius": 0.5 * mm});
            skCircle(sketch, "E81.98.0", {"center": v(6.04, 19.17) * mm, "radius": 0.5 * mm});
            skCircle(sketch, "E81.99.0", {"center": v(4.86, 19.5) * mm, "radius": 0.5 * mm});
            skCircle(sketch, "E81.100.0", {"center": v(3.66, 19.76) * mm, "radius": 0.5 * mm});
            skCircle(sketch, "E81.101.0", {"center": v(2.45, 19.95) * mm, "radius": 0.5 * mm});
            skCircle(sketch, "E81.102.0", {"center": v(1.23, 20.06) * mm, "radius": 0.5 * mm});
            skCircle(sketch, "E82.1.0", {"center": v(-1.22, 21.37) * mm, "radius": 0.5 * mm});
            skCircle(sketch, "E82.2.0", {"center": v(-2.44, 21.26) * mm, "radius": 0.5 * mm});
            skCircle(sketch, "E82.3.0", {"center": v(-3.65, 21.09) * mm, "radius": 0.5 * mm});
            skCircle(sketch, "E82.4.0", {"center": v(-4.85, 20.84) * mm, "radius": 0.5 * mm});
            skCircle(sketch, "E82.5.0", {"center": v(-6.03, 20.53) * mm, "radius": 0.5 * mm});
            skCircle(sketch, "E82.6.0", {"center": v(-7.2, 20.16) * mm, "radius": 0.5 * mm});
            skCircle(sketch, "E82.7.0", {"center": v(-8.33, 19.71) * mm, "radius": 0.5 * mm});
            skCircle(sketch, "E82.8.0", {"center": v(-9.44, 19.2) * mm, "radius": 0.5 * mm});
            skCircle(sketch, "E82.9.0", {"center": v(-10.52, 18.63) * mm, "radius": 0.5 * mm});
            skCircle(sketch, "E82.10.0", {"center": v(-11.57, 18) * mm, "radius": 0.5 * mm});
            skCircle(sketch, "E82.11.0", {"center": v(-12.58, 17.31) * mm, "radius": 0.5 * mm});
            skCircle(sketch, "E82.12.0", {"center": v(-13.55, 16.57) * mm, "radius": 0.5 * mm});
            skCircle(sketch, "E82.13.0", {"center": v(-14.47, 15.77) * mm, "radius": 0.5 * mm});
            skCircle(sketch, "E82.14.0", {"center": v(-15.35, 14.91) * mm, "radius": 0.5 * mm});
            skCircle(sketch, "E82.15.0", {"center": v(-16.17, 14.01) * mm, "radius": 0.5 * mm});
            skCircle(sketch, "E82.16.0", {"center": v(-16.95, 13.07) * mm, "radius": 0.5 * mm});
            skCircle(sketch, "E82.17.0", {"center": v(-17.67, 12.08) * mm, "radius": 0.5 * mm});
            skCircle(sketch, "E82.18.0", {"center": v(-18.33, 11.05) * mm, "radius": 0.5 * mm});
            skCircle(sketch, "E82.19.0", {"center": v(-18.93, 9.99) * mm, "radius": 0.5 * mm});
            skCircle(sketch, "E82.20.0", {"center": v(-19.47, 8.89) * mm, "radius": 0.5 * mm});
            skCircle(sketch, "E82.21.0", {"center": v(-19.94, 7.76) * mm, "radius": 0.5 * mm});
            skCircle(sketch, "E82.22.0", {"center": v(-20.35, 6.61) * mm, "radius": 0.5 * mm});
            skCircle(sketch, "E82.23.0", {"center": v(-20.7, 5.44) * mm, "radius": 0.5 * mm});
            skCircle(sketch, "E82.24.0", {"center": v(-20.97, 4.25) * mm, "radius": 0.5 * mm});
            skCircle(sketch, "E82.25.0", {"center": v(-21.18, 3.05) * mm, "radius": 0.5 * mm});
            skCircle(sketch, "E82.26.0", {"center": v(-21.32, 1.83) * mm, "radius": 0.5 * mm});
            skCircle(sketch, "E82.27.0", {"center": v(-21.4, 0.61) * mm, "radius": 0.5 * mm});
            skCircle(sketch, "E82.28.0", {"center": v(-21.4, -0.61) * mm, "radius": 0.5 * mm});
            skCircle(sketch, "E82.29.0", {"center": v(-21.32, -1.83) * mm, "radius": 0.5 * mm});
            skCircle(sketch, "E82.30.0", {"center": v(-21.18, -3.05) * mm, "radius": 0.5 * mm});
            skCircle(sketch, "E82.31.0", {"center": v(-20.97, -4.25) * mm, "radius": 0.5 * mm});
            skCircle(sketch, "E82.32.0", {"center": v(-20.7, -5.44) * mm, "radius": 0.5 * mm});
            skCircle(sketch, "E82.33.0", {"center": v(-20.35, -6.61) * mm, "radius": 0.5 * mm});
            skCircle(sketch, "E82.34.0", {"center": v(-19.94, -7.76) * mm, "radius": 0.5 * mm});
            skCircle(sketch, "E82.35.0", {"center": v(-19.47, -8.89) * mm, "radius": 0.5 * mm});
            skCircle(sketch, "E82.36.0", {"center": v(-18.93, -9.99) * mm, "radius": 0.5 * mm});
            skCircle(sketch, "E82.37.0", {"center": v(-18.33, -11.05) * mm, "radius": 0.5 * mm});
            skCircle(sketch, "E82.38.0", {"center": v(-17.67, -12.08) * mm, "radius": 0.5 * mm});
            skCircle(sketch, "E82.39.0", {"center": v(-16.95, -13.07) * mm, "radius": 0.5 * mm});
            skCircle(sketch, "E82.40.0", {"center": v(-16.17, -14.01) * mm, "radius": 0.5 * mm});
            skCircle(sketch, "E82.41.0", {"center": v(-15.35, -14.91) * mm, "radius": 0.5 * mm});
            skCircle(sketch, "E82.42.0", {"center": v(-14.47, -15.77) * mm, "radius": 0.5 * mm});
            skCircle(sketch, "E82.43.0", {"center": v(-13.55, -16.57) * mm, "radius": 0.5 * mm});
            skCircle(sketch, "E82.44.0", {"center": v(-12.58, -17.31) * mm, "radius": 0.5 * mm});
            skCircle(sketch, "E82.45.0", {"center": v(-11.57, -18) * mm, "radius": 0.5 * mm});
            skCircle(sketch, "E82.46.0", {"center": v(-10.52, -18.63) * mm, "radius": 0.5 * mm});
            skCircle(sketch, "E82.47.0", {"center": v(-9.44, -19.2) * mm, "radius": 0.5 * mm});
            skCircle(sketch, "E82.48.0", {"center": v(-8.33, -19.71) * mm, "radius": 0.5 * mm});
            skCircle(sketch, "E82.49.0", {"center": v(-7.2, -20.16) * mm, "radius": 0.5 * mm});
            skCircle(sketch, "E82.50.0", {"center": v(-6.03, -20.53) * mm, "radius": 0.5 * mm});
            skCircle(sketch, "E82.51.0", {"center": v(-4.85, -20.84) * mm, "radius": 0.5 * mm});
            skCircle(sketch, "E82.52.0", {"center": v(-3.65, -21.09) * mm, "radius": 0.5 * mm});
            skCircle(sketch, "E82.53.0", {"center": v(-2.44, -21.26) * mm, "radius": 0.5 * mm});
            skCircle(sketch, "E82.54.0", {"center": v(-1.22, -21.37) * mm, "radius": 0.5 * mm});
            skCircle(sketch, "E82.55.0", {"center": v(0, -21.4) * mm, "radius": 0.5 * mm});
            skCircle(sketch, "E82.56.0", {"center": v(1.22, -21.37) * mm, "radius": 0.5 * mm});
            skCircle(sketch, "E82.57.0", {"center": v(2.44, -21.26) * mm, "radius": 0.5 * mm});
            skCircle(sketch, "E82.58.0", {"center": v(3.65, -21.09) * mm, "radius": 0.5 * mm});
            skCircle(sketch, "E82.59.0", {"center": v(4.85, -20.84) * mm, "radius": 0.5 * mm});
            skCircle(sketch, "E82.60.0", {"center": v(6.03, -20.53) * mm, "radius": 0.5 * mm});
            skCircle(sketch, "E82.61.0", {"center": v(7.2, -20.16) * mm, "radius": 0.5 * mm});
            skCircle(sketch, "E82.62.0", {"center": v(8.33, -19.71) * mm, "radius": 0.5 * mm});
            skCircle(sketch, "E82.63.0", {"center": v(9.44, -19.2) * mm, "radius": 0.5 * mm});
            skCircle(sketch, "E82.64.0", {"center": v(10.52, -18.63) * mm, "radius": 0.5 * mm});
            skCircle(sketch, "E82.65.0", {"center": v(11.57, -18) * mm, "radius": 0.5 * mm});
            skCircle(sketch, "E82.66.0", {"center": v(12.58, -17.31) * mm, "radius": 0.5 * mm});
            skCircle(sketch, "E82.67.0", {"center": v(13.55, -16.57) * mm, "radius": 0.5 * mm});
            skCircle(sketch, "E82.68.0", {"center": v(14.47, -15.77) * mm, "radius": 0.5 * mm});
            skCircle(sketch, "E82.69.0", {"center": v(15.35, -14.91) * mm, "radius": 0.5 * mm});
            skCircle(sketch, "E82.70.0", {"center": v(16.17, -14.01) * mm, "radius": 0.5 * mm});
            skCircle(sketch, "E82.71.0", {"center": v(16.95, -13.07) * mm, "radius": 0.5 * mm});
            skCircle(sketch, "E82.72.0", {"center": v(17.67, -12.08) * mm, "radius": 0.5 * mm});
            skCircle(sketch, "E82.73.0", {"center": v(18.33, -11.05) * mm, "radius": 0.5 * mm});
            skCircle(sketch, "E82.74.0", {"center": v(18.93, -9.99) * mm, "radius": 0.5 * mm});
            skCircle(sketch, "E82.75.0", {"center": v(19.47, -8.89) * mm, "radius": 0.5 * mm});
            skCircle(sketch, "E82.76.0", {"center": v(19.94, -7.76) * mm, "radius": 0.5 * mm});
            skCircle(sketch, "E82.77.0", {"center": v(20.35, -6.61) * mm, "radius": 0.5 * mm});
            skCircle(sketch, "E82.78.0", {"center": v(20.7, -5.44) * mm, "radius": 0.5 * mm});
            skCircle(sketch, "E82.79.0", {"center": v(20.97, -4.25) * mm, "radius": 0.5 * mm});
            skCircle(sketch, "E82.80.0", {"center": v(21.18, -3.05) * mm, "radius": 0.5 * mm});
            skCircle(sketch, "E82.81.0", {"center": v(21.32, -1.83) * mm, "radius": 0.5 * mm});
            skCircle(sketch, "E82.82.0", {"center": v(21.4, -0.61) * mm, "radius": 0.5 * mm});
            skCircle(sketch, "E82.83.0", {"center": v(21.4, 0.61) * mm, "radius": 0.5 * mm});
            skCircle(sketch, "E82.84.0", {"center": v(21.32, 1.83) * mm, "radius": 0.5 * mm});
            skCircle(sketch, "E82.85.0", {"center": v(21.18, 3.05) * mm, "radius": 0.5 * mm});
            skCircle(sketch, "E82.86.0", {"center": v(20.97, 4.25) * mm, "radius": 0.5 * mm});
            skCircle(sketch, "E82.87.0", {"center": v(20.7, 5.44) * mm, "radius": 0.5 * mm});
            skCircle(sketch, "E82.88.0", {"center": v(20.35, 6.61) * mm, "radius": 0.5 * mm});
            skCircle(sketch, "E82.89.0", {"center": v(19.94, 7.76) * mm, "radius": 0.5 * mm});
            skCircle(sketch, "E82.90.0", {"center": v(19.47, 8.89) * mm, "radius": 0.5 * mm});
            skCircle(sketch, "E82.91.0", {"center": v(18.93, 9.99) * mm, "radius": 0.5 * mm});
            skCircle(sketch, "E82.92.0", {"center": v(18.33, 11.05) * mm, "radius": 0.5 * mm});
            skCircle(sketch, "E82.93.0", {"center": v(17.67, 12.08) * mm, "radius": 0.5 * mm});
            skCircle(sketch, "E82.94.0", {"center": v(16.95, 13.07) * mm, "radius": 0.5 * mm});
            skCircle(sketch, "E82.95.0", {"center": v(16.17, 14.01) * mm, "radius": 0.5 * mm});
            skCircle(sketch, "E82.96.0", {"center": v(15.35, 14.91) * mm, "radius": 0.5 * mm});
            skCircle(sketch, "E82.97.0", {"center": v(14.47, 15.77) * mm, "radius": 0.5 * mm});
            skCircle(sketch, "E82.98.0", {"center": v(13.55, 16.57) * mm, "radius": 0.5 * mm});
            skCircle(sketch, "E82.99.0", {"center": v(12.58, 17.31) * mm, "radius": 0.5 * mm});
            skCircle(sketch, "E82.100.0", {"center": v(11.57, 18) * mm, "radius": 0.5 * mm});
            skCircle(sketch, "E82.101.0", {"center": v(10.52, 18.63) * mm, "radius": 0.5 * mm});
            skCircle(sketch, "E82.102.0", {"center": v(9.44, 19.2) * mm, "radius": 0.5 * mm});
            skCircle(sketch, "E82.103.0", {"center": v(8.33, 19.71) * mm, "radius": 0.5 * mm});
            skCircle(sketch, "E82.104.0", {"center": v(7.2, 20.16) * mm, "radius": 0.5 * mm});
            skCircle(sketch, "E82.105.0", {"center": v(6.03, 20.53) * mm, "radius": 0.5 * mm});
            skCircle(sketch, "E82.106.0", {"center": v(4.85, 20.84) * mm, "radius": 0.5 * mm});
            skCircle(sketch, "E82.107.0", {"center": v(3.65, 21.09) * mm, "radius": 0.5 * mm});
            skCircle(sketch, "E82.108.0", {"center": v(2.44, 21.26) * mm, "radius": 0.5 * mm});
            skCircle(sketch, "E82.109.0", {"center": v(1.22, 21.37) * mm, "radius": 0.5 * mm});
            skCircle(sketch, "E83.1.0", {"center": v(-1.22, 22.67) * mm, "radius": 0.5 * mm});
            skCircle(sketch, "E83.2.0", {"center": v(-2.43, 22.57) * mm, "radius": 0.5 * mm});
            skCircle(sketch, "E83.3.0", {"center": v(-3.64, 22.4) * mm, "radius": 0.5 * mm});
            skCircle(sketch, "E83.4.0", {"center": v(-4.84, 22.18) * mm, "radius": 0.5 * mm});
            skCircle(sketch, "E83.5.0", {"center": v(-6.02, 21.89) * mm, "radius": 0.5 * mm});
            skCircle(sketch, "E83.6.0", {"center": v(-7.19, 21.53) * mm, "radius": 0.5 * mm});
            skCircle(sketch, "E83.7.0", {"center": v(-8.33, 21.11) * mm, "radius": 0.5 * mm});
            skCircle(sketch, "E83.8.0", {"center": v(-9.46, 20.64) * mm, "radius": 0.5 * mm});
            skCircle(sketch, "E83.9.0", {"center": v(-10.55, 20.1) * mm, "radius": 0.5 * mm});
            skCircle(sketch, "E83.10.0", {"center": v(-11.61, 19.5) * mm, "radius": 0.5 * mm});
            skCircle(sketch, "E83.11.0", {"center": v(-12.64, 18.85) * mm, "radius": 0.5 * mm});
            skCircle(sketch, "E83.12.0", {"center": v(-13.64, 18.15) * mm, "radius": 0.5 * mm});
            skCircle(sketch, "E83.13.0", {"center": v(-14.6, 17.39) * mm, "radius": 0.5 * mm});
            skCircle(sketch, "E83.14.0", {"center": v(-15.5, 16.58) * mm, "radius": 0.5 * mm});
            skCircle(sketch, "E83.15.0", {"center": v(-16.37, 15.72) * mm, "radius": 0.5 * mm});
            skCircle(sketch, "E83.16.0", {"center": v(-17.2, 14.82) * mm, "radius": 0.5 * mm});
            skCircle(sketch, "E83.17.0", {"center": v(-17.96, 13.88) * mm, "radius": 0.5 * mm});
            skCircle(sketch, "E83.18.0", {"center": v(-18.68, 12.9) * mm, "radius": 0.5 * mm});
            skCircle(sketch, "E83.19.0", {"center": v(-19.35, 11.87) * mm, "radius": 0.5 * mm});
            skCircle(sketch, "E83.20.0", {"center": v(-19.96, 10.82) * mm, "radius": 0.5 * mm});
            skCircle(sketch, "E83.21.0", {"center": v(-20.5, 9.73) * mm, "radius": 0.5 * mm});
            skCircle(sketch, "E83.22.0", {"center": v(-21, 8.62) * mm, "radius": 0.5 * mm});
            skCircle(sketch, "E83.23.0", {"center": v(-21.43, 7.48) * mm, "radius": 0.5 * mm});
            skCircle(sketch, "E83.24.0", {"center": v(-21.8, 6.32) * mm, "radius": 0.5 * mm});
            skCircle(sketch, "E83.25.0", {"center": v(-22.11, 5.14) * mm, "radius": 0.5 * mm});
            skCircle(sketch, "E83.26.0", {"center": v(-22.36, 3.94) * mm, "radius": 0.5 * mm});
            skCircle(sketch, "E83.27.0", {"center": v(-22.53, 2.74) * mm, "radius": 0.5 * mm});
            skCircle(sketch, "E83.28.0", {"center": v(-22.65, 1.52) * mm, "radius": 0.5 * mm});
            skCircle(sketch, "E83.29.0", {"center": v(-22.7, 0.3) * mm, "radius": 0.5 * mm});
            skCircle(sketch, "E83.30.0", {"center": v(-22.68, -0.91) * mm, "radius": 0.5 * mm});
            skCircle(sketch, "E83.31.0", {"center": v(-22.6, -2.13) * mm, "radius": 0.5 * mm});
            skCircle(sketch, "E83.32.0", {"center": v(-22.45, -3.34) * mm, "radius": 0.5 * mm});
            skCircle(sketch, "E83.33.0", {"center": v(-22.24, -4.54) * mm, "radius": 0.5 * mm});
            skCircle(sketch, "E83.34.0", {"center": v(-21.97, -5.73) * mm, "radius": 0.5 * mm});
            skCircle(sketch, "E83.35.0", {"center": v(-21.63, -6.9) * mm, "radius": 0.5 * mm});
            skCircle(sketch, "E83.36.0", {"center": v(-21.22, -8.05) * mm, "radius": 0.5 * mm});
            skCircle(sketch, "E83.37.0", {"center": v(-20.76, -9.18) * mm, "radius": 0.5 * mm});
            skCircle(sketch, "E83.38.0", {"center": v(-20.24, -10.28) * mm, "radius": 0.5 * mm});
            skCircle(sketch, "E83.39.0", {"center": v(-19.66, -11.35) * mm, "radius": 0.5 * mm});
            skCircle(sketch, "E83.40.0", {"center": v(-19.02, -12.39) * mm, "radius": 0.5 * mm});
            skCircle(sketch, "E83.41.0", {"center": v(-18.33, -13.4) * mm, "radius": 0.5 * mm});
            skCircle(sketch, "E83.42.0", {"center": v(-17.58, -14.36) * mm, "radius": 0.5 * mm});
            skCircle(sketch, "E83.43.0", {"center": v(-16.79, -15.28) * mm, "radius": 0.5 * mm});
            skCircle(sketch, "E83.44.0", {"center": v(-15.94, -16.16) * mm, "radius": 0.5 * mm});
            skCircle(sketch, "E83.45.0", {"center": v(-15.05, -17) * mm, "radius": 0.5 * mm});
            skCircle(sketch, "E83.46.0", {"center": v(-14.12, -17.77) * mm, "radius": 0.5 * mm});
            skCircle(sketch, "E83.47.0", {"center": v(-13.14, -18.5) * mm, "radius": 0.5 * mm});
            skCircle(sketch, "E83.48.0", {"center": v(-12.13, -19.19) * mm, "radius": 0.5 * mm});
            skCircle(sketch, "E83.49.0", {"center": v(-11.09, -19.8) * mm, "radius": 0.5 * mm});
            skCircle(sketch, "E83.50.0", {"center": v(-10, -20.38) * mm, "radius": 0.5 * mm});
            skCircle(sketch, "E83.51.0", {"center": v(-8.9, -20.88) * mm, "radius": 0.5 * mm});
            skCircle(sketch, "E83.52.0", {"center": v(-7.76, -21.33) * mm, "radius": 0.5 * mm});
            skCircle(sketch, "E83.53.0", {"center": v(-6.6, -21.72) * mm, "radius": 0.5 * mm});
            skCircle(sketch, "E83.54.0", {"center": v(-5.43, -22.04) * mm, "radius": 0.5 * mm});
            skCircle(sketch, "E83.55.0", {"center": v(-4.24, -22.3) * mm, "radius": 0.5 * mm});
            skCircle(sketch, "E83.56.0", {"center": v(-3.04, -22.5) * mm, "radius": 0.5 * mm});
            skCircle(sketch, "E83.57.0", {"center": v(-1.83, -22.63) * mm, "radius": 0.5 * mm});
            skCircle(sketch, "E83.58.0", {"center": v(-0.6, -22.7) * mm, "radius": 0.5 * mm});
            skCircle(sketch, "E83.59.0", {"center": v(0.6, -22.7) * mm, "radius": 0.5 * mm});
            skCircle(sketch, "E83.60.0", {"center": v(1.83, -22.63) * mm, "radius": 0.5 * mm});
            skCircle(sketch, "E83.61.0", {"center": v(3.04, -22.5) * mm, "radius": 0.5 * mm});
            skCircle(sketch, "E83.62.0", {"center": v(4.24, -22.3) * mm, "radius": 0.5 * mm});
            skCircle(sketch, "E83.63.0", {"center": v(5.43, -22.04) * mm, "radius": 0.5 * mm});
            skCircle(sketch, "E83.64.0", {"center": v(6.6, -21.72) * mm, "radius": 0.5 * mm});
            skCircle(sketch, "E83.65.0", {"center": v(7.76, -21.33) * mm, "radius": 0.5 * mm});
            skCircle(sketch, "E83.66.0", {"center": v(8.9, -20.88) * mm, "radius": 0.5 * mm});
            skCircle(sketch, "E83.67.0", {"center": v(10, -20.38) * mm, "radius": 0.5 * mm});
            skCircle(sketch, "E83.68.0", {"center": v(11.09, -19.8) * mm, "radius": 0.5 * mm});
            skCircle(sketch, "E83.69.0", {"center": v(12.13, -19.19) * mm, "radius": 0.5 * mm});
            skCircle(sketch, "E83.70.0", {"center": v(13.14, -18.5) * mm, "radius": 0.5 * mm});
            skCircle(sketch, "E83.71.0", {"center": v(14.12, -17.77) * mm, "radius": 0.5 * mm});
            skCircle(sketch, "E83.72.0", {"center": v(15.05, -17) * mm, "radius": 0.5 * mm});
            skCircle(sketch, "E83.73.0", {"center": v(15.94, -16.16) * mm, "radius": 0.5 * mm});
            skCircle(sketch, "E83.74.0", {"center": v(16.79, -15.28) * mm, "radius": 0.5 * mm});
            skCircle(sketch, "E83.75.0", {"center": v(17.58, -14.36) * mm, "radius": 0.5 * mm});
            skCircle(sketch, "E83.76.0", {"center": v(18.33, -13.4) * mm, "radius": 0.5 * mm});
            skCircle(sketch, "E83.77.0", {"center": v(19.02, -12.39) * mm, "radius": 0.5 * mm});
            skCircle(sketch, "E83.78.0", {"center": v(19.66, -11.35) * mm, "radius": 0.5 * mm});
            skCircle(sketch, "E83.79.0", {"center": v(20.24, -10.28) * mm, "radius": 0.5 * mm});
            skCircle(sketch, "E83.80.0", {"center": v(20.76, -9.18) * mm, "radius": 0.5 * mm});
            skCircle(sketch, "E83.81.0", {"center": v(21.22, -8.05) * mm, "radius": 0.5 * mm});
            skCircle(sketch, "E83.82.0", {"center": v(21.63, -6.9) * mm, "radius": 0.5 * mm});
            skCircle(sketch, "E83.83.0", {"center": v(21.97, -5.73) * mm, "radius": 0.5 * mm});
            skCircle(sketch, "E83.84.0", {"center": v(22.24, -4.54) * mm, "radius": 0.5 * mm});
            skCircle(sketch, "E83.85.0", {"center": v(22.45, -3.34) * mm, "radius": 0.5 * mm});
            skCircle(sketch, "E83.86.0", {"center": v(22.6, -2.13) * mm, "radius": 0.5 * mm});
            skCircle(sketch, "E83.87.0", {"center": v(22.68, -0.91) * mm, "radius": 0.5 * mm});
            skCircle(sketch, "E83.88.0", {"center": v(22.7, 0.3) * mm, "radius": 0.5 * mm});
            skCircle(sketch, "E83.89.0", {"center": v(22.65, 1.52) * mm, "radius": 0.5 * mm});
            skCircle(sketch, "E83.90.0", {"center": v(22.53, 2.74) * mm, "radius": 0.5 * mm});
            skCircle(sketch, "E83.91.0", {"center": v(22.36, 3.94) * mm, "radius": 0.5 * mm});
            skCircle(sketch, "E83.92.0", {"center": v(22.11, 5.14) * mm, "radius": 0.5 * mm});
            skCircle(sketch, "E83.93.0", {"center": v(21.8, 6.32) * mm, "radius": 0.5 * mm});
            skCircle(sketch, "E83.94.0", {"center": v(21.43, 7.48) * mm, "radius": 0.5 * mm});
            skCircle(sketch, "E83.95.0", {"center": v(21, 8.62) * mm, "radius": 0.5 * mm});
            skCircle(sketch, "E83.96.0", {"center": v(20.5, 9.73) * mm, "radius": 0.5 * mm});
            skCircle(sketch, "E83.97.0", {"center": v(19.96, 10.82) * mm, "radius": 0.5 * mm});
            skCircle(sketch, "E83.98.0", {"center": v(19.35, 11.87) * mm, "radius": 0.5 * mm});
            skCircle(sketch, "E83.99.0", {"center": v(18.68, 12.9) * mm, "radius": 0.5 * mm});
            skCircle(sketch, "E83.100.0", {"center": v(17.96, 13.88) * mm, "radius": 0.5 * mm});
            skCircle(sketch, "E83.101.0", {"center": v(17.2, 14.82) * mm, "radius": 0.5 * mm});
            skCircle(sketch, "E83.102.0", {"center": v(16.37, 15.72) * mm, "radius": 0.5 * mm});
            skCircle(sketch, "E83.103.0", {"center": v(15.5, 16.58) * mm, "radius": 0.5 * mm});
            skCircle(sketch, "E83.104.0", {"center": v(14.6, 17.39) * mm, "radius": 0.5 * mm});
            skCircle(sketch, "E83.105.0", {"center": v(13.64, 18.15) * mm, "radius": 0.5 * mm});
            skCircle(sketch, "E83.106.0", {"center": v(12.64, 18.85) * mm, "radius": 0.5 * mm});
            skCircle(sketch, "E83.107.0", {"center": v(11.61, 19.5) * mm, "radius": 0.5 * mm});
            skCircle(sketch, "E83.108.0", {"center": v(10.55, 20.1) * mm, "radius": 0.5 * mm});
            skCircle(sketch, "E83.109.0", {"center": v(9.46, 20.64) * mm, "radius": 0.5 * mm});
            skCircle(sketch, "E83.110.0", {"center": v(8.33, 21.11) * mm, "radius": 0.5 * mm});
            skCircle(sketch, "E83.111.0", {"center": v(7.19, 21.53) * mm, "radius": 0.5 * mm});
            skCircle(sketch, "E83.112.0", {"center": v(6.02, 21.89) * mm, "radius": 0.5 * mm});
            skCircle(sketch, "E83.113.0", {"center": v(4.84, 22.18) * mm, "radius": 0.5 * mm});
            skCircle(sketch, "E83.114.0", {"center": v(3.64, 22.4) * mm, "radius": 0.5 * mm});
            skCircle(sketch, "E83.115.0", {"center": v(2.43, 22.57) * mm, "radius": 0.5 * mm});
            skCircle(sketch, "E83.116.0", {"center": v(1.22, 22.67) * mm, "radius": 0.5 * mm});
            skCircle(sketch, "E84.1.0", {"center": v(-1.22, 23.97) * mm, "radius": 0.5 * mm});
            skCircle(sketch, "E84.2.0", {"center": v(-2.43, 23.88) * mm, "radius": 0.5 * mm});
            skCircle(sketch, "E84.3.0", {"center": v(-3.63, 23.72) * mm, "radius": 0.5 * mm});
            skCircle(sketch, "E84.4.0", {"center": v(-4.83, 23.5) * mm, "radius": 0.5 * mm});
            skCircle(sketch, "E84.5.0", {"center": v(-6.02, 23.23) * mm, "radius": 0.5 * mm});
            skCircle(sketch, "E84.6.0", {"center": v(-7.18, 22.9) * mm, "radius": 0.5 * mm});
            skCircle(sketch, "E84.7.0", {"center": v(-8.34, 22.5) * mm, "radius": 0.5 * mm});
            skCircle(sketch, "E84.8.0", {"center": v(-9.46, 22.05) * mm, "radius": 0.5 * mm});
            skCircle(sketch, "E84.9.0", {"center": v(-10.57, 21.55) * mm, "radius": 0.5 * mm});
            skCircle(sketch, "E84.10.0", {"center": v(-11.65, 20.98) * mm, "radius": 0.5 * mm});
            skCircle(sketch, "E84.11.0", {"center": v(-12.7, 20.37) * mm, "radius": 0.5 * mm});
            skCircle(sketch, "E84.12.0", {"center": v(-13.71, 19.7) * mm, "radius": 0.5 * mm});
            skCircle(sketch, "E84.13.0", {"center": v(-14.7, 18.98) * mm, "radius": 0.5 * mm});
            skCircle(sketch, "E84.14.0", {"center": v(-15.63, 18.21) * mm, "radius": 0.5 * mm});
            skCircle(sketch, "E84.15.0", {"center": v(-16.54, 17.4) * mm, "radius": 0.5 * mm});
            skCircle(sketch, "E84.16.0", {"center": v(-17.4, 16.54) * mm, "radius": 0.5 * mm});
            skCircle(sketch, "E84.17.0", {"center": v(-18.21, 15.63) * mm, "radius": 0.5 * mm});
            skCircle(sketch, "E84.18.0", {"center": v(-18.98, 14.7) * mm, "radius": 0.5 * mm});
            skCircle(sketch, "E84.19.0", {"center": v(-19.7, 13.71) * mm, "radius": 0.5 * mm});
            skCircle(sketch, "E84.20.0", {"center": v(-20.37, 12.7) * mm, "radius": 0.5 * mm});
            skCircle(sketch, "E84.21.0", {"center": v(-20.98, 11.65) * mm, "radius": 0.5 * mm});
            skCircle(sketch, "E84.22.0", {"center": v(-21.55, 10.57) * mm, "radius": 0.5 * mm});
            skCircle(sketch, "E84.23.0", {"center": v(-22.05, 9.46) * mm, "radius": 0.5 * mm});
            skCircle(sketch, "E84.24.0", {"center": v(-22.5, 8.34) * mm, "radius": 0.5 * mm});
            skCircle(sketch, "E84.25.0", {"center": v(-22.9, 7.18) * mm, "radius": 0.5 * mm});
            skCircle(sketch, "E84.26.0", {"center": v(-23.23, 6.02) * mm, "radius": 0.5 * mm});
            skCircle(sketch, "E84.27.0", {"center": v(-23.5, 4.83) * mm, "radius": 0.5 * mm});
            skCircle(sketch, "E84.28.0", {"center": v(-23.72, 3.63) * mm, "radius": 0.5 * mm});
            skCircle(sketch, "E84.29.0", {"center": v(-23.88, 2.43) * mm, "radius": 0.5 * mm});
            skCircle(sketch, "E84.30.0", {"center": v(-23.97, 1.22) * mm, "radius": 0.5 * mm});
            skCircle(sketch, "E84.31.0", {"center": v(-24, 0) * mm, "radius": 0.5 * mm});
            skCircle(sketch, "E84.32.0", {"center": v(-23.97, -1.22) * mm, "radius": 0.5 * mm});
            skCircle(sketch, "E84.33.0", {"center": v(-23.88, -2.43) * mm, "radius": 0.5 * mm});
            skCircle(sketch, "E84.34.0", {"center": v(-23.72, -3.63) * mm, "radius": 0.5 * mm});
            skCircle(sketch, "E84.35.0", {"center": v(-23.5, -4.83) * mm, "radius": 0.5 * mm});
            skCircle(sketch, "E84.36.0", {"center": v(-23.23, -6.02) * mm, "radius": 0.5 * mm});
            skCircle(sketch, "E84.37.0", {"center": v(-22.9, -7.18) * mm, "radius": 0.5 * mm});
            skCircle(sketch, "E84.38.0", {"center": v(-22.5, -8.34) * mm, "radius": 0.5 * mm});
            skCircle(sketch, "E84.39.0", {"center": v(-22.05, -9.46) * mm, "radius": 0.5 * mm});
            skCircle(sketch, "E84.40.0", {"center": v(-21.55, -10.57) * mm, "radius": 0.5 * mm});
            skCircle(sketch, "E84.41.0", {"center": v(-20.98, -11.65) * mm, "radius": 0.5 * mm});
            skCircle(sketch, "E84.42.0", {"center": v(-20.37, -12.7) * mm, "radius": 0.5 * mm});
            skCircle(sketch, "E84.43.0", {"center": v(-19.7, -13.71) * mm, "radius": 0.5 * mm});
            skCircle(sketch, "E84.44.0", {"center": v(-18.98, -14.7) * mm, "radius": 0.5 * mm});
            skCircle(sketch, "E84.45.0", {"center": v(-18.21, -15.63) * mm, "radius": 0.5 * mm});
            skCircle(sketch, "E84.46.0", {"center": v(-17.4, -16.54) * mm, "radius": 0.5 * mm});
            skCircle(sketch, "E84.47.0", {"center": v(-16.54, -17.4) * mm, "radius": 0.5 * mm});
            skCircle(sketch, "E84.48.0", {"center": v(-15.63, -18.21) * mm, "radius": 0.5 * mm});
            skCircle(sketch, "E84.49.0", {"center": v(-14.7, -18.98) * mm, "radius": 0.5 * mm});
            skCircle(sketch, "E84.50.0", {"center": v(-13.71, -19.7) * mm, "radius": 0.5 * mm});
            skCircle(sketch, "E84.51.0", {"center": v(-12.7, -20.37) * mm, "radius": 0.5 * mm});
            skCircle(sketch, "E84.52.0", {"center": v(-11.65, -20.98) * mm, "radius": 0.5 * mm});
            skCircle(sketch, "E84.53.0", {"center": v(-10.57, -21.55) * mm, "radius": 0.5 * mm});
            skCircle(sketch, "E84.54.0", {"center": v(-9.46, -22.05) * mm, "radius": 0.5 * mm});
            skCircle(sketch, "E84.55.0", {"center": v(-8.34, -22.5) * mm, "radius": 0.5 * mm});
            skCircle(sketch, "E84.56.0", {"center": v(-7.18, -22.9) * mm, "radius": 0.5 * mm});
            skCircle(sketch, "E84.57.0", {"center": v(-6.02, -23.23) * mm, "radius": 0.5 * mm});
            skCircle(sketch, "E84.58.0", {"center": v(-4.83, -23.5) * mm, "radius": 0.5 * mm});
            skCircle(sketch, "E84.59.0", {"center": v(-3.63, -23.72) * mm, "radius": 0.5 * mm});
            skCircle(sketch, "E84.60.0", {"center": v(-2.43, -23.88) * mm, "radius": 0.5 * mm});
            skCircle(sketch, "E84.61.0", {"center": v(-1.22, -23.97) * mm, "radius": 0.5 * mm});
            skCircle(sketch, "E84.62.0", {"center": v(0, -24) * mm, "radius": 0.5 * mm});
            skCircle(sketch, "E84.63.0", {"center": v(1.22, -23.97) * mm, "radius": 0.5 * mm});
            skCircle(sketch, "E84.64.0", {"center": v(2.43, -23.88) * mm, "radius": 0.5 * mm});
            skCircle(sketch, "E84.65.0", {"center": v(3.63, -23.72) * mm, "radius": 0.5 * mm});
            skCircle(sketch, "E84.66.0", {"center": v(4.83, -23.5) * mm, "radius": 0.5 * mm});
            skCircle(sketch, "E84.67.0", {"center": v(6.02, -23.23) * mm, "radius": 0.5 * mm});
            skCircle(sketch, "E84.68.0", {"center": v(7.18, -22.9) * mm, "radius": 0.5 * mm});
            skCircle(sketch, "E84.69.0", {"center": v(8.34, -22.5) * mm, "radius": 0.5 * mm});
            skCircle(sketch, "E84.70.0", {"center": v(9.46, -22.05) * mm, "radius": 0.5 * mm});
            skCircle(sketch, "E84.71.0", {"center": v(10.57, -21.55) * mm, "radius": 0.5 * mm});
            skCircle(sketch, "E84.72.0", {"center": v(11.65, -20.98) * mm, "radius": 0.5 * mm});
            skCircle(sketch, "E84.73.0", {"center": v(12.7, -20.37) * mm, "radius": 0.5 * mm});
            skCircle(sketch, "E84.74.0", {"center": v(13.71, -19.7) * mm, "radius": 0.5 * mm});
            skCircle(sketch, "E84.75.0", {"center": v(14.7, -18.98) * mm, "radius": 0.5 * mm});
            skCircle(sketch, "E84.76.0", {"center": v(15.63, -18.21) * mm, "radius": 0.5 * mm});
            skCircle(sketch, "E84.77.0", {"center": v(16.54, -17.4) * mm, "radius": 0.5 * mm});
            skCircle(sketch, "E84.78.0", {"center": v(17.4, -16.54) * mm, "radius": 0.5 * mm});
            skCircle(sketch, "E84.79.0", {"center": v(18.21, -15.63) * mm, "radius": 0.5 * mm});
            skCircle(sketch, "E84.80.0", {"center": v(18.98, -14.7) * mm, "radius": 0.5 * mm});
            skCircle(sketch, "E84.81.0", {"center": v(19.7, -13.71) * mm, "radius": 0.5 * mm});
            skCircle(sketch, "E84.82.0", {"center": v(20.37, -12.7) * mm, "radius": 0.5 * mm});
            skCircle(sketch, "E84.83.0", {"center": v(20.98, -11.65) * mm, "radius": 0.5 * mm});
            skCircle(sketch, "E84.84.0", {"center": v(21.55, -10.57) * mm, "radius": 0.5 * mm});
            skCircle(sketch, "E84.85.0", {"center": v(22.05, -9.46) * mm, "radius": 0.5 * mm});
            skCircle(sketch, "E84.86.0", {"center": v(22.5, -8.34) * mm, "radius": 0.5 * mm});
            skCircle(sketch, "E84.87.0", {"center": v(22.9, -7.18) * mm, "radius": 0.5 * mm});
            skCircle(sketch, "E84.88.0", {"center": v(23.23, -6.02) * mm, "radius": 0.5 * mm});
            skCircle(sketch, "E84.89.0", {"center": v(23.5, -4.83) * mm, "radius": 0.5 * mm});
            skCircle(sketch, "E84.90.0", {"center": v(23.72, -3.63) * mm, "radius": 0.5 * mm});
            skCircle(sketch, "E84.91.0", {"center": v(23.88, -2.43) * mm, "radius": 0.5 * mm});
            skCircle(sketch, "E84.92.0", {"center": v(23.97, -1.22) * mm, "radius": 0.5 * mm});
            skCircle(sketch, "E84.93.0", {"center": v(24, 0) * mm, "radius": 0.5 * mm});
            skCircle(sketch, "E84.94.0", {"center": v(23.97, 1.22) * mm, "radius": 0.5 * mm});
            skCircle(sketch, "E84.95.0", {"center": v(23.88, 2.43) * mm, "radius": 0.5 * mm});
            skCircle(sketch, "E84.96.0", {"center": v(23.72, 3.63) * mm, "radius": 0.5 * mm});
            skCircle(sketch, "E84.97.0", {"center": v(23.5, 4.83) * mm, "radius": 0.5 * mm});
            skCircle(sketch, "E84.98.0", {"center": v(23.23, 6.02) * mm, "radius": 0.5 * mm});
            skCircle(sketch, "E84.99.0", {"center": v(22.9, 7.18) * mm, "radius": 0.5 * mm});
            skCircle(sketch, "E84.100.0", {"center": v(22.5, 8.34) * mm, "radius": 0.5 * mm});
            skCircle(sketch, "E84.101.0", {"center": v(22.05, 9.46) * mm, "radius": 0.5 * mm});
            skCircle(sketch, "E84.102.0", {"center": v(21.55, 10.57) * mm, "radius": 0.5 * mm});
            skCircle(sketch, "E84.103.0", {"center": v(20.98, 11.65) * mm, "radius": 0.5 * mm});
            skCircle(sketch, "E84.104.0", {"center": v(20.37, 12.7) * mm, "radius": 0.5 * mm});
            skCircle(sketch, "E84.105.0", {"center": v(19.7, 13.71) * mm, "radius": 0.5 * mm});
            skCircle(sketch, "E84.106.0", {"center": v(18.98, 14.7) * mm, "radius": 0.5 * mm});
            skCircle(sketch, "E84.107.0", {"center": v(18.21, 15.63) * mm, "radius": 0.5 * mm});
            skCircle(sketch, "E84.108.0", {"center": v(17.4, 16.54) * mm, "radius": 0.5 * mm});
            skCircle(sketch, "E84.109.0", {"center": v(16.54, 17.4) * mm, "radius": 0.5 * mm});
            skCircle(sketch, "E84.110.0", {"center": v(15.63, 18.21) * mm, "radius": 0.5 * mm});
            skCircle(sketch, "E84.111.0", {"center": v(14.7, 18.98) * mm, "radius": 0.5 * mm});
            skCircle(sketch, "E84.112.0", {"center": v(13.71, 19.7) * mm, "radius": 0.5 * mm});
            skCircle(sketch, "E84.113.0", {"center": v(12.7, 20.37) * mm, "radius": 0.5 * mm});
            skCircle(sketch, "E84.114.0", {"center": v(11.65, 20.98) * mm, "radius": 0.5 * mm});
            skCircle(sketch, "E84.115.0", {"center": v(10.57, 21.55) * mm, "radius": 0.5 * mm});
            skCircle(sketch, "E84.116.0", {"center": v(9.46, 22.05) * mm, "radius": 0.5 * mm});
            skCircle(sketch, "E84.117.0", {"center": v(8.34, 22.5) * mm, "radius": 0.5 * mm});
            skCircle(sketch, "E84.118.0", {"center": v(7.18, 22.9) * mm, "radius": 0.5 * mm});
            skCircle(sketch, "E84.119.0", {"center": v(6.02, 23.23) * mm, "radius": 0.5 * mm});
            skCircle(sketch, "E84.120.0", {"center": v(4.83, 23.5) * mm, "radius": 0.5 * mm});
            skCircle(sketch, "E84.121.0", {"center": v(3.63, 23.72) * mm, "radius": 0.5 * mm});
            skCircle(sketch, "E84.122.0", {"center": v(2.43, 23.88) * mm, "radius": 0.5 * mm});
            skCircle(sketch, "E84.123.0", {"center": v(1.22, 23.97) * mm, "radius": 0.5 * mm});
            skCircle(sketch, "E85.1.0", {"center": v(-1.21, 25.27) * mm, "radius": 0.5 * mm});
            skCircle(sketch, "E85.2.0", {"center": v(-2.42, 25.18) * mm, "radius": 0.5 * mm});
            skCircle(sketch, "E85.3.0", {"center": v(-3.63, 25.04) * mm, "radius": 0.5 * mm});
            skCircle(sketch, "E85.4.0", {"center": v(-4.82, 24.84) * mm, "radius": 0.5 * mm});
            skCircle(sketch, "E85.5.0", {"center": v(-6, 24.58) * mm, "radius": 0.5 * mm});
            skCircle(sketch, "E85.6.0", {"center": v(-7.18, 24.26) * mm, "radius": 0.5 * mm});
            skCircle(sketch, "E85.7.0", {"center": v(-8.34, 23.89) * mm, "radius": 0.5 * mm});
            skCircle(sketch, "E85.8.0", {"center": v(-9.47, 23.46) * mm, "radius": 0.5 * mm});
            skCircle(sketch, "E85.9.0", {"center": v(-10.59, 22.98) * mm, "radius": 0.5 * mm});
            skCircle(sketch, "E85.10.0", {"center": v(-11.67, 22.45) * mm, "radius": 0.5 * mm});
            skCircle(sketch, "E85.11.0", {"center": v(-12.74, 21.86) * mm, "radius": 0.5 * mm});
            skCircle(sketch, "E85.12.0", {"center": v(-13.77, 21.22) * mm, "radius": 0.5 * mm});
            skCircle(sketch, "E85.13.0", {"center": v(-14.77, 20.54) * mm, "radius": 0.5 * mm});
            skCircle(sketch, "E85.14.0", {"center": v(-15.74, 19.8) * mm, "radius": 0.5 * mm});
            skCircle(sketch, "E85.15.0", {"center": v(-16.67, 19.03) * mm, "radius": 0.5 * mm});
            skCircle(sketch, "E85.16.0", {"center": v(-17.57, 18.2) * mm, "radius": 0.5 * mm});
            skCircle(sketch, "E85.17.0", {"center": v(-18.42, 17.35) * mm, "radius": 0.5 * mm});
            skCircle(sketch, "E85.18.0", {"center": v(-19.23, 16.44) * mm, "radius": 0.5 * mm});
            skCircle(sketch, "E85.19.0", {"center": v(-20, 15.5) * mm, "radius": 0.5 * mm});
            skCircle(sketch, "E85.20.0", {"center": v(-20.71, 14.53) * mm, "radius": 0.5 * mm});
            skCircle(sketch, "E85.21.0", {"center": v(-21.39, 13.52) * mm, "radius": 0.5 * mm});
            skCircle(sketch, "E85.22.0", {"center": v(-22.01, 12.47) * mm, "radius": 0.5 * mm});
            skCircle(sketch, "E85.23.0", {"center": v(-22.58, 11.4) * mm, "radius": 0.5 * mm});
            skCircle(sketch, "E85.24.0", {"center": v(-23.1, 10.3) * mm, "radius": 0.5 * mm});
            skCircle(sketch, "E85.25.0", {"center": v(-23.57, 9.19) * mm, "radius": 0.5 * mm});
            skCircle(sketch, "E85.26.0", {"center": v(-23.99, 8.05) * mm, "radius": 0.5 * mm});
            skCircle(sketch, "E85.27.0", {"center": v(-24.34, 6.89) * mm, "radius": 0.5 * mm});
            skCircle(sketch, "E85.28.0", {"center": v(-24.65, 5.71) * mm, "radius": 0.5 * mm});
            skCircle(sketch, "E85.29.0", {"center": v(-24.9, 4.53) * mm, "radius": 0.5 * mm});
            skCircle(sketch, "E85.30.0", {"center": v(-25.08, 3.33) * mm, "radius": 0.5 * mm});
            skCircle(sketch, "E85.31.0", {"center": v(-25.21, 2.12) * mm, "radius": 0.5 * mm});
            skCircle(sketch, "E85.32.0", {"center": v(-25.28, 0.9) * mm, "radius": 0.5 * mm});
            skCircle(sketch, "E85.33.0", {"center": v(-25.3, -0.3) * mm, "radius": 0.5 * mm});
            skCircle(sketch, "E85.34.0", {"center": v(-25.25, -1.52) * mm, "radius": 0.5 * mm});
            skCircle(sketch, "E85.35.0", {"center": v(-25.15, -2.73) * mm, "radius": 0.5 * mm});
            skCircle(sketch, "E85.36.0", {"center": v(-25, -3.93) * mm, "radius": 0.5 * mm});
            skCircle(sketch, "E85.37.0", {"center": v(-24.78, -5.12) * mm, "radius": 0.5 * mm});
            skCircle(sketch, "E85.38.0", {"center": v(-24.5, -6.3) * mm, "radius": 0.5 * mm});
            skCircle(sketch, "E85.39.0", {"center": v(-24.17, -7.47) * mm, "radius": 0.5 * mm});
            skCircle(sketch, "E85.40.0", {"center": v(-23.79, -8.62) * mm, "radius": 0.5 * mm});
            skCircle(sketch, "E85.41.0", {"center": v(-23.35, -9.75) * mm, "radius": 0.5 * mm});
            skCircle(sketch, "E85.42.0", {"center": v(-22.85, -10.86) * mm, "radius": 0.5 * mm});
            skCircle(sketch, "E85.43.0", {"center": v(-22.3, -11.94) * mm, "radius": 0.5 * mm});
            skCircle(sketch, "E85.44.0", {"center": v(-21.7, -13) * mm, "radius": 0.5 * mm});
            skCircle(sketch, "E85.45.0", {"center": v(-21.06, -14.02) * mm, "radius": 0.5 * mm});
            skCircle(sketch, "E85.46.0", {"center": v(-20.36, -15.02) * mm, "radius": 0.5 * mm});
            skCircle(sketch, "E85.47.0", {"center": v(-19.62, -15.98) * mm, "radius": 0.5 * mm});
            skCircle(sketch, "E85.48.0", {"center": v(-18.83, -16.9) * mm, "radius": 0.5 * mm});
            skCircle(sketch, "E85.49.0", {"center": v(-18, -17.78) * mm, "radius": 0.5 * mm});
            skCircle(sketch, "E85.50.0", {"center": v(-17.12, -18.62) * mm, "radius": 0.5 * mm});
            skCircle(sketch, "E85.51.0", {"center": v(-16.21, -19.42) * mm, "radius": 0.5 * mm});
            skCircle(sketch, "E85.52.0", {"center": v(-15.26, -20.18) * mm, "radius": 0.5 * mm});
            skCircle(sketch, "E85.53.0", {"center": v(-14.28, -20.89) * mm, "radius": 0.5 * mm});
            skCircle(sketch, "E85.54.0", {"center": v(-13.26, -21.55) * mm, "radius": 0.5 * mm});
            skCircle(sketch, "E85.55.0", {"center": v(-12.2, -22.16) * mm, "radius": 0.5 * mm});
            skCircle(sketch, "E85.56.0", {"center": v(-11.13, -22.72) * mm, "radius": 0.5 * mm});
            skCircle(sketch, "E85.57.0", {"center": v(-10.03, -23.23) * mm, "radius": 0.5 * mm});
            skCircle(sketch, "E85.58.0", {"center": v(-8.9, -23.68) * mm, "radius": 0.5 * mm});
            skCircle(sketch, "E85.59.0", {"center": v(-7.76, -24.08) * mm, "radius": 0.5 * mm});
            skCircle(sketch, "E85.60.0", {"center": v(-6.6, -24.42) * mm, "radius": 0.5 * mm});
            skCircle(sketch, "E85.61.0", {"center": v(-5.42, -24.71) * mm, "radius": 0.5 * mm});
            skCircle(sketch, "E85.62.0", {"center": v(-4.23, -24.94) * mm, "radius": 0.5 * mm});
            skCircle(sketch, "E85.63.0", {"center": v(-3.03, -25.12) * mm, "radius": 0.5 * mm});
            skCircle(sketch, "E85.64.0", {"center": v(-1.82, -25.23) * mm, "radius": 0.5 * mm});
            skCircle(sketch, "E85.65.0", {"center": v(-0.6, -25.3) * mm, "radius": 0.5 * mm});
            skCircle(sketch, "E85.66.0", {"center": v(0.6, -25.3) * mm, "radius": 0.5 * mm});
            skCircle(sketch, "E85.67.0", {"center": v(1.82, -25.23) * mm, "radius": 0.5 * mm});
            skCircle(sketch, "E85.68.0", {"center": v(3.03, -25.12) * mm, "radius": 0.5 * mm});
            skCircle(sketch, "E85.69.0", {"center": v(4.23, -24.94) * mm, "radius": 0.5 * mm});
            skCircle(sketch, "E85.70.0", {"center": v(5.42, -24.71) * mm, "radius": 0.5 * mm});
            skCircle(sketch, "E85.71.0", {"center": v(6.6, -24.42) * mm, "radius": 0.5 * mm});
            skCircle(sketch, "E85.72.0", {"center": v(7.76, -24.08) * mm, "radius": 0.5 * mm});
            skCircle(sketch, "E85.73.0", {"center": v(8.9, -23.68) * mm, "radius": 0.5 * mm});
            skCircle(sketch, "E85.74.0", {"center": v(10.03, -23.23) * mm, "radius": 0.5 * mm});
            skCircle(sketch, "E85.75.0", {"center": v(11.13, -22.72) * mm, "radius": 0.5 * mm});
            skCircle(sketch, "E85.76.0", {"center": v(12.2, -22.16) * mm, "radius": 0.5 * mm});
            skCircle(sketch, "E85.77.0", {"center": v(13.26, -21.55) * mm, "radius": 0.5 * mm});
            skCircle(sketch, "E85.78.0", {"center": v(14.28, -20.89) * mm, "radius": 0.5 * mm});
            skCircle(sketch, "E85.79.0", {"center": v(15.26, -20.18) * mm, "radius": 0.5 * mm});
            skCircle(sketch, "E85.80.0", {"center": v(16.21, -19.42) * mm, "radius": 0.5 * mm});
            skCircle(sketch, "E85.81.0", {"center": v(17.12, -18.62) * mm, "radius": 0.5 * mm});
            skCircle(sketch, "E85.82.0", {"center": v(18, -17.78) * mm, "radius": 0.5 * mm});
            skCircle(sketch, "E85.83.0", {"center": v(18.83, -16.9) * mm, "radius": 0.5 * mm});
            skCircle(sketch, "E85.84.0", {"center": v(19.62, -15.98) * mm, "radius": 0.5 * mm});
            skCircle(sketch, "E85.85.0", {"center": v(20.36, -15.02) * mm, "radius": 0.5 * mm});
            skCircle(sketch, "E85.86.0", {"center": v(21.06, -14.02) * mm, "radius": 0.5 * mm});
            skCircle(sketch, "E85.87.0", {"center": v(21.7, -13) * mm, "radius": 0.5 * mm});
            skCircle(sketch, "E85.88.0", {"center": v(22.3, -11.94) * mm, "radius": 0.5 * mm});
            skCircle(sketch, "E85.89.0", {"center": v(22.85, -10.86) * mm, "radius": 0.5 * mm});
            skCircle(sketch, "E85.90.0", {"center": v(23.35, -9.75) * mm, "radius": 0.5 * mm});
            skCircle(sketch, "E85.91.0", {"center": v(23.79, -8.62) * mm, "radius": 0.5 * mm});
            skCircle(sketch, "E85.92.0", {"center": v(24.17, -7.47) * mm, "radius": 0.5 * mm});
            skCircle(sketch, "E85.93.0", {"center": v(24.5, -6.3) * mm, "radius": 0.5 * mm});
            skCircle(sketch, "E85.94.0", {"center": v(24.78, -5.12) * mm, "radius": 0.5 * mm});
            skCircle(sketch, "E85.95.0", {"center": v(25, -3.93) * mm, "radius": 0.5 * mm});
            skCircle(sketch, "E85.96.0", {"center": v(25.15, -2.73) * mm, "radius": 0.5 * mm});
            skCircle(sketch, "E85.97.0", {"center": v(25.25, -1.52) * mm, "radius": 0.5 * mm});
            skCircle(sketch, "E85.98.0", {"center": v(25.3, -0.3) * mm, "radius": 0.5 * mm});
            skCircle(sketch, "E85.99.0", {"center": v(25.28, 0.9) * mm, "radius": 0.5 * mm});
            skCircle(sketch, "E85.100.0", {"center": v(25.21, 2.12) * mm, "radius": 0.5 * mm});
            skCircle(sketch, "E85.101.0", {"center": v(25.08, 3.33) * mm, "radius": 0.5 * mm});
            skCircle(sketch, "E85.102.0", {"center": v(24.9, 4.53) * mm, "radius": 0.5 * mm});
            skCircle(sketch, "E85.103.0", {"center": v(24.65, 5.71) * mm, "radius": 0.5 * mm});
            skCircle(sketch, "E85.104.0", {"center": v(24.34, 6.89) * mm, "radius": 0.5 * mm});
            skCircle(sketch, "E85.105.0", {"center": v(23.99, 8.05) * mm, "radius": 0.5 * mm});
            skCircle(sketch, "E85.106.0", {"center": v(23.57, 9.19) * mm, "radius": 0.5 * mm});
            skCircle(sketch, "E85.107.0", {"center": v(23.1, 10.3) * mm, "radius": 0.5 * mm});
            skCircle(sketch, "E85.108.0", {"center": v(22.58, 11.4) * mm, "radius": 0.5 * mm});
            skCircle(sketch, "E85.109.0", {"center": v(22.01, 12.47) * mm, "radius": 0.5 * mm});
            skCircle(sketch, "E85.110.0", {"center": v(21.39, 13.52) * mm, "radius": 0.5 * mm});
            skCircle(sketch, "E85.111.0", {"center": v(20.71, 14.53) * mm, "radius": 0.5 * mm});
            skCircle(sketch, "E85.112.0", {"center": v(20, 15.5) * mm, "radius": 0.5 * mm});
            skCircle(sketch, "E85.113.0", {"center": v(19.23, 16.44) * mm, "radius": 0.5 * mm});
            skCircle(sketch, "E85.114.0", {"center": v(18.42, 17.35) * mm, "radius": 0.5 * mm});
            skCircle(sketch, "E85.115.0", {"center": v(17.57, 18.2) * mm, "radius": 0.5 * mm});
            skCircle(sketch, "E85.116.0", {"center": v(16.67, 19.03) * mm, "radius": 0.5 * mm});
            skCircle(sketch, "E85.117.0", {"center": v(15.74, 19.8) * mm, "radius": 0.5 * mm});
            skCircle(sketch, "E85.118.0", {"center": v(14.77, 20.54) * mm, "radius": 0.5 * mm});
            skCircle(sketch, "E85.119.0", {"center": v(13.77, 21.22) * mm, "radius": 0.5 * mm});
            skCircle(sketch, "E85.120.0", {"center": v(12.74, 21.86) * mm, "radius": 0.5 * mm});
            skCircle(sketch, "E85.121.0", {"center": v(11.67, 22.45) * mm, "radius": 0.5 * mm});
            skCircle(sketch, "E85.122.0", {"center": v(10.59, 22.98) * mm, "radius": 0.5 * mm});
            skCircle(sketch, "E85.123.0", {"center": v(9.47, 23.46) * mm, "radius": 0.5 * mm});
            skCircle(sketch, "E85.124.0", {"center": v(8.34, 23.89) * mm, "radius": 0.5 * mm});
            skCircle(sketch, "E85.125.0", {"center": v(7.18, 24.26) * mm, "radius": 0.5 * mm});
            skCircle(sketch, "E85.126.0", {"center": v(6, 24.58) * mm, "radius": 0.5 * mm});
            skCircle(sketch, "E85.127.0", {"center": v(4.82, 24.84) * mm, "radius": 0.5 * mm});
            skCircle(sketch, "E85.128.0", {"center": v(3.63, 25.04) * mm, "radius": 0.5 * mm});
            skCircle(sketch, "E85.129.0", {"center": v(2.42, 25.18) * mm, "radius": 0.5 * mm});
            skCircle(sketch, "E85.130.0", {"center": v(1.21, 25.27) * mm, "radius": 0.5 * mm});
            skCircle(sketch, "E86.1.0", {"center": v(-1.21, 26.57) * mm, "radius": 0.5 * mm});
            skCircle(sketch, "E86.2.0", {"center": v(-2.42, 26.49) * mm, "radius": 0.5 * mm});
            skCircle(sketch, "E86.3.0", {"center": v(-3.62, 26.35) * mm, "radius": 0.5 * mm});
            skCircle(sketch, "E86.4.0", {"center": v(-4.82, 26.16) * mm, "radius": 0.5 * mm});
            skCircle(sketch, "E86.5.0", {"center": v(-6, 25.91) * mm, "radius": 0.5 * mm});
            skCircle(sketch, "E86.6.0", {"center": v(-7.18, 25.61) * mm, "radius": 0.5 * mm});
            skCircle(sketch, "E86.7.0", {"center": v(-8.33, 25.26) * mm, "radius": 0.5 * mm});
            skCircle(sketch, "E86.8.0", {"center": v(-9.48, 24.85) * mm, "radius": 0.5 * mm});
            skCircle(sketch, "E86.9.0", {"center": v(-10.6, 24.4) * mm, "radius": 0.5 * mm});
            skCircle(sketch, "E86.10.0", {"center": v(-11.7, 23.9) * mm, "radius": 0.5 * mm});
            skCircle(sketch, "E86.11.0", {"center": v(-12.77, 23.33) * mm, "radius": 0.5 * mm});
            skCircle(sketch, "E86.12.0", {"center": v(-13.82, 22.73) * mm, "radius": 0.5 * mm});
            skCircle(sketch, "E86.13.0", {"center": v(-14.84, 22.07) * mm, "radius": 0.5 * mm});
            skCircle(sketch, "E86.14.0", {"center": v(-15.83, 21.38) * mm, "radius": 0.5 * mm});
            skCircle(sketch, "E86.15.0", {"center": v(-16.79, 20.63) * mm, "radius": 0.5 * mm});
            skCircle(sketch, "E86.16.0", {"center": v(-17.7, 19.85) * mm, "radius": 0.5 * mm});
            skCircle(sketch, "E86.17.0", {"center": v(-18.6, 19.02) * mm, "radius": 0.5 * mm});
            skCircle(sketch, "E86.18.0", {"center": v(-19.44, 18.16) * mm, "radius": 0.5 * mm});
            skCircle(sketch, "E86.19.0", {"center": v(-20.25, 17.25) * mm, "radius": 0.5 * mm});
            skCircle(sketch, "E86.20.0", {"center": v(-21.01, 16.31) * mm, "radius": 0.5 * mm});
            skCircle(sketch, "E86.21.0", {"center": v(-21.73, 15.34) * mm, "radius": 0.5 * mm});
            skCircle(sketch, "E86.22.0", {"center": v(-22.4, 14.33) * mm, "radius": 0.5 * mm});
            skCircle(sketch, "E86.23.0", {"center": v(-23.04, 13.3) * mm, "radius": 0.5 * mm});
            skCircle(sketch, "E86.24.0", {"center": v(-23.62, 12.24) * mm, "radius": 0.5 * mm});
            skCircle(sketch, "E86.25.0", {"center": v(-24.15, 11.15) * mm, "radius": 0.5 * mm});
            skCircle(sketch, "E86.26.0", {"center": v(-24.63, 10.04) * mm, "radius": 0.5 * mm});
            skCircle(sketch, "E86.27.0", {"center": v(-25.06, 8.9) * mm, "radius": 0.5 * mm});
            skCircle(sketch, "E86.28.0", {"center": v(-25.44, 7.76) * mm, "radius": 0.5 * mm});
            skCircle(sketch, "E86.29.0", {"center": v(-25.77, 6.6) * mm, "radius": 0.5 * mm});
            skCircle(sketch, "E86.30.0", {"center": v(-26.04, 5.41) * mm, "radius": 0.5 * mm});
            skCircle(sketch, "E86.31.0", {"center": v(-26.26, 4.22) * mm, "radius": 0.5 * mm});
            skCircle(sketch, "E86.32.0", {"center": v(-26.43, 3.02) * mm, "radius": 0.5 * mm});
            skCircle(sketch, "E86.33.0", {"center": v(-26.54, 1.82) * mm, "radius": 0.5 * mm});
            skCircle(sketch, "E86.34.0", {"center": v(-26.6, 0.6) * mm, "radius": 0.5 * mm});
            skCircle(sketch, "E86.35.0", {"center": v(-26.6, -0.6) * mm, "radius": 0.5 * mm});
            skCircle(sketch, "E86.36.0", {"center": v(-26.54, -1.82) * mm, "radius": 0.5 * mm});
            skCircle(sketch, "E86.37.0", {"center": v(-26.43, -3.02) * mm, "radius": 0.5 * mm});
            skCircle(sketch, "E86.38.0", {"center": v(-26.26, -4.22) * mm, "radius": 0.5 * mm});
            skCircle(sketch, "E86.39.0", {"center": v(-26.04, -5.41) * mm, "radius": 0.5 * mm});
            skCircle(sketch, "E86.40.0", {"center": v(-25.77, -6.6) * mm, "radius": 0.5 * mm});
            skCircle(sketch, "E86.41.0", {"center": v(-25.44, -7.76) * mm, "radius": 0.5 * mm});
            skCircle(sketch, "E86.42.0", {"center": v(-25.06, -8.9) * mm, "radius": 0.5 * mm});
            skCircle(sketch, "E86.43.0", {"center": v(-24.63, -10.04) * mm, "radius": 0.5 * mm});
            skCircle(sketch, "E86.44.0", {"center": v(-24.15, -11.15) * mm, "radius": 0.5 * mm});
            skCircle(sketch, "E86.45.0", {"center": v(-23.62, -12.24) * mm, "radius": 0.5 * mm});
            skCircle(sketch, "E86.46.0", {"center": v(-23.04, -13.3) * mm, "radius": 0.5 * mm});
            skCircle(sketch, "E86.47.0", {"center": v(-22.4, -14.33) * mm, "radius": 0.5 * mm});
            skCircle(sketch, "E86.48.0", {"center": v(-21.73, -15.34) * mm, "radius": 0.5 * mm});
            skCircle(sketch, "E86.49.0", {"center": v(-21.01, -16.31) * mm, "radius": 0.5 * mm});
            skCircle(sketch, "E86.50.0", {"center": v(-20.25, -17.25) * mm, "radius": 0.5 * mm});
            skCircle(sketch, "E86.51.0", {"center": v(-19.44, -18.16) * mm, "radius": 0.5 * mm});
            skCircle(sketch, "E86.52.0", {"center": v(-18.6, -19.02) * mm, "radius": 0.5 * mm});
            skCircle(sketch, "E86.53.0", {"center": v(-17.7, -19.85) * mm, "radius": 0.5 * mm});
            skCircle(sketch, "E86.54.0", {"center": v(-16.79, -20.63) * mm, "radius": 0.5 * mm});
            skCircle(sketch, "E86.55.0", {"center": v(-15.83, -21.38) * mm, "radius": 0.5 * mm});
            skCircle(sketch, "E86.56.0", {"center": v(-14.84, -22.07) * mm, "radius": 0.5 * mm});
            skCircle(sketch, "E86.57.0", {"center": v(-13.82, -22.73) * mm, "radius": 0.5 * mm});
            skCircle(sketch, "E86.58.0", {"center": v(-12.77, -23.33) * mm, "radius": 0.5 * mm});
            skCircle(sketch, "E86.59.0", {"center": v(-11.7, -23.9) * mm, "radius": 0.5 * mm});
            skCircle(sketch, "E86.60.0", {"center": v(-10.6, -24.4) * mm, "radius": 0.5 * mm});
            skCircle(sketch, "E86.61.0", {"center": v(-9.48, -24.85) * mm, "radius": 0.5 * mm});
            skCircle(sketch, "E86.62.0", {"center": v(-8.33, -25.26) * mm, "radius": 0.5 * mm});
            skCircle(sketch, "E86.63.0", {"center": v(-7.18, -25.61) * mm, "radius": 0.5 * mm});
            skCircle(sketch, "E86.64.0", {"center": v(-6, -25.91) * mm, "radius": 0.5 * mm});
            skCircle(sketch, "E86.65.0", {"center": v(-4.82, -26.16) * mm, "radius": 0.5 * mm});
            skCircle(sketch, "E86.66.0", {"center": v(-3.62, -26.35) * mm, "radius": 0.5 * mm});
            skCircle(sketch, "E86.67.0", {"center": v(-2.42, -26.49) * mm, "radius": 0.5 * mm});
            skCircle(sketch, "E86.68.0", {"center": v(-1.21, -26.57) * mm, "radius": 0.5 * mm});
            skCircle(sketch, "E86.69.0", {"center": v(0, -26.6) * mm, "radius": 0.5 * mm});
            skCircle(sketch, "E86.70.0", {"center": v(1.21, -26.57) * mm, "radius": 0.5 * mm});
            skCircle(sketch, "E86.71.0", {"center": v(2.42, -26.49) * mm, "radius": 0.5 * mm});
            skCircle(sketch, "E86.72.0", {"center": v(3.62, -26.35) * mm, "radius": 0.5 * mm});
            skCircle(sketch, "E86.73.0", {"center": v(4.82, -26.16) * mm, "radius": 0.5 * mm});
            skCircle(sketch, "E86.74.0", {"center": v(6, -25.91) * mm, "radius": 0.5 * mm});
            skCircle(sketch, "E86.75.0", {"center": v(7.18, -25.61) * mm, "radius": 0.5 * mm});
            skCircle(sketch, "E86.76.0", {"center": v(8.33, -25.26) * mm, "radius": 0.5 * mm});
            skCircle(sketch, "E86.77.0", {"center": v(9.48, -24.85) * mm, "radius": 0.5 * mm});
            skCircle(sketch, "E86.78.0", {"center": v(10.6, -24.4) * mm, "radius": 0.5 * mm});
            skCircle(sketch, "E86.79.0", {"center": v(11.7, -23.9) * mm, "radius": 0.5 * mm});
            skCircle(sketch, "E86.80.0", {"center": v(12.77, -23.33) * mm, "radius": 0.5 * mm});
            skCircle(sketch, "E86.81.0", {"center": v(13.82, -22.73) * mm, "radius": 0.5 * mm});
            skCircle(sketch, "E86.82.0", {"center": v(14.84, -22.07) * mm, "radius": 0.5 * mm});
            skCircle(sketch, "E86.83.0", {"center": v(15.83, -21.38) * mm, "radius": 0.5 * mm});
            skCircle(sketch, "E86.84.0", {"center": v(16.79, -20.63) * mm, "radius": 0.5 * mm});
            skCircle(sketch, "E86.85.0", {"center": v(17.7, -19.85) * mm, "radius": 0.5 * mm});
            skCircle(sketch, "E86.86.0", {"center": v(18.6, -19.02) * mm, "radius": 0.5 * mm});
            skCircle(sketch, "E86.87.0", {"center": v(19.44, -18.16) * mm, "radius": 0.5 * mm});
            skCircle(sketch, "E86.88.0", {"center": v(20.25, -17.25) * mm, "radius": 0.5 * mm});
            skCircle(sketch, "E86.89.0", {"center": v(21.01, -16.31) * mm, "radius": 0.5 * mm});
            skCircle(sketch, "E86.90.0", {"center": v(21.73, -15.34) * mm, "radius": 0.5 * mm});
            skCircle(sketch, "E86.91.0", {"center": v(22.4, -14.33) * mm, "radius": 0.5 * mm});
            skCircle(sketch, "E86.92.0", {"center": v(23.04, -13.3) * mm, "radius": 0.5 * mm});
            skCircle(sketch, "E86.93.0", {"center": v(23.62, -12.24) * mm, "radius": 0.5 * mm});
            skCircle(sketch, "E86.94.0", {"center": v(24.15, -11.15) * mm, "radius": 0.5 * mm});
            skCircle(sketch, "E86.95.0", {"center": v(24.63, -10.04) * mm, "radius": 0.5 * mm});
            skCircle(sketch, "E86.96.0", {"center": v(25.06, -8.9) * mm, "radius": 0.5 * mm});
            skCircle(sketch, "E86.97.0", {"center": v(25.44, -7.76) * mm, "radius": 0.5 * mm});
            skCircle(sketch, "E86.98.0", {"center": v(25.77, -6.6) * mm, "radius": 0.5 * mm});
            skCircle(sketch, "E86.99.0", {"center": v(26.04, -5.41) * mm, "radius": 0.5 * mm});
            skCircle(sketch, "E86.100.0", {"center": v(26.26, -4.22) * mm, "radius": 0.5 * mm});
            skCircle(sketch, "E86.101.0", {"center": v(26.43, -3.02) * mm, "radius": 0.5 * mm});
            skCircle(sketch, "E86.102.0", {"center": v(26.54, -1.82) * mm, "radius": 0.5 * mm});
            skCircle(sketch, "E86.103.0", {"center": v(26.6, -0.6) * mm, "radius": 0.5 * mm});
            skCircle(sketch, "E86.104.0", {"center": v(26.6, 0.6) * mm, "radius": 0.5 * mm});
            skCircle(sketch, "E86.105.0", {"center": v(26.54, 1.82) * mm, "radius": 0.5 * mm});
            skCircle(sketch, "E86.106.0", {"center": v(26.43, 3.02) * mm, "radius": 0.5 * mm});
            skCircle(sketch, "E86.107.0", {"center": v(26.26, 4.22) * mm, "radius": 0.5 * mm});
            skCircle(sketch, "E86.108.0", {"center": v(26.04, 5.41) * mm, "radius": 0.5 * mm});
            skCircle(sketch, "E86.109.0", {"center": v(25.77, 6.6) * mm, "radius": 0.5 * mm});
            skCircle(sketch, "E86.110.0", {"center": v(25.44, 7.76) * mm, "radius": 0.5 * mm});
            skCircle(sketch, "E86.111.0", {"center": v(25.06, 8.9) * mm, "radius": 0.5 * mm});
            skCircle(sketch, "E86.112.0", {"center": v(24.63, 10.04) * mm, "radius": 0.5 * mm});
            skCircle(sketch, "E86.113.0", {"center": v(24.15, 11.15) * mm, "radius": 0.5 * mm});
            skCircle(sketch, "E86.114.0", {"center": v(23.62, 12.24) * mm, "radius": 0.5 * mm});
            skCircle(sketch, "E86.115.0", {"center": v(23.04, 13.3) * mm, "radius": 0.5 * mm});
            skCircle(sketch, "E86.116.0", {"center": v(22.4, 14.33) * mm, "radius": 0.5 * mm});
            skCircle(sketch, "E86.117.0", {"center": v(21.73, 15.34) * mm, "radius": 0.5 * mm});
            skCircle(sketch, "E86.118.0", {"center": v(21.01, 16.31) * mm, "radius": 0.5 * mm});
            skCircle(sketch, "E86.119.0", {"center": v(20.25, 17.25) * mm, "radius": 0.5 * mm});
            skCircle(sketch, "E86.120.0", {"center": v(19.44, 18.16) * mm, "radius": 0.5 * mm});
            skCircle(sketch, "E86.121.0", {"center": v(18.6, 19.02) * mm, "radius": 0.5 * mm});
            skCircle(sketch, "E86.122.0", {"center": v(17.7, 19.85) * mm, "radius": 0.5 * mm});
            skCircle(sketch, "E86.123.0", {"center": v(16.79, 20.63) * mm, "radius": 0.5 * mm});
            skCircle(sketch, "E86.124.0", {"center": v(15.83, 21.38) * mm, "radius": 0.5 * mm});
            skCircle(sketch, "E86.125.0", {"center": v(14.84, 22.07) * mm, "radius": 0.5 * mm});
            skCircle(sketch, "E86.126.0", {"center": v(13.82, 22.73) * mm, "radius": 0.5 * mm});
            skCircle(sketch, "E86.127.0", {"center": v(12.77, 23.33) * mm, "radius": 0.5 * mm});
            skCircle(sketch, "E86.128.0", {"center": v(11.7, 23.9) * mm, "radius": 0.5 * mm});
            skCircle(sketch, "E86.129.0", {"center": v(10.6, 24.4) * mm, "radius": 0.5 * mm});
            skCircle(sketch, "E86.130.0", {"center": v(9.48, 24.85) * mm, "radius": 0.5 * mm});
            skCircle(sketch, "E86.131.0", {"center": v(8.33, 25.26) * mm, "radius": 0.5 * mm});
            skCircle(sketch, "E86.132.0", {"center": v(7.18, 25.61) * mm, "radius": 0.5 * mm});
            skCircle(sketch, "E86.133.0", {"center": v(6, 25.91) * mm, "radius": 0.5 * mm});
            skCircle(sketch, "E86.134.0", {"center": v(4.82, 26.16) * mm, "radius": 0.5 * mm});
            skCircle(sketch, "E86.135.0", {"center": v(3.62, 26.35) * mm, "radius": 0.5 * mm});
            skCircle(sketch, "E86.136.0", {"center": v(2.42, 26.49) * mm, "radius": 0.5 * mm});
            skCircle(sketch, "E86.137.0", {"center": v(1.21, 26.57) * mm, "radius": 0.5 * mm});
            skCircle(sketch, "E87.1.0", {"center": v(-1.2, 27.87) * mm, "radius": 0.5 * mm});
            skCircle(sketch, "E87.2.0", {"center": v(-2.41, 27.8) * mm, "radius": 0.5 * mm});
            skCircle(sketch, "E87.3.0", {"center": v(-3.62, 27.66) * mm, "radius": 0.5 * mm});
            skCircle(sketch, "E87.4.0", {"center": v(-4.81, 27.48) * mm, "radius": 0.5 * mm});
            skCircle(sketch, "E87.5.0", {"center": v(-6, 27.25) * mm, "radius": 0.5 * mm});
            skCircle(sketch, "E87.6.0", {"center": v(-7.17, 26.96) * mm, "radius": 0.5 * mm});
            skCircle(sketch, "E87.7.0", {"center": v(-8.33, 26.63) * mm, "radius": 0.5 * mm});
            skCircle(sketch, "E87.8.0", {"center": v(-9.48, 26.24) * mm, "radius": 0.5 * mm});
            skCircle(sketch, "E87.9.0", {"center": v(-10.6, 25.8) * mm, "radius": 0.5 * mm});
            skCircle(sketch, "E87.10.0", {"center": v(-11.71, 25.32) * mm, "radius": 0.5 * mm});
            skCircle(sketch, "E87.11.0", {"center": v(-12.8, 24.8) * mm, "radius": 0.5 * mm});
            skCircle(sketch, "E87.12.0", {"center": v(-13.86, 24.21) * mm, "radius": 0.5 * mm});
            skCircle(sketch, "E87.13.0", {"center": v(-14.9, 23.59) * mm, "radius": 0.5 * mm});
            skCircle(sketch, "E87.14.0", {"center": v(-15.9, 22.92) * mm, "radius": 0.5 * mm});
            skCircle(sketch, "E87.15.0", {"center": v(-16.88, 22.21) * mm, "radius": 0.5 * mm});
            skCircle(sketch, "E87.16.0", {"center": v(-17.83, 21.46) * mm, "radius": 0.5 * mm});
            skCircle(sketch, "E87.17.0", {"center": v(-18.74, 20.67) * mm, "radius": 0.5 * mm});
            skCircle(sketch, "E87.18.0", {"center": v(-19.62, 19.83) * mm, "radius": 0.5 * mm});
            skCircle(sketch, "E87.19.0", {"center": v(-20.46, 18.97) * mm, "radius": 0.5 * mm});
            skCircle(sketch, "E87.20.0", {"center": v(-21.26, 18.06) * mm, "radius": 0.5 * mm});
            skCircle(sketch, "E87.21.0", {"center": v(-22.03, 17.12) * mm, "radius": 0.5 * mm});
            skCircle(sketch, "E87.22.0", {"center": v(-22.75, 16.15) * mm, "radius": 0.5 * mm});
            skCircle(sketch, "E87.23.0", {"center": v(-23.43, 15.15) * mm, "radius": 0.5 * mm});
            skCircle(sketch, "E87.24.0", {"center": v(-24.06, 14.12) * mm, "radius": 0.5 * mm});
            skCircle(sketch, "E87.25.0", {"center": v(-24.65, 13.07) * mm, "radius": 0.5 * mm});
            skCircle(sketch, "E87.26.0", {"center": v(-25.2, 11.99) * mm, "radius": 0.5 * mm});
            skCircle(sketch, "E87.27.0", {"center": v(-25.69, 10.89) * mm, "radius": 0.5 * mm});
            skCircle(sketch, "E87.28.0", {"center": v(-26.14, 9.76) * mm, "radius": 0.5 * mm});
            skCircle(sketch, "E87.29.0", {"center": v(-26.53, 8.62) * mm, "radius": 0.5 * mm});
            skCircle(sketch, "E87.30.0", {"center": v(-26.88, 7.46) * mm, "radius": 0.5 * mm});
            skCircle(sketch, "E87.31.0", {"center": v(-27.18, 6.3) * mm, "radius": 0.5 * mm});
            skCircle(sketch, "E87.32.0", {"center": v(-27.43, 5.1) * mm, "radius": 0.5 * mm});
            skCircle(sketch, "E87.33.0", {"center": v(-27.62, 3.92) * mm, "radius": 0.5 * mm});
            skCircle(sketch, "E87.34.0", {"center": v(-27.77, 2.72) * mm, "radius": 0.5 * mm});
            skCircle(sketch, "E87.35.0", {"center": v(-27.86, 1.51) * mm, "radius": 0.5 * mm});
            skCircle(sketch, "E87.36.0", {"center": v(-27.9, 0.3) * mm, "radius": 0.5 * mm});
            skCircle(sketch, "E87.37.0", {"center": v(-27.89, -0.9) * mm, "radius": 0.5 * mm});
            skCircle(sketch, "E87.38.0", {"center": v(-27.82, -2.11) * mm, "radius": 0.5 * mm});
            skCircle(sketch, "E87.39.0", {"center": v(-27.7, -3.32) * mm, "radius": 0.5 * mm});
            skCircle(sketch, "E87.40.0", {"center": v(-27.53, -4.51) * mm, "radius": 0.5 * mm});
            skCircle(sketch, "E87.41.0", {"center": v(-27.31, -5.7) * mm, "radius": 0.5 * mm});
            skCircle(sketch, "E87.42.0", {"center": v(-27.04, -6.88) * mm, "radius": 0.5 * mm});
            skCircle(sketch, "E87.43.0", {"center": v(-26.72, -8.04) * mm, "radius": 0.5 * mm});
            skCircle(sketch, "E87.44.0", {"center": v(-26.34, -9.2) * mm, "radius": 0.5 * mm});
            skCircle(sketch, "E87.45.0", {"center": v(-25.92, -10.33) * mm, "radius": 0.5 * mm});
            skCircle(sketch, "E87.46.0", {"center": v(-25.45, -11.44) * mm, "radius": 0.5 * mm});
            skCircle(sketch, "E87.47.0", {"center": v(-24.93, -12.53) * mm, "radius": 0.5 * mm});
            skCircle(sketch, "E87.48.0", {"center": v(-24.36, -13.6) * mm, "radius": 0.5 * mm});
            skCircle(sketch, "E87.49.0", {"center": v(-23.75, -14.64) * mm, "radius": 0.5 * mm});
            skCircle(sketch, "E87.50.0", {"center": v(-23.1, -15.66) * mm, "radius": 0.5 * mm});
            skCircle(sketch, "E87.51.0", {"center": v(-22.4, -16.64) * mm, "radius": 0.5 * mm});
            skCircle(sketch, "E87.52.0", {"center": v(-21.65, -17.6) * mm, "radius": 0.5 * mm});
            skCircle(sketch, "E87.53.0", {"center": v(-20.87, -18.52) * mm, "radius": 0.5 * mm});
            skCircle(sketch, "E87.54.0", {"center": v(-20.05, -19.4) * mm, "radius": 0.5 * mm});
            skCircle(sketch, "E87.55.0", {"center": v(-19.19, -20.26) * mm, "radius": 0.5 * mm});
            skCircle(sketch, "E87.56.0", {"center": v(-18.3, -21.07) * mm, "radius": 0.5 * mm});
            skCircle(sketch, "E87.57.0", {"center": v(-17.36, -21.84) * mm, "radius": 0.5 * mm});
            skCircle(sketch, "E87.58.0", {"center": v(-16.4, -22.57) * mm, "radius": 0.5 * mm});
            skCircle(sketch, "E87.59.0", {"center": v(-15.4, -23.26) * mm, "radius": 0.5 * mm});
            skCircle(sketch, "E87.60.0", {"center": v(-14.38, -23.9) * mm, "radius": 0.5 * mm});
            skCircle(sketch, "E87.61.0", {"center": v(-13.33, -24.5) * mm, "radius": 0.5 * mm});
            skCircle(sketch, "E87.62.0", {"center": v(-12.26, -25.06) * mm, "radius": 0.5 * mm});
            skCircle(sketch, "E87.63.0", {"center": v(-11.16, -25.57) * mm, "radius": 0.5 * mm});
            skCircle(sketch, "E87.64.0", {"center": v(-10.05, -26.03) * mm, "radius": 0.5 * mm});
            skCircle(sketch, "E87.65.0", {"center": v(-8.9, -26.44) * mm, "radius": 0.5 * mm});
            skCircle(sketch, "E87.66.0", {"center": v(-7.75, -26.8) * mm, "radius": 0.5 * mm});
            skCircle(sketch, "E87.67.0", {"center": v(-6.59, -27.11) * mm, "radius": 0.5 * mm});
            skCircle(sketch, "E87.68.0", {"center": v(-5.4, -27.37) * mm, "radius": 0.5 * mm});
            skCircle(sketch, "E87.69.0", {"center": v(-4.22, -27.58) * mm, "radius": 0.5 * mm});
            skCircle(sketch, "E87.70.0", {"center": v(-3.02, -27.74) * mm, "radius": 0.5 * mm});
            skCircle(sketch, "E87.71.0", {"center": v(-1.81, -27.84) * mm, "radius": 0.5 * mm});
            skCircle(sketch, "E87.72.0", {"center": v(-0.6, -27.9) * mm, "radius": 0.5 * mm});
            skCircle(sketch, "E87.73.0", {"center": v(0.6, -27.9) * mm, "radius": 0.5 * mm});
            skCircle(sketch, "E87.74.0", {"center": v(1.81, -27.84) * mm, "radius": 0.5 * mm});
            skCircle(sketch, "E87.75.0", {"center": v(3.02, -27.74) * mm, "radius": 0.5 * mm});
            skCircle(sketch, "E87.76.0", {"center": v(4.22, -27.58) * mm, "radius": 0.5 * mm});
            skCircle(sketch, "E87.77.0", {"center": v(5.4, -27.37) * mm, "radius": 0.5 * mm});
            skCircle(sketch, "E87.78.0", {"center": v(6.59, -27.11) * mm, "radius": 0.5 * mm});
            skCircle(sketch, "E87.79.0", {"center": v(7.75, -26.8) * mm, "radius": 0.5 * mm});
            skCircle(sketch, "E87.80.0", {"center": v(8.9, -26.44) * mm, "radius": 0.5 * mm});
            skCircle(sketch, "E87.81.0", {"center": v(10.05, -26.03) * mm, "radius": 0.5 * mm});
            skCircle(sketch, "E87.82.0", {"center": v(11.16, -25.57) * mm, "radius": 0.5 * mm});
            skCircle(sketch, "E87.83.0", {"center": v(12.26, -25.06) * mm, "radius": 0.5 * mm});
            skCircle(sketch, "E87.84.0", {"center": v(13.33, -24.5) * mm, "radius": 0.5 * mm});
            skCircle(sketch, "E87.85.0", {"center": v(14.38, -23.9) * mm, "radius": 0.5 * mm});
            skCircle(sketch, "E87.86.0", {"center": v(15.4, -23.26) * mm, "radius": 0.5 * mm});
            skCircle(sketch, "E87.87.0", {"center": v(16.4, -22.57) * mm, "radius": 0.5 * mm});
            skCircle(sketch, "E87.88.0", {"center": v(17.36, -21.84) * mm, "radius": 0.5 * mm});
            skCircle(sketch, "E87.89.0", {"center": v(18.3, -21.07) * mm, "radius": 0.5 * mm});
            skCircle(sketch, "E87.90.0", {"center": v(19.19, -20.26) * mm, "radius": 0.5 * mm});
            skCircle(sketch, "E87.91.0", {"center": v(20.05, -19.4) * mm, "radius": 0.5 * mm});
            skCircle(sketch, "E87.92.0", {"center": v(20.87, -18.52) * mm, "radius": 0.5 * mm});
            skCircle(sketch, "E87.93.0", {"center": v(21.65, -17.6) * mm, "radius": 0.5 * mm});
            skCircle(sketch, "E87.94.0", {"center": v(22.4, -16.64) * mm, "radius": 0.5 * mm});
            skCircle(sketch, "E87.95.0", {"center": v(23.1, -15.66) * mm, "radius": 0.5 * mm});
            skCircle(sketch, "E87.96.0", {"center": v(23.75, -14.64) * mm, "radius": 0.5 * mm});
            skCircle(sketch, "E87.97.0", {"center": v(24.36, -13.6) * mm, "radius": 0.5 * mm});
            skCircle(sketch, "E87.98.0", {"center": v(24.93, -12.53) * mm, "radius": 0.5 * mm});
            skCircle(sketch, "E87.99.0", {"center": v(25.45, -11.44) * mm, "radius": 0.5 * mm});
            skCircle(sketch, "E87.100.0", {"center": v(25.92, -10.33) * mm, "radius": 0.5 * mm});
            skCircle(sketch, "E87.101.0", {"center": v(26.34, -9.2) * mm, "radius": 0.5 * mm});
            skCircle(sketch, "E87.102.0", {"center": v(26.72, -8.04) * mm, "radius": 0.5 * mm});
            skCircle(sketch, "E87.103.0", {"center": v(27.04, -6.88) * mm, "radius": 0.5 * mm});
            skCircle(sketch, "E87.104.0", {"center": v(27.31, -5.7) * mm, "radius": 0.5 * mm});
            skCircle(sketch, "E87.105.0", {"center": v(27.53, -4.51) * mm, "radius": 0.5 * mm});
            skCircle(sketch, "E87.106.0", {"center": v(27.7, -3.32) * mm, "radius": 0.5 * mm});
            skCircle(sketch, "E87.107.0", {"center": v(27.82, -2.11) * mm, "radius": 0.5 * mm});
            skCircle(sketch, "E87.108.0", {"center": v(27.89, -0.9) * mm, "radius": 0.5 * mm});
            skCircle(sketch, "E87.109.0", {"center": v(27.9, 0.3) * mm, "radius": 0.5 * mm});
            skCircle(sketch, "E87.110.0", {"center": v(27.86, 1.51) * mm, "radius": 0.5 * mm});
            skCircle(sketch, "E87.111.0", {"center": v(27.77, 2.72) * mm, "radius": 0.5 * mm});
            skCircle(sketch, "E87.112.0", {"center": v(27.62, 3.92) * mm, "radius": 0.5 * mm});
            skCircle(sketch, "E87.113.0", {"center": v(27.43, 5.1) * mm, "radius": 0.5 * mm});
            skCircle(sketch, "E87.114.0", {"center": v(27.18, 6.3) * mm, "radius": 0.5 * mm});
            skCircle(sketch, "E87.115.0", {"center": v(26.88, 7.46) * mm, "radius": 0.5 * mm});
            skCircle(sketch, "E87.116.0", {"center": v(26.53, 8.62) * mm, "radius": 0.5 * mm});
            skCircle(sketch, "E87.117.0", {"center": v(26.14, 9.76) * mm, "radius": 0.5 * mm});
            skCircle(sketch, "E87.118.0", {"center": v(25.69, 10.89) * mm, "radius": 0.5 * mm});
            skCircle(sketch, "E87.119.0", {"center": v(25.2, 11.99) * mm, "radius": 0.5 * mm});
            skCircle(sketch, "E87.120.0", {"center": v(24.65, 13.07) * mm, "radius": 0.5 * mm});
            skCircle(sketch, "E87.121.0", {"center": v(24.06, 14.12) * mm, "radius": 0.5 * mm});
            skCircle(sketch, "E87.122.0", {"center": v(23.43, 15.15) * mm, "radius": 0.5 * mm});
            skCircle(sketch, "E87.123.0", {"center": v(22.75, 16.15) * mm, "radius": 0.5 * mm});
            skCircle(sketch, "E87.124.0", {"center": v(22.03, 17.12) * mm, "radius": 0.5 * mm});
            skCircle(sketch, "E87.125.0", {"center": v(21.26, 18.06) * mm, "radius": 0.5 * mm});
            skCircle(sketch, "E87.126.0", {"center": v(20.46, 18.97) * mm, "radius": 0.5 * mm});
            skCircle(sketch, "E87.127.0", {"center": v(19.62, 19.83) * mm, "radius": 0.5 * mm});
            skCircle(sketch, "E87.128.0", {"center": v(18.74, 20.67) * mm, "radius": 0.5 * mm});
            skCircle(sketch, "E87.129.0", {"center": v(17.83, 21.46) * mm, "radius": 0.5 * mm});
            skCircle(sketch, "E87.130.0", {"center": v(16.88, 22.21) * mm, "radius": 0.5 * mm});
            skCircle(sketch, "E87.131.0", {"center": v(15.9, 22.92) * mm, "radius": 0.5 * mm});
            skCircle(sketch, "E87.132.0", {"center": v(14.9, 23.59) * mm, "radius": 0.5 * mm});
            skCircle(sketch, "E87.133.0", {"center": v(13.86, 24.21) * mm, "radius": 0.5 * mm});
            skCircle(sketch, "E87.134.0", {"center": v(12.8, 24.8) * mm, "radius": 0.5 * mm});
            skCircle(sketch, "E87.135.0", {"center": v(11.71, 25.32) * mm, "radius": 0.5 * mm});
            skCircle(sketch, "E87.136.0", {"center": v(10.6, 25.8) * mm, "radius": 0.5 * mm});
            skCircle(sketch, "E87.137.0", {"center": v(9.48, 26.24) * mm, "radius": 0.5 * mm});
            skCircle(sketch, "E87.138.0", {"center": v(8.33, 26.63) * mm, "radius": 0.5 * mm});
            skCircle(sketch, "E87.139.0", {"center": v(7.17, 26.96) * mm, "radius": 0.5 * mm});
            skCircle(sketch, "E87.140.0", {"center": v(6, 27.25) * mm, "radius": 0.5 * mm});
            skCircle(sketch, "E87.141.0", {"center": v(4.81, 27.48) * mm, "radius": 0.5 * mm});
            skCircle(sketch, "E87.142.0", {"center": v(3.62, 27.66) * mm, "radius": 0.5 * mm});
            skCircle(sketch, "E87.143.0", {"center": v(2.41, 27.8) * mm, "radius": 0.5 * mm});
            skCircle(sketch, "E87.144.0", {"center": v(1.2, 27.87) * mm, "radius": 0.5 * mm});
            skCircle(sketch, "E88.1.0", {"center": v(-1.2, 29.18) * mm, "radius": 0.5 * mm});
            skCircle(sketch, "E88.2.0", {"center": v(-2.41, 29.1) * mm, "radius": 0.5 * mm});
            skCircle(sketch, "E88.3.0", {"center": v(-3.61, 28.98) * mm, "radius": 0.5 * mm});
            skCircle(sketch, "E88.4.0", {"center": v(-4.8, 28.8) * mm, "radius": 0.5 * mm});
            skCircle(sketch, "E88.5.0", {"center": v(-6, 28.58) * mm, "radius": 0.5 * mm});
            skCircle(sketch, "E88.6.0", {"center": v(-7.17, 28.3) * mm, "radius": 0.5 * mm});
            skCircle(sketch, "E88.7.0", {"center": v(-8.33, 27.99) * mm, "radius": 0.5 * mm});
            skCircle(sketch, "E88.8.0", {"center": v(-9.48, 27.62) * mm, "radius": 0.5 * mm});
            skCircle(sketch, "E88.9.0", {"center": v(-10.61, 27.2) * mm, "radius": 0.5 * mm});
            skCircle(sketch, "E88.10.0", {"center": v(-11.73, 26.74) * mm, "radius": 0.5 * mm});
            skCircle(sketch, "E88.11.0", {"center": v(-12.82, 26.23) * mm, "radius": 0.5 * mm});
            skCircle(sketch, "E88.12.0", {"center": v(-13.9, 25.68) * mm, "radius": 0.5 * mm});
            skCircle(sketch, "E88.13.0", {"center": v(-14.95, 25.08) * mm, "radius": 0.5 * mm});
            skCircle(sketch, "E88.14.0", {"center": v(-15.97, 24.45) * mm, "radius": 0.5 * mm});
            skCircle(sketch, "E88.15.0", {"center": v(-16.97, 23.76) * mm, "radius": 0.5 * mm});
            skCircle(sketch, "E88.16.0", {"center": v(-17.94, 23.04) * mm, "radius": 0.5 * mm});
            skCircle(sketch, "E88.17.0", {"center": v(-18.87, 22.28) * mm, "radius": 0.5 * mm});
            skCircle(sketch, "E88.18.0", {"center": v(-19.78, 21.48) * mm, "radius": 0.5 * mm});
            skCircle(sketch, "E88.19.0", {"center": v(-20.65, 20.65) * mm, "radius": 0.5 * mm});
            skCircle(sketch, "E88.20.0", {"center": v(-21.48, 19.78) * mm, "radius": 0.5 * mm});
            skCircle(sketch, "E88.21.0", {"center": v(-22.28, 18.87) * mm, "radius": 0.5 * mm});
            skCircle(sketch, "E88.22.0", {"center": v(-23.04, 17.94) * mm, "radius": 0.5 * mm});
            skCircle(sketch, "E88.23.0", {"center": v(-23.76, 16.97) * mm, "radius": 0.5 * mm});
            skCircle(sketch, "E88.24.0", {"center": v(-24.45, 15.97) * mm, "radius": 0.5 * mm});
            skCircle(sketch, "E88.25.0", {"center": v(-25.08, 14.95) * mm, "radius": 0.5 * mm});
            skCircle(sketch, "E88.26.0", {"center": v(-25.68, 13.9) * mm, "radius": 0.5 * mm});
            skCircle(sketch, "E88.27.0", {"center": v(-26.23, 12.82) * mm, "radius": 0.5 * mm});
            skCircle(sketch, "E88.28.0", {"center": v(-26.74, 11.73) * mm, "radius": 0.5 * mm});
            skCircle(sketch, "E88.29.0", {"center": v(-27.2, 10.61) * mm, "radius": 0.5 * mm});
            skCircle(sketch, "E88.30.0", {"center": v(-27.62, 9.48) * mm, "radius": 0.5 * mm});
            skCircle(sketch, "E88.31.0", {"center": v(-27.99, 8.33) * mm, "radius": 0.5 * mm});
            skCircle(sketch, "E88.32.0", {"center": v(-28.3, 7.17) * mm, "radius": 0.5 * mm});
            skCircle(sketch, "E88.33.0", {"center": v(-28.58, 6) * mm, "radius": 0.5 * mm});
            skCircle(sketch, "E88.34.0", {"center": v(-28.8, 4.8) * mm, "radius": 0.5 * mm});
            skCircle(sketch, "E88.35.0", {"center": v(-28.98, 3.61) * mm, "radius": 0.5 * mm});
            skCircle(sketch, "E88.36.0", {"center": v(-29.1, 2.41) * mm, "radius": 0.5 * mm});
            skCircle(sketch, "E88.37.0", {"center": v(-29.18, 1.2) * mm, "radius": 0.5 * mm});
            skCircle(sketch, "E88.38.0", {"center": v(-29.2, 0) * mm, "radius": 0.5 * mm});
            skCircle(sketch, "E88.39.0", {"center": v(-29.18, -1.2) * mm, "radius": 0.5 * mm});
            skCircle(sketch, "E88.40.0", {"center": v(-29.1, -2.41) * mm, "radius": 0.5 * mm});
            skCircle(sketch, "E88.41.0", {"center": v(-28.98, -3.61) * mm, "radius": 0.5 * mm});
            skCircle(sketch, "E88.42.0", {"center": v(-28.8, -4.8) * mm, "radius": 0.5 * mm});
            skCircle(sketch, "E88.43.0", {"center": v(-28.58, -6) * mm, "radius": 0.5 * mm});
            skCircle(sketch, "E88.44.0", {"center": v(-28.3, -7.17) * mm, "radius": 0.5 * mm});
            skCircle(sketch, "E88.45.0", {"center": v(-27.99, -8.33) * mm, "radius": 0.5 * mm});
            skCircle(sketch, "E88.46.0", {"center": v(-27.62, -9.48) * mm, "radius": 0.5 * mm});
            skCircle(sketch, "E88.47.0", {"center": v(-27.2, -10.61) * mm, "radius": 0.5 * mm});
            skCircle(sketch, "E88.48.0", {"center": v(-26.74, -11.73) * mm, "radius": 0.5 * mm});
            skCircle(sketch, "E88.49.0", {"center": v(-26.23, -12.82) * mm, "radius": 0.5 * mm});
            skCircle(sketch, "E88.50.0", {"center": v(-25.68, -13.9) * mm, "radius": 0.5 * mm});
            skCircle(sketch, "E88.51.0", {"center": v(-25.08, -14.95) * mm, "radius": 0.5 * mm});
            skCircle(sketch, "E88.52.0", {"center": v(-24.45, -15.97) * mm, "radius": 0.5 * mm});
            skCircle(sketch, "E88.53.0", {"center": v(-23.76, -16.97) * mm, "radius": 0.5 * mm});
            skCircle(sketch, "E88.54.0", {"center": v(-23.04, -17.94) * mm, "radius": 0.5 * mm});
            skCircle(sketch, "E88.55.0", {"center": v(-22.28, -18.87) * mm, "radius": 0.5 * mm});
            skCircle(sketch, "E88.56.0", {"center": v(-21.48, -19.78) * mm, "radius": 0.5 * mm});
            skCircle(sketch, "E88.57.0", {"center": v(-20.65, -20.65) * mm, "radius": 0.5 * mm});
            skCircle(sketch, "E88.58.0", {"center": v(-19.78, -21.48) * mm, "radius": 0.5 * mm});
            skCircle(sketch, "E88.59.0", {"center": v(-18.87, -22.28) * mm, "radius": 0.5 * mm});
            skCircle(sketch, "E88.60.0", {"center": v(-17.94, -23.04) * mm, "radius": 0.5 * mm});
            skCircle(sketch, "E88.61.0", {"center": v(-16.97, -23.76) * mm, "radius": 0.5 * mm});
            skCircle(sketch, "E88.62.0", {"center": v(-15.97, -24.45) * mm, "radius": 0.5 * mm});
            skCircle(sketch, "E88.63.0", {"center": v(-14.95, -25.08) * mm, "radius": 0.5 * mm});
            skCircle(sketch, "E88.64.0", {"center": v(-13.9, -25.68) * mm, "radius": 0.5 * mm});
            skCircle(sketch, "E88.65.0", {"center": v(-12.82, -26.23) * mm, "radius": 0.5 * mm});
            skCircle(sketch, "E88.66.0", {"center": v(-11.73, -26.74) * mm, "radius": 0.5 * mm});
            skCircle(sketch, "E88.67.0", {"center": v(-10.61, -27.2) * mm, "radius": 0.5 * mm});
            skCircle(sketch, "E88.68.0", {"center": v(-9.48, -27.62) * mm, "radius": 0.5 * mm});
            skCircle(sketch, "E88.69.0", {"center": v(-8.33, -27.99) * mm, "radius": 0.5 * mm});
            skCircle(sketch, "E88.70.0", {"center": v(-7.17, -28.3) * mm, "radius": 0.5 * mm});
            skCircle(sketch, "E88.71.0", {"center": v(-6, -28.58) * mm, "radius": 0.5 * mm});
            skCircle(sketch, "E88.72.0", {"center": v(-4.8, -28.8) * mm, "radius": 0.5 * mm});
            skCircle(sketch, "E88.73.0", {"center": v(-3.61, -28.98) * mm, "radius": 0.5 * mm});
            skCircle(sketch, "E88.74.0", {"center": v(-2.41, -29.1) * mm, "radius": 0.5 * mm});
            skCircle(sketch, "E88.75.0", {"center": v(-1.2, -29.18) * mm, "radius": 0.5 * mm});
            skCircle(sketch, "E88.76.0", {"center": v(0, -29.2) * mm, "radius": 0.5 * mm});
            skCircle(sketch, "E88.77.0", {"center": v(1.2, -29.18) * mm, "radius": 0.5 * mm});
            skCircle(sketch, "E88.78.0", {"center": v(2.41, -29.1) * mm, "radius": 0.5 * mm});
            skCircle(sketch, "E88.79.0", {"center": v(3.61, -28.98) * mm, "radius": 0.5 * mm});
            skCircle(sketch, "E88.80.0", {"center": v(4.8, -28.8) * mm, "radius": 0.5 * mm});
            skCircle(sketch, "E88.81.0", {"center": v(6, -28.58) * mm, "radius": 0.5 * mm});
            skCircle(sketch, "E88.82.0", {"center": v(7.17, -28.3) * mm, "radius": 0.5 * mm});
            skCircle(sketch, "E88.83.0", {"center": v(8.33, -27.99) * mm, "radius": 0.5 * mm});
            skCircle(sketch, "E88.84.0", {"center": v(9.48, -27.62) * mm, "radius": 0.5 * mm});
            skCircle(sketch, "E88.85.0", {"center": v(10.61, -27.2) * mm, "radius": 0.5 * mm});
            skCircle(sketch, "E88.86.0", {"center": v(11.73, -26.74) * mm, "radius": 0.5 * mm});
            skCircle(sketch, "E88.87.0", {"center": v(12.82, -26.23) * mm, "radius": 0.5 * mm});
            skCircle(sketch, "E88.88.0", {"center": v(13.9, -25.68) * mm, "radius": 0.5 * mm});
            skCircle(sketch, "E88.89.0", {"center": v(14.95, -25.08) * mm, "radius": 0.5 * mm});
            skCircle(sketch, "E88.90.0", {"center": v(15.97, -24.45) * mm, "radius": 0.5 * mm});
            skCircle(sketch, "E88.91.0", {"center": v(16.97, -23.76) * mm, "radius": 0.5 * mm});
            skCircle(sketch, "E88.92.0", {"center": v(17.94, -23.04) * mm, "radius": 0.5 * mm});
            skCircle(sketch, "E88.93.0", {"center": v(18.87, -22.28) * mm, "radius": 0.5 * mm});
            skCircle(sketch, "E88.94.0", {"center": v(19.78, -21.48) * mm, "radius": 0.5 * mm});
            skCircle(sketch, "E88.95.0", {"center": v(20.65, -20.65) * mm, "radius": 0.5 * mm});
            skCircle(sketch, "E88.96.0", {"center": v(21.48, -19.78) * mm, "radius": 0.5 * mm});
            skCircle(sketch, "E88.97.0", {"center": v(22.28, -18.87) * mm, "radius": 0.5 * mm});
            skCircle(sketch, "E88.98.0", {"center": v(23.04, -17.94) * mm, "radius": 0.5 * mm});
            skCircle(sketch, "E88.99.0", {"center": v(23.76, -16.97) * mm, "radius": 0.5 * mm});
            skCircle(sketch, "E88.100.0", {"center": v(24.45, -15.97) * mm, "radius": 0.5 * mm});
            skCircle(sketch, "E88.101.0", {"center": v(25.08, -14.95) * mm, "radius": 0.5 * mm});
            skCircle(sketch, "E88.102.0", {"center": v(25.68, -13.9) * mm, "radius": 0.5 * mm});
            skCircle(sketch, "E88.103.0", {"center": v(26.23, -12.82) * mm, "radius": 0.5 * mm});
            skCircle(sketch, "E88.104.0", {"center": v(26.74, -11.73) * mm, "radius": 0.5 * mm});
            skCircle(sketch, "E88.105.0", {"center": v(27.2, -10.61) * mm, "radius": 0.5 * mm});
            skCircle(sketch, "E88.106.0", {"center": v(27.62, -9.48) * mm, "radius": 0.5 * mm});
            skCircle(sketch, "E88.107.0", {"center": v(27.99, -8.33) * mm, "radius": 0.5 * mm});
            skCircle(sketch, "E88.108.0", {"center": v(28.3, -7.17) * mm, "radius": 0.5 * mm});
            skCircle(sketch, "E88.109.0", {"center": v(28.58, -6) * mm, "radius": 0.5 * mm});
            skCircle(sketch, "E88.110.0", {"center": v(28.8, -4.8) * mm, "radius": 0.5 * mm});
            skCircle(sketch, "E88.111.0", {"center": v(28.98, -3.61) * mm, "radius": 0.5 * mm});
            skCircle(sketch, "E88.112.0", {"center": v(29.1, -2.41) * mm, "radius": 0.5 * mm});
            skCircle(sketch, "E88.113.0", {"center": v(29.18, -1.2) * mm, "radius": 0.5 * mm});
            skCircle(sketch, "E88.114.0", {"center": v(29.2, 0) * mm, "radius": 0.5 * mm});
            skCircle(sketch, "E88.115.0", {"center": v(29.18, 1.2) * mm, "radius": 0.5 * mm});
            skCircle(sketch, "E88.116.0", {"center": v(29.1, 2.41) * mm, "radius": 0.5 * mm});
            skCircle(sketch, "E88.117.0", {"center": v(28.98, 3.61) * mm, "radius": 0.5 * mm});
            skCircle(sketch, "E88.118.0", {"center": v(28.8, 4.8) * mm, "radius": 0.5 * mm});
            skCircle(sketch, "E88.119.0", {"center": v(28.58, 6) * mm, "radius": 0.5 * mm});
            skCircle(sketch, "E88.120.0", {"center": v(28.3, 7.17) * mm, "radius": 0.5 * mm});
            skCircle(sketch, "E88.121.0", {"center": v(27.99, 8.33) * mm, "radius": 0.5 * mm});
            skCircle(sketch, "E88.122.0", {"center": v(27.62, 9.48) * mm, "radius": 0.5 * mm});
            skCircle(sketch, "E88.123.0", {"center": v(27.2, 10.61) * mm, "radius": 0.5 * mm});
            skCircle(sketch, "E88.124.0", {"center": v(26.74, 11.73) * mm, "radius": 0.5 * mm});
            skCircle(sketch, "E88.125.0", {"center": v(26.23, 12.82) * mm, "radius": 0.5 * mm});
            skCircle(sketch, "E88.126.0", {"center": v(25.68, 13.9) * mm, "radius": 0.5 * mm});
            skCircle(sketch, "E88.127.0", {"center": v(25.08, 14.95) * mm, "radius": 0.5 * mm});
            skCircle(sketch, "E88.128.0", {"center": v(24.45, 15.97) * mm, "radius": 0.5 * mm});
            skCircle(sketch, "E88.129.0", {"center": v(23.76, 16.97) * mm, "radius": 0.5 * mm});
            skCircle(sketch, "E88.130.0", {"center": v(23.04, 17.94) * mm, "radius": 0.5 * mm});
            skCircle(sketch, "E88.131.0", {"center": v(22.28, 18.87) * mm, "radius": 0.5 * mm});
            skCircle(sketch, "E88.132.0", {"center": v(21.48, 19.78) * mm, "radius": 0.5 * mm});
            skCircle(sketch, "E88.133.0", {"center": v(20.65, 20.65) * mm, "radius": 0.5 * mm});
            skCircle(sketch, "E88.134.0", {"center": v(19.78, 21.48) * mm, "radius": 0.5 * mm});
            skCircle(sketch, "E88.135.0", {"center": v(18.87, 22.28) * mm, "radius": 0.5 * mm});
            skCircle(sketch, "E88.136.0", {"center": v(17.94, 23.04) * mm, "radius": 0.5 * mm});
            skCircle(sketch, "E88.137.0", {"center": v(16.97, 23.76) * mm, "radius": 0.5 * mm});
            skCircle(sketch, "E88.138.0", {"center": v(15.97, 24.45) * mm, "radius": 0.5 * mm});
            skCircle(sketch, "E88.139.0", {"center": v(14.95, 25.08) * mm, "radius": 0.5 * mm});
            skCircle(sketch, "E88.140.0", {"center": v(13.9, 25.68) * mm, "radius": 0.5 * mm});
            skCircle(sketch, "E88.141.0", {"center": v(12.82, 26.23) * mm, "radius": 0.5 * mm});
            skCircle(sketch, "E88.142.0", {"center": v(11.73, 26.74) * mm, "radius": 0.5 * mm});
            skCircle(sketch, "E88.143.0", {"center": v(10.61, 27.2) * mm, "radius": 0.5 * mm});
            skCircle(sketch, "E88.144.0", {"center": v(9.48, 27.62) * mm, "radius": 0.5 * mm});
            skCircle(sketch, "E88.145.0", {"center": v(8.33, 27.99) * mm, "radius": 0.5 * mm});
            skCircle(sketch, "E88.146.0", {"center": v(7.17, 28.3) * mm, "radius": 0.5 * mm});
            skCircle(sketch, "E88.147.0", {"center": v(6, 28.58) * mm, "radius": 0.5 * mm});
            skCircle(sketch, "E88.148.0", {"center": v(4.8, 28.8) * mm, "radius": 0.5 * mm});
            skCircle(sketch, "E88.149.0", {"center": v(3.61, 28.98) * mm, "radius": 0.5 * mm});
            skCircle(sketch, "E88.150.0", {"center": v(2.41, 29.1) * mm, "radius": 0.5 * mm});
            skCircle(sketch, "E88.151.0", {"center": v(1.2, 29.18) * mm, "radius": 0.5 * mm});
            skCircle(sketch, "E89", {"center": v(0, 0) * mm, "radius": 30 * mm});
            skSolve(sketch);
        }
        {
            var Q0;
            Q0=makeQuery(id+"F8.imprint","IMPRINT",FACE,{"disambiguationData":[TD([[makeQuery(id+"F8.imprint","IMPRINT",EDGE,{"derivedFrom":sQuery(id+"F8.wireOp",EDGE,"E49")}),-1.0]])]});
            extrude(context, id + "F9", {"entities" : qUnion([Q0]), "operationType" : NewBodyOperationType.ADD, "endBound" : BoundingType.UP_TO_NEXT, "oppositeDirection" : true, "depth" : 1 * mm, "offsetDistance" : 25 * mm, "hasSecondDirection" : true, "secondDirectionOppositeDirection" : false, "secondDirectionDepth" : 2.8 * mm});
        }
    });
